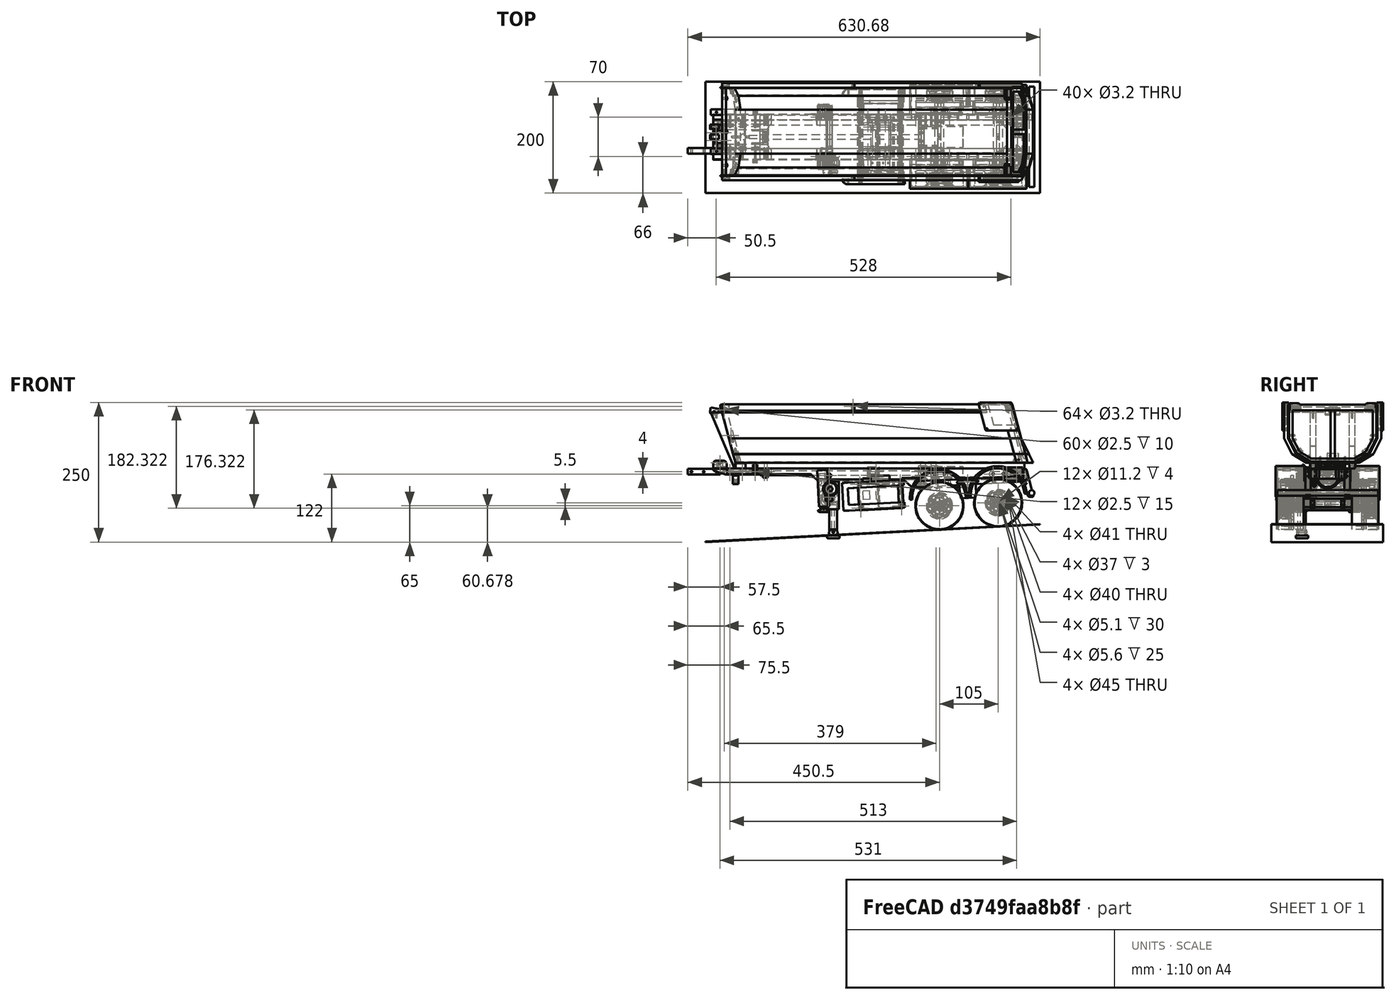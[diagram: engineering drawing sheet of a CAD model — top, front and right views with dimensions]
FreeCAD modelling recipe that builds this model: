
FCSTD DOCUMENT  (FreeCAD 0.19R)
Label: trailer-frame
License: CC-BY 3.0
LicenseURL: http://creativecommons.org/licenses/by/3.0/
objects: Part::Cylinder×595, Part::MultiFuse×465, Part::Box×378, Part::Cut×363, Part::Fillet×122, Part::Chamfer×58, Part::Mirroring×20, Part::Feature×19, Part::Extrusion×10, App::DocumentObjectGroup×8, Part::RegularPolygon×4, Part::Cone×4, Part::Compound×2, Mesh::Feature×1
note: 2040 computed .brp shape members not serialized (recipe doc carries the construction recipe); baked Part::Feature solids carry a one-line shape summary decoded from their .brp

FEATURE [Part::Box] Box
  AttacherType = Attacher::AttachEngine3D
  Height = 20
  Length = 600
  Placement = pos=(0,0,0) rot=(0,1,0;0.05236rad)
  Width = 10
FEATURE [Part::Box] Box001
  AttacherType = Attacher::AttachEngine3D
  Height = 20
  Length = 600
  Placement = pos=(0,52,0) rot=(0,1,0;0.05236rad)
  Width = 10
FEATURE [Part::MultiFuse] Fusion
  Refine = true
  Shapes = -> [Box001,Box]
FEATURE [Part::Fillet] Fillet
  Base = -> Fusion
  Edges = 4 edges r=3: [Edge8,Edge10,Edge17,Edge19]
FEATURE [Part::Box] Box002
  AttacherType = Attacher::AttachEngine3D
  Height = 17
  Length = 200
  Placement = pos=(399,0,-35) rot=(0,0,1;0rad)
  Width = 10
FEATURE [Part::Box] Box003
  AttacherType = Attacher::AttachEngine3D
  Height = 27
  Length = 14
  Placement = pos=(400,0,-35) rot=(0,-1,0;0.785398rad)
  Width = 10
FEATURE [Part::MultiFuse] Fusion001
  Refine = true
  Shapes = -> [Box002,Box003]
FEATURE [Part::MultiFuse] Fusion002
  Refine = true
  Shapes = -> [Box001,Box]
FEATURE [Part::Fillet] Fillet001
  Base = -> Fusion002
  Edges = 4 edges r=3: [Edge8,Edge10,Edge17,Edge19]
FEATURE [Part::Box] Box004
  AttacherType = Attacher::AttachEngine3D
  Height = 27
  Length = 14
  Placement = pos=(400,0,-35) rot=(0,-1,0;0.785398rad)
  Width = 10
FEATURE [Part::Box] Box005
  AttacherType = Attacher::AttachEngine3D
  Height = 17
  Length = 200
  Placement = pos=(399,0,-35) rot=(0,0,1;0rad)
  Width = 10
FEATURE [Part::MultiFuse] Fusion003
  Placement = pos=(0,52,0) rot=(0,0,1;0rad)
  Refine = true
  Shapes = -> [Box005,Box004]
FEATURE [Part::Box] Box006
  AttacherType = Attacher::AttachEngine3D
  Height = 10
  Length = 150
  Placement = pos=(0,0,0) rot=(0,1,0;0.05236rad)
  Width = 62
FEATURE [Part::Box] Box007
  AttacherType = Attacher::AttachEngine3D
  Height = 10
  Length = 20
  Placement = pos=(143.2,0,-4.8) rot=(0,1,0;0.785398rad)
  Width = 62
FEATURE [Part::MultiFuse] Fusion005
  Refine = true
  Shapes = -> [Box007,Box006]
FEATURE [Part::Cut] Cut001
  Base = -> Fillet001
  Placement = pos=(0,0,0) rot=(0,-1,0;0.05236rad)
  Refine = true
  Tool = -> Fusion005
FEATURE [Part::Box] Box008
  AttacherType = Attacher::AttachEngine3D
  Height = 10
  Length = 60
  Placement = pos=(0,1,9) rot=(0,0,1;0rad)
  Width = 60
FEATURE [Part::Cylinder] Cylinder
  Angle = 360
  AttacherType = Attacher::AttachEngine3D
  Height = 19
  Placement = pos=(30,31,6) rot=(0,0,1;0rad)
  Radius = 5
FEATURE [Part::Cylinder] Cylinder001
  Angle = 360
  AttacherType = Attacher::AttachEngine3D
  Height = 51
  Placement = pos=(10,31,10) rot=(0,1,0;1.5708rad)
  Radius = 1.4
FEATURE [Part::Cylinder] Cylinder002
  Angle = 360
  AttacherType = Attacher::AttachEngine3D
  Height = 41
  Placement = pos=(20,31,10) rot=(0,1,0;1.5708rad)
  Radius = 1.6
FEATURE [Part::Cylinder] Cylinder003
  Angle = 360
  AttacherType = Attacher::AttachEngine3D
  Height = 20
  Placement = pos=(41,31,10) rot=(0,1,0;1.5708rad)
  Radius = 2.6
FEATURE [Mesh::Feature] frame_holes  label="frame-holes"
  Placement = pos=(59.5,8,-19) rot=(1,0,0;1.5708rad)
FEATURE [Part::Cylinder] Cylinder004
  Angle = 360
  AttacherType = Attacher::AttachEngine3D
  Height = 15
  Placement = pos=(51,15,14) rot=(1,0,0;1.5708rad)
  Radius = 1.25
FEATURE [Part::Cylinder] Cylinder005
  Angle = 360
  AttacherType = Attacher::AttachEngine3D
  Height = 15
  Placement = pos=(6,15,14) rot=(1,0,0;1.5708rad)
  Radius = 1.25
FEATURE [Part::Cylinder] Cylinder006
  Angle = 360
  AttacherType = Attacher::AttachEngine3D
  Height = 15
  Placement = pos=(28,15,14) rot=(1,0,0;1.5708rad)
  Radius = 1.25
FEATURE [Part::MultiFuse] Fusion007
  Refine = true
  Shapes = -> [Cylinder004,Cylinder005,Cylinder006]
FEATURE [Part::Cylinder] Cylinder007
  Angle = 360
  AttacherType = Attacher::AttachEngine3D
  Height = 15
  Placement = pos=(28,15,14) rot=(1,0,0;1.5708rad)
  Radius = 1.25
FEATURE [Part::Cylinder] Cylinder008
  Angle = 360
  AttacherType = Attacher::AttachEngine3D
  Height = 15
  Placement = pos=(6,15,14) rot=(1,0,0;1.5708rad)
  Radius = 1.25
FEATURE [Part::Cylinder] Cylinder009
  Angle = 360
  AttacherType = Attacher::AttachEngine3D
  Height = 15
  Placement = pos=(51,15,14) rot=(1,0,0;1.5708rad)
  Radius = 1.25
FEATURE [Part::MultiFuse] Fusion008
  Placement = pos=(0,47,0) rot=(0,0,1;0rad)
  Refine = true
  Shapes = -> [Cylinder009,Cylinder008,Cylinder007]
FEATURE [Part::MultiFuse] Fusion009
  Refine = true
  Shapes = -> [Fusion007,Fusion008]
FEATURE [Part::MultiFuse] Fusion010
  Refine = true
  Shapes = -> [Box001,Box]
FEATURE [Part::Fillet] Fillet004
  Base = -> Fusion010
  Edges = 4 edges r=3: [Edge8,Edge10,Edge17,Edge19]
FEATURE [Part::Cut] Cut
  Base = -> Fusion001
  Placement = pos=(0,0,0) rot=(0,-1,0;0.05236rad)
  Refine = true
  Tool = -> Fillet
FEATURE [Part::Cut] Cut006
  Base = -> Fusion003
  Placement = pos=(0,0,0) rot=(0,-1,0;0.05236rad)
  Refine = true
  Tool = -> Fillet004
FEATURE [Part::Box] Box010
  AttacherType = Attacher::AttachEngine3D
  Height = 18
  Length = 600
  Placement = pos=(0,1,1) rot=(0,0,1;0rad)
  Width = 10
FEATURE [Part::Box] Box011
  AttacherType = Attacher::AttachEngine3D
  Height = 18
  Length = 600
  Placement = pos=(0,51,1) rot=(0,0,1;0rad)
  Width = 10
FEATURE [Part::Fillet] Fillet005
  Base = -> Box011
  Edges = 2 edges r=2: [Edge11,Edge12]
FEATURE [Part::Fillet] Fillet006
  Base = -> Box010
  Edges = 2 edges r=2: [Edge9,Edge10]
FEATURE [Part::MultiFuse] Fusion011
  Refine = true
  Shapes = -> [Fillet005,Fillet006]
FEATURE [Part::Cut] Cut007
  Base = -> Cut001
  Refine = true
  Tool = -> Fusion011
FEATURE [Part::Cylinder] Cylinder010
  Angle = 360
  AttacherType = Attacher::AttachEngine3D
  Height = 30
  Placement = pos=(578,6,-35) rot=(0,0,1;0rad)
  Radius = 1.6
FEATURE [Part::Cylinder] Cylinder011
  Angle = 360
  AttacherType = Attacher::AttachEngine3D
  Height = 3
  Placement = pos=(578,6,-35) rot=(0,0,1;0rad)
  Radius = 3.2
FEATURE [Part::MultiFuse] Fusion012
  Placement = pos=(0,0,30) rot=(0,0,1;0rad)
  Refine = true
  Shapes = -> [Cylinder010,Cylinder011]
FEATURE [Part::Cylinder] Cylinder012
  Angle = 360
  AttacherType = Attacher::AttachEngine3D
  Height = 3
  Placement = pos=(578,6,-35) rot=(0,0,1;0rad)
  Radius = 3.2
FEATURE [Part::Cylinder] Cylinder013
  Angle = 360
  AttacherType = Attacher::AttachEngine3D
  Height = 30
  Placement = pos=(578,6,-35) rot=(0,0,1;0rad)
  Radius = 1.6
FEATURE [Part::MultiFuse] Fusion013
  Placement = pos=(-170,0,21.1) rot=(0,0,1;0rad)
  Refine = true
  Shapes = -> [Cylinder013,Cylinder012]
FEATURE [Part::Cylinder] Cylinder014
  Angle = 360
  AttacherType = Attacher::AttachEngine3D
  Height = 3
  Placement = pos=(578,6,-35) rot=(0,0,1;0rad)
  Radius = 3.2
FEATURE [Part::Cylinder] Cylinder015
  Angle = 360
  AttacherType = Attacher::AttachEngine3D
  Height = 30
  Placement = pos=(578,6,-35) rot=(0,0,1;0rad)
  Radius = 1.6
FEATURE [Part::MultiFuse] Fusion014
  Placement = pos=(-110,0,24.3) rot=(0,0,1;0rad)
  Refine = true
  Shapes = -> [Cylinder015,Cylinder014]
FEATURE [Part::Cylinder] Cylinder016
  Angle = 360
  AttacherType = Attacher::AttachEngine3D
  Height = 3
  Placement = pos=(578,6,-35) rot=(0,0,1;0rad)
  Radius = 3.2
FEATURE [Part::Cylinder] Cylinder017
  Angle = 360
  AttacherType = Attacher::AttachEngine3D
  Height = 30
  Placement = pos=(578,6,-35) rot=(0,0,1;0rad)
  Radius = 1.6
FEATURE [Part::MultiFuse] Fusion015
  Placement = pos=(-30,0,28.5) rot=(0,0,1;0rad)
  Refine = true
  Shapes = -> [Cylinder017,Cylinder016]
FEATURE [Part::Cylinder] Cylinder018
  Angle = 360
  AttacherType = Attacher::AttachEngine3D
  Height = 3
  Placement = pos=(578,6,-35) rot=(0,0,1;0rad)
  Radius = 3.2
FEATURE [Part::Cylinder] Cylinder019
  Angle = 360
  AttacherType = Attacher::AttachEngine3D
  Height = 30
  Placement = pos=(578,6,-35) rot=(0,0,1;0rad)
  Radius = 1.6
FEATURE [Part::MultiFuse] Fusion016
  Placement = pos=(0,50,30) rot=(0,0,1;0rad)
  Refine = true
  Shapes = -> [Cylinder019,Cylinder018]
FEATURE [Part::Cylinder] Cylinder020
  Angle = 360
  AttacherType = Attacher::AttachEngine3D
  Height = 3
  Placement = pos=(578,6,-35) rot=(0,0,1;0rad)
  Radius = 3.2
FEATURE [Part::Cylinder] Cylinder021
  Angle = 360
  AttacherType = Attacher::AttachEngine3D
  Height = 30
  Placement = pos=(578,6,-35) rot=(0,0,1;0rad)
  Radius = 1.6
FEATURE [Part::MultiFuse] Fusion017
  Placement = pos=(-170,50,21.1) rot=(0,0,1;0rad)
  Refine = true
  Shapes = -> [Cylinder021,Cylinder020]
FEATURE [Part::Cylinder] Cylinder022
  Angle = 360
  AttacherType = Attacher::AttachEngine3D
  Height = 3
  Placement = pos=(578,6,-35) rot=(0,0,1;0rad)
  Radius = 3.2
FEATURE [Part::Cylinder] Cylinder023
  Angle = 360
  AttacherType = Attacher::AttachEngine3D
  Height = 30
  Placement = pos=(578,6,-35) rot=(0,0,1;0rad)
  Radius = 1.6
FEATURE [Part::MultiFuse] Fusion018
  Placement = pos=(-110,50,24.3) rot=(0,0,1;0rad)
  Refine = true
  Shapes = -> [Cylinder023,Cylinder022]
FEATURE [Part::Cylinder] Cylinder024
  Angle = 360
  AttacherType = Attacher::AttachEngine3D
  Height = 3
  Placement = pos=(578,6,-35) rot=(0,0,1;0rad)
  Radius = 3.2
FEATURE [Part::Cylinder] Cylinder025
  Angle = 360
  AttacherType = Attacher::AttachEngine3D
  Height = 30
  Placement = pos=(578,6,-35) rot=(0,0,1;0rad)
  Radius = 1.6
FEATURE [Part::MultiFuse] Fusion019
  Placement = pos=(-30,50,28.5) rot=(0,0,1;0rad)
  Refine = true
  Shapes = -> [Cylinder025,Cylinder024]
FEATURE [Part::Box] Box012
  AttacherType = Attacher::AttachEngine3D
  Height = 32
  Length = 10
  Placement = pos=(600,0,-3.6) rot=(0,-1,0;0.05236rad)
  Width = 62
FEATURE [Part::Cut] Cut010  label="frame_"
  Base = -> Cut007
  Refine = true
  Tool = -> Box012
FEATURE [Part::Box] Box013
  AttacherType = Attacher::AttachEngine3D
  Height = 17
  Length = 20
  Placement = pos=(580,0,1.5) rot=(0,0,1;0rad)
  Width = 10
FEATURE [Part::Box] Box014
  AttacherType = Attacher::AttachEngine3D
  Height = 32
  Length = 10
  Placement = pos=(600,0,-3.6) rot=(0,-1,0;0.05236rad)
  Width = 62
FEATURE [Part::Cut] Cut011
  Base = -> Box013
  Placement = pos=(0,1,0) rot=(0,0,1;0rad)
  Refine = true
  Tool = -> Box014
FEATURE [Part::Box] Box015
  AttacherType = Attacher::AttachEngine3D
  Height = 32
  Length = 10
  Placement = pos=(600,0,-3.6) rot=(0,-1,0;0.05236rad)
  Width = 62
FEATURE [Part::Box] Box016
  AttacherType = Attacher::AttachEngine3D
  Height = 17
  Length = 20
  Placement = pos=(580,0,1.5) rot=(0,0,1;0rad)
  Width = 10
FEATURE [Part::Cut] Cut012
  Base = -> Box016
  Placement = pos=(0,51,0) rot=(0,0,1;0rad)
  Refine = true
  Tool = -> Box015
FEATURE [Part::Box] Box017
  AttacherType = Attacher::AttachEngine3D
  Height = 17
  Length = 10
  Placement = pos=(580,11,1.5) rot=(0,0,1;0rad)
  Width = 40
FEATURE [Part::MultiFuse] Fusion022
  Refine = true
  Shapes = -> [Cut011,Cut012,Box017]
FEATURE [Part::Chamfer] Chamfer
  Base = -> Fusion022
  Edges = 1 edges r=5: [Edge15]
FEATURE [Part::Chamfer] Chamfer001
  Base = -> Chamfer
  Edges = 1 edges r=5: [Edge23]
FEATURE [Part::Fillet] Fillet007
  Base = -> Chamfer001
  Edges = 2 edges r=3: [Edge8,Edge26]
FEATURE [Part::Fillet] Fillet008
  Base = -> Fillet007
  Edges = 2 edges r=3: [Edge6,Edge27]
FEATURE [Part::Cylinder] Cylinder026
  Angle = 360
  AttacherType = Attacher::AttachEngine3D
  Height = 22
  Placement = pos=(0,0,0) rot=(1,0,0;1.5708rad)
  Radius = 42
FEATURE [Part::Cylinder] Cylinder027
  Angle = 360
  AttacherType = Attacher::AttachEngine3D
  Height = 22
  Placement = pos=(0,-26,0) rot=(1,0,0;1.5708rad)
  Radius = 42
FEATURE [Part::MultiFuse] Fusion023
  Refine = true
  Shapes = -> [Cylinder026,Cylinder027]
FEATURE [Part::Cylinder] Cylinder028
  Angle = 360
  AttacherType = Attacher::AttachEngine3D
  Height = 22
  Placement = pos=(0,-26,0) rot=(1,0,0;1.5708rad)
  Radius = 42
FEATURE [Part::Cylinder] Cylinder029
  Angle = 360
  AttacherType = Attacher::AttachEngine3D
  Height = 22
  Placement = pos=(0,0,0) rot=(1,0,0;1.5708rad)
  Radius = 42
FEATURE [Part::MultiFuse] Fusion024
  Placement = pos=(105,0,0) rot=(0,0,1;0rad)
  Refine = true
  Shapes = -> [Cylinder029,Cylinder028]
FEATURE [Part::MultiFuse] Fusion025  label="wheels_"
  Placement = pos=(450,-12,-47) rot=(0,-1,0;0.05236rad)
  Refine = true
  Shapes = -> [Fusion024,Fusion023]
FEATURE [Part::Cylinder] Cylinder030
  Angle = 360
  AttacherType = Attacher::AttachEngine3D
  Height = 100
  Placement = pos=(400,0,0) rot=(1,0,0;1.5708rad)
  Radius = 1.25
FEATURE [Part::Cylinder] Cylinder031
  Angle = 360
  AttacherType = Attacher::AttachEngine3D
  Height = 100
  Placement = pos=(418,0,0) rot=(1,0,0;1.5708rad)
  Radius = 1.6
FEATURE [Part::Cylinder] Cylinder032
  Angle = 360
  AttacherType = Attacher::AttachEngine3D
  Height = 100
  Placement = pos=(436,0,0) rot=(1,0,0;1.5708rad)
  Radius = 1.25
FEATURE [Part::MultiFuse] Fusion026
  Placement = pos=(83,77,-26) rot=(0,-1,0;0.05236rad)
  Refine = true
  Shapes = -> [Cylinder030,Cylinder031,Cylinder032]
FEATURE [Part::Cylinder] Cylinder033
  Angle = 360
  AttacherType = Attacher::AttachEngine3D
  Height = 100
  Placement = pos=(418,0,0) rot=(1,0,0;1.5708rad)
  Radius = 1.6
FEATURE [Part::Cylinder] Cylinder034
  Angle = 360
  AttacherType = Attacher::AttachEngine3D
  Height = 100
  Placement = pos=(436,0,0) rot=(1,0,0;1.5708rad)
  Radius = 1.25
FEATURE [Part::Cylinder] Cylinder035
  Angle = 360
  AttacherType = Attacher::AttachEngine3D
  Height = 100
  Placement = pos=(400,0,0) rot=(1,0,0;1.5708rad)
  Radius = 1.25
FEATURE [Part::MultiFuse] Fusion027
  Placement = pos=(83,77,-26) rot=(0,-1,0;0.05236rad)
  Refine = true
  Shapes = -> [Cylinder035,Cylinder033,Cylinder034]
FEATURE [Part::Cylinder] Cylinder036
  Angle = 360
  AttacherType = Attacher::AttachEngine3D
  Height = 15
  Placement = pos=(588,16,10) rot=(1,0,0;1.5708rad)
  Radius = 1.25
FEATURE [Part::Cylinder] Cylinder037
  Angle = 360
  AttacherType = Attacher::AttachEngine3D
  Height = 15
  Placement = pos=(588,61,10) rot=(1,0,0;1.5708rad)
  Radius = 1.25
FEATURE [Part::MultiFuse] Fusion028
  Refine = true
  Shapes = -> [Cylinder036,Cylinder037]
FEATURE [Part::Cut] Cut015
  Base = -> Fillet008
  Refine = true
  Tool = -> Fusion028
FEATURE [Part::Cylinder] Cylinder038
  Angle = 360
  AttacherType = Attacher::AttachEngine3D
  Height = 15
  Placement = pos=(585,7,14) rot=(0,1,0;1.5708rad)
  Radius = 1.25
FEATURE [Part::Cylinder] Cylinder039
  Angle = 360
  AttacherType = Attacher::AttachEngine3D
  Height = 15
  Placement = pos=(585,7,6) rot=(0,1,0;1.5708rad)
  Radius = 1.25
FEATURE [Part::MultiFuse] Fusion029
  Refine = true
  Shapes = -> [Cylinder038,Cylinder039]
FEATURE [Part::Cylinder] Cylinder040
  Angle = 360
  AttacherType = Attacher::AttachEngine3D
  Height = 15
  Placement = pos=(585,7,14) rot=(0,1,0;1.5708rad)
  Radius = 1.25
FEATURE [Part::Cylinder] Cylinder041
  Angle = 360
  AttacherType = Attacher::AttachEngine3D
  Height = 15
  Placement = pos=(585,7,6) rot=(0,1,0;1.5708rad)
  Radius = 1.25
FEATURE [Part::MultiFuse] Fusion030
  Placement = pos=(0,48,0) rot=(0,0,1;0rad)
  Refine = true
  Shapes = -> [Cylinder040,Cylinder041]
FEATURE [Part::MultiFuse] Fusion031
  Refine = true
  Shapes = -> [Fusion029,Fusion030]
FEATURE [Part::Cut] Cut016
  Base = -> Cut015
  Refine = true
  Tool = -> Fusion031
FEATURE [Part::Box] Box018
  AttacherType = Attacher::AttachEngine3D
  Height = 5
  Length = 3
  Placement = pos=(580,4,1.5) rot=(0,0,1;0rad)
  Width = 4
FEATURE [Part::Box] Box019
  AttacherType = Attacher::AttachEngine3D
  Height = 5
  Length = 3
  Placement = pos=(580,54,1.5) rot=(0,0,1;0rad)
  Width = 4
FEATURE [Part::MultiFuse] Fusion032
  Refine = true
  Shapes = -> [Box019,Box018]
FEATURE [Part::Cut] Cut017  label="rear-cross-member_"
  Base = -> Cut016
  Refine = true
  Tool = -> Fusion032
FEATURE [Part::Box] Box020
  AttacherType = Attacher::AttachEngine3D
  Height = 10
  Length = 58
  Placement = pos=(0,0,9) rot=(0,0,1;0rad)
  Width = 10
FEATURE [Part::Fillet] Fillet009
  Base = -> Box020
  Edges = 1 edges r=3: [Edge10]
  Placement = pos=(-0.5,1,0) rot=(0,0,1;0rad)
FEATURE [Part::Cylinder] Cylinder042
  Angle = 360
  AttacherType = Attacher::AttachEngine3D
  Height = 10
  Placement = pos=(6,11,14) rot=(1,0,0;1.5708rad)
  Radius = 1.5
FEATURE [Part::Cylinder] Cylinder043
  Angle = 360
  AttacherType = Attacher::AttachEngine3D
  Height = 10
  Placement = pos=(28,11,14) rot=(1,0,0;1.5708rad)
  Radius = 1.5
FEATURE [Part::Cylinder] Cylinder044
  Angle = 360
  AttacherType = Attacher::AttachEngine3D
  Height = 10
  Placement = pos=(51,11,14) rot=(1,0,0;1.5708rad)
  Radius = 1.5
FEATURE [Part::MultiFuse] Fusion033
  Refine = true
  Shapes = -> [Cylinder042,Cylinder043,Cylinder044]
FEATURE [Part::Cut] Cut018  label="frame-holes001"
  Base = -> Fillet009
  Refine = true
  Tool = -> Fusion033
FEATURE [Part::MultiFuse] Fusion034
  Refine = true
  Shapes = -> [Fusion016,Fusion017,Fusion018,Fusion019]
FEATURE [Part::Cut] Cut019
  Base = -> Cut006
  Refine = true
  Tool = -> Fusion034
FEATURE [Part::Cut] Cut020  label="right-wheels-frame"
  Base = -> Cut019
  Placement = pos=(0,10,0) rot=(0,0,1;0rad)
  Refine = true
  Tool = -> Fusion026
FEATURE [Part::MultiFuse] Fusion035
  Refine = true
  Shapes = -> [Fusion012,Fusion013,Fusion014,Fusion015]
FEATURE [Part::Cut] Cut021
  Base = -> Cut
  Refine = true
  Tool = -> Fusion035
FEATURE [Part::Cut] Cut022  label="left-wheels-frame"
  Base = -> Cut021
  Placement = pos=(0,-10,0) rot=(0,0,1;0rad)
  Refine = true
  Tool = -> Fusion027
FEATURE [Part::Box] Box021  label="Cube"
  AttacherType = Attacher::AttachEngine3D
  Height = 10
  Length = 10
  Placement = pos=(80,1,9) rot=(0,0,1;0rad)
  Width = 60
FEATURE [Part::Cylinder] Cylinder045
  Angle = 360
  AttacherType = Attacher::AttachEngine3D
  Height = 4
  Placement = pos=(90,31,10) rot=(0,1,0;1.5708rad)
  Radius = 6.5
FEATURE [Part::Cylinder] Cylinder046
  Angle = 360
  AttacherType = Attacher::AttachEngine3D
  Height = 10
  Placement = pos=(80,31,11.5) rot=(0,1,0;1.5708rad)
  Radius = 8
FEATURE [Part::Cylinder] Cylinder047
  Angle = 360
  AttacherType = Attacher::AttachEngine3D
  Height = 4
  Placement = pos=(89.5,31,10) rot=(0,1,0;1.5708rad)
  Radius = 3.5
FEATURE [Part::MultiFuse] Fusion037
  Placement = pos=(-4,0,2) rot=(0,0,1;0rad)
  Refine = true
  Shapes = -> [Cylinder045,Cylinder047]
FEATURE [Part::MultiFuse] Fusion038
  Refine = true
  Shapes = -> [Box021,Cylinder046]
FEATURE [Part::Cylinder] Cylinder048
  Angle = 360
  AttacherType = Attacher::AttachEngine3D
  Height = 350
  Placement = pos=(48,31,12) rot=(0,1,0;1.5708rad)
  Radius = 4
FEATURE [Part::Cylinder] Cylinder049
  Angle = 360
  AttacherType = Attacher::AttachEngine3D
  Height = 75
  Placement = pos=(336,31,5) rot=(0,1,0;1.5708rad)
  Radius = 18.5
FEATURE [Part::Box] Box022  label="Cube001"
  AttacherType = Attacher::AttachEngine3D
  Height = 17
  Length = 34
  Placement = pos=(326,1,1.5) rot=(0,0,1;0rad)
  Width = 60
FEATURE [Part::Cylinder] Cylinder050
  Angle = 360
  AttacherType = Attacher::AttachEngine3D
  Height = 34
  Placement = pos=(326,31,4.5) rot=(0,1,0;1.5708rad)
  Radius = 20.5
FEATURE [Part::Cylinder] Cylinder051
  Angle = 360
  AttacherType = Attacher::AttachEngine3D
  Height = 10
  Placement = pos=(327,31,12) rot=(0,1,0;1.5708rad)
  Radius = 7
FEATURE [Part::Cylinder] Cylinder052
  Angle = 360
  AttacherType = Attacher::AttachEngine3D
  Height = 75
  Placement = pos=(336,31,5) rot=(0,1,0;1.5708rad)
  Radius = 18.7
FEATURE [Part::MultiFuse] Fusion039
  Placement = pos=(1,0,0) rot=(0,0,1;0rad)
  Refine = true
  Shapes = -> [Box022,Cylinder050]
FEATURE [Part::Cut] Cut024
  Base = -> Fusion039
  Refine = true
  Tool = -> Cylinder051
FEATURE [Part::Cut] Cut025
  Base = -> Cut024
  Refine = true
  Tool = -> Cylinder052
FEATURE [Part::Cylinder] Cylinder053
  Angle = 360
  AttacherType = Attacher::AttachEngine3D
  Height = 10
  Placement = pos=(15.5,0,0) rot=(0,0,1;0rad)
  Radius = 1.6
FEATURE [Part::Cylinder] Cylinder054
  Angle = 360
  AttacherType = Attacher::AttachEngine3D
  Height = 10
  Placement = pos=(-15.5,0,0) rot=(0,0,1;0rad)
  Radius = 1.6
FEATURE [Part::MultiFuse] Fusion041
  Placement = pos=(0,0,0) rot=(0,0,1;1.0472rad)
  Refine = true
  Shapes = -> [Cylinder054,Cylinder053]
FEATURE [Part::Cylinder] Cylinder055
  Angle = 360
  AttacherType = Attacher::AttachEngine3D
  Height = 10
  Placement = pos=(15.5,0,0) rot=(0,0,1;0rad)
  Radius = 1.6
FEATURE [Part::Cylinder] Cylinder056
  Angle = 360
  AttacherType = Attacher::AttachEngine3D
  Height = 10
  Placement = pos=(-15.5,0,0) rot=(0,0,1;0rad)
  Radius = 1.6
FEATURE [Part::MultiFuse] Fusion042
  Placement = pos=(0,0,0) rot=(0,0,1;2.0944rad)
  Refine = true
  Shapes = -> [Cylinder056,Cylinder055]
FEATURE [Part::Cylinder] Cylinder057
  Angle = 360
  AttacherType = Attacher::AttachEngine3D
  Height = 10
  Placement = pos=(-15.5,0,0) rot=(0,0,1;0rad)
  Radius = 1.6
FEATURE [Part::Cylinder] Cylinder058
  Angle = 360
  AttacherType = Attacher::AttachEngine3D
  Height = 10
  Placement = pos=(15.5,0,0) rot=(0,0,1;0rad)
  Radius = 1.6
FEATURE [Part::MultiFuse] Fusion043
  Refine = true
  Shapes = -> [Cylinder057,Cylinder058]
FEATURE [Part::MultiFuse] Fusion044
  Placement = pos=(0,0,0) rot=(0,0,1;0.523599rad)
  Refine = true
  Shapes = -> [Fusion041,Fusion042,Fusion043]
FEATURE [Part::Box] Box023  label="Cube002"
  AttacherType = Attacher::AttachEngine3D
  Height = 10
  Length = 10
  Width = 10
FEATURE [Part::Cut] Cut026  label="holes"
  Base = -> Fusion044
  Placement = pos=(327,31,5) rot=(0,1,0;1.5708rad)
  Refine = true
  Tool = -> Box023
FEATURE [Part::Cut] Cut027
  Base = -> Cut025
  Refine = true
  Tool = -> Cut026
FEATURE [Part::Cylinder] Cylinder059
  Angle = 360
  AttacherType = Attacher::AttachEngine3D
  Height = 10
  Placement = pos=(82.5,11,14) rot=(1,0,0;1.5708rad)
  Radius = 1.25
FEATURE [Part::Cylinder] Cylinder060
  Angle = 360
  AttacherType = Attacher::AttachEngine3D
  Height = 10
  Placement = pos=(87.5,11,14) rot=(1,0,0;1.5708rad)
  Radius = 1.25
FEATURE [Part::Cylinder] Cylinder061
  Angle = 360
  AttacherType = Attacher::AttachEngine3D
  Height = 10
  Placement = pos=(82.5,61,14) rot=(1,0,0;1.5708rad)
  Radius = 1.25
FEATURE [Part::Cylinder] Cylinder062
  Angle = 360
  AttacherType = Attacher::AttachEngine3D
  Height = 10
  Placement = pos=(87.5,61,14) rot=(1,0,0;1.5708rad)
  Radius = 1.25
FEATURE [Part::MultiFuse] Fusion045
  Refine = true
  Shapes = -> [Cylinder059,Cylinder061]
FEATURE [Part::MultiFuse] Fusion046
  Refine = true
  Shapes = -> [Cylinder060,Cylinder062]
FEATURE [Part::Cylinder] Cylinder063
  Angle = 360
  AttacherType = Attacher::AttachEngine3D
  Height = 10
  Placement = pos=(87.5,61,14) rot=(1,0,0;1.5708rad)
  Radius = 1.25
FEATURE [Part::Cylinder] Cylinder064
  Angle = 360
  AttacherType = Attacher::AttachEngine3D
  Height = 10
  Placement = pos=(87.5,11,14) rot=(1,0,0;1.5708rad)
  Radius = 1.25
FEATURE [Part::MultiFuse] Fusion048
  Refine = true
  Shapes = -> [Fusion045,Fusion046]
FEATURE [Part::MultiFuse] Fusion049
  Placement = pos=(242.5,0,0) rot=(0,0,1;0rad)
  Refine = true
  Shapes = -> [Cylinder064,Cylinder063]
FEATURE [Part::Cylinder] Cylinder065
  Angle = 360
  AttacherType = Attacher::AttachEngine3D
  Height = 10
  Placement = pos=(87.5,61,14) rot=(1,0,0;1.5708rad)
  Radius = 1.25
FEATURE [Part::Cylinder] Cylinder066
  Angle = 360
  AttacherType = Attacher::AttachEngine3D
  Height = 10
  Placement = pos=(87.5,11,14) rot=(1,0,0;1.5708rad)
  Radius = 1.25
FEATURE [Part::MultiFuse] Fusion050
  Placement = pos=(251.5,0,0) rot=(0,0,1;0rad)
  Refine = true
  Shapes = -> [Cylinder066,Cylinder065]
FEATURE [Part::Cylinder] Cylinder067
  Angle = 360
  AttacherType = Attacher::AttachEngine3D
  Height = 10
  Placement = pos=(87.5,61,14) rot=(1,0,0;1.5708rad)
  Radius = 1.25
FEATURE [Part::Cylinder] Cylinder068
  Angle = 360
  AttacherType = Attacher::AttachEngine3D
  Height = 10
  Placement = pos=(87.5,11,14) rot=(1,0,0;1.5708rad)
  Radius = 1.25
FEATURE [Part::MultiFuse] Fusion051
  Placement = pos=(261.5,0,0) rot=(0,0,1;0rad)
  Refine = true
  Shapes = -> [Cylinder068,Cylinder067]
FEATURE [Part::Cylinder] Cylinder069
  Angle = 360
  AttacherType = Attacher::AttachEngine3D
  Height = 10
  Placement = pos=(87.5,11,14) rot=(1,0,0;1.5708rad)
  Radius = 1.25
FEATURE [Part::Cylinder] Cylinder070
  Angle = 360
  AttacherType = Attacher::AttachEngine3D
  Height = 10
  Placement = pos=(87.5,61,14) rot=(1,0,0;1.5708rad)
  Radius = 1.25
FEATURE [Part::MultiFuse] Fusion052
  Placement = pos=(270.5,0,0) rot=(0,0,1;0rad)
  Refine = true
  Shapes = -> [Cylinder069,Cylinder070]
FEATURE [Part::MultiFuse] Fusion053
  Refine = true
  Shapes = -> [Fusion049,Fusion050,Fusion051,Fusion052]
FEATURE [Part::MultiFuse] Fusion055
  Placement = pos=(270.5,0,0) rot=(0,0,1;0rad)
  Refine = true
  Shapes = -> [Cylinder069,Cylinder070]
FEATURE [Part::MultiFuse] Fusion056
  Placement = pos=(251.5,0,0) rot=(0,0,1;0rad)
  Refine = true
  Shapes = -> [Cylinder066,Cylinder065]
FEATURE [Part::MultiFuse] Fusion057
  Placement = pos=(261.5,0,0) rot=(0,0,1;0rad)
  Refine = true
  Shapes = -> [Cylinder068,Cylinder067]
FEATURE [Part::MultiFuse] Fusion058
  Placement = pos=(242.5,0,0) rot=(0,0,1;0rad)
  Refine = true
  Shapes = -> [Cylinder064,Cylinder063]
FEATURE [Part::MultiFuse] Fusion054
  Placement = pos=(0,0,-8) rot=(0,0,1;0rad)
  Refine = true
  Shapes = -> [Fusion058,Fusion056,Fusion057,Fusion055]
FEATURE [Part::MultiFuse] Fusion059
  Refine = true
  Shapes = -> [Fusion053,Fusion054]
FEATURE [Part::MultiFuse] Fusion060
  Refine = true
  Shapes = -> [Cylinder060,Cylinder062]
FEATURE [Part::MultiFuse] Fusion062
  Refine = true
  Shapes = -> [Cylinder059,Cylinder061]
FEATURE [Part::MultiFuse] Fusion061
  Placement = pos=(0,-10,0) rot=(0,0,1;0rad)
  Refine = true
  Shapes = -> [Fusion062,Fusion060]
FEATURE [Part::MultiFuse] Fusion064
  Refine = true
  Shapes = -> [Fusion049,Fusion050,Fusion051,Fusion052]
FEATURE [Part::MultiFuse] Fusion065
  Placement = pos=(0,0,-8) rot=(0,0,1;0rad)
  Refine = true
  Shapes = -> [Fusion058,Fusion056,Fusion057,Fusion055]
FEATURE [Part::MultiFuse] Fusion063
  Placement = pos=(0,-10,0) rot=(0,0,1;0rad)
  Refine = true
  Shapes = -> [Fusion064,Fusion065]
FEATURE [Part::Box] Box024  label="Cube003"
  AttacherType = Attacher::AttachEngine3D
  Height = 5
  Length = 10
  Placement = pos=(0,-10,-5) rot=(0,0,1;0rad)
  Width = 15
FEATURE [Part::Box] Box025  label="Cube004"
  AttacherType = Attacher::AttachEngine3D
  Height = 20
  Length = 10
  Placement = pos=(0,-10,0) rot=(0,0,1;0rad)
  Width = 8
FEATURE [Part::Box] Box026  label="Cube005"
  AttacherType = Attacher::AttachEngine3D
  Height = 5
  Length = 10
  Placement = pos=(0,-10,20) rot=(0,0,1;0rad)
  Width = 15
FEATURE [Part::MultiFuse] Fusion066
  Placement = pos=(80,2,0) rot=(0,0,1;0rad)
  Refine = true
  Shapes = -> [Box024,Box025,Box026]
FEATURE [Part::Cut] Cut030
  Base = -> Fusion066
  Placement = pos=(0,-10,0) rot=(1,0,0;1.5708rad)
  Refine = true
  Tool = -> Fusion061
FEATURE [Part::Box] Box027  label="Cube006"
  AttacherType = Attacher::AttachEngine3D
  Height = 5
  Length = 34
  Placement = pos=(0,-10,-5) rot=(0,0,1;0rad)
  Width = 15
FEATURE [Part::Box] Box028  label="Cube007"
  AttacherType = Attacher::AttachEngine3D
  Height = 20
  Length = 34
  Placement = pos=(0,-10,0) rot=(0,0,1;0rad)
  Width = 8
FEATURE [Part::Box] Box029  label="Cube008"
  AttacherType = Attacher::AttachEngine3D
  Height = 5
  Length = 34
  Placement = pos=(0,-10,20) rot=(0,0,1;0rad)
  Width = 15
FEATURE [Part::MultiFuse] Fusion067
  Placement = pos=(327,2,0) rot=(0,0,1;0rad)
  Refine = true
  Shapes = -> [Box027,Box028,Box029]
FEATURE [Part::Cut] Cut031
  Base = -> Fusion067
  Placement = pos=(0,-10,0) rot=(1,0,0;1.5708rad)
  Refine = true
  Tool = -> Fusion063
FEATURE [Part::Cylinder] Cylinder071
  Angle = 360
  AttacherType = Attacher::AttachEngine3D
  Height = 10
  Placement = pos=(80,19,14) rot=(0,1,0;1.5708rad)
  Radius = 1.6
FEATURE [Part::Cylinder] Cylinder072
  Angle = 360
  AttacherType = Attacher::AttachEngine3D
  Height = 10
  Placement = pos=(80,43,14) rot=(0,1,0;1.5708rad)
  Radius = 1.6
FEATURE [Part::MultiFuse] Fusion068
  Refine = true
  Shapes = -> [Cylinder071,Cylinder072]
FEATURE [Part::Box] Box030  label="Cube009"
  AttacherType = Attacher::AttachEngine3D
  Height = 22
  Length = 1
  Placement = pos=(89,15,2) rot=(0,0,1;0rad)
  Width = 32
FEATURE [Part::Cut] Cut036  label="motor-support"
  Base = -> Cut027
  Placement = pos=(86,0,0) rot=(0,0,1;0rad)
  Refine = true
  Tool = -> Fusion059
FEATURE [Part::Box] Box031  label="Cube010"
  AttacherType = Attacher::AttachEngine3D
  Height = 5.5
  Length = 15
  Placement = pos=(75,23,3.5) rot=(0,0,1;0rad)
  Width = 16
FEATURE [Part::Box] Box032  label="Cube011"
  AttacherType = Attacher::AttachEngine3D
  Height = 10
  Length = 5
  Placement = pos=(75,1,9) rot=(0,0,1;0rad)
  Width = 60
FEATURE [Part::MultiFuse] Fusion069
  Refine = true
  Shapes = -> [Box032,Box031,Fusion038]
FEATURE [Part::Cut] Cut037
  Base = -> Fusion069
  Refine = true
  Tool = -> Fusion037
FEATURE [Part::Cut] Cut038
  Base = -> Cut037
  Refine = true
  Tool = -> Fusion048
FEATURE [Part::Cut] Cut039
  Base = -> Cut038
  Refine = true
  Tool = -> Fusion068
FEATURE [Part::Cut] Cut040
  Base = -> Cut039
  Refine = true
  Tool = -> Box030
FEATURE [Part::Fillet] Fillet010
  Base = -> Cut040
  Edges = 2 edges r=2: [Edge33,Edge40]
FEATURE [Part::Chamfer] Chamfer002
  Base = -> Fillet010
  Edges = 2 edges r=5.49: [Edge18,Edge45]
FEATURE [Part::Box] Box033  label="Cube012"
  AttacherType = Attacher::AttachEngine3D
  Height = 10
  Length = 5
  Placement = pos=(90,1,9) rot=(0,0,1;0rad)
  Width = 8
FEATURE [Part::Box] Box034  label="Cube013"
  AttacherType = Attacher::AttachEngine3D
  Height = 10
  Length = 5
  Placement = pos=(90,53,9) rot=(0,0,1;0rad)
  Width = 8
FEATURE [Part::Fillet] Fillet011
  Base = -> Box033
  Edges = 1 edges r=2: [Edge10]
FEATURE [Part::Fillet] Fillet012
  Base = -> Box034
  Edges = 1 edges r=2: [Edge12]
FEATURE [Part::MultiFuse] Fusion070
  Refine = true
  Shapes = -> [Chamfer002,Fillet011,Fillet012]
FEATURE [Part::Fillet] Fillet013
  Base = -> Fusion070
  Edges = 2 edges r=4.99: [Edge2,Edge47]
FEATURE [Part::Box] Box035  label="Cube014"
  AttacherType = Attacher::AttachEngine3D
  Height = 10
  Length = 5
  Placement = pos=(75,1,-1) rot=(0,0,1;0rad)
  Width = 60
FEATURE [Part::Cut] Cut041  label="front-threaded-bar-support"
  Base = -> Fillet013
  Placement = pos=(54,0,0) rot=(0,0,1;0rad)
  Refine = true
  Tool = -> Box035
FEATURE [Part::Box] Box036  label="Cube015"
  AttacherType = Attacher::AttachEngine3D
  Height = 50
  Length = 80
  Placement = pos=(0,-29,0) rot=(0,0,1;0rad)
  Width = 130
FEATURE [Part::Box] Box037  label="Cube016"
  AttacherType = Attacher::AttachEngine3D
  Height = 45
  Length = 75
  Placement = pos=(2.5,-24,2.5) rot=(0,0,1;0rad)
  Width = 120
FEATURE [Part::Cut] Cut042
  Base = -> Box036
  Refine = true
  Tool = -> Box037
FEATURE [Part::Box] Box038  label="Cube017"
  AttacherType = Attacher::AttachEngine3D
  Height = 50
  Length = 80
  Placement = pos=(0,96,0) rot=(0,0,1;0rad)
  Width = 5
FEATURE [Part::Cut] Cut043
  Base = -> Cut042
  Refine = true
  Tool = -> Box038
FEATURE [Part::Box] Box039  label="Cube018"
  AttacherType = Attacher::AttachEngine3D
  Height = 50
  Length = 80
  Placement = pos=(0,96,0) rot=(0,0,1;0rad)
  Width = 5
FEATURE [Part::Cylinder] Cylinder073
  Angle = 360
  AttacherType = Attacher::AttachEngine3D
  Height = 125
  Placement = pos=(3.5,96,3.5) rot=(1,0,0;1.5708rad)
  Radius = 3
FEATURE [Part::Cylinder] Cylinder074
  Angle = 360
  AttacherType = Attacher::AttachEngine3D
  Height = 10
  Placement = pos=(3.5,96,3.5) rot=(1,0,0;1.5708rad)
  Radius = 1.25
FEATURE [Part::Cylinder] Cylinder075
  Angle = 360
  AttacherType = Attacher::AttachEngine3D
  Height = 125
  Placement = pos=(76.5,96,3.5) rot=(1,0,0;1.5708rad)
  Radius = 3
FEATURE [Part::Cylinder] Cylinder076
  Angle = 360
  AttacherType = Attacher::AttachEngine3D
  Height = 10
  Placement = pos=(76.5,96,3.5) rot=(1,0,0;1.5708rad)
  Radius = 1.25
FEATURE [Part::Cylinder] Cylinder077
  Angle = 360
  AttacherType = Attacher::AttachEngine3D
  Height = 125
  Placement = pos=(76.5,96,46.5) rot=(1,0,0;1.5708rad)
  Radius = 3
FEATURE [Part::Cylinder] Cylinder078
  Angle = 360
  AttacherType = Attacher::AttachEngine3D
  Height = 10
  Placement = pos=(76.5,96,46.5) rot=(1,0,0;1.5708rad)
  Radius = 1.25
FEATURE [Part::Cylinder] Cylinder079
  Angle = 360
  AttacherType = Attacher::AttachEngine3D
  Height = 125
  Placement = pos=(3.5,96,46.5) rot=(1,0,0;1.5708rad)
  Radius = 3
FEATURE [Part::Cylinder] Cylinder080
  Angle = 360
  AttacherType = Attacher::AttachEngine3D
  Height = 10
  Placement = pos=(3.5,96,46.5) rot=(1,0,0;1.5708rad)
  Radius = 1.25
FEATURE [Part::MultiFuse] Fusion071
  Refine = true
  Shapes = -> [Cylinder073,Cylinder075,Cylinder077,Cylinder079,Cut043]
FEATURE [Part::MultiFuse] Fusion072
  Refine = true
  Shapes = -> [Cylinder074,Cylinder078,Cylinder076,Cylinder080]
FEATURE [Part::Cylinder] Cylinder081
  Angle = 360
  AttacherType = Attacher::AttachEngine3D
  Height = 10
  Placement = pos=(76.5,96,3.5) rot=(1,0,0;1.5708rad)
  Radius = 1.6
FEATURE [Part::Cylinder] Cylinder082
  Angle = 360
  AttacherType = Attacher::AttachEngine3D
  Height = 10
  Placement = pos=(3.5,96,46.5) rot=(1,0,0;1.5708rad)
  Radius = 1.6
FEATURE [Part::Cylinder] Cylinder083
  Angle = 360
  AttacherType = Attacher::AttachEngine3D
  Height = 10
  Placement = pos=(76.5,96,46.5) rot=(1,0,0;1.5708rad)
  Radius = 1.6
FEATURE [Part::Cylinder] Cylinder084
  Angle = 360
  AttacherType = Attacher::AttachEngine3D
  Height = 10
  Placement = pos=(3.5,96,3.5) rot=(1,0,0;1.5708rad)
  Radius = 1.6
FEATURE [Part::MultiFuse] Fusion073
  Placement = pos=(0,5,0) rot=(0,0,1;0rad)
  Refine = true
  Shapes = -> [Cylinder084,Cylinder083,Cylinder081,Cylinder082]
FEATURE [Part::Cut] Cut044
  Base = -> Fusion071
  Refine = true
  Tool = -> Fusion072
FEATURE [Part::Box] Box040  label="battery"
  AttacherType = Attacher::AttachEngine3D
  Height = 35
  Length = 35
  Placement = pos=(342,-28,-50) rot=(0,-1,0;0.05236rad)
  Width = 109
FEATURE [Part::Box] Box041  label="Cube020"
  AttacherType = Attacher::AttachEngine3D
  Height = 50
  Length = 2.5
  Placement = pos=(35,-29,0) rot=(0,0,1;0rad)
  Width = 100
FEATURE [Part::Box] Box042  label="Cube021"
  AttacherType = Attacher::AttachEngine3D
  Height = 11
  Length = 2.5
  Placement = pos=(63,-29,39) rot=(0,0,1;0rad)
  Width = 100
FEATURE [Part::Box] Box043  label="Cube022"
  AttacherType = Attacher::AttachEngine3D
  Height = 2.5
  Length = 6.5
  Placement = pos=(73.5,-29,25) rot=(0,0,1;0rad)
  Width = 100
FEATURE [Part::MultiFuse] Fusion074
  Refine = true
  Shapes = -> [Cut044,Box041,Box042,Box043]
FEATURE [Part::Cylinder] Cylinder085
  Angle = 360
  AttacherType = Attacher::AttachEngine3D
  Height = 10
  Placement = pos=(72,12,41) rot=(0,1,0;1.5708rad)
  Radius = 3
FEATURE [Part::Cut] Cut045
  Base = -> Fusion074
  Refine = true
  Tool = -> Cylinder085
FEATURE [Part::Cylinder] Cylinder086
  Angle = 360
  AttacherType = Attacher::AttachEngine3D
  Height = 10
  Placement = pos=(0,0,11) rot=(0,1,0;1.5708rad)
  Radius = 1.6
FEATURE [Part::Cylinder] Cylinder087
  Angle = 360
  AttacherType = Attacher::AttachEngine3D
  Height = 10
  Placement = pos=(0,0,37) rot=(0,1,0;1.5708rad)
  Radius = 1.6
FEATURE [Part::Cylinder] Cylinder088
  Angle = 360
  AttacherType = Attacher::AttachEngine3D
  Height = 10
  Placement = pos=(0,62,11) rot=(0,1,0;1.5708rad)
  Radius = 1.6
FEATURE [Part::Cylinder] Cylinder089
  Angle = 360
  AttacherType = Attacher::AttachEngine3D
  Height = 10
  Placement = pos=(0,62,37) rot=(0,1,0;1.5708rad)
  Radius = 1.6
FEATURE [Part::MultiFuse] Fusion075
  Refine = true
  Shapes = -> [Cylinder086,Cylinder088,Cylinder089,Cylinder087]
FEATURE [Part::Cut] Cut046
  Base = -> Cut045
  Refine = true
  Tool = -> Fusion075
FEATURE [Part::Cylinder] Cylinder094
  Angle = 360
  AttacherType = Attacher::AttachEngine3D
  Height = 3
  Placement = pos=(3.5,96,3.5) rot=(1,0,0;1.5708rad)
  Radius = 4
FEATURE [Part::Cylinder] Cylinder095
  Angle = 360
  AttacherType = Attacher::AttachEngine3D
  Height = 3
  Placement = pos=(76.5,96,46.5) rot=(1,0,0;1.5708rad)
  Radius = 4
FEATURE [Part::Cylinder] Cylinder096
  Angle = 360
  AttacherType = Attacher::AttachEngine3D
  Height = 3
  Placement = pos=(76.5,96,3.5) rot=(1,0,0;1.5708rad)
  Radius = 4
FEATURE [Part::Cylinder] Cylinder097
  Angle = 360
  AttacherType = Attacher::AttachEngine3D
  Height = 3
  Placement = pos=(3.5,96,46.5) rot=(1,0,0;1.5708rad)
  Radius = 4
FEATURE [Part::MultiFuse] Fusion082
  Placement = pos=(0,5,0) rot=(0,0,1;0rad)
  Refine = true
  Shapes = -> [Cylinder094,Cylinder095,Cylinder096,Cylinder097]
FEATURE [Part::Box] Box044  label="Cube023"
  AttacherType = Attacher::AttachEngine3D
  Height = 10
  Length = 58
  Placement = pos=(308.5,-3,-14.5) rot=(0,-1,0;0.05236rad)
  Width = 68
FEATURE [Part::Box] Box045  label="Cube024"
  AttacherType = Attacher::AttachEngine3D
  Height = 22
  Length = 50
  Placement = pos=(312.5,-3,-5) rot=(0,0,1;0rad)
  Width = 68
FEATURE [Part::Cut] Cut051
  Base = -> Box045
  Refine = true
  Tool = -> Box044
FEATURE [Part::Box] Box046  label="Cube025"
  AttacherType = Attacher::AttachEngine3D
  Height = 20
  Length = 50
  Placement = pos=(312.5,0,0) rot=(0,0,1;0rad)
  Width = 62
FEATURE [Part::Fillet] Fillet018
  Base = -> Box046
  Edges = 2 edges r=2: [Edge9,Edge11]
FEATURE [Part::Cut] Cut052
  Base = -> Cut051
  Refine = true
  Tool = -> Fillet018
FEATURE [Part::Box] Box047  label="Cube026"
  AttacherType = Attacher::AttachEngine3D
  Height = 20
  Length = 15
  Placement = pos=(312.5,10,-5) rot=(0,0,1;0rad)
  Width = 42
FEATURE [Part::Cut] Cut053
  Base = -> Cut052
  Refine = true
  Tool = -> Box047
FEATURE [Part::Fillet] Fillet019
  Base = -> Cut053
  Edges = 2 edges r=5: [Edge23,Edge34]
FEATURE [Part::Fillet] Fillet020
  Base = -> Fillet019
  Edges = 2 edges r=2: [Edge43,Edge44]
FEATURE [Part::Fillet] Fillet021
  Base = -> Fillet020
  Edges = 2 edges r=5: [Edge6,Edge49]
FEATURE [Part::Cylinder] Cylinder098
  Angle = 360
  AttacherType = Attacher::AttachEngine3D
  Height = 15
  Placement = pos=(330.5,13.5,-15) rot=(0,0,1;0rad)
  Radius = 1.6
FEATURE [Part::Cylinder] Cylinder099
  Angle = 360
  AttacherType = Attacher::AttachEngine3D
  Height = 15
  Placement = pos=(359.5,13.5,-15) rot=(0,0,1;0rad)
  Radius = 1.6
FEATURE [Part::MultiFuse] Fusion083
  Refine = true
  Shapes = -> [Cylinder098,Cylinder099]
FEATURE [Part::Cylinder] Cylinder100
  Angle = 360
  AttacherType = Attacher::AttachEngine3D
  Height = 15
  Placement = pos=(330.5,13.5,-15) rot=(0,0,1;0rad)
  Radius = 1.6
FEATURE [Part::Cylinder] Cylinder101
  Angle = 360
  AttacherType = Attacher::AttachEngine3D
  Height = 15
  Placement = pos=(359.5,13.5,-15) rot=(0,0,1;0rad)
  Radius = 1.6
FEATURE [Part::MultiFuse] Fusion084
  Placement = pos=(0,35,0) rot=(0,0,1;0rad)
  Refine = true
  Shapes = -> [Cylinder100,Cylinder101]
FEATURE [Part::MultiFuse] Fusion085
  Refine = true
  Shapes = -> [Fusion084,Fusion083]
FEATURE [Part::MultiFuse] Fusion086
  Refine = true
  Shapes = -> [Cylinder098,Cylinder099]
FEATURE [Part::MultiFuse] Fusion088
  Placement = pos=(0,35,0) rot=(0,0,1;0rad)
  Refine = true
  Shapes = -> [Cylinder100,Cylinder101]
FEATURE [Part::MultiFuse] Fusion087
  Refine = true
  Shapes = -> [Fusion088,Fusion086]
FEATURE [Part::Cut] Cut054
  Base = -> Fillet021
  Refine = true
  Tool = -> Fusion085
FEATURE [Part::Cylinder] Cylinder102
  Angle = 360
  AttacherType = Attacher::AttachEngine3D
  Height = 10
  Placement = pos=(320,7,10) rot=(1,0,0;1.5708rad)
  Radius = 1.6
FEATURE [Part::Cylinder] Cylinder103
  Angle = 360
  AttacherType = Attacher::AttachEngine3D
  Height = 10
  Placement = pos=(355,7,10) rot=(1,0,0;1.5708rad)
  Radius = 1.6
FEATURE [Part::MultiFuse] Fusion089
  Refine = true
  Shapes = -> [Cylinder102,Cylinder103]
FEATURE [Part::Cylinder] Cylinder104
  Angle = 360
  AttacherType = Attacher::AttachEngine3D
  Height = 10
  Placement = pos=(355,7,10) rot=(1,0,0;1.5708rad)
  Radius = 1.6
FEATURE [Part::Cylinder] Cylinder105
  Angle = 360
  AttacherType = Attacher::AttachEngine3D
  Height = 10
  Placement = pos=(320,7,10) rot=(1,0,0;1.5708rad)
  Radius = 1.6
FEATURE [Part::MultiFuse] Fusion090
  Placement = pos=(0,58,0) rot=(0,0,1;0rad)
  Refine = true
  Shapes = -> [Cylinder105,Cylinder104]
FEATURE [Part::MultiFuse] Fusion091
  Refine = true
  Shapes = -> [Fusion090,Fusion089]
FEATURE [Part::Cut] Cut055
  Base = -> Cut054
  Refine = true
  Tool = -> Fusion091
FEATURE [Part::Fillet] Fillet022  label="battery-box-holder_"
  Base = -> Cut055
  Edges = 4 edges r=3: [Edge7,Edge49,Edge56,Edge66]
FEATURE [Part::Cylinder] Cylinder106
  Angle = 360
  AttacherType = Attacher::AttachEngine3D
  Height = 2
  Placement = pos=(330.5,13.5,-12) rot=(0,0,1;0rad)
  Radius = 3.1
FEATURE [Part::Cylinder] Cylinder107
  Angle = 360
  AttacherType = Attacher::AttachEngine3D
  Height = 2
  Placement = pos=(359.5,13.5,-11) rot=(0,0,1;0rad)
  Radius = 3.1
FEATURE [Part::Cylinder] Cylinder108
  Angle = 360
  AttacherType = Attacher::AttachEngine3D
  Height = 2
  Placement = pos=(359.5,48.5,-11) rot=(0,0,1;0rad)
  Radius = 3.1
FEATURE [Part::Cylinder] Cylinder109
  Angle = 360
  AttacherType = Attacher::AttachEngine3D
  Height = 2
  Placement = pos=(330.5,48.5,-12) rot=(0,0,1;0rad)
  Radius = 3.1
FEATURE [Part::MultiFuse] Fusion092
  Placement = pos=(0,0,6) rot=(0,0,1;0rad)
  Refine = true
  Shapes = -> [Cylinder109,Cylinder106]
FEATURE [Part::MultiFuse] Fusion093
  Placement = pos=(0,0,6.5) rot=(0,0,1;0rad)
  Refine = true
  Shapes = -> [Cylinder108,Cylinder107]
FEATURE [Part::MultiFuse] Fusion094
  Refine = true
  Shapes = -> [Fusion093,Fusion092]
FEATURE [Part::Box] Box048  label="Cube027"
  AttacherType = Attacher::AttachEngine3D
  Height = 17
  Length = 16
  Placement = pos=(323.5,7.5,1.5) rot=(0,0,1;0rad)
  Width = 8.5
FEATURE [Part::Box] Box049  label="Cube028"
  AttacherType = Attacher::AttachEngine3D
  Height = 20
  Length = 20
  Placement = pos=(320,18.5,1.5) rot=(0,0,1;0rad)
  Width = 6
FEATURE [Part::Cylinder] Cylinder110
  Angle = 360
  AttacherType = Attacher::AttachEngine3D
  Height = 10
  Placement = pos=(320,26,0) rot=(1,0,0;1.5708rad)
  Radius = 1.6
FEATURE [Part::Cylinder] Cylinder111
  Angle = 360
  AttacherType = Attacher::AttachEngine3D
  Height = 10
  Placement = pos=(320,26,10) rot=(1,0,0;1.5708rad)
  Radius = 1.6
FEATURE [Part::MultiFuse] Fusion096
  Placement = pos=(15,-1.5,6) rot=(0,0,1;0rad)
  Refine = true
  Shapes = -> [Cylinder111,Cylinder110]
FEATURE [Part::Cut] Cut057  label="limit-switch-1"
  Base = -> Box049
  Placement = pos=(1.5,-18.5,-1.5) rot=(0,0,1;0rad)
  Refine = true
  Tool = -> Fusion096
FEATURE [Part::MultiFuse] Fusion097
  Placement = pos=(15,-1.5,6) rot=(0,0,1;0rad)
  Refine = true
  Shapes = -> [Cylinder111,Cylinder110]
FEATURE [Part::Box] Box050  label="Cube029"
  AttacherType = Attacher::AttachEngine3D
  Height = 20
  Length = 20
  Placement = pos=(320,18.5,1.5) rot=(0,0,1;0rad)
  Width = 6
FEATURE [Part::Cut] Cut058  label="limit-switch-2"
  Base = -> Box050
  Placement = pos=(320,37.5,343) rot=(0,1,0;1.5708rad)
  Refine = true
  Tool = -> Fusion097
FEATURE [Part::Cylinder] Cylinder112
  Angle = 360
  AttacherType = Attacher::AttachEngine3D
  Height = 10
  Placement = pos=(320,26,10) rot=(1,0,0;1.5708rad)
  Radius = 1.25
FEATURE [Part::Cylinder] Cylinder113
  Angle = 360
  AttacherType = Attacher::AttachEngine3D
  Height = 10
  Placement = pos=(320,26,0) rot=(1,0,0;1.5708rad)
  Radius = 1.25
FEATURE [Part::MultiFuse] Fusion098
  Placement = pos=(16.5,-9.5,4.5) rot=(0,0,1;0rad)
  Refine = true
  Shapes = -> [Cylinder112,Cylinder113]
FEATURE [Part::Cut] Cut059
  Base = -> Box048
  Refine = true
  Tool = -> Fusion098
FEATURE [Part::Box] Box051  label="Cube030"
  AttacherType = Attacher::AttachEngine3D
  Height = 17
  Length = 16
  Placement = pos=(323.5,46,1.5) rot=(0,0,1;0rad)
  Width = 8.5
FEATURE [Part::Box] Box052  label="Cube031"
  AttacherType = Attacher::AttachEngine3D
  Height = 10
  Length = 1.2
  Placement = pos=(325.4,46,2.5) rot=(0,0,1;0rad)
  Width = 5
FEATURE [Part::Box] Box053  label="Cube032"
  AttacherType = Attacher::AttachEngine3D
  Height = 10
  Length = 1.2
  Placement = pos=(335.4,46,2.5) rot=(0,0,1;0rad)
  Width = 5
FEATURE [Part::MultiFuse] Fusion099
  Refine = true
  Shapes = -> [Box052,Box053]
FEATURE [Part::Cut] Cut060
  Base = -> Box051
  Refine = true
  Tool = -> Fusion099
FEATURE [Part::Fillet] Fillet024
  Base = -> Cut059
  Edges = 2 edges r=2: [Edge5,Edge7]
FEATURE [Part::Fillet] Fillet025
  Base = -> Cut060
  Edges = 2 edges r=2: [Edge16,Edge18]
FEATURE [Part::Box] Box054  label="Cube033"
  AttacherType = Attacher::AttachEngine3D
  Height = 1.2
  Length = 12
  Placement = pos=(325.5,50.5,9.4) rot=(0,0,1;0rad)
  Width = 4
FEATURE [Part::Cut] Cut061  label="limit-switch-holder-2"
  Base = -> Fillet025
  Placement = pos=(0,16,0) rot=(0,0,1;0rad)
  Refine = true
  Tool = -> Box054
FEATURE [Part::Box] Box055  label="Cube034"
  AttacherType = Attacher::AttachEngine3D
  Height = 1.2
  Length = 12
  Placement = pos=(325.5,7.5,9.4) rot=(0,0,1;0rad)
  Width = 4
FEATURE [Part::Cut] Cut062  label="limit-switch-holder-1"
  Base = -> Fillet024
  Placement = pos=(0,-16,0) rot=(0,0,1;0rad)
  Refine = true
  Tool = -> Box055
FEATURE [Part::Box] Box056  label="Cube035"
  AttacherType = Attacher::AttachEngine3D
  Height = 10
  Length = 110
  Width = 10
FEATURE [Part::Box] Box057  label="Cube036"
  AttacherType = Attacher::AttachEngine3D
  Height = 10
  Length = 110
  Placement = pos=(0,0,-40) rot=(0,0,1;0rad)
  Width = 10
FEATURE [Part::Box] Box058  label="Cube037"
  AttacherType = Attacher::AttachEngine3D
  Height = 50
  Length = 8
  Placement = pos=(100,2,-40) rot=(0,0,1;0rad)
  Width = 8
FEATURE [Part::Box] Box059  label="Cube038"
  AttacherType = Attacher::AttachEngine3D
  Height = 50
  Length = 10
  Placement = pos=(0,0,-40) rot=(0,0,1;0rad)
  Width = 10
FEATURE [Part::MultiFuse] Fusion100
  Refine = true
  Shapes = -> [Box056,Box058,Box057,Box059]
FEATURE [Part::Fillet] Fillet026  label="lateral-protection-2_"
  Base = -> Fusion100
  Edges = 1 edges r=9.99: [Edge30]
  Placement = pos=(276,-49,-16) rot=(0,-1,0;0.05236rad)
FEATURE [Part::MultiFuse] Fusion101
  Refine = true
  Shapes = -> [Box056,Box058,Box057,Box059]
FEATURE [Part::Fillet] Fillet027
  Base = -> Fusion101
  Edges = 1 edges r=9.99: [Edge30]
  Placement = pos=(276,-50,-16) rot=(0,-1,0;0.05236rad)
FEATURE [Part::Mirroring] Part__Mirroring  label="Fillet027 (Mirror #1)"
  Base = (0,0,0)
  Normal = (0,0,1)
  Placement = pos=(0,71,0) rot=(0,0,1;0rad)
  Source = -> Fillet027
FEATURE [Part::Fillet] Fillet028
  Base = -> Box039
  Edges = 4 edges r=3: [Edge2,Edge4,Edge6,Edge8]
FEATURE [Part::Fillet] Fillet029
  Base = -> Fillet028
  Edges = 4 edges r=3: [Edge4,Edge16,Edge18,Edge20]
FEATURE [Part::MultiFuse] Fusion102
  Refine = true
  Shapes = -> [Fillet029,Fusion082]
FEATURE [Part::Cylinder] Cylinder114
  Angle = 360
  AttacherType = Attacher::AttachEngine3D
  Height = 25
  Placement = pos=(3.5,96,46.5) rot=(1,0,0;1.5708rad)
  Radius = 1.6
FEATURE [Part::Cylinder] Cylinder115
  Angle = 360
  AttacherType = Attacher::AttachEngine3D
  Height = 25
  Placement = pos=(76.5,96,3.5) rot=(1,0,0;1.5708rad)
  Radius = 1.6
FEATURE [Part::Cylinder] Cylinder116
  Angle = 360
  AttacherType = Attacher::AttachEngine3D
  Height = 25
  Placement = pos=(3.5,96,3.5) rot=(1,0,0;1.5708rad)
  Radius = 1.6
FEATURE [Part::Cylinder] Cylinder117
  Angle = 360
  AttacherType = Attacher::AttachEngine3D
  Height = 25
  Placement = pos=(76.5,96,46.5) rot=(1,0,0;1.5708rad)
  Radius = 1.6
FEATURE [Part::MultiFuse] Fusion103
  Placement = pos=(306,25,-55) rot=(0,-1,0;0.05236rad)
  Refine = true
  Shapes = -> [Cylinder116,Cylinder117,Cylinder115,Cylinder114]
FEATURE [Part::Cylinder] Cylinder118
  Angle = 360
  AttacherType = Attacher::AttachEngine3D
  Height = 10
  Placement = pos=(76.5,96,3.5) rot=(1,0,0;1.5708rad)
  Radius = 4
FEATURE [Part::Cylinder] Cylinder119
  Angle = 360
  AttacherType = Attacher::AttachEngine3D
  Height = 10
  Placement = pos=(76.5,96,46.5) rot=(1,0,0;1.5708rad)
  Radius = 4
FEATURE [Part::Cylinder] Cylinder120
  Angle = 360
  AttacherType = Attacher::AttachEngine3D
  Height = 10
  Placement = pos=(3.5,96,46.5) rot=(1,0,0;1.5708rad)
  Radius = 4
FEATURE [Part::Cylinder] Cylinder121
  Angle = 360
  AttacherType = Attacher::AttachEngine3D
  Height = 10
  Placement = pos=(3.5,96,3.5) rot=(1,0,0;1.5708rad)
  Radius = 4
FEATURE [Part::MultiFuse] Fusion104
  Placement = pos=(306,15,-55) rot=(0,-1,0;0.05236rad)
  Refine = true
  Shapes = -> [Cylinder121,Cylinder119,Cylinder118,Cylinder120]
FEATURE [Part::Cylinder] Cylinder122
  Angle = 360
  AttacherType = Attacher::AttachEngine3D
  Height = 25
  Placement = pos=(76.5,96,3.5) rot=(1,0,0;1.5708rad)
  Radius = 1.6
FEATURE [Part::Cylinder] Cylinder123
  Angle = 360
  AttacherType = Attacher::AttachEngine3D
  Height = 25
  Placement = pos=(76.5,96,46.5) rot=(1,0,0;1.5708rad)
  Radius = 1.6
FEATURE [Part::Cylinder] Cylinder124
  Angle = 360
  AttacherType = Attacher::AttachEngine3D
  Height = 25
  Placement = pos=(3.5,96,46.5) rot=(1,0,0;1.5708rad)
  Radius = 1.6
FEATURE [Part::Cylinder] Cylinder125
  Angle = 360
  AttacherType = Attacher::AttachEngine3D
  Height = 25
  Placement = pos=(3.5,96,3.5) rot=(1,0,0;1.5708rad)
  Radius = 1.6
FEATURE [Part::MultiFuse] Fusion105
  Placement = pos=(306,25,-55) rot=(0,-1,0;0.05236rad)
  Refine = true
  Shapes = -> [Cylinder125,Cylinder123,Cylinder122,Cylinder124]
FEATURE [Part::Cut] Cut064  label="lateral-protection-spacers-1"
  Base = -> Fusion104
  Placement = pos=(0,-5,0) rot=(0,0,1;0rad)
  Refine = true
  Tool = -> Fusion105
FEATURE [Part::Cylinder] Cylinder126
  Angle = 360
  AttacherType = Attacher::AttachEngine3D
  Height = 25
  Placement = pos=(76.5,96,3.5) rot=(1,0,0;1.5708rad)
  Radius = 1.6
FEATURE [Part::Cylinder] Cylinder127
  Angle = 360
  AttacherType = Attacher::AttachEngine3D
  Height = 25
  Placement = pos=(76.5,96,46.5) rot=(1,0,0;1.5708rad)
  Radius = 1.6
FEATURE [Part::Cylinder] Cylinder128
  Angle = 360
  AttacherType = Attacher::AttachEngine3D
  Height = 25
  Placement = pos=(3.5,96,46.5) rot=(1,0,0;1.5708rad)
  Radius = 1.6
FEATURE [Part::Cylinder] Cylinder129
  Angle = 360
  AttacherType = Attacher::AttachEngine3D
  Height = 25
  Placement = pos=(3.5,96,3.5) rot=(1,0,0;1.5708rad)
  Radius = 1.6
FEATURE [Part::MultiFuse] Fusion106
  Placement = pos=(306,-120,-55) rot=(0,-1,0;0.05236rad)
  Refine = true
  Shapes = -> [Cylinder129,Cylinder127,Cylinder126,Cylinder128]
FEATURE [Part::Cut] Cut065  label="lateral-protection-1"
  Base = -> Part__Mirroring
  Placement = pos=(0,-5,0) rot=(0,0,1;0rad)
  Refine = true
  Tool = -> Fusion103
FEATURE [Part::Cut] Cut067  label="lateral-protection-2"
  Base = -> Fillet026
  Placement = pos=(0,-5,0) rot=(0,0,1;0rad)
  Refine = true
  Tool = -> Fusion106
FEATURE [Part::Fillet] Fillet030
  Base = -> Cut046
  Edges = 4 edges r=3: [Edge1,Edge4,Edge10,Edge30]
FEATURE [Part::Fillet] Fillet031
  Base = -> Fillet030
  Edges = 4 edges r=3: [Edge1,Edge9,Edge12,Edge15]
  Placement = pos=(306,0,-55) rot=(0,-1,0;0.05236rad)
FEATURE [Part::MultiFuse] Fusion109
  Refine = true
  Shapes = -> [Fusion094,Fillet031]
FEATURE [Part::Cut] Cut068
  Base = -> Fusion109
  Refine = true
  Tool = -> Fusion087
FEATURE [Part::MultiFuse] Fusion110
  Placement = pos=(306,15,-55) rot=(0,-1,0;0.05236rad)
  Refine = true
  Shapes = -> [Cylinder121,Cylinder119,Cylinder118,Cylinder120]
FEATURE [Part::MultiFuse] Fusion111
  Placement = pos=(306,25,-55) rot=(0,-1,0;0.05236rad)
  Refine = true
  Shapes = -> [Cylinder125,Cylinder123,Cylinder122,Cylinder124]
FEATURE [Part::Cut] Cut069  label="lateral-protection-spacers-2"
  Base = -> Fusion110
  Placement = pos=(0,-145,0) rot=(0,0,1;0rad)
  Refine = true
  Tool = -> Fusion111
FEATURE [Part::Cylinder] Cylinder130
  Angle = 360
  AttacherType = Attacher::AttachEngine3D
  Height = 3
  Placement = pos=(3.5,96,3.5) rot=(1,0,0;1.5708rad)
  Radius = 4
FEATURE [Part::Cylinder] Cylinder131
  Angle = 360
  AttacherType = Attacher::AttachEngine3D
  Height = 3
  Placement = pos=(76.5,96,3.5) rot=(1,0,0;1.5708rad)
  Radius = 4
FEATURE [Part::Cylinder] Cylinder132
  Angle = 360
  AttacherType = Attacher::AttachEngine3D
  Height = 3
  Placement = pos=(3.5,96,46.5) rot=(1,0,0;1.5708rad)
  Radius = 4
FEATURE [Part::Cylinder] Cylinder133
  Angle = 360
  AttacherType = Attacher::AttachEngine3D
  Height = 3
  Placement = pos=(76.5,96,46.5) rot=(1,0,0;1.5708rad)
  Radius = 4
FEATURE [Part::MultiFuse] Fusion112
  Placement = pos=(306,-122,-55) rot=(0,-1,0;0.05236rad)
  Refine = true
  Shapes = -> [Cylinder130,Cylinder132,Cylinder133,Cylinder131]
FEATURE [Part::MultiFuse] Fusion113
  Refine = true
  Shapes = -> [Cut068,Fusion112]
FEATURE [Part::Cylinder] Cylinder134
  Angle = 360
  AttacherType = Attacher::AttachEngine3D
  Height = 10
  Placement = pos=(3.5,96,3.5) rot=(1,0,0;1.5708rad)
  Radius = 1.25
FEATURE [Part::Cylinder] Cylinder135
  Angle = 360
  AttacherType = Attacher::AttachEngine3D
  Height = 10
  Placement = pos=(3.5,96,46.5) rot=(1,0,0;1.5708rad)
  Radius = 1.25
FEATURE [Part::Cylinder] Cylinder136
  Angle = 360
  AttacherType = Attacher::AttachEngine3D
  Height = 10
  Placement = pos=(76.5,96,46.5) rot=(1,0,0;1.5708rad)
  Radius = 1.25
FEATURE [Part::Cylinder] Cylinder137
  Angle = 360
  AttacherType = Attacher::AttachEngine3D
  Height = 10
  Placement = pos=(76.5,96,3.5) rot=(1,0,0;1.5708rad)
  Radius = 1.25
FEATURE [Part::MultiFuse] Fusion114
  Placement = pos=(306,-115,-55) rot=(0,-1,0;0.05236rad)
  Refine = true
  Shapes = -> [Cylinder134,Cylinder135,Cylinder136,Cylinder137]
FEATURE [Part::Cut] Cut070  label="battery-box_"
  Base = -> Fusion113
  Refine = true
  Tool = -> Fusion114
FEATURE [Part::Box] Box062  label="Cube041"
  AttacherType = Attacher::AttachEngine3D
  Height = 6
  Length = 41
  Placement = pos=(332,7,-12.1) rot=(0,-1,0;0.05236rad)
  Width = 10
FEATURE [Part::Cut] Cut072  label="battery-box"
  Base = -> Cut070
  Placement = pos=(0,-5,0) rot=(0,0,1;0rad)
  Refine = true
  Tool = -> Box062
FEATURE [Part::Cut] Cut063  label="battery-holder-cap"
  Base = -> Fusion102
  Placement = pos=(306,-5,-55) rot=(0,-1,0;0.05236rad)
  Refine = true
  Tool = -> Fusion073
FEATURE [Part::Box] Box063  label="Cube042"
  AttacherType = Attacher::AttachEngine3D
  Height = 29
  Length = 62
  Placement = pos=(309,-10,-9) rot=(0,0,1;0rad)
  Width = 10
FEATURE [Part::Box] Box064  label="Cube043"
  AttacherType = Attacher::AttachEngine3D
  Height = 29
  Length = 62
  Placement = pos=(309,62,-9) rot=(0,0,1;0rad)
  Width = 10
FEATURE [Part::MultiFuse] Fusion115
  Refine = true
  Shapes = -> [Box064,Box063]
FEATURE [Part::Cut] Cut073
  Base = -> Fillet022
  Refine = true
  Tool = -> Fusion115
FEATURE [Part::Cylinder] Cylinder138
  Angle = 360
  AttacherType = Attacher::AttachEngine3D
  Height = 10
  Placement = pos=(320,6,-6) rot=(0,0,1;0rad)
  Radius = 1.6
FEATURE [Part::Cylinder] Cylinder139
  Angle = 360
  AttacherType = Attacher::AttachEngine3D
  Height = 10
  Placement = pos=(320,56,-6) rot=(0,0,1;0rad)
  Radius = 1.6
FEATURE [Part::MultiFuse] Fusion116
  Placement = pos=(2,0,0) rot=(0,0,1;0rad)
  Refine = true
  Shapes = -> [Cylinder139,Cylinder138]
FEATURE [Part::Cylinder] Cylinder140
  Angle = 360
  AttacherType = Attacher::AttachEngine3D
  Height = 10
  Placement = pos=(320,6,-6) rot=(0,0,1;0rad)
  Radius = 1.6
FEATURE [Part::Cylinder] Cylinder141
  Angle = 360
  AttacherType = Attacher::AttachEngine3D
  Height = 10
  Placement = pos=(320,56,-6) rot=(0,0,1;0rad)
  Radius = 1.6
FEATURE [Part::MultiFuse] Fusion117
  Placement = pos=(33,0,0) rot=(0,0,1;0rad)
  Refine = true
  Shapes = -> [Cylinder141,Cylinder140]
FEATURE [Part::MultiFuse] Fusion118
  Refine = true
  Shapes = -> [Fusion117,Fusion116]
FEATURE [Part::Cut] Cut074  label="battery-box-holder"
  Base = -> Cut073
  Refine = true
  Tool = -> Fusion118
FEATURE [Part::Cylinder] Cylinder143
  Angle = 180
  AttacherType = Attacher::AttachEngine3D
  Height = 53
  Placement = pos=(450,-9,-42) rot=(1,0,0;1.5708rad)
  Radius = 52
FEATURE [Part::Cylinder] Cylinder144
  Angle = 180
  AttacherType = Attacher::AttachEngine3D
  Height = 53
  Placement = pos=(450,-9,-42) rot=(1,0,0;1.5708rad)
  Radius = 49
FEATURE [Part::Cut] Cut075
  Base = -> Cylinder143
  Placement = pos=(0,0,10) rot=(0,0,1;0rad)
  Refine = true
  Tool = -> Cylinder144
FEATURE [Part::Cylinder] Cylinder145
  Angle = 180
  AttacherType = Attacher::AttachEngine3D
  Height = 2
  Placement = pos=(450,-12,-42) rot=(1,0,0;1.5708rad)
  Radius = 52
FEATURE [Part::Cylinder] Cylinder146
  Angle = 180
  AttacherType = Attacher::AttachEngine3D
  Height = 2
  Placement = pos=(450,-12,-42) rot=(1,0,0;1.5708rad)
  Radius = 48
FEATURE [Part::Cut] Cut076
  Base = -> Cylinder145
  Placement = pos=(0,-48,10) rot=(0,0,1;0rad)
  Refine = true
  Tool = -> Cylinder146
FEATURE [Part::MultiFuse] Fusion119
  Placement = pos=(105,0,0) rot=(0,0,1;0rad)
  Refine = true
  Shapes = -> [Cut076,Cut075]
FEATURE [Part::Cut] Cut077
  Base = -> Cylinder143
  Placement = pos=(0,0,10) rot=(0,0,1;0rad)
  Refine = true
  Tool = -> Cylinder144
FEATURE [Part::Cut] Cut078
  Base = -> Cylinder145
  Placement = pos=(0,-48,10) rot=(0,0,1;0rad)
  Refine = true
  Tool = -> Cylinder146
FEATURE [Part::MultiFuse] Fusion120
  Refine = true
  Shapes = -> [Cut078,Cut077]
FEATURE [Part::MultiFuse] Fusion121
  Placement = pos=(-2,0,-27) rot=(0,-1,0;0.05236rad)
  Refine = true
  Shapes = -> [Fusion119,Fusion120]
FEATURE [Part::Box] Box065  label="Cube044"
  AttacherType = Attacher::AttachEngine3D
  Height = 10
  Length = 7
  Placement = pos=(498,-39,-32.8) rot=(0,-1,0;0.05236rad)
  Width = 30
FEATURE [Part::MultiFuse] Fusion122
  Placement = pos=(0,3,0) rot=(0,0,1;0rad)
  Refine = true
  Shapes = -> [Fusion121,Box065]
FEATURE [Part::Cylinder] Cylinder147
  Angle = 180
  AttacherType = Attacher::AttachEngine3D
  Height = 3
  Placement = pos=(448.581,-6,-35.3913) rot=(0.999315,-0.026168,0.026168;1.57148rad)
  Radius = 52
FEATURE [Part::Box] Box066  label="Cube045"
  AttacherType = Attacher::AttachEngine3D
  Height = 35
  Length = 128
  Placement = pos=(382,-9,-40.8) rot=(0,-1,0;0.05236rad)
  Width = 3
FEATURE [Part::Cut] Cut079
  Base = -> Cylinder147
  Placement = pos=(0.48,0,-0.5) rot=(0,0,1;0rad)
  Refine = true
  Tool = -> Box066
FEATURE [Part::Box] Box067  label="Cube046"
  AttacherType = Attacher::AttachEngine3D
  Height = 35
  Length = 128
  Placement = pos=(382,-9,-40.8) rot=(0,-1,0;0.05236rad)
  Width = 3
FEATURE [Part::Cylinder] Cylinder148
  Angle = 180
  AttacherType = Attacher::AttachEngine3D
  Height = 3
  Placement = pos=(448.581,-6,-35.3913) rot=(0.999315,-0.026168,0.026168;1.57148rad)
  Radius = 52
FEATURE [Part::Cut] Cut080
  Base = -> Cylinder148
  Placement = pos=(105.48,0,5) rot=(0,0,1;0rad)
  Refine = true
  Tool = -> Box067
FEATURE [Part::Box] Box068  label="Cube047"
  AttacherType = Attacher::AttachEngine3D
  Height = 32
  Length = 59
  Placement = pos=(473,-20,-36) rot=(0,-1,0;0.05236rad)
  Width = 20
FEATURE [Part::MultiFuse] Fusion123
  Refine = true
  Shapes = -> [Fusion122,Cut079,Cut080]
FEATURE [Part::Cut] Cut081
  Base = -> Fusion123
  Refine = true
  Tool = -> Box068
FEATURE [Part::Box] Box069  label="fender-left-support"
  AttacherType = Attacher::AttachEngine3D
  Height = 32
  Length = 29
  Placement = pos=(487,-22.8,-33.5) rot=(0,-1,0;0.05236rad)
  Width = 13.8
FEATURE [Part::Cylinder] Cylinder152
  Angle = 360
  AttacherType = Attacher::AttachEngine3D
  Height = 9
  Placement = pos=(555,-5,10) rot=(1,0,0;1.5708rad)
  Radius = 1.6
FEATURE [Part::Cylinder] Cylinder153
  Angle = 360
  AttacherType = Attacher::AttachEngine3D
  Height = 9
  Placement = pos=(450,-5,10) rot=(1,0,0;1.5708rad)
  Radius = 1.6
FEATURE [Part::Fillet] Fillet033
  Base = -> Cut081
  Edges = 2 edges r=0.99: [Edge16,Edge68]
  Placement = pos=(0,-3,2) rot=(0,0,1;0rad)
FEATURE [Part::MultiFuse] Fusion125
  Placement = pos=(-9,5,0) rot=(0,0,1;0rad)
  Refine = true
  Shapes = -> [Cylinder153,Cylinder152]
FEATURE [Part::Box] Box070  label="fender-right-support"
  AttacherType = Attacher::AttachEngine3D
  Height = 32
  Length = 29
  Placement = pos=(487,71,-33.5) rot=(0,-1,0;0.05236rad)
  Width = 13.8
FEATURE [Part::MultiFuse] Fusion128
  Refine = true
  Shapes = -> [Cylinder026,Cylinder027]
FEATURE [Part::MultiFuse] Fusion130
  Placement = pos=(105,0,0) rot=(0,0,1;0rad)
  Refine = true
  Shapes = -> [Cylinder029,Cylinder028]
FEATURE [Part::MultiFuse] Fusion129  label="wheels001"
  Placement = pos=(450,122,-47) rot=(0,-1,0;0.05236rad)
  Refine = true
  Shapes = -> [Fusion130,Fusion128]
FEATURE [Part::Box] Box071
  AttacherType = Attacher::AttachEngine3D
  Height = 10
  Length = 30
  Placement = pos=(435,-9,5) rot=(0,0,1;0rad)
  Width = 9
FEATURE [Part::MultiFuse] Fusion131  label="wheels"
  Refine = true
  Shapes = -> [Fusion025,Fusion129]
FEATURE [Part::Fillet] Fillet034
  Base = -> Box071
  Edges = 4 edges r=3: [Edge2,Edge4,Edge6,Edge8]
FEATURE [Part::Cylinder] Cylinder154
  Angle = 360
  AttacherType = Attacher::AttachEngine3D
  Height = 9
  Placement = pos=(555,-5,10) rot=(1,0,0;1.5708rad)
  Radius = 1.6
FEATURE [Part::Cylinder] Cylinder155
  Angle = 360
  AttacherType = Attacher::AttachEngine3D
  Height = 9
  Placement = pos=(450,-5,10) rot=(1,0,0;1.5708rad)
  Radius = 1.6
FEATURE [Part::MultiFuse] Fusion132
  Placement = pos=(9,5,0) rot=(0,0,1;0rad)
  Refine = true
  Shapes = -> [Cylinder155,Cylinder154]
FEATURE [Part::Cylinder] Cylinder156
  Angle = 360
  AttacherType = Attacher::AttachEngine3D
  Height = 9
  Placement = pos=(555,-5,10) rot=(1,0,0;1.5708rad)
  Radius = 1.6
FEATURE [Part::Cylinder] Cylinder157
  Angle = 360
  AttacherType = Attacher::AttachEngine3D
  Height = 9
  Placement = pos=(450,-5,10) rot=(1,0,0;1.5708rad)
  Radius = 1.6
FEATURE [Part::MultiFuse] Fusion133
  Placement = pos=(-9,0,0) rot=(0,0,1;0rad)
  Refine = true
  Shapes = -> [Cylinder157,Cylinder156]
FEATURE [Part::Cylinder] Cylinder158
  Angle = 360
  AttacherType = Attacher::AttachEngine3D
  Height = 9
  Placement = pos=(555,-5,10) rot=(1,0,0;1.5708rad)
  Radius = 1.6
FEATURE [Part::Cylinder] Cylinder159
  Angle = 360
  AttacherType = Attacher::AttachEngine3D
  Height = 9
  Placement = pos=(450,-5,10) rot=(1,0,0;1.5708rad)
  Radius = 1.6
FEATURE [Part::MultiFuse] Fusion134
  Placement = pos=(9,0,0) rot=(0,0,1;0rad)
  Refine = true
  Shapes = -> [Cylinder159,Cylinder158]
FEATURE [Part::MultiFuse] Fusion135
  Refine = true
  Shapes = -> [Fusion132,Fusion125]
FEATURE [Part::MultiFuse] Fusion136
  Refine = true
  Shapes = -> [Fusion133,Fusion134]
FEATURE [Part::MultiFuse] Fusion138
  Placement = pos=(-9,5,0) rot=(0,0,1;0rad)
  Refine = true
  Shapes = -> [Cylinder153,Cylinder152]
FEATURE [Part::MultiFuse] Fusion139
  Placement = pos=(9,5,0) rot=(0,0,1;0rad)
  Refine = true
  Shapes = -> [Cylinder155,Cylinder154]
FEATURE [Part::MultiFuse] Fusion137
  Refine = true
  Shapes = -> [Fusion139,Fusion138]
FEATURE [Part::Box] Box072
  AttacherType = Attacher::AttachEngine3D
  Height = 10
  Length = 30
  Placement = pos=(435,-9,5) rot=(0,0,1;0rad)
  Width = 9
FEATURE [Part::Fillet] Fillet035
  Base = -> Box072
  Edges = 4 edges r=3: [Edge2,Edge4,Edge6,Edge8]
  Placement = pos=(105,0,0) rot=(0,0,1;0rad)
FEATURE [Part::Cut] Cut082  label="fender-spacer-left-02"
  Base = -> Fillet035
  Placement = pos=(0,-10,0) rot=(0,0,1;0rad)
  Refine = true
  Tool = -> Fusion137
FEATURE [Part::Cut] Cut083  label="fender-spacer-left-01"
  Base = -> Fillet034
  Placement = pos=(0,-10,0) rot=(0,0,1;0rad)
  Refine = true
  Tool = -> Fusion135
FEATURE [Part::Cut] Cut084  label="fender-lh"
  Base = -> Fillet033
  Refine = true
  Tool = -> Fusion136
FEATURE [Part::MultiFuse] Fusion140
  Refine = true
  Shapes = -> [Fusion133,Fusion134]
FEATURE [Part::Fillet] Fillet036
  Base = -> Cut081
  Edges = 2 edges r=0.99: [Edge16,Edge68]
  Placement = pos=(0,-3,2) rot=(0,0,1;0rad)
FEATURE [Part::Cut] Cut085  label="fender-lh001"
  Base = -> Fillet036
  Refine = true
  Tool = -> Fusion140
FEATURE [Part::Mirroring] Part__Mirroring001  label="fender-rh"
  Base = (0,0,0)
  Normal = (0,0,1)
  Placement = pos=(0,62,0) rot=(0,0,1;0rad)
  Source = -> Cut085
FEATURE [Part::MultiFuse] Fusion141
  Refine = true
  Shapes = -> [Fusion139,Fusion138]
FEATURE [Part::MultiFuse] Fusion142
  Refine = true
  Shapes = -> [Fusion132,Fusion125]
FEATURE [Part::Fillet] Fillet037
  Base = -> Box072
  Edges = 4 edges r=3: [Edge2,Edge4,Edge6,Edge8]
  Placement = pos=(105,0,0) rot=(0,0,1;0rad)
FEATURE [Part::Cut] Cut087  label="fender-spacer-right-04"
  Base = -> Fillet037
  Placement = pos=(0,81,0) rot=(0,0,1;0rad)
  Refine = true
  Tool = -> Fusion141
FEATURE [Part::Fillet] Fillet038
  Base = -> Box071
  Edges = 4 edges r=3: [Edge2,Edge4,Edge6,Edge8]
FEATURE [Part::Cut] Cut086  label="fender-spacer-right-03"
  Base = -> Fillet038
  Placement = pos=(0,81,0) rot=(0,0,1;0rad)
  Refine = true
  Tool = -> Fusion142
FEATURE [Part::Box] Box073
  AttacherType = Attacher::AttachEngine3D
  Height = 25
  Length = 10
  Placement = pos=(590,1,-2) rot=(0,-1,0;0.05236rad)
  Width = 10
FEATURE [Part::Box] Box074
  AttacherType = Attacher::AttachEngine3D
  Height = 10
  Length = 21
  Placement = pos=(591,1,15.5) rot=(0,0,1;0rad)
  Width = 10
FEATURE [Part::Box] Box075
  AttacherType = Attacher::AttachEngine3D
  Height = 54
  Length = 10
  Placement = pos=(609,1,-33) rot=(0,-1,0;0.261799rad)
  Width = 10
FEATURE [Part::Box] Box076
  AttacherType = Attacher::AttachEngine3D
  Height = 10
  Length = 21
  Placement = pos=(591,1,8.5) rot=(0,0,1;0rad)
  Width = 10
FEATURE [Part::Fillet] Fillet039
  Base = -> Box076
  Edges = 1 edges r=3: [Edge10]
FEATURE [Part::Cut] Cut088
  Base = -> Box074
  Refine = true
  Tool = -> Fillet039
FEATURE [Part::MultiFuse] Fusion143
  Refine = true
  Shapes = -> [Box073,Cut088]
FEATURE [Part::Cut] Cut089
  Base = -> Box075
  Refine = true
  Tool = -> Fusion143
FEATURE [Part::Cylinder] Cylinder160
  Angle = 360
  AttacherType = Attacher::AttachEngine3D
  Height = 180
  Placement = pos=(615,121,-24) rot=(1,0,0;1.5708rad)
  Radius = 5
FEATURE [Part::Box] Box077
  AttacherType = Attacher::AttachEngine3D
  Height = 10
  Length = 20
  Placement = pos=(603,1,-41) rot=(0,0,1;0rad)
  Width = 10
FEATURE [Part::Cut] Cut090
  Base = -> Cut089
  Refine = true
  Tool = -> Box077
FEATURE [Part::Fillet] Fillet040
  Base = -> Cut090
  Edges = 1 edges r=2: [Edge3]
FEATURE [Part::Fillet] Fillet041
  Base = -> Fillet040
  Edges = 1 edges r=5: [Edge24]
FEATURE [Part::Cylinder] Cylinder161  label="bumper-METAL"
  Angle = 360
  AttacherType = Attacher::AttachEngine3D
  Height = 180
  Placement = pos=(615,121,-24) rot=(1,0,0;1.5708rad)
  Radius = 5
FEATURE [Part::Cut] Cut091
  Base = -> Fillet041
  Refine = true
  Tool = -> Cylinder160
FEATURE [Part::Cylinder] Cylinder162
  Angle = 360
  AttacherType = Attacher::AttachEngine3D
  Height = 10
  Placement = pos=(599,7,14) rot=(0,1,0;1.5708rad)
  Radius = 1.6
FEATURE [Part::Cylinder] Cylinder163
  Angle = 360
  AttacherType = Attacher::AttachEngine3D
  Height = 10
  Placement = pos=(599,7,6) rot=(0,1,0;1.5708rad)
  Radius = 1.6
FEATURE [Part::Cylinder] Cylinder164
  Angle = 360
  AttacherType = Attacher::AttachEngine3D
  Height = 4
  Placement = pos=(604,7,14) rot=(0,1,0;1.5708rad)
  Radius = 3.1
FEATURE [Part::Cylinder] Cylinder165
  Angle = 360
  AttacherType = Attacher::AttachEngine3D
  Height = 4
  Placement = pos=(606,7,6) rot=(0,1,0;1.5708rad)
  Radius = 3.1
FEATURE [Part::MultiFuse] Fusion144
  Refine = true
  Shapes = -> [Cylinder162,Cylinder165,Cylinder163,Cylinder164]
FEATURE [Part::Cut] Cut092
  Base = -> Cut091
  Refine = true
  Tool = -> Fusion144
FEATURE [Part::Cylinder] Cylinder166
  Angle = 360
  AttacherType = Attacher::AttachEngine3D
  Height = 10
  Placement = pos=(604.475,6,-27.2709) rot=(0,1,0;1.309rad)
  Radius = 1.1
FEATURE [Part::Cut] Cut093
  Base = -> Cut092
  Refine = true
  Tool = -> Cylinder166
FEATURE [Part::Cylinder] Cylinder167
  Angle = 360
  AttacherType = Attacher::AttachEngine3D
  Height = 6
  Placement = pos=(605,11,-7) rot=(1,0,0;1.5708rad)
  Radius = 0.9
FEATURE [Part::Cylinder] Cylinder168
  Angle = 360
  AttacherType = Attacher::AttachEngine3D
  Height = 6
  Placement = pos=(605,11,0) rot=(1,0,0;1.5708rad)
  Radius = 0.9
FEATURE [Part::MultiFuse] Fusion145
  Placement = pos=(0,-4,0) rot=(0,0,1;0rad)
  Refine = true
  Shapes = -> [Cylinder168,Cylinder167]
FEATURE [Part::Cut] Cut094  label="left-bumper-holder"
  Base = -> Cut093
  Placement = pos=(0,-10,0) rot=(0,0,1;0rad)
  Refine = true
  Tool = -> Fusion145
FEATURE [Part::MultiFuse] Fusion146
  Placement = pos=(0,-4,0) rot=(0,0,1;0rad)
  Refine = true
  Shapes = -> [Cylinder168,Cylinder167]
FEATURE [Part::Cut] Cut096
  Base = -> Cut092
  Refine = true
  Tool = -> Cylinder166
FEATURE [Part::Cut] Cut095  label="left-bumper-holder001"
  Base = -> Cut096
  Refine = true
  Tool = -> Fusion146
FEATURE [Part::Mirroring] Part__Mirroring002  label="right-bumper-holder"
  Base = (0,0,0)
  Normal = (0,0,1)
  Placement = pos=(0,72,0) rot=(0,0,1;0rad)
  Source = -> Cut095
FEATURE [Part::Box] Box078  label="Cube048"
  AttacherType = Attacher::AttachEngine3D
  Height = 20
  Length = 70
  Placement = pos=(530,0,0) rot=(0,0,1;0rad)
  Width = 62
FEATURE [Part::Cut] Cut097  label="frame"
  Base = -> Cut010
  Placement = pos=(70,0,0) rot=(0,0,1;0rad)
  Refine = true
  Tool = -> Box078
FEATURE [Part::MultiFuse] Fusion147  label="motor-threaded-bar-METAL"
  Placement = pos=(81,0,0) rot=(0,0,1;0rad)
  Refine = true
  Shapes = -> [Cylinder048,Cylinder049]
FEATURE [Part::Box] Box079  label="Cube049"
  AttacherType = Attacher::AttachEngine3D
  Height = 11
  Length = 25
  Placement = pos=(-24,0,9) rot=(0,0,1;0rad)
  Width = 62
FEATURE [Part::Box] Box083  label="Cube051"
  AttacherType = Attacher::AttachEngine3D
  Height = 1.5
  Length = 25
  Placement = pos=(-24,10,19) rot=(0,0,1;0rad)
  Width = 42
FEATURE [Part::Box] Box084  label="Cube052"
  AttacherType = Attacher::AttachEngine3D
  Height = 10
  Length = 30
  Placement = pos=(-29,0,7) rot=(0,1,0;0.296706rad)
  Width = 62
FEATURE [Part::MultiFuse] Fusion149
  Placement = pos=(-1,0,4) rot=(0,0,1;0rad)
  Refine = true
  Shapes = -> [Cylinder001,Cylinder002,Cylinder003]
FEATURE [Part::Fillet] Fillet044
  Base = -> Box008
  Edges = 2 edges r=3: [Edge10,Edge12]
FEATURE [Part::Cut] Cut098
  Base = -> Box079
  Refine = true
  Tool = -> Box083
FEATURE [Part::Fillet] Fillet045
  Base = -> Cut098
  Edges = 2 edges r=3: [Edge11,Edge18]
FEATURE [Part::MultiFuse] Fusion150
  Refine = true
  Shapes = -> [Fillet044,Fillet045]
FEATURE [Part::Cut] Cut099
  Base = -> Fusion150
  Refine = true
  Tool = -> Box084
FEATURE [Part::Cut] Cut100
  Base = -> Cut099
  Refine = true
  Tool = -> Cylinder
FEATURE [Part::Cut] Cut101
  Base = -> Cut100
  Refine = true
  Tool = -> Fusion009
FEATURE [Part::Cut] Cut102
  Base = -> Cut101
  Refine = true
  Tool = -> Fusion149
FEATURE [Part::Fillet] Fillet046
  Base = -> Cut102
  Edges = 2 edges r=3: [Edge19,Edge56]
  Placement = pos=(69,0,0) rot=(0,0,1;0rad)
FEATURE [Part::Box] Box086  label="Cube054"
  AttacherType = Attacher::AttachEngine3D
  Height = 8
  Length = 8
  Placement = pos=(45,44.5,19) rot=(0,0,1;0rad)
  Width = 5
FEATURE [Part::Box] Box087  label="Cube055"
  AttacherType = Attacher::AttachEngine3D
  Height = 15
  Length = 24
  Placement = pos=(45,42,19) rot=(0,0,1;0rad)
  Width = 10
FEATURE [Part::Cut] Cut103
  Base = -> Box087
  Refine = true
  Tool = -> Box086
FEATURE [Part::Box] Box088  label="Cube056"
  AttacherType = Attacher::AttachEngine3D
  Height = 11
  Length = 1.8
  Placement = pos=(53,43.5,19) rot=(0,0,1;0rad)
  Width = 7
FEATURE [Part::Cut] Cut104
  Base = -> Cut103
  Refine = true
  Tool = -> Box088
FEATURE [Part::Box] Box089  label="Cube057"
  AttacherType = Attacher::AttachEngine3D
  Height = 8
  Length = 4
  Placement = pos=(54,44.5,19) rot=(0,0,1;0rad)
  Width = 5
FEATURE [Part::Cut] Cut105
  Base = -> Cut104
  Refine = true
  Tool = -> Box089
FEATURE [Part::Cylinder] Cylinder169
  Angle = 360
  AttacherType = Attacher::AttachEngine3D
  Height = 10
  Placement = pos=(57,52,30) rot=(1,0,0;1.5708rad)
  Radius = 1.6
FEATURE [Part::Box] Box090  label="Cube058"
  AttacherType = Attacher::AttachEngine3D
  Height = 5
  Length = 19
  Placement = pos=(54,44.5,19) rot=(0,0,1;0rad)
  Width = 5
FEATURE [Part::Cut] Cut106
  Base = -> Cut105
  Refine = true
  Tool = -> Box090
FEATURE [Part::Cut] Cut107
  Base = -> Cut106
  Refine = true
  Tool = -> Cylinder169
FEATURE [Part::Fillet] Fillet047
  Base = -> Cut107
  Edges = 2 edges r=6: [Edge1,Edge10]
  Placement = pos=(0,-32,0) rot=(0,0,1;0rad)
FEATURE [Part::Cut] Cut108
  Base = -> Cut106
  Refine = true
  Tool = -> Cylinder169
FEATURE [Part::Fillet] Fillet048
  Base = -> Cut108
  Edges = 2 edges r=6: [Edge1,Edge10]
FEATURE [Part::Box] Box091  label="Cube059"
  AttacherType = Attacher::AttachEngine3D
  Height = 3
  Length = 24
  Placement = pos=(45,20,19) rot=(0,0,1;0rad)
  Width = 22
FEATURE [Part::MultiFuse] Fusion151
  Refine = true
  Shapes = -> [Fillet047,Fillet048,Box091]
FEATURE [Part::Cylinder] Cylinder170
  Angle = 360
  AttacherType = Attacher::AttachEngine3D
  Height = 10
  Placement = pos=(50,38,12) rot=(0,0,1;0rad)
  Radius = 1.6
FEATURE [Part::Cylinder] Cylinder171
  Angle = 360
  AttacherType = Attacher::AttachEngine3D
  Height = 10
  Placement = pos=(50,24,12) rot=(0,0,1;0rad)
  Radius = 1.6
FEATURE [Part::Cylinder] Cylinder172
  Angle = 360
  AttacherType = Attacher::AttachEngine3D
  Height = 10
  Placement = pos=(64,38,12) rot=(0,0,1;0rad)
  Radius = 1.6
FEATURE [Part::Cylinder] Cylinder173
  Angle = 360
  AttacherType = Attacher::AttachEngine3D
  Height = 10
  Placement = pos=(64,24,12) rot=(0,0,1;0rad)
  Radius = 1.6
FEATURE [Part::MultiFuse] Fusion152
  Refine = true
  Shapes = -> [Cylinder170,Cylinder171,Cylinder173,Cylinder172]
FEATURE [Part::Cylinder] Cylinder174
  Angle = 360
  AttacherType = Attacher::AttachEngine3D
  Height = 4
  Placement = pos=(50,24,15) rot=(0,0,1;0rad)
  Radius = 1.2
FEATURE [Part::Cylinder] Cylinder175
  Angle = 360
  AttacherType = Attacher::AttachEngine3D
  Height = 4
  Placement = pos=(50,38,15) rot=(0,0,1;0rad)
  Radius = 1.2
FEATURE [Part::Cylinder] Cylinder176
  Angle = 360
  AttacherType = Attacher::AttachEngine3D
  Height = 8
  Placement = pos=(64,24,11) rot=(0,0,1;0rad)
  Radius = 1.2
FEATURE [Part::Cylinder] Cylinder177
  Angle = 360
  AttacherType = Attacher::AttachEngine3D
  Height = 8
  Placement = pos=(64,38,11) rot=(0,0,1;0rad)
  Radius = 1.2
FEATURE [Part::MultiFuse] Fusion153
  Refine = true
  Shapes = -> [Cylinder175,Cylinder174,Cylinder176,Cylinder177]
FEATURE [Part::Cut] Cut109  label="fifth-wheel-plate_"
  Base = -> Fillet046
  Refine = true
  Tool = -> Fusion153
FEATURE [Part::Cut] Cut110  label="fake-cylinder-holder"
  Base = -> Fusion151
  Refine = true
  Tool = -> Fusion152
FEATURE [Part::Cylinder] Cylinder178
  Angle = 360
  AttacherType = Attacher::AttachEngine3D
  Height = 62
  Placement = pos=(67,15,19) rot=(0,1,0;1.5708rad)
  Radius = 3
FEATURE [Part::Cylinder] Cylinder179
  Angle = 360
  AttacherType = Attacher::AttachEngine3D
  Height = 62
  Placement = pos=(67,47,19) rot=(0,1,0;1.5708rad)
  Radius = 3
FEATURE [Part::MultiFuse] Fusion154
  Refine = true
  Shapes = -> [Cylinder179,Cylinder178]
FEATURE [Part::Cut] Cut111  label="fifth-wheel-plate"
  Base = -> Cut109
  Refine = true
  Tool = -> Fusion154
FEATURE [Part::Box] Box092  label="Cube060"
  AttacherType = Attacher::AttachEngine3D
  Height = 15
  Length = 135
  Placement = pos=(435,0,5) rot=(0,0,1;0rad)
  Width = 10
FEATURE [Part::Box] Box093  label="Cube061"
  AttacherType = Attacher::AttachEngine3D
  Height = 15
  Length = 135
  Placement = pos=(435,-4,5) rot=(0,0,1;0rad)
  Width = 10
FEATURE [Part::Fillet] Fillet049
  Base = -> Box092
  Edges = 1 edges r=3: [Edge10]
FEATURE [Part::Cut] Cut112
  Base = -> Box093
  Refine = true
  Tool = -> Fillet049
FEATURE [Part::Cylinder] Cylinder180
  Angle = 360
  AttacherType = Attacher::AttachEngine3D
  Height = 10
  Placement = pos=(441,0,10) rot=(1,0,0;1.5708rad)
  Radius = 1.25
FEATURE [Part::Cylinder] Cylinder181
  Angle = 360
  AttacherType = Attacher::AttachEngine3D
  Height = 10
  Placement = pos=(459,0,10) rot=(1,0,0;1.5708rad)
  Radius = 1.25
FEATURE [Part::Cylinder] Cylinder182
  Angle = 360
  AttacherType = Attacher::AttachEngine3D
  Height = 10
  Placement = pos=(546,0,10) rot=(1,0,0;1.5708rad)
  Radius = 1.25
FEATURE [Part::Cylinder] Cylinder183
  Angle = 360
  AttacherType = Attacher::AttachEngine3D
  Height = 10
  Placement = pos=(564,0,10) rot=(1,0,0;1.5708rad)
  Radius = 1.25
FEATURE [Part::MultiFuse] Fusion155
  Refine = true
  Shapes = -> [Cylinder180,Cylinder183,Cylinder182,Cylinder181]
FEATURE [Part::Cut] Cut113  label="fenders-holes"
  Base = -> Cut112
  Refine = true
  Tool = -> Fusion155
FEATURE [Part::Box] Box094  label="Cube062"
  AttacherType = Attacher::AttachEngine3D
  Height = 50
  Length = 20
  Placement = pos=(250,-25,-50) rot=(0,0,1;0rad)
  Width = 20
FEATURE [Part::Box] Box095  label="Cube063"
  AttacherType = Attacher::AttachEngine3D
  Height = 50
  Length = 14
  Placement = pos=(253,-22,-50) rot=(0,0,1;0rad)
  Width = 14
FEATURE [Part::Box] Box096  label="floor"
  AttacherType = Attacher::AttachEngine3D
  Height = 1
  Length = 600
  Placement = pos=(31,-70,-112) rot=(0,-1,0;0.05236rad)
  Width = 200
FEATURE [Part::Box] Box097  label="Cube064"
  AttacherType = Attacher::AttachEngine3D
  Height = 60
  Length = 14
  Placement = pos=(253,-22,-66) rot=(0,0,1;0rad)
  Width = 14
FEATURE [Part::Cut] Cut114
  Base = -> Box094
  Placement = pos=(0,0,-3) rot=(0,0,1;0rad)
  Refine = true
  Tool = -> Box095
FEATURE [Part::Fillet] Fillet050
  Base = -> Box097
  Edges = 2 edges r=5: [Edge4,Edge8]
FEATURE [Part::Box] Box098  label="Cube065"
  AttacherType = Attacher::AttachEngine3D
  Height = 5
  Length = 22
  Placement = pos=(249,-26,-74) rot=(0,0,1;0rad)
  Width = 22
FEATURE [Part::Box] Box099  label="Cube066"
  AttacherType = Attacher::AttachEngine3D
  Height = 10
  Length = 22
  Placement = pos=(249,-26,-66) rot=(0,0,1;0rad)
  Width = 5.2
FEATURE [Part::Box] Box100  label="Cube067"
  AttacherType = Attacher::AttachEngine3D
  Height = 10
  Length = 22
  Placement = pos=(249,-9.2,-66) rot=(0,0,1;0rad)
  Width = 5.2
FEATURE [Part::MultiFuse] Fusion156
  Refine = true
  Shapes = -> [Box100,Box099]
FEATURE [Part::Cut] Cut115
  Base = -> Fillet050
  Refine = true
  Tool = -> Fusion156
FEATURE [Part::Box] Box101  label="Cube068"
  AttacherType = Attacher::AttachEngine3D
  Height = 10
  Length = 16
  Placement = pos=(252,-9,-69) rot=(0,0,1;0rad)
  Width = 3
FEATURE [Part::Box] Box102  label="Cube069"
  AttacherType = Attacher::AttachEngine3D
  Height = 10
  Length = 16
  Placement = pos=(252,-26,-69) rot=(0,0,1;0rad)
  Width = 3
FEATURE [Part::Fillet] Fillet051
  Base = -> Box101
  Edges = 2 edges r=6: [Edge2,Edge6]
FEATURE [Part::Fillet] Fillet052
  Base = -> Box102
  Edges = 2 edges r=6: [Edge2,Edge6]
  Placement = pos=(0,2,0) rot=(0,0,1;0rad)
FEATURE [Part::Cylinder] Cylinder184
  Angle = 360
  AttacherType = Attacher::AttachEngine3D
  Height = 30
  Placement = pos=(260,0,-61) rot=(1,0,0;1.5708rad)
  Radius = 1.5
FEATURE [Part::MultiFuse] Fusion157
  Refine = true
  Shapes = -> [Fillet051,Fillet052,Box098]
FEATURE [Part::Fillet] Fillet053
  Base = -> Fusion157
  Edges = 4 edges r=2: [Edge10,Edge12,Edge14,Edge16]
FEATURE [Part::Fillet] Fillet054
  Base = -> Fillet053
  Edges = 4 edges r=1: [Edge39,Edge40,Edge42,Edge44]
  Placement = pos=(0,0,2) rot=(0,0,1;0rad)
FEATURE [Part::Cut] Cut116
  Base = -> Fillet054
  Placement = pos=(0,0,10) rot=(0,0,1;0rad)
  Refine = true
  Tool = -> Cylinder184
FEATURE [Part::Cylinder] Cylinder185
  Angle = 360
  AttacherType = Attacher::AttachEngine3D
  Height = 30
  Placement = pos=(260,0,-61) rot=(1,0,0;1.5708rad)
  Radius = 1.7
FEATURE [Part::Cut] Cut117
  Base = -> Cut115
  Refine = true
  Tool = -> Cylinder185
FEATURE [Part::Cylinder] Cylinder186
  Angle = 360
  AttacherType = Attacher::AttachEngine3D
  Height = 50
  Placement = pos=(260,-15,-56) rot=(0,0,1;0rad)
  Radius = 2.6
FEATURE [Part::Cut] Cut118
  Base = -> Cut117
  Refine = true
  Tool = -> Cylinder186
FEATURE [Part::Box] Box103  label="Cube070"
  AttacherType = Attacher::AttachEngine3D
  Height = 4
  Length = 14
  Placement = pos=(253,-19,-12) rot=(0,0,1;0rad)
  Width = 8
FEATURE [Part::Cut] Cut119
  Base = -> Cut118
  Placement = pos=(0,0,10) rot=(0,0,1;0rad)
  Refine = true
  Tool = -> Box103
FEATURE [Part::MultiFuse] Fusion158
  Placement = pos=(0,0,-43) rot=(0,0,1;0rad)
  Refine = true
  Shapes = -> [Cut116,Cut119]
FEATURE [Part::Cylinder] Cylinder187
  Angle = 360
  AttacherType = Attacher::AttachEngine3D
  Height = 20
  Placement = pos=(586,31,1.5) rot=(0,0,1;0rad)
  Radius = 1.25
FEATURE [Part::Cut] Cut120  label="rear-cross-member_001"
  Base = -> Cut017
  Refine = true
  Tool = -> Cylinder187
FEATURE [Part::Cylinder] Cylinder188
  Angle = 360
  AttacherType = Attacher::AttachEngine3D
  Height = 8
  Placement = pos=(584,7,10.5) rot=(0,0,1;0rad)
  Radius = 2
FEATURE [Part::Cylinder] Cylinder189
  Angle = 360
  AttacherType = Attacher::AttachEngine3D
  Height = 8
  Placement = pos=(584,55,10.5) rot=(0,0,1;0rad)
  Radius = 2
FEATURE [Part::MultiFuse] Fusion159
  Placement = pos=(0.5,0,0) rot=(0,0,1;0rad)
  Refine = true
  Shapes = -> [Cylinder189,Cylinder188]
FEATURE [Part::Cut] Cut121  label="rear-cross-member"
  Base = -> Cut120
  Refine = true
  Tool = -> Fusion159
FEATURE [Part::Box] Box104  label="Cube169"
  AttacherType = Attacher::AttachEngine3D
  Height = 65
  Length = 18
  Placement = pos=(352,-6,-65) rot=(0,0,1;0rad)
  Width = 16
FEATURE [Part::Box] Box105  label="Cube173"
  AttacherType = Attacher::AttachEngine3D
  Height = 60
  Length = 12.5
  Placement = pos=(353.75,-4.25,-65) rot=(0,0,1;0rad)
  Width = 12.5
FEATURE [Part::Cut] Cut125
  Base = -> Box104
  Refine = true
  Tool = -> Box105
FEATURE [Part::Box] Box106  label="Cube174"
  AttacherType = Attacher::AttachEngine3D
  Height = 12.5
  Length = 12
  Placement = pos=(363.75,-10,-55.25) rot=(0,0,1;0rad)
  Width = 20
FEATURE [Part::Cut] Cut124
  Base = -> Cut125
  Refine = true
  Tool = -> Box106
FEATURE [Part::Cylinder] Cylinder194  label="Cylinder483"
  Angle = 360
  AttacherType = Attacher::AttachEngine3D
  Height = 10
  Placement = pos=(323,0,-59) rot=(0,1,0;1.5708rad)
  Radius = 1.25
FEATURE [Part::Cylinder] Cylinder195  label="Cylinder482"
  Angle = 360
  AttacherType = Attacher::AttachEngine3D
  Height = 10
  Placement = pos=(323,0,-39) rot=(0,1,0;1.5708rad)
  Radius = 1.25
FEATURE [Part::MultiFuse] Fusion167
  Placement = pos=(40,2,0) rot=(0,0,1;0rad)
  Refine = true
  Shapes = -> [Cylinder194,Cylinder195]
FEATURE [Part::Box] Box115  label="Cube196"
  AttacherType = Attacher::AttachEngine3D
  Height = 65
  Length = 18
  Placement = pos=(352,-6,-65) rot=(0,0,1;0rad)
  Width = 16
FEATURE [Part::Box] Box116  label="Cube197"
  AttacherType = Attacher::AttachEngine3D
  Height = 60
  Length = 12.5
  Placement = pos=(353.75,-4.25,-65) rot=(0,0,1;0rad)
  Width = 12.5
FEATURE [Part::Cut] Cut135
  Base = -> Box115
  Refine = true
  Tool = -> Box116
FEATURE [Part::Box] Box117  label="Cube198"
  AttacherType = Attacher::AttachEngine3D
  Height = 12.5
  Length = 12
  Placement = pos=(363.75,-10,-55.25) rot=(0,0,1;0rad)
  Width = 20
FEATURE [Part::Cut] Cut134
  Base = -> Cut135
  Refine = true
  Tool = -> Box117
FEATURE [Part::Cylinder] Cylinder204  label="Cylinder491"
  Angle = 360
  AttacherType = Attacher::AttachEngine3D
  Height = 10
  Placement = pos=(323,0,-59) rot=(0,1,0;1.5708rad)
  Radius = 1.25
FEATURE [Part::Cylinder] Cylinder205  label="Cylinder492"
  Angle = 360
  AttacherType = Attacher::AttachEngine3D
  Height = 10
  Placement = pos=(323,0,-39) rot=(0,1,0;1.5708rad)
  Radius = 1.25
FEATURE [Part::MultiFuse] Fusion175
  Placement = pos=(40,2,0) rot=(0,0,1;0rad)
  Refine = true
  Shapes = -> [Cylinder204,Cylinder205]
FEATURE [Part::Box] Box126  label="Cube222"
  AttacherType = Attacher::AttachEngine3D
  Height = 12
  Length = 12
  Placement = pos=(324,-6,-55) rot=(0,0,1;0rad)
  Width = 16
FEATURE [Part::Box] Box127  label="Cube223"
  AttacherType = Attacher::AttachEngine3D
  Height = 26
  Length = 2
  Placement = pos=(330,-6,-62) rot=(0,0,1;0rad)
  Width = 16
FEATURE [Part::Box] Box128  label="Cube224"
  AttacherType = Attacher::AttachEngine3D
  Height = 14
  Length = 4
  Placement = pos=(332,-6,-56) rot=(0,0,1;0rad)
  Width = 16
FEATURE [Part::MultiFuse] Fusion179
  Refine = true
  Shapes = -> [Box126,Box127,Box128]
FEATURE [Part::Box] Box129  label="Cube221"
  AttacherType = Attacher::AttachEngine3D
  Height = 12
  Length = 10
  Placement = pos=(324,-4.25,-55) rot=(0,0,1;0rad)
  Width = 12.5
FEATURE [Part::Cut] Cut146
  Base = -> Fusion179
  Refine = true
  Tool = -> Box129
FEATURE [Part::Box] Box130  label="Cube228"
  AttacherType = Attacher::AttachEngine3D
  Height = 12
  Length = 12
  Placement = pos=(324,-6,-55) rot=(0,0,1;0rad)
  Width = 16
FEATURE [Part::Box] Box131  label="Cube225"
  AttacherType = Attacher::AttachEngine3D
  Height = 26
  Length = 2
  Placement = pos=(330,-6,-62) rot=(0,0,1;0rad)
  Width = 16
FEATURE [Part::Box] Box132  label="Cube226"
  AttacherType = Attacher::AttachEngine3D
  Height = 14
  Length = 4
  Placement = pos=(332,-6,-56) rot=(0,0,1;0rad)
  Width = 16
FEATURE [Part::MultiFuse] Fusion180
  Refine = true
  Shapes = -> [Box130,Box131,Box132]
FEATURE [Part::Box] Box133  label="Cube227"
  AttacherType = Attacher::AttachEngine3D
  Height = 12
  Length = 10
  Placement = pos=(324,-4.25,-55) rot=(0,0,1;0rad)
  Width = 12.5
FEATURE [Part::Cut] Cut147
  Base = -> Fusion180
  Placement = pos=(0,76,0) rot=(0,0,1;0rad)
  Refine = true
  Tool = -> Box133
FEATURE [Part::Box] Box134  label="Cube233"
  AttacherType = Attacher::AttachEngine3D
  Height = 6
  Length = 8
  Placement = pos=(328,6.25,-52) rot=(0,0,1;0rad)
  Width = 2
FEATURE [Part::Box] Box135  label="Cube234"
  AttacherType = Attacher::AttachEngine3D
  Height = 6
  Length = 8
  Placement = pos=(328,-4.5,-52) rot=(0,0,1;0rad)
  Width = 2
FEATURE [Part::MultiFuse] Fusion181
  Refine = true
  Shapes = -> [Box134,Box135]
FEATURE [Part::Fillet] Fillet057
  Base = -> Fusion181
  Edges = 4 edges r=2.5: [Edge2,Edge4,Edge14,Edge16]
  Placement = pos=(-1.5,0,0) rot=(0,0,1;0rad)
FEATURE [Part::Box] Box136  label="Cube236"
  AttacherType = Attacher::AttachEngine3D
  Height = 6
  Length = 8
  Placement = pos=(328,6.25,-52) rot=(0,0,1;0rad)
  Width = 2
FEATURE [Part::Box] Box137  label="Cube235"
  AttacherType = Attacher::AttachEngine3D
  Height = 6
  Length = 8
  Placement = pos=(328,-4.5,-52) rot=(0,0,1;0rad)
  Width = 2
FEATURE [Part::MultiFuse] Fusion182
  Refine = true
  Shapes = -> [Box136,Box137]
FEATURE [Part::Fillet] Fillet058
  Base = -> Fusion182
  Edges = 4 edges r=2.5: [Edge2,Edge4,Edge14,Edge16]
  Placement = pos=(-1.5,76.25,0) rot=(0,0,1;0rad)
FEATURE [Part::MultiFuse] Fusion178
  Refine = true
  Shapes = -> [Cut146,Cut147,Fillet057,Fillet058]
FEATURE [Part::Cylinder] Cylinder206  label="Cylinder498"
  Angle = 360
  AttacherType = Attacher::AttachEngine3D
  Height = 92
  Placement = pos=(329.25,86,-49) rot=(1,0,0;1.5708rad)
  Radius = 1.6
FEATURE [Part::Cut] Cut145
  Base = -> Fusion178
  Refine = true
  Tool = -> Cylinder206
FEATURE [Part::Cylinder] Cylinder207  label="Cylinder501"
  Angle = 360
  AttacherType = Attacher::AttachEngine3D
  Height = 10
  Placement = pos=(323,0,-59) rot=(0,1,0;1.5708rad)
  Radius = 1.6
FEATURE [Part::Cylinder] Cylinder208  label="Cylinder500"
  Angle = 360
  AttacherType = Attacher::AttachEngine3D
  Height = 10
  Placement = pos=(323,0,-39) rot=(0,1,0;1.5708rad)
  Radius = 1.6
FEATURE [Part::MultiFuse] Fusion184
  Placement = pos=(3,2,0) rot=(0,0,1;0rad)
  Refine = true
  Shapes = -> [Cylinder207,Cylinder208]
FEATURE [Part::Cylinder] Cylinder209  label="Cylinder502"
  Angle = 360
  AttacherType = Attacher::AttachEngine3D
  Height = 10
  Placement = pos=(323,0,-59) rot=(0,1,0;1.5708rad)
  Radius = 1.6
FEATURE [Part::Cylinder] Cylinder210  label="Cylinder503"
  Angle = 360
  AttacherType = Attacher::AttachEngine3D
  Height = 10
  Placement = pos=(323,0,-39) rot=(0,1,0;1.5708rad)
  Radius = 1.6
FEATURE [Part::MultiFuse] Fusion185
  Placement = pos=(3,78,0) rot=(0,0,1;0rad)
  Refine = true
  Shapes = -> [Cylinder209,Cylinder210]
FEATURE [Part::MultiFuse] Fusion183
  Refine = true
  Shapes = -> [Fusion184,Fusion185]
FEATURE [Part::Cut] Cut144
  Base = -> Cut145
  Refine = true
  Tool = -> Fusion183
FEATURE [Part::Box] Box138  label="Cube237"
  AttacherType = Attacher::AttachEngine3D
  Height = 10
  Length = 10
  Placement = pos=(326,10,-54) rot=(0,0,1;0rad)
  Width = 60
FEATURE [Part::Cylinder] Cylinder211  label="Cylinder499"
  Angle = 360
  AttacherType = Attacher::AttachEngine3D
  Height = 92
  Placement = pos=(329.25,86,-49) rot=(1,0,0;1.5708rad)
  Radius = 2
FEATURE [Part::Cut] Cut148
  Base = -> Box138
  Refine = true
  Tool = -> Cylinder211
FEATURE [Part::MultiFuse] Fusion177
  Refine = true
  Shapes = -> [Cut144,Cut148]
FEATURE [Part::Box] Box139  label="Cube238"
  AttacherType = Attacher::AttachEngine3D
  Height = 10
  Length = 10
  Placement = pos=(326,10,-54) rot=(0,0,1;0rad)
  Width = 10
FEATURE [Part::Cut] Cut143
  Base = -> Fusion177
  Refine = true
  Tool = -> Box139
FEATURE [Part::Cylinder] Cylinder212  label="Cylinder508"
  Angle = 360
  AttacherType = Attacher::AttachEngine3D
  Height = 30
  Placement = pos=(333.25,10,-34.25) rot=(1,0,0;1.5708rad)
  Radius = 2.75
FEATURE [Part::Box] Box140  label="Cube247"
  AttacherType = Attacher::AttachEngine3D
  Height = 10
  Length = 6
  Placement = pos=(330,-6,-37) rot=(0,0,1;0rad)
  Width = 16
FEATURE [Part::Box] Box141  label="Cube244"
  AttacherType = Attacher::AttachEngine3D
  Height = 26
  Length = 20
  Placement = pos=(316,10,-62) rot=(0,0,1;0rad)
  Width = 10
FEATURE [Part::Cylinder] Cylinder213  label="Cylinder507"
  Angle = 360
  AttacherType = Attacher::AttachEngine3D
  Height = 6
  Placement = pos=(329.25,18,-49) rot=(1,0,0;1.5708rad)
  Radius = 12.5
FEATURE [Part::Cut] Cut152
  Base = -> Box141
  Refine = true
  Tool = -> Cylinder213
FEATURE [Part::Box] Box142  label="Cube245"
  AttacherType = Attacher::AttachEngine3D
  Height = 9
  Length = 10
  Placement = pos=(326,10,-36) rot=(0,0,1;0rad)
  Width = 10
FEATURE [Part::MultiFuse] Fusion187
  Refine = true
  Shapes = -> [Cut152,Box142]
FEATURE [Part::Box] Box143  label="Cube246"
  AttacherType = Attacher::AttachEngine3D
  Height = 11
  Length = 10
  Placement = pos=(328,12,-40) rot=(0,0,1;0rad)
  Width = 6
FEATURE [Part::Cut] Cut151
  Base = -> Fusion187
  Refine = true
  Tool = -> Box143
FEATURE [Part::MultiFuse] Fusion186
  Refine = true
  Shapes = -> [Cylinder212,Box140,Cut151]
FEATURE [Part::Cylinder] Cylinder214  label="Cylinder510"
  Angle = 360
  AttacherType = Attacher::AttachEngine3D
  Height = 4
  Placement = pos=(332,2,-39) rot=(0,1,0;1.5708rad)
  Radius = 3
FEATURE [Part::Cut] Cut150
  Base = -> Fusion186
  Refine = true
  Tool = -> Cylinder214
FEATURE [Part::Cylinder] Cylinder215  label="Cylinder509"
  Angle = 360
  AttacherType = Attacher::AttachEngine3D
  Height = 47
  Placement = pos=(333.25,20,-34.25) rot=(1,0,0;1.5708rad)
  Radius = 1.55
FEATURE [Part::Cut] Cut149
  Base = -> Cut150
  Refine = true
  Tool = -> Cylinder215
FEATURE [Part::MultiFuse] Fusion176
  Refine = true
  Shapes = -> [Cut143,Cut149]
FEATURE [Part::Cylinder] Cylinder216  label="Cylinder511"
  Angle = 360
  AttacherType = Attacher::AttachEngine3D
  Height = 5
  Placement = pos=(331,8,-54) rot=(0,1,0;1.5708rad)
  Radius = 0.8
FEATURE [Part::Cylinder] Cylinder217  label="Cylinder512"
  Angle = 360
  AttacherType = Attacher::AttachEngine3D
  Height = 5
  Placement = pos=(331,23,-46) rot=(0,1,0;1.5708rad)
  Radius = 0.8
FEATURE [Part::Cylinder] Cylinder218  label="Cylinder513"
  Angle = 360
  AttacherType = Attacher::AttachEngine3D
  Height = 5
  Placement = pos=(331,8,-29) rot=(0,1,0;1.5708rad)
  Radius = 0.8
FEATURE [Part::MultiFuse] Fusion188
  Refine = true
  Shapes = -> [Cylinder216,Cylinder217,Cylinder218]
FEATURE [Part::Cut] Cut142
  Base = -> Fusion176
  Refine = true
  Tool = -> Fusion188
FEATURE [Part::Fillet] Fillet056
  Base = -> Cut142
  Edges = 3 edges r=3: [Edge70,Edge83,Edge169]
FEATURE [Part::Fillet] Fillet055  label="supports-reductor-frame"
  Base = -> Fillet056
  Edges = 6 edges r=4: [Edge5,Edge52,Edge134,Edge139,Edge148,Edge151]
  Placement = pos=(-80,-9,0) rot=(0,-1,0;0.05236rad)
FEATURE [Part::Box] Box144  label="Cube195"
  AttacherType = Attacher::AttachEngine3D
  Height = 8.5
  Length = 16
  Placement = pos=(311,8.5,-74) rot=(0,0,1;0rad)
  Width = 3.5
FEATURE [Part::Chamfer] Chamfer003
  Base = -> Box144
  Edges = 2 edges r=6.5: [Edge2,Edge6]
  Placement = pos=(1,-16.5,0) rot=(0,0,1;0rad)
FEATURE [Part::Box] Box145  label="Cube178"
  AttacherType = Attacher::AttachEngine3D
  Height = 3
  Length = 20
  Placement = pos=(310,-8,-74) rot=(0,0,1;0rad)
  Width = 20
FEATURE [Part::Cylinder] Cylinder219  label="Cylinder484"
  Angle = 360
  AttacherType = Attacher::AttachEngine3D
  Height = 13
  Placement = pos=(320,-4.5,-68) rot=(-1,0,0;1.5708rad)
  Radius = 4.65
FEATURE [Part::Cut] Cut154
  Base = -> Box145
  Refine = true
  Tool = -> Cylinder219
FEATURE [Part::Chamfer] Chamfer004
  Base = -> Cut154
  Edges = 2 edges r=2: [Edge9,Edge11]
FEATURE [Part::Box] Box146  label="Cube180"
  AttacherType = Attacher::AttachEngine3D
  Height = 8.5
  Length = 16
  Placement = pos=(311,8.5,-74) rot=(0,0,1;0rad)
  Width = 3.5
FEATURE [Part::Chamfer] Chamfer005
  Base = -> Box146
  Edges = 2 edges r=6.5: [Edge2,Edge6]
  Placement = pos=(1,0,0) rot=(0,0,1;0rad)
FEATURE [Part::MultiFuse] Fusion189
  Refine = true
  Shapes = -> [Chamfer003,Chamfer004,Chamfer005]
FEATURE [Part::Fillet] Fillet061
  Base = -> Fusion189
  Edges = 4 edges r=3: [Edge2,Edge3,Edge26,Edge40]
FEATURE [Part::Fillet] Fillet060
  Base = -> Fillet061
  Edges = 2 edges r=2.49: [Edge43,Edge44]
FEATURE [Part::Fillet] Fillet059
  Base = -> Fillet060
  Edges = 2 edges r=0.5: [Edge14,Edge32]
FEATURE [Part::Cylinder] Cylinder220  label="Cylinder479"
  Angle = 360
  AttacherType = Attacher::AttachEngine3D
  Height = 22
  Placement = pos=(320,13,-68) rot=(1,0,0;1.5708rad)
  Radius = 1.25
FEATURE [Part::Cut] Cut153  label="supports-left-foot"
  Base = -> Fillet059
  Placement = pos=(-77.3,-19,16) rot=(0,0,1;0rad)
  Refine = true
  Tool = -> Cylinder220
FEATURE [Part::Box] Box147  label="Cube216"
  AttacherType = Attacher::AttachEngine3D
  Height = 8.5
  Length = 16
  Placement = pos=(311,8.5,-74) rot=(0,0,1;0rad)
  Width = 3.5
FEATURE [Part::Chamfer] Chamfer006
  Base = -> Box147
  Edges = 2 edges r=6.5: [Edge2,Edge6]
  Placement = pos=(1,-16.5,0) rot=(0,0,1;0rad)
FEATURE [Part::Box] Box148  label="Cube217"
  AttacherType = Attacher::AttachEngine3D
  Height = 3
  Length = 20
  Placement = pos=(310,-8,-74) rot=(0,0,1;0rad)
  Width = 20
FEATURE [Part::Cylinder] Cylinder221  label="Cylinder493"
  Angle = 360
  AttacherType = Attacher::AttachEngine3D
  Height = 13
  Placement = pos=(320,-4.5,-68) rot=(-1,0,0;1.5708rad)
  Radius = 4.65
FEATURE [Part::Cut] Cut156
  Base = -> Box148
  Refine = true
  Tool = -> Cylinder221
FEATURE [Part::Chamfer] Chamfer007
  Base = -> Cut156
  Edges = 2 edges r=2: [Edge9,Edge11]
FEATURE [Part::Box] Box149  label="Cube218"
  AttacherType = Attacher::AttachEngine3D
  Height = 8.5
  Length = 16
  Placement = pos=(311,8.5,-74) rot=(0,0,1;0rad)
  Width = 3.5
FEATURE [Part::Chamfer] Chamfer008
  Base = -> Box149
  Edges = 2 edges r=6.5: [Edge2,Edge6]
  Placement = pos=(1,0,0) rot=(0,0,1;0rad)
FEATURE [Part::MultiFuse] Fusion190
  Refine = true
  Shapes = -> [Chamfer006,Chamfer007,Chamfer008]
FEATURE [Part::Fillet] Fillet064
  Base = -> Fusion190
  Edges = 4 edges r=3: [Edge2,Edge3,Edge26,Edge40]
FEATURE [Part::Fillet] Fillet063
  Base = -> Fillet064
  Edges = 2 edges r=2.49: [Edge43,Edge44]
FEATURE [Part::Fillet] Fillet062
  Base = -> Fillet063
  Edges = 2 edges r=0.5: [Edge14,Edge32]
FEATURE [Part::Cylinder] Cylinder222  label="Cylinder494"
  Angle = 360
  AttacherType = Attacher::AttachEngine3D
  Height = 22
  Placement = pos=(320,13,-68) rot=(1,0,0;1.5708rad)
  Radius = 1.25
FEATURE [Part::Cut] Cut155  label="supports-right-foot"
  Base = -> Fillet062
  Placement = pos=(-77.3,77,16) rot=(0,0,1;0rad)
  Refine = true
  Tool = -> Cylinder222
FEATURE [Part::Feature] difference
  Placement = pos=(369.25,6,-49) rot=(1,0,0;1.5708rad)
  shape: bbox 8.776 x 12 x 8.776 mm, 388 faces (baked)
FEATURE [Part::Cylinder] Cylinder223  label="Cylinder477"
  Angle = 360
  AttacherType = Attacher::AttachEngine3D
  Height = 12
  Placement = pos=(369.25,-6,-49) rot=(-1,0,0;1.5708rad)
  Radius = 1.65
FEATURE [Part::Cut] Cut158
  Base = -> difference
  Placement = pos=(-40,2,0) rot=(0,0,1;0rad)
  Refine = true
  Tool = -> Cylinder223
FEATURE [Part::Cylinder] Cylinder224  label="Cylinder495"
  Angle = 360
  AttacherType = Attacher::AttachEngine3D
  Height = 12
  Placement = pos=(329.25,8,-49) rot=(1,0,0;1.5708rad)
  Radius = 1.65
FEATURE [Part::Box] Box150  label="Cube219"
  AttacherType = Attacher::AttachEngine3D
  Height = 10
  Length = 10
  Placement = pos=(320.25,-4,-55) rot=(0,0,1;0rad)
  Width = 12
FEATURE [Part::Cut] Cut159
  Base = -> Cylinder224
  Refine = true
  Tool = -> Box150
FEATURE [Part::MultiFuse] Fusion191  label="supports-left-pinion_"
  Refine = true
  Shapes = -> [Cut158,Cut159]
FEATURE [Part::Box] Box151  label="Cube230"
  AttacherType = Attacher::AttachEngine3D
  Height = 10
  Length = 10
  Placement = pos=(324,6,-54) rot=(0,0,1;0rad)
  Width = 2
FEATURE [Part::Box] Box152  label="Cube229"
  AttacherType = Attacher::AttachEngine3D
  Height = 10
  Length = 10
  Placement = pos=(324,-4,-54) rot=(0,0,1;0rad)
  Width = 2
FEATURE [Part::MultiFuse] Fusion192
  Refine = true
  Shapes = -> [Box151,Box152]
FEATURE [Part::Cut] Cut157  label="supports-left-pinion"
  Base = -> Fusion191
  Placement = pos=(-80,-19,17) rot=(0,0,1;0rad)
  Refine = true
  Tool = -> Fusion192
FEATURE [Part::Feature] difference001
  Placement = pos=(369.25,6,-49) rot=(1,0,0;1.5708rad)
  shape: bbox 8.776 x 12 x 8.776 mm, 388 faces (baked)
FEATURE [Part::Cylinder] Cylinder225  label="Cylinder496"
  Angle = 360
  AttacherType = Attacher::AttachEngine3D
  Height = 12
  Placement = pos=(369.25,-6,-49) rot=(-1,0,0;1.5708rad)
  Radius = 1.65
FEATURE [Part::Cut] Cut161
  Base = -> difference001
  Placement = pos=(-40,2,0) rot=(0,0,1;0rad)
  Refine = true
  Tool = -> Cylinder225
FEATURE [Part::Cylinder] Cylinder226  label="Cylinder497"
  Angle = 360
  AttacherType = Attacher::AttachEngine3D
  Height = 12
  Placement = pos=(329.25,8,-49) rot=(1,0,0;1.5708rad)
  Radius = 1.65
FEATURE [Part::Box] Box153  label="Cube220"
  AttacherType = Attacher::AttachEngine3D
  Height = 10
  Length = 10
  Placement = pos=(320.25,-4,-55) rot=(0,0,1;0rad)
  Width = 12
FEATURE [Part::Cut] Cut162
  Base = -> Cylinder226
  Refine = true
  Tool = -> Box153
FEATURE [Part::MultiFuse] Fusion193  label="supports-right-pinion_"
  Placement = pos=(0,76,0) rot=(0,0,1;0rad)
  Refine = true
  Shapes = -> [Cut161,Cut162]
FEATURE [Part::Box] Box154  label="Cube232"
  AttacherType = Attacher::AttachEngine3D
  Height = 10
  Length = 10
  Placement = pos=(324,6,-54) rot=(0,0,1;0rad)
  Width = 2
FEATURE [Part::Box] Box155  label="Cube231"
  AttacherType = Attacher::AttachEngine3D
  Height = 10
  Length = 10
  Placement = pos=(324,-4,-54) rot=(0,0,1;0rad)
  Width = 2
FEATURE [Part::MultiFuse] Fusion194
  Placement = pos=(0,76,0) rot=(0,0,1;0rad)
  Refine = true
  Shapes = -> [Box154,Box155]
FEATURE [Part::Cut] Cut160  label="supports-right-pinion"
  Base = -> Fusion193
  Placement = pos=(-80,1,17) rot=(0,0,1;0rad)
  Refine = true
  Tool = -> Fusion194
FEATURE [Part::Feature] difference002
  Placement = pos=(369.25,6,-49) rot=(1,0,0;1.5708rad)
  shape: bbox 8.776 x 12 x 8.776 mm, 388 faces (baked)
FEATURE [Part::Cylinder] Cylinder227  label="Cylinder504"
  Angle = 360
  AttacherType = Attacher::AttachEngine3D
  Height = 12
  Placement = pos=(369.25,-6,-49) rot=(-1,0,0;1.5708rad)
  Radius = 1.65
FEATURE [Part::Cut] Cut165
  Base = -> difference002
  Placement = pos=(-40,2,0) rot=(0,0,1;0rad)
  Refine = true
  Tool = -> Cylinder227
FEATURE [Part::Cylinder] Cylinder228  label="Cylinder505"
  Angle = 360
  AttacherType = Attacher::AttachEngine3D
  Height = 12
  Placement = pos=(329.25,8,-49) rot=(1,0,0;1.5708rad)
  Radius = 1.65
FEATURE [Part::Box] Box156  label="Cube239"
  AttacherType = Attacher::AttachEngine3D
  Height = 10
  Length = 10
  Placement = pos=(320.25,-4,-55) rot=(0,0,1;0rad)
  Width = 12
FEATURE [Part::Cut] Cut166
  Base = -> Cylinder228
  Refine = true
  Tool = -> Box156
FEATURE [Part::MultiFuse] Fusion195  label="supports-left-pinion_001"
  Refine = true
  Shapes = -> [Cut165,Cut166]
FEATURE [Part::Box] Box157  label="Cube241"
  AttacherType = Attacher::AttachEngine3D
  Height = 10
  Length = 10
  Placement = pos=(324,6,-54) rot=(0,0,1;0rad)
  Width = 2
FEATURE [Part::Box] Box158  label="Cube240"
  AttacherType = Attacher::AttachEngine3D
  Height = 10
  Length = 10
  Placement = pos=(324,-4,-54) rot=(0,0,1;0rad)
  Width = 2
FEATURE [Part::MultiFuse] Fusion196
  Refine = true
  Shapes = -> [Box157,Box158]
FEATURE [Part::Cut] Cut164  label="supports-reductor-pinion_"
  Base = -> Fusion195
  Placement = pos=(0,14.25,0) rot=(0,0,1;0rad)
  Refine = true
  Tool = -> Fusion196
FEATURE [Part::Box] Box159  label="Cube242"
  AttacherType = Attacher::AttachEngine3D
  Height = 10
  Length = 10
  Placement = pos=(324,17.25,-54) rot=(0,0,1;0rad)
  Width = 15
FEATURE [Part::Cut] Cut163  label="supports-reductor-pinion"
  Base = -> Cut164
  Placement = pos=(-74.6,-18.75,32.1) rot=(0,0,1;0rad)
  Refine = true
  Tool = -> Box159
FEATURE [Part::Feature] difference003  label="supports-reductor-gear_"
  Placement = pos=(329.25,17.25,-49) rot=(1,0,0;1.5708rad)
  shape: bbox 23.99 x 5 x 23.99 mm, 1060 faces (baked)
FEATURE [Part::Cylinder] Cylinder229  label="Cylinder514"
  Angle = 360
  AttacherType = Attacher::AttachEngine3D
  Height = 5
  Placement = pos=(329.25,17.25,-49) rot=(1,0,0;1.5708rad)
  Radius = 1.65
FEATURE [Part::Cut] Cut167
  Base = -> difference003
  Refine = true
  Tool = -> Cylinder229
FEATURE [Part::Cylinder] Cylinder230  label="Cylinder506"
  Angle = 360
  AttacherType = Attacher::AttachEngine3D
  Height = 5
  Placement = pos=(329.25,8,-49) rot=(1,0,0;1.5708rad)
  Radius = 1.65
FEATURE [Part::Box] Box160  label="Cube243"
  AttacherType = Attacher::AttachEngine3D
  Height = 10
  Length = 10
  Placement = pos=(320.25,-4,-55) rot=(0,0,1;0rad)
  Width = 12
FEATURE [Part::Cut] Cut168
  Base = -> Cylinder230
  Placement = pos=(0,9.25,0) rot=(0,0,1;0rad)
  Refine = true
  Tool = -> Box160
FEATURE [Part::MultiFuse] Fusion197  label="supports-reductor-gear"
  Placement = pos=(-78,-19,17.2) rot=(0,0,1;0rad)
  Refine = true
  Shapes = -> [Cut167,Cut168]
FEATURE [Part::Cylinder] Cylinder231  label="Cylinder521"
  Angle = 360
  AttacherType = Attacher::AttachEngine3D
  Height = 3
  Placement = pos=(333.25,-23,-34.25) rot=(1,0,0;1.5708rad)
  Radius = 4
FEATURE [Part::Cylinder] Cylinder232  label="Cylinder520"
  Angle = 360
  AttacherType = Attacher::AttachEngine3D
  Height = 2
  Placement = pos=(333.25,-23,-34.25) rot=(1,0,0;1.5708rad)
  Radius = 1.65
FEATURE [Part::Cut] Cut169
  Base = -> Cylinder231
  Refine = true
  Tool = -> Cylinder232
FEATURE [Part::Fillet] Fillet065
  Base = -> Cut169
  Edges = 1 edges r=1: [Edge1]
FEATURE [Part::Cylinder] Cylinder233  label="Cylinder518"
  Angle = 360
  AttacherType = Attacher::AttachEngine3D
  Height = 5
  Placement = pos=(329.25,8,-49) rot=(1,0,0;1.5708rad)
  Radius = 1.65
FEATURE [Part::Box] Box161  label="Cube257"
  AttacherType = Attacher::AttachEngine3D
  Height = 10
  Length = 10
  Placement = pos=(320.25,-4,-55) rot=(0,0,1;0rad)
  Width = 12
FEATURE [Part::Cut] Cut171
  Base = -> Cylinder233
  Placement = pos=(4,-28,14.75) rot=(0,0,1;0rad)
  Refine = true
  Tool = -> Box161
FEATURE [Part::Cylinder] Cylinder234  label="Cylinder516"
  Angle = 360
  AttacherType = Attacher::AttachEngine3D
  Height = 5
  Placement = pos=(333.25,-20,-34.25) rot=(1,0,0;1.5708rad)
  Radius = 13
FEATURE [Part::Cylinder] Cylinder235  label="Cylinder517"
  Angle = 360
  AttacherType = Attacher::AttachEngine3D
  Height = 5
  Placement = pos=(333.25,-20,-34.25) rot=(1,0,0;1.5708rad)
  Radius = 1.65
FEATURE [Part::Cut] Cut172
  Base = -> Cylinder234
  Refine = true
  Tool = -> Cylinder235
FEATURE [Part::MultiFuse] Fusion199
  Refine = true
  Shapes = -> [Cut171,Cut172]
FEATURE [Part::Cylinder] Cylinder236  label="Cylinder519"
  Angle = 360
  AttacherType = Attacher::AttachEngine3D
  Height = 2
  Placement = pos=(333.25,-23,-34.25) rot=(1,0,0;1.5708rad)
  Radius = 11
FEATURE [Part::Cut] Cut170
  Base = -> Fusion199
  Refine = true
  Tool = -> Cylinder236
FEATURE [Part::Fillet] Fillet067
  Base = -> Cut170
  Edges = 2 edges r=0.99: [Edge1,Edge4]
FEATURE [Part::Fillet] Fillet066
  Base = -> Fillet067
  Edges = 1 edges r=1: [Edge3]
FEATURE [Part::MultiFuse] Fusion198  label="supports-wheel"
  Placement = pos=(-78.7,-9,17.5) rot=(0,0,1;0rad)
  Refine = true
  Shapes = -> [Fillet065,Fillet066]
FEATURE [Part::Box] Box162  label="Cube170"
  AttacherType = Attacher::AttachEngine3D
  Height = 70
  Length = 12
  Placement = pos=(354,-6,-73) rot=(0,0,1;0rad)
  Width = 12
FEATURE [Part::Box] Box163  label="Cube172"
  AttacherType = Attacher::AttachEngine3D
  Height = 49
  Length = 5
  Placement = pos=(361.75,-6,-52) rot=(0,0,1;0rad)
  Width = 12
FEATURE [Part::Cut] Cut178
  Base = -> Box162
  Refine = true
  Tool = -> Box163
FEATURE [Part::Feature] union
  Placement = pos=(362.75,0,-29) rot=(0,0,1;0rad)
  shape: bbox 4.337 x 12 x 50 mm, 106 faces (baked)
FEATURE [Part::MultiFuse] Fusion201
  Refine = true
  Shapes = -> [Cut178,union]
FEATURE [Part::Box] Box164  label="Cube182"
  AttacherType = Attacher::AttachEngine3D
  Height = 10
  Length = 17
  Placement = pos=(353,-6,-4) rot=(0,0,1;0rad)
  Width = 12
FEATURE [Part::Cut] Cut177
  Base = -> Fusion201
  Refine = true
  Tool = -> Box164
FEATURE [Part::Box] Box165  label="Cube183"
  AttacherType = Attacher::AttachEngine3D
  Height = 4
  Length = 2.99
  Placement = pos=(361.5,-6,-52) rot=(0,0,1;0rad)
  Width = 12
FEATURE [Part::MultiFuse] Fusion200
  Refine = true
  Shapes = -> [Cut177,Box165]
FEATURE [Part::Box] Box166  label="Cube176"
  AttacherType = Attacher::AttachEngine3D
  Height = 10
  Length = 10
  Placement = pos=(344,-6,-73) rot=(0,1,0;0.785398rad)
  Width = 12
FEATURE [Part::Mirroring] Part__Mirroring006  label="Cube176 (Mirror #11)"
  Base = (0,0,0)
  Normal = (0,0,1)
  Placement = pos=(720,0,0) rot=(0,0,1;0rad)
  Source = -> Box166
FEATURE [Part::Box] Box167  label="Cube175"
  AttacherType = Attacher::AttachEngine3D
  Height = 10
  Length = 10
  Placement = pos=(344,-6,-73) rot=(0,1,0;0.785398rad)
  Width = 12
FEATURE [Part::MultiFuse] Fusion202
  Refine = true
  Shapes = -> [Part__Mirroring006,Box167]
FEATURE [Part::Cut] Cut176
  Base = -> Fusion200
  Refine = true
  Tool = -> Fusion202
FEATURE [Part::Cylinder] Cylinder237  label="Cylinder478"
  Angle = 360
  AttacherType = Attacher::AttachEngine3D
  Height = 12
  Placement = pos=(360,-6,-69) rot=(-1,0,0;1.5708rad)
  Radius = 1.65
FEATURE [Part::Cut] Cut175
  Base = -> Cut176
  Placement = pos=(-40,2,0) rot=(0,0,1;0rad)
  Refine = true
  Tool = -> Cylinder237
FEATURE [Part::Box] Box168  label="Cube192"
  AttacherType = Attacher::AttachEngine3D
  Height = 4.5
  Length = 13
  Placement = pos=(314,-4,-6) rot=(0,0,1;0rad)
  Width = 12
FEATURE [Part::Cut] Cut174
  Base = -> Cut175
  Refine = true
  Tool = -> Box168
FEATURE [Part::Chamfer] Chamfer010
  Base = -> Cut174
  Edges = 1 edges r=1.2: [Edge192]
FEATURE [Part::Chamfer] Chamfer009
  Base = -> Chamfer010
  Edges = 1 edges r=1.49: [Edge99]
FEATURE [Part::Box] Box169  label="Cube194"
  AttacherType = Attacher::AttachEngine3D
  Height = 70
  Length = 12
  Placement = pos=(326,-4,-73) rot=(0,0,1;0rad)
  Width = 12
FEATURE [Part::Box] Box170  label="Cube193"
  AttacherType = Attacher::AttachEngine3D
  Height = 70
  Length = 12
  Placement = pos=(315,-4,-73) rot=(0,0,1;0rad)
  Width = 12
FEATURE [Part::Fillet] Fillet068
  Base = -> Box170
  Edges = 2 edges r=1: [Edge5,Edge7]
FEATURE [Part::Cut] Cut179
  Base = -> Box169
  Placement = pos=(-1,0,0) rot=(0,0,1;0rad)
  Refine = true
  Tool = -> Fillet068
FEATURE [Part::Cut] Cut173  label="supports-left-leg"
  Base = -> Chamfer009
  Placement = pos=(-80.5,-19,0.3) rot=(0,-1,0;0.05236rad)
  Refine = true
  Tool = -> Cut179
FEATURE [Part::Box] Box171  label="Cube258"
  AttacherType = Attacher::AttachEngine3D
  Height = 70
  Length = 12
  Placement = pos=(354,-6,-73) rot=(0,0,1;0rad)
  Width = 12
FEATURE [Part::Box] Box172  label="Cube259"
  AttacherType = Attacher::AttachEngine3D
  Height = 49
  Length = 5
  Placement = pos=(361.75,-6,-52) rot=(0,0,1;0rad)
  Width = 12
FEATURE [Part::Cut] Cut185
  Base = -> Box171
  Refine = true
  Tool = -> Box172
FEATURE [Part::Feature] union001
  Placement = pos=(362.75,0,-29) rot=(0,0,1;0rad)
  shape: bbox 4.337 x 12 x 50 mm, 106 faces (baked)
FEATURE [Part::MultiFuse] Fusion204
  Refine = true
  Shapes = -> [Cut185,union001]
FEATURE [Part::Box] Box173  label="Cube260"
  AttacherType = Attacher::AttachEngine3D
  Height = 10
  Length = 17
  Placement = pos=(353,-6,-4) rot=(0,0,1;0rad)
  Width = 12
FEATURE [Part::Cut] Cut184
  Base = -> Fusion204
  Refine = true
  Tool = -> Box173
FEATURE [Part::Box] Box174  label="Cube261"
  AttacherType = Attacher::AttachEngine3D
  Height = 4
  Length = 2.99
  Placement = pos=(361.5,-6,-52) rot=(0,0,1;0rad)
  Width = 12
FEATURE [Part::MultiFuse] Fusion203
  Refine = true
  Shapes = -> [Cut184,Box174]
FEATURE [Part::Box] Box175  label="Cube262"
  AttacherType = Attacher::AttachEngine3D
  Height = 10
  Length = 10
  Placement = pos=(344,-6,-73) rot=(0,1,0;0.785398rad)
  Width = 12
FEATURE [Part::Mirroring] Part__Mirroring007  label="Cube176 (Mirror #11)001"
  Base = (0,0,0)
  Normal = (0,0,1)
  Placement = pos=(720,0,0) rot=(0,0,1;0rad)
  Source = -> Box175
FEATURE [Part::Box] Box176  label="Cube263"
  AttacherType = Attacher::AttachEngine3D
  Height = 10
  Length = 10
  Placement = pos=(344,-6,-73) rot=(0,1,0;0.785398rad)
  Width = 12
FEATURE [Part::MultiFuse] Fusion205
  Refine = true
  Shapes = -> [Part__Mirroring007,Box176]
FEATURE [Part::Cut] Cut183
  Base = -> Fusion203
  Refine = true
  Tool = -> Fusion205
FEATURE [Part::Cylinder] Cylinder238  label="Cylinder522"
  Angle = 360
  AttacherType = Attacher::AttachEngine3D
  Height = 12
  Placement = pos=(360,-6,-69) rot=(-1,0,0;1.5708rad)
  Radius = 1.65
FEATURE [Part::Cut] Cut182
  Base = -> Cut183
  Placement = pos=(-40,2,0) rot=(0,0,1;0rad)
  Refine = true
  Tool = -> Cylinder238
FEATURE [Part::Box] Box177  label="Cube264"
  AttacherType = Attacher::AttachEngine3D
  Height = 4.5
  Length = 13
  Placement = pos=(314,-4,-6) rot=(0,0,1;0rad)
  Width = 12
FEATURE [Part::Cut] Cut181
  Base = -> Cut182
  Refine = true
  Tool = -> Box177
FEATURE [Part::Chamfer] Chamfer012
  Base = -> Cut181
  Edges = 1 edges r=1.2: [Edge192]
FEATURE [Part::Chamfer] Chamfer011
  Base = -> Chamfer012
  Edges = 1 edges r=1.49: [Edge99]
FEATURE [Part::Box] Box178  label="Cube265"
  AttacherType = Attacher::AttachEngine3D
  Height = 70
  Length = 12
  Placement = pos=(326,-4,-73) rot=(0,0,1;0rad)
  Width = 12
FEATURE [Part::Box] Box179  label="Cube266"
  AttacherType = Attacher::AttachEngine3D
  Height = 70
  Length = 12
  Placement = pos=(315,-4,-73) rot=(0,0,1;0rad)
  Width = 12
FEATURE [Part::Fillet] Fillet069
  Base = -> Box179
  Edges = 2 edges r=1: [Edge5,Edge7]
FEATURE [Part::Cut] Cut186
  Base = -> Box178
  Placement = pos=(-1,0,0) rot=(0,0,1;0rad)
  Refine = true
  Tool = -> Fillet069
FEATURE [Part::Cut] Cut180  label="supports-right-leg"
  Base = -> Chamfer011
  Placement = pos=(-79.5,77,6) rot=(0,-1,0;0.034907rad)
  Refine = true
  Tool = -> Cut186
FEATURE [Part::Cut] Cut187
  Base = -> Cut124
  Placement = pos=(-120,-9,10) rot=(0,0,1;0rad)
  Refine = true
  Tool = -> Fusion167
FEATURE [Part::Cut] Cut188
  Base = -> Cut134
  Placement = pos=(-120,67,10) rot=(0,0,1;0rad)
  Refine = true
  Tool = -> Fusion175
FEATURE [Part::Chamfer] Chamfer013
  Base = -> Cut188
  Edges = 2 edges r=1.1: [Edge29,Edge35]
  Placement = pos=(0,0,-13) rot=(0,-1,0;0.05236rad)
FEATURE [Part::Chamfer] Chamfer014
  Base = -> Cut187
  Edges = 2 edges r=1.1: [Edge29,Edge35]
  Placement = pos=(0,0,-13) rot=(0,-1,0;0.05236rad)
FEATURE [Part::Box] Box180  label="Cube267"
  AttacherType = Attacher::AttachEngine3D
  Height = 18
  Length = 20
  Placement = pos=(231,0,-7) rot=(0,0,1;0rad)
  Width = 10
FEATURE [Part::Box] Box181  label="Cube268"
  AttacherType = Attacher::AttachEngine3D
  Height = 18
  Length = 20
  Placement = pos=(231,52,-7) rot=(0,0,1;0rad)
  Width = 10
FEATURE [Part::Cut] Cut189
  Base = -> Chamfer013
  Placement = pos=(0,0,7) rot=(0,0,1;0rad)
  Refine = true
  Tool = -> Box181
FEATURE [Part::Cut] Cut190
  Base = -> Chamfer014
  Placement = pos=(0,0,7) rot=(0,0,1;0rad)
  Refine = true
  Tool = -> Box180
FEATURE [Part::Box] Box182  label="Cube269"
  AttacherType = Attacher::AttachEngine3D
  Height = 11
  Length = 18
  Placement = pos=(232.21,0,-11) rot=(0,-1,0;0.05236rad)
  Width = 10
FEATURE [Part::Box] Box185  label="Cube272"
  AttacherType = Attacher::AttachEngine3D
  Height = 11
  Length = 50
  Placement = pos=(231,0,0) rot=(0,0,1;0rad)
  Width = 10
FEATURE [Part::Cut] Cut191
  Base = -> Box182
  Refine = true
  Tool = -> Box185
FEATURE [Part::Chamfer] Chamfer015
  Base = -> Cut191
  Edges = 1 edges r=9: [Edge13]
FEATURE [Part::Cylinder] Cylinder239  label="Cylinder523"
  Angle = 360
  AttacherType = Attacher::AttachEngine3D
  Height = 10
  Placement = pos=(236,6,-9) rot=(0,0,1;0rad)
  Radius = 1.6
FEATURE [Part::Cylinder] Cylinder240  label="Cylinder524"
  Angle = 360
  AttacherType = Attacher::AttachEngine3D
  Height = 10
  Placement = pos=(246,6,-9) rot=(0,0,1;0rad)
  Radius = 1.6
FEATURE [Part::Cylinder] Cylinder241  label="Cylinder525"
  Angle = 360
  AttacherType = Attacher::AttachEngine3D
  Height = 10
  Placement = pos=(236,6,-12) rot=(0,0,1;0rad)
  Radius = 3.1
FEATURE [Part::Cylinder] Cylinder242  label="Cylinder526"
  Angle = 360
  AttacherType = Attacher::AttachEngine3D
  Height = 10
  Placement = pos=(246,6,-12) rot=(0,0,1;0rad)
  Radius = 3.1
FEATURE [Part::MultiFuse] Fusion206
  Placement = pos=(0,0,-1) rot=(0,0,1;0rad)
  Refine = true
  Shapes = -> [Cylinder239,Cylinder240,Cylinder242,Cylinder241]
FEATURE [Part::Cut] Cut192
  Base = -> Chamfer015
  Refine = true
  Tool = -> Fusion206
FEATURE [Part::Box] Box186  label="Cube273"
  AttacherType = Attacher::AttachEngine3D
  Height = 7
  Length = 7.5
  Placement = pos=(249,-3,3) rot=(0,0,1;0rad)
  Width = 3
FEATURE [Part::Cylinder] Cylinder243  label="Cylinder527"
  Angle = 360
  AttacherType = Attacher::AttachEngine3D
  Height = 10
  Placement = pos=(253,7,6.5) rot=(1,0,0;1.5708rad)
  Radius = 1.6
FEATURE [Part::Cut] Cut193
  Base = -> Box186
  Refine = true
  Tool = -> Cylinder243
FEATURE [Part::Fillet] Fillet070
  Base = -> Cut193
  Edges = 2 edges r=3: [Edge10,Edge14]
  Placement = pos=(-0.5,0,0.5) rot=(0,0,1;0rad)
FEATURE [Part::Cylinder] Cylinder244  label="Cylinder528"
  Angle = 360
  AttacherType = Attacher::AttachEngine3D
  Height = 10
  Placement = pos=(246,6,-9) rot=(0,0,1;0rad)
  Radius = 1.6
FEATURE [Part::Box] Box187  label="Cube274"
  AttacherType = Attacher::AttachEngine3D
  Height = 11
  Length = 18
  Placement = pos=(232.21,0,-11) rot=(0,-1,0;0.05236rad)
  Width = 10
FEATURE [Part::Box] Box188  label="Cube275"
  AttacherType = Attacher::AttachEngine3D
  Height = 11
  Length = 50
  Placement = pos=(231,0,0) rot=(0,0,1;0rad)
  Width = 10
FEATURE [Part::Cut] Cut194
  Base = -> Box187
  Refine = true
  Tool = -> Box188
FEATURE [Part::Chamfer] Chamfer016
  Base = -> Cut194
  Edges = 1 edges r=9: [Edge13]
FEATURE [Part::Cylinder] Cylinder245  label="Cylinder529"
  Angle = 360
  AttacherType = Attacher::AttachEngine3D
  Height = 10
  Placement = pos=(246,6,-12) rot=(0,0,1;0rad)
  Radius = 3.1
FEATURE [Part::Box] Box189  label="Cube276"
  AttacherType = Attacher::AttachEngine3D
  Height = 7
  Length = 7.5
  Placement = pos=(249,-3,3) rot=(0,0,1;0rad)
  Width = 3
FEATURE [Part::Cylinder] Cylinder246  label="Cylinder530"
  Angle = 360
  AttacherType = Attacher::AttachEngine3D
  Height = 10
  Placement = pos=(253,7,6.5) rot=(1,0,0;1.5708rad)
  Radius = 1.6
FEATURE [Part::Cut] Cut196
  Base = -> Box189
  Refine = true
  Tool = -> Cylinder246
FEATURE [Part::Fillet] Fillet071
  Base = -> Cut196
  Edges = 2 edges r=3: [Edge10,Edge14]
  Placement = pos=(-0.5,0,0.5) rot=(0,0,1;0rad)
FEATURE [Part::Cylinder] Cylinder247  label="Cylinder531"
  Angle = 360
  AttacherType = Attacher::AttachEngine3D
  Height = 10
  Placement = pos=(236,6,-12) rot=(0,0,1;0rad)
  Radius = 3.1
FEATURE [Part::Cylinder] Cylinder248  label="Cylinder532"
  Angle = 360
  AttacherType = Attacher::AttachEngine3D
  Height = 10
  Placement = pos=(236,6,-9) rot=(0,0,1;0rad)
  Radius = 1.6
FEATURE [Part::MultiFuse] Fusion209
  Placement = pos=(0,0,-1) rot=(0,0,1;0rad)
  Refine = true
  Shapes = -> [Cylinder248,Cylinder244,Cylinder245,Cylinder247]
FEATURE [Part::Cut] Cut195
  Base = -> Chamfer016
  Placement = pos=(0.371,0,0) rot=(0,0,1;0rad)
  Refine = true
  Tool = -> Fusion209
FEATURE [Part::Box] Box190  label="Cube277"
  AttacherType = Attacher::AttachEngine3D
  Height = 12.5
  Length = 38
  Placement = pos=(223,-16,15.7) rot=(0,-1,0;0.05236rad)
  Width = 20
FEATURE [Part::Box] Box191  label="Cube278"
  AttacherType = Attacher::AttachEngine3D
  Height = 12.5
  Length = 38
  Placement = pos=(223,58,15.7) rot=(0,-1,0;0.05236rad)
  Width = 20
FEATURE [Part::MultiFuse] Fusion213
  Refine = true
  Shapes = -> [Cut195,Cut190,Fillet071]
FEATURE [Part::Cut] Cut197  label="supports-left-frame"
  Base = -> Fusion213
  Placement = pos=(0,-10,0) rot=(0,0,1;0rad)
  Refine = true
  Tool = -> Box190
FEATURE [Part::Mirroring] Part__Mirroring008  label="Fillet070 (Mirror #6)"
  Base = (0,0,0)
  Normal = (0,0,1)
  Placement = pos=(0,62,0) rot=(0,0,1;0rad)
  Source = -> Fillet070
FEATURE [Part::Mirroring] Part__Mirroring009  label="Cut192 (Mirror #7)"
  Base = (0,0,0)
  Normal = (0,0,1)
  Placement = pos=(0.371,62,0) rot=(0,0,1;0rad)
  Source = -> Cut192
FEATURE [Part::MultiFuse] Fusion214
  Refine = true
  Shapes = -> [Cut189,Part__Mirroring008,Part__Mirroring009]
FEATURE [Part::Cut] Cut198  label="supports-right-frame"
  Base = -> Fusion214
  Placement = pos=(0,10,0) rot=(0,0,1;0rad)
  Refine = true
  Tool = -> Box191
FEATURE [Part::Box] Box192
  AttacherType = Attacher::AttachEngine3D
  Height = 20
  Length = 600
  Placement = pos=(0,-10,0) rot=(0,0,1;0rad)
  Width = 10
FEATURE [Part::Box] Box193
  AttacherType = Attacher::AttachEngine3D
  Height = 20
  Length = 600
  Placement = pos=(0,62,0) rot=(0,0,1;0rad)
  Width = 10
FEATURE [Part::MultiFuse] Fusion216
  Refine = true
  Shapes = -> [Box193,Box192]
FEATURE [Part::Box] Box194
  AttacherType = Attacher::AttachEngine3D
  Height = 10
  Length = 150
  Placement = pos=(0,-10,0) rot=(0,0,1;0rad)
  Width = 82
FEATURE [Part::Box] Box195
  AttacherType = Attacher::AttachEngine3D
  Height = 20
  Length = 20
  Placement = pos=(137,-10,-10) rot=(0,0,1;0rad)
  Width = 82
FEATURE [Part::Box] Box196
  AttacherType = Attacher::AttachEngine3D
  Height = 18
  Length = 600
  Placement = pos=(0,1,1) rot=(0,0,1;0rad)
  Width = 10
FEATURE [Part::Box] Box197
  AttacherType = Attacher::AttachEngine3D
  Height = 18
  Length = 600
  Placement = pos=(0,51,1) rot=(0,0,1;0rad)
  Width = 10
FEATURE [Part::Fillet] Fillet073
  Base = -> Box197
  Edges = 2 edges r=2: [Edge11,Edge12]
  Placement = pos=(0,10,0) rot=(0,0,1;0rad)
FEATURE [Part::Fillet] Fillet074
  Base = -> Box196
  Edges = 2 edges r=2: [Edge9,Edge10]
  Placement = pos=(0,-10,0) rot=(0,0,1;0rad)
FEATURE [Part::Fillet] Fillet075
  Base = -> Fusion216
  Edges = 4 edges r=3: [Edge11,Edge12,Edge21,Edge22]
FEATURE [Part::MultiFuse] Fusion218
  Refine = true
  Shapes = -> [Fillet073,Fillet074]
FEATURE [Part::Cut] Cut199
  Base = -> Fillet075
  Refine = true
  Tool = -> Fusion218
FEATURE [Part::Chamfer] Chamfer017
  Base = -> Box195
  Edges = 1 edges r=19: [Edge6]
  Placement = pos=(12,0,0) rot=(0,0,1;0rad)
FEATURE [Part::MultiFuse] Fusion219
  Placement = pos=(70,0,0) rot=(0,0,1;0rad)
  Refine = true
  Shapes = -> [Chamfer017,Box194]
FEATURE [Part::Box] Box211  label="Cube292"
  AttacherType = Attacher::AttachEngine3D
  Height = 20
  Length = 70
  Placement = pos=(0,-10,0) rot=(0,0,1;0rad)
  Width = 82
FEATURE [Part::MultiFuse] Fusion245
  Refine = true
  Shapes = -> [Box211,Fusion219]
FEATURE [Part::Cut] Cut221  label="frame-wide-METAL"
  Base = -> Cut199
  Refine = true
  Tool = -> Fusion245
FEATURE [Part::Box] Box212
  AttacherType = Attacher::AttachEngine3D
  Height = 10
  Length = 60
  Placement = pos=(0,-9,9) rot=(0,0,1;0rad)
  Width = 80
FEATURE [Part::Cylinder] Cylinder271
  Angle = 360
  AttacherType = Attacher::AttachEngine3D
  Height = 19
  Placement = pos=(30,31,6) rot=(0,0,1;0rad)
  Radius = 5
FEATURE [Part::Cylinder] Cylinder272
  Angle = 360
  AttacherType = Attacher::AttachEngine3D
  Height = 41
  Placement = pos=(20,31,10) rot=(0,1,0;1.5708rad)
  Radius = 1.6
FEATURE [Part::Cylinder] Cylinder273
  Angle = 360
  AttacherType = Attacher::AttachEngine3D
  Height = 51
  Placement = pos=(10,31,10) rot=(0,1,0;1.5708rad)
  Radius = 1.4
FEATURE [Part::Cylinder] Cylinder274
  Angle = 360
  AttacherType = Attacher::AttachEngine3D
  Height = 20
  Placement = pos=(41,31,10) rot=(0,1,0;1.5708rad)
  Radius = 2.6
FEATURE [Part::Cylinder] Cylinder277
  Angle = 360
  AttacherType = Attacher::AttachEngine3D
  Height = 15
  Placement = pos=(28,15,14) rot=(1,0,0;1.5708rad)
  Radius = 1.25
FEATURE [Part::Cylinder] Cylinder278
  Angle = 360
  AttacherType = Attacher::AttachEngine3D
  Height = 15
  Placement = pos=(6,15,14) rot=(1,0,0;1.5708rad)
  Radius = 1.25
FEATURE [Part::Cylinder] Cylinder279
  Angle = 360
  AttacherType = Attacher::AttachEngine3D
  Height = 15
  Placement = pos=(51,15,14) rot=(1,0,0;1.5708rad)
  Radius = 1.25
FEATURE [Part::MultiFuse] Fusion246
  Placement = pos=(0,56,0) rot=(0,0,1;0rad)
  Refine = true
  Shapes = -> [Cylinder279,Cylinder278,Cylinder277]
FEATURE [Part::Box] Box213  label="Cube293"
  AttacherType = Attacher::AttachEngine3D
  Height = 11
  Length = 25
  Placement = pos=(-24,-10,9) rot=(0,0,1;0rad)
  Width = 82
FEATURE [Part::Box] Box214  label="Cube294"
  AttacherType = Attacher::AttachEngine3D
  Height = 1.5
  Length = 25
  Placement = pos=(-24,0,19) rot=(0,0,1;0rad)
  Width = 62
FEATURE [Part::Box] Box215  label="Cube295"
  AttacherType = Attacher::AttachEngine3D
  Height = 10
  Length = 30
  Placement = pos=(-29,-10,7) rot=(0,1,0;0.296706rad)
  Width = 82
FEATURE [Part::MultiFuse] Fusion249
  Placement = pos=(-1,0,4) rot=(0,0,1;0rad)
  Refine = true
  Shapes = -> [Cylinder273,Cylinder272,Cylinder274]
FEATURE [Part::Fillet] Fillet084
  Base = -> Box212
  Edges = 2 edges r=3: [Edge10,Edge12]
FEATURE [Part::Cut] Cut222
  Base = -> Box213
  Refine = true
  Tool = -> Box214
FEATURE [Part::Fillet] Fillet085
  Base = -> Cut222
  Edges = 2 edges r=3: [Edge11,Edge18]
FEATURE [Part::Cylinder] Cylinder280
  Angle = 360
  AttacherType = Attacher::AttachEngine3D
  Height = 4
  Placement = pos=(50,24,15) rot=(0,0,1;0rad)
  Radius = 1.2
FEATURE [Part::Cylinder] Cylinder281
  Angle = 360
  AttacherType = Attacher::AttachEngine3D
  Height = 4
  Placement = pos=(50,38,15) rot=(0,0,1;0rad)
  Radius = 1.2
FEATURE [Part::Cylinder] Cylinder282
  Angle = 360
  AttacherType = Attacher::AttachEngine3D
  Height = 8
  Placement = pos=(64,24,11) rot=(0,0,1;0rad)
  Radius = 1.2
FEATURE [Part::Cylinder] Cylinder283
  Angle = 360
  AttacherType = Attacher::AttachEngine3D
  Height = 8
  Placement = pos=(64,38,11) rot=(0,0,1;0rad)
  Radius = 1.2
FEATURE [Part::Cylinder] Cylinder284
  Angle = 360
  AttacherType = Attacher::AttachEngine3D
  Height = 62
  Placement = pos=(67,5,19) rot=(0,1,0;1.5708rad)
  Radius = 3
FEATURE [Part::Cylinder] Cylinder285
  Angle = 360
  AttacherType = Attacher::AttachEngine3D
  Height = 62
  Placement = pos=(67,57,19) rot=(0,1,0;1.5708rad)
  Radius = 3
FEATURE [Part::MultiFuse] Fusion252
  Refine = true
  Shapes = -> [Cylinder285,Cylinder284]
FEATURE [Part::MultiFuse] Fusion253
  Refine = true
  Shapes = -> [Fillet084,Fillet085]
FEATURE [Part::Cut] Cut223
  Base = -> Fusion253
  Refine = true
  Tool = -> Box215
FEATURE [Part::Cylinder] Cylinder286
  Angle = 360
  AttacherType = Attacher::AttachEngine3D
  Height = 15
  Placement = pos=(6,15,14) rot=(1,0,0;1.5708rad)
  Radius = 1.25
FEATURE [Part::Cylinder] Cylinder287
  Angle = 360
  AttacherType = Attacher::AttachEngine3D
  Height = 15
  Placement = pos=(28,15,14) rot=(1,0,0;1.5708rad)
  Radius = 1.25
FEATURE [Part::Cylinder] Cylinder288
  Angle = 360
  AttacherType = Attacher::AttachEngine3D
  Height = 15
  Placement = pos=(51,15,14) rot=(1,0,0;1.5708rad)
  Radius = 1.25
FEATURE [Part::MultiFuse] Fusion254
  Placement = pos=(0,-9,0) rot=(0,0,1;0rad)
  Refine = true
  Shapes = -> [Cylinder288,Cylinder286,Cylinder287]
FEATURE [Part::MultiFuse] Fusion255
  Refine = true
  Shapes = -> [Cylinder271,Fusion246,Fusion249,Fusion254]
FEATURE [Part::Cut] Cut224
  Base = -> Cut223
  Placement = pos=(69,0,0) rot=(0,0,1;0rad)
  Refine = true
  Tool = -> Fusion255
FEATURE [Part::Fillet] Fillet086
  Base = -> Cut224
  Edges = 2 edges r=3: [Edge19,Edge56]
FEATURE [Part::Box] Box216  label="Cube296"
  AttacherType = Attacher::AttachEngine3D
  Height = 10
  Length = 10
  Placement = pos=(80,-9,9) rot=(0,0,1;0rad)
  Width = 80
FEATURE [Part::Cylinder] Cylinder289
  Angle = 360
  AttacherType = Attacher::AttachEngine3D
  Height = 4
  Placement = pos=(90,31,10) rot=(0,1,0;1.5708rad)
  Radius = 6.5
FEATURE [Part::Cylinder] Cylinder290
  Angle = 360
  AttacherType = Attacher::AttachEngine3D
  Height = 10
  Placement = pos=(80,31,11.5) rot=(0,1,0;1.5708rad)
  Radius = 8
FEATURE [Part::Cylinder] Cylinder291
  Angle = 360
  AttacherType = Attacher::AttachEngine3D
  Height = 4
  Placement = pos=(89.5,31,10) rot=(0,1,0;1.5708rad)
  Radius = 3.5
FEATURE [Part::MultiFuse] Fusion257
  Placement = pos=(-4,0,2) rot=(0,0,1;0rad)
  Refine = true
  Shapes = -> [Cylinder289,Cylinder291]
FEATURE [Part::MultiFuse] Fusion258
  Refine = true
  Shapes = -> [Box216,Cylinder290]
FEATURE [Part::Cylinder] Cylinder292
  Angle = 360
  AttacherType = Attacher::AttachEngine3D
  Height = 10
  Placement = pos=(82.5,1,14) rot=(1,0,0;1.5708rad)
  Radius = 1.25
FEATURE [Part::Cylinder] Cylinder293
  Angle = 360
  AttacherType = Attacher::AttachEngine3D
  Height = 10
  Placement = pos=(87.5,1,14) rot=(1,0,0;1.5708rad)
  Radius = 1.25
FEATURE [Part::Cylinder] Cylinder294
  Angle = 360
  AttacherType = Attacher::AttachEngine3D
  Height = 10
  Placement = pos=(82.5,71,14) rot=(1,0,0;1.5708rad)
  Radius = 1.25
FEATURE [Part::Cylinder] Cylinder295
  Angle = 360
  AttacherType = Attacher::AttachEngine3D
  Height = 10
  Placement = pos=(87.5,71,14) rot=(1,0,0;1.5708rad)
  Radius = 1.25
FEATURE [Part::MultiFuse] Fusion259
  Refine = true
  Shapes = -> [Cylinder292,Cylinder294]
FEATURE [Part::MultiFuse] Fusion260
  Refine = true
  Shapes = -> [Cylinder293,Cylinder295]
FEATURE [Part::MultiFuse] Fusion261
  Refine = true
  Shapes = -> [Fusion259,Fusion260]
FEATURE [Part::Cylinder] Cylinder296
  Angle = 360
  AttacherType = Attacher::AttachEngine3D
  Height = 16
  Placement = pos=(80,19,14) rot=(0,1,0;1.5708rad)
  Radius = 1.6
FEATURE [Part::Cylinder] Cylinder297
  Angle = 360
  AttacherType = Attacher::AttachEngine3D
  Height = 16
  Placement = pos=(80,43,14) rot=(0,1,0;1.5708rad)
  Radius = 1.6
FEATURE [Part::MultiFuse] Fusion262
  Placement = pos=(-6,0,0) rot=(0,0,1;0rad)
  Refine = true
  Shapes = -> [Cylinder296,Cylinder297]
FEATURE [Part::Box] Box217  label="Cube297"
  AttacherType = Attacher::AttachEngine3D
  Height = 22
  Length = 1
  Placement = pos=(89,15,2) rot=(0,0,1;0rad)
  Width = 32
FEATURE [Part::Box] Box218  label="Cube298"
  AttacherType = Attacher::AttachEngine3D
  Height = 5.5
  Length = 15
  Placement = pos=(75,23,3.5) rot=(0,0,1;0rad)
  Width = 16
FEATURE [Part::Box] Box219  label="Cube299"
  AttacherType = Attacher::AttachEngine3D
  Height = 10
  Length = 5
  Placement = pos=(75,-9,9) rot=(0,0,1;0rad)
  Width = 80
FEATURE [Part::MultiFuse] Fusion263
  Refine = true
  Shapes = -> [Box219,Box218,Fusion258]
FEATURE [Part::Cut] Cut226
  Base = -> Fusion263
  Refine = true
  Tool = -> Fusion257
FEATURE [Part::Cut] Cut227
  Base = -> Cut226
  Refine = true
  Tool = -> Fusion261
FEATURE [Part::Cut] Cut228
  Base = -> Cut227
  Refine = true
  Tool = -> Fusion262
FEATURE [Part::Cut] Cut229
  Base = -> Cut228
  Refine = true
  Tool = -> Box217
FEATURE [Part::Box] Box220  label="Cube300"
  AttacherType = Attacher::AttachEngine3D
  Height = 10
  Length = 5
  Placement = pos=(90,1,9) rot=(0,0,1;0rad)
  Width = 8
FEATURE [Part::Box] Box221  label="Cube301"
  AttacherType = Attacher::AttachEngine3D
  Height = 10
  Length = 5
  Placement = pos=(90,53,9) rot=(0,0,1;0rad)
  Width = 8
FEATURE [Part::Fillet] Fillet088
  Base = -> Box220
  Edges = 1 edges r=2: [Edge10]
  Placement = pos=(0,-10,0) rot=(0,0,1;0rad)
FEATURE [Part::Fillet] Fillet089
  Base = -> Box221
  Edges = 1 edges r=2: [Edge12]
  Placement = pos=(0,10,0) rot=(0,0,1;0rad)
FEATURE [Part::Box] Box222  label="Cube302"
  AttacherType = Attacher::AttachEngine3D
  Height = 10
  Length = 5
  Placement = pos=(75,1,-1) rot=(0,0,1;0rad)
  Width = 60
FEATURE [Part::Cut] Cut230
  Base = -> Cut229
  Refine = true
  Tool = -> Box222
FEATURE [Part::Fillet] Fillet090
  Base = -> Cut230
  Edges = 2 edges r=2: [Edge23,Edge25]
FEATURE [Part::MultiFuse] Fusion264
  Placement = pos=(54,0,0) rot=(0,0,1;0rad)
  Refine = true
  Shapes = -> [Fillet088,Fillet089,Fillet090]
FEATURE [Part::Box] Box226  label="Cube306"
  AttacherType = Attacher::AttachEngine3D
  Height = 50
  Length = 80
  Placement = pos=(0,-29,0) rot=(0,0,1;0rad)
  Width = 130
FEATURE [Part::Box] Box227  label="Cube307"
  AttacherType = Attacher::AttachEngine3D
  Height = 45
  Length = 75
  Placement = pos=(2.5,-24,2.5) rot=(0,0,1;0rad)
  Width = 120
FEATURE [Part::Cut] Cut232
  Base = -> Box226
  Refine = true
  Tool = -> Box227
FEATURE [Part::Box] Box229  label="Cube309"
  AttacherType = Attacher::AttachEngine3D
  Height = 30
  Length = 3.5
  Placement = pos=(337.5,6,-35.5) rot=(0,-1,0;0.05236rad)
  Width = 60
FEATURE [Part::Box] Box231  label="Cube311"
  AttacherType = Attacher::AttachEngine3D
  Height = 6.5
  Length = 6.5
  Placement = pos=(377.5,-31,-26) rot=(0,-1,0;0.05236rad)
  Width = 100
FEATURE [Part::Cylinder] Cylinder310
  Angle = 360
  AttacherType = Attacher::AttachEngine3D
  Height = 10
  Placement = pos=(0,0,11) rot=(0,1,0;1.5708rad)
  Radius = 1.75
FEATURE [Part::Cylinder] Cylinder311
  Angle = 360
  AttacherType = Attacher::AttachEngine3D
  Height = 10
  Placement = pos=(0,0,37) rot=(0,1,0;1.5708rad)
  Radius = 1.75
FEATURE [Part::Cylinder] Cylinder312
  Angle = 360
  AttacherType = Attacher::AttachEngine3D
  Height = 10
  Placement = pos=(0,62,11) rot=(0,1,0;1.5708rad)
  Radius = 1.75
FEATURE [Part::Cylinder] Cylinder313
  Angle = 360
  AttacherType = Attacher::AttachEngine3D
  Height = 10
  Placement = pos=(0,62,37) rot=(0,1,0;1.5708rad)
  Radius = 1.75
FEATURE [Part::MultiFuse] Fusion272
  Placement = pos=(300,-1,-55) rot=(0,0,1;0rad)
  Refine = true
  Shapes = -> [Cylinder310,Cylinder312,Cylinder313,Cylinder311]
FEATURE [Part::Cylinder] Cylinder314
  Angle = 360
  AttacherType = Attacher::AttachEngine3D
  Height = 15
  Placement = pos=(330.5,13.5,-15) rot=(0,0,1;0rad)
  Radius = 1.6
FEATURE [Part::Cylinder] Cylinder315
  Angle = 360
  AttacherType = Attacher::AttachEngine3D
  Height = 15
  Placement = pos=(361.5,13.5,-15) rot=(0,0,1;0rad)
  Radius = 1.6
FEATURE [Part::Cylinder] Cylinder316
  Angle = 360
  AttacherType = Attacher::AttachEngine3D
  Height = 15
  Placement = pos=(330.5,13.5,-15) rot=(0,0,1;0rad)
  Radius = 1.6
FEATURE [Part::Cylinder] Cylinder317
  Angle = 360
  AttacherType = Attacher::AttachEngine3D
  Height = 15
  Placement = pos=(361.5,13.5,-15) rot=(0,0,1;0rad)
  Radius = 1.6
FEATURE [Part::MultiFuse] Fusion273
  Placement = pos=(-8.5,-17.5,0) rot=(0,0,1;0rad)
  Refine = true
  Shapes = -> [Cylinder314,Cylinder315]
FEATURE [Part::MultiFuse] Fusion275
  Placement = pos=(-8.5,52.5,0) rot=(0,0,1;0rad)
  Refine = true
  Shapes = -> [Cylinder316,Cylinder317]
FEATURE [Part::Cylinder] Cylinder318
  Angle = 360
  AttacherType = Attacher::AttachEngine3D
  Height = 4
  Placement = pos=(322,-4,-12) rot=(0,0,1;0rad)
  Radius = 4
FEATURE [Part::Cylinder] Cylinder319
  Angle = 360
  AttacherType = Attacher::AttachEngine3D
  Height = 4
  Placement = pos=(353,-4,-11) rot=(0,0,1;0rad)
  Radius = 4
FEATURE [Part::Cylinder] Cylinder320
  Angle = 360
  AttacherType = Attacher::AttachEngine3D
  Height = 4
  Placement = pos=(353,66,-11) rot=(0,0,1;0rad)
  Radius = 4
FEATURE [Part::Cylinder] Cylinder321
  Angle = 360
  AttacherType = Attacher::AttachEngine3D
  Height = 4
  Placement = pos=(322,66,-12) rot=(0,0,1;0rad)
  Radius = 4
FEATURE [Part::MultiFuse] Fusion276
  Placement = pos=(0,0,6) rot=(0,0,1;0rad)
  Refine = true
  Shapes = -> [Cylinder321,Cylinder318]
FEATURE [Part::MultiFuse] Fusion277
  Placement = pos=(0,0,6.5) rot=(0,0,1;0rad)
  Refine = true
  Shapes = -> [Cylinder320,Cylinder319]
FEATURE [Part::MultiFuse] Fusion278
  Placement = pos=(0,0,-2.5) rot=(0,0,1;0rad)
  Refine = true
  Shapes = -> [Fusion277,Fusion276]
FEATURE [Part::Cylinder] Cylinder322
  Angle = 360
  AttacherType = Attacher::AttachEngine3D
  Height = 3
  Placement = pos=(3.5,96,3.5) rot=(1,0,0;1.5708rad)
  Radius = 4
FEATURE [Part::Cylinder] Cylinder323
  Angle = 360
  AttacherType = Attacher::AttachEngine3D
  Height = 3
  Placement = pos=(76.5,96,3.5) rot=(1,0,0;1.5708rad)
  Radius = 4
FEATURE [Part::Cylinder] Cylinder324
  Angle = 360
  AttacherType = Attacher::AttachEngine3D
  Height = 3
  Placement = pos=(3.5,96,46.5) rot=(1,0,0;1.5708rad)
  Radius = 4
FEATURE [Part::Cylinder] Cylinder325
  Angle = 360
  AttacherType = Attacher::AttachEngine3D
  Height = 3
  Placement = pos=(76.5,96,46.5) rot=(1,0,0;1.5708rad)
  Radius = 4
FEATURE [Part::MultiFuse] Fusion280
  Placement = pos=(306,-127,-55) rot=(0,-1,0;0.05236rad)
  Refine = true
  Shapes = -> [Cylinder322,Cylinder324,Cylinder325,Cylinder323]
FEATURE [Part::Cylinder] Cylinder326
  Angle = 360
  AttacherType = Attacher::AttachEngine3D
  Height = 10
  Placement = pos=(3.5,96,3.5) rot=(1,0,0;1.5708rad)
  Radius = 1.25
FEATURE [Part::Cylinder] Cylinder327
  Angle = 360
  AttacherType = Attacher::AttachEngine3D
  Height = 10
  Placement = pos=(3.5,96,46.5) rot=(1,0,0;1.5708rad)
  Radius = 1.25
FEATURE [Part::Cylinder] Cylinder328
  Angle = 360
  AttacherType = Attacher::AttachEngine3D
  Height = 10
  Placement = pos=(76.5,96,46.5) rot=(1,0,0;1.5708rad)
  Radius = 1.25
FEATURE [Part::Cylinder] Cylinder329
  Angle = 360
  AttacherType = Attacher::AttachEngine3D
  Height = 10
  Placement = pos=(76.5,96,3.5) rot=(1,0,0;1.5708rad)
  Radius = 1.25
FEATURE [Part::MultiFuse] Fusion282
  Placement = pos=(306,-120,-55) rot=(0,-1,0;0.05236rad)
  Refine = true
  Shapes = -> [Cylinder326,Cylinder327,Cylinder328,Cylinder329]
FEATURE [Part::Box] Box233  label="Cube313"
  AttacherType = Attacher::AttachEngine3D
  Height = 17
  Length = 34
  Placement = pos=(326,1,1.5) rot=(0,0,1;0rad)
  Width = 60
FEATURE [Part::Cylinder] Cylinder330
  Angle = 360
  AttacherType = Attacher::AttachEngine3D
  Height = 34
  Placement = pos=(326,31,4.5) rot=(0,1,0;1.5708rad)
  Radius = 20.5
FEATURE [Part::Cylinder] Cylinder331
  Angle = 360
  AttacherType = Attacher::AttachEngine3D
  Height = 10
  Placement = pos=(327,31,12) rot=(0,1,0;1.5708rad)
  Radius = 7
FEATURE [Part::Cylinder] Cylinder332
  Angle = 360
  AttacherType = Attacher::AttachEngine3D
  Height = 75
  Placement = pos=(336,31,5) rot=(0,1,0;1.5708rad)
  Radius = 18.7
FEATURE [Part::MultiFuse] Fusion283
  Placement = pos=(1,0,0) rot=(0,0,1;0rad)
  Refine = true
  Shapes = -> [Box233,Cylinder330]
FEATURE [Part::Cut] Cut240
  Base = -> Fusion283
  Refine = true
  Tool = -> Cylinder331
FEATURE [Part::Cut] Cut241
  Base = -> Cut240
  Refine = true
  Tool = -> Cylinder332
FEATURE [Part::Cylinder] Cylinder333
  Angle = 360
  AttacherType = Attacher::AttachEngine3D
  Height = 10
  Placement = pos=(15.5,0,0) rot=(0,0,1;0rad)
  Radius = 1.6
FEATURE [Part::Cylinder] Cylinder334
  Angle = 360
  AttacherType = Attacher::AttachEngine3D
  Height = 10
  Placement = pos=(-15.5,0,0) rot=(0,0,1;0rad)
  Radius = 1.6
FEATURE [Part::MultiFuse] Fusion284
  Placement = pos=(0,0,0) rot=(0,0,1;1.0472rad)
  Refine = true
  Shapes = -> [Cylinder334,Cylinder333]
FEATURE [Part::Cylinder] Cylinder335
  Angle = 360
  AttacherType = Attacher::AttachEngine3D
  Height = 10
  Placement = pos=(15.5,0,0) rot=(0,0,1;0rad)
  Radius = 1.6
FEATURE [Part::Cylinder] Cylinder336
  Angle = 360
  AttacherType = Attacher::AttachEngine3D
  Height = 10
  Placement = pos=(-15.5,0,0) rot=(0,0,1;0rad)
  Radius = 1.6
FEATURE [Part::MultiFuse] Fusion285
  Placement = pos=(0,0,0) rot=(0,0,1;2.0944rad)
  Refine = true
  Shapes = -> [Cylinder336,Cylinder335]
FEATURE [Part::Cylinder] Cylinder337
  Angle = 360
  AttacherType = Attacher::AttachEngine3D
  Height = 10
  Placement = pos=(-15.5,0,0) rot=(0,0,1;0rad)
  Radius = 1.6
FEATURE [Part::Cylinder] Cylinder338
  Angle = 360
  AttacherType = Attacher::AttachEngine3D
  Height = 10
  Placement = pos=(15.5,0,0) rot=(0,0,1;0rad)
  Radius = 1.6
FEATURE [Part::MultiFuse] Fusion286
  Refine = true
  Shapes = -> [Cylinder337,Cylinder338]
FEATURE [Part::MultiFuse] Fusion287
  Placement = pos=(0,0,0) rot=(0,0,1;0.523599rad)
  Refine = true
  Shapes = -> [Fusion284,Fusion285,Fusion286]
FEATURE [Part::Box] Box234  label="Cube314"
  AttacherType = Attacher::AttachEngine3D
  Height = 10
  Length = 10
  Width = 10
FEATURE [Part::Cut] Cut242  label="holes002"
  Base = -> Fusion287
  Placement = pos=(327,31,5) rot=(0,1,0;1.5708rad)
  Refine = true
  Tool = -> Box234
FEATURE [Part::Cut] Cut243
  Base = -> Cut241
  Refine = true
  Tool = -> Cut242
FEATURE [Part::Cylinder] Cylinder339
  Angle = 360
  AttacherType = Attacher::AttachEngine3D
  Height = 10
  Placement = pos=(87.5,61,14) rot=(1,0,0;1.5708rad)
  Radius = 1.25
FEATURE [Part::Cylinder] Cylinder340
  Angle = 360
  AttacherType = Attacher::AttachEngine3D
  Height = 10
  Placement = pos=(87.5,11,14) rot=(1,0,0;1.5708rad)
  Radius = 1.25
FEATURE [Part::MultiFuse] Fusion288
  Placement = pos=(242.5,0,0) rot=(0,0,1;0rad)
  Refine = true
  Shapes = -> [Cylinder340,Cylinder339]
FEATURE [Part::Cylinder] Cylinder341
  Angle = 360
  AttacherType = Attacher::AttachEngine3D
  Height = 10
  Placement = pos=(87.5,61,14) rot=(1,0,0;1.5708rad)
  Radius = 1.25
FEATURE [Part::Cylinder] Cylinder342
  Angle = 360
  AttacherType = Attacher::AttachEngine3D
  Height = 10
  Placement = pos=(87.5,11,14) rot=(1,0,0;1.5708rad)
  Radius = 1.25
FEATURE [Part::MultiFuse] Fusion289
  Placement = pos=(251.5,0,0) rot=(0,0,1;0rad)
  Refine = true
  Shapes = -> [Cylinder342,Cylinder341]
FEATURE [Part::Cylinder] Cylinder343
  Angle = 360
  AttacherType = Attacher::AttachEngine3D
  Height = 10
  Placement = pos=(87.5,61,14) rot=(1,0,0;1.5708rad)
  Radius = 1.25
FEATURE [Part::Cylinder] Cylinder344
  Angle = 360
  AttacherType = Attacher::AttachEngine3D
  Height = 10
  Placement = pos=(87.5,11,14) rot=(1,0,0;1.5708rad)
  Radius = 1.25
FEATURE [Part::MultiFuse] Fusion290
  Placement = pos=(261.5,0,0) rot=(0,0,1;0rad)
  Refine = true
  Shapes = -> [Cylinder344,Cylinder343]
FEATURE [Part::Cylinder] Cylinder345
  Angle = 360
  AttacherType = Attacher::AttachEngine3D
  Height = 10
  Placement = pos=(87.5,11,14) rot=(1,0,0;1.5708rad)
  Radius = 1.25
FEATURE [Part::Cylinder] Cylinder346
  Angle = 360
  AttacherType = Attacher::AttachEngine3D
  Height = 10
  Placement = pos=(87.5,61,14) rot=(1,0,0;1.5708rad)
  Radius = 1.25
FEATURE [Part::MultiFuse] Fusion291
  Placement = pos=(270.5,0,0) rot=(0,0,1;0rad)
  Refine = true
  Shapes = -> [Cylinder345,Cylinder346]
FEATURE [Part::MultiFuse] Fusion292
  Refine = true
  Shapes = -> [Fusion288,Fusion289,Fusion290,Fusion291]
FEATURE [Part::MultiFuse] Fusion294
  Placement = pos=(270.5,0,0) rot=(0,0,1;0rad)
  Refine = true
  Shapes = -> [Cylinder345,Cylinder346]
FEATURE [Part::MultiFuse] Fusion295
  Placement = pos=(251.5,0,0) rot=(0,0,1;0rad)
  Refine = true
  Shapes = -> [Cylinder342,Cylinder341]
FEATURE [Part::MultiFuse] Fusion296
  Placement = pos=(261.5,0,0) rot=(0,0,1;0rad)
  Refine = true
  Shapes = -> [Cylinder344,Cylinder343]
FEATURE [Part::MultiFuse] Fusion297
  Placement = pos=(242.5,0,0) rot=(0,0,1;0rad)
  Refine = true
  Shapes = -> [Cylinder340,Cylinder339]
FEATURE [Part::MultiFuse] Fusion293
  Placement = pos=(0,0,-8) rot=(0,0,1;0rad)
  Refine = true
  Shapes = -> [Fusion297,Fusion295,Fusion296,Fusion294]
FEATURE [Part::MultiFuse] Fusion298
  Refine = true
  Shapes = -> [Fusion292,Fusion293]
FEATURE [Part::Cut] Cut244  label="motor-support001"
  Base = -> Cut243
  Placement = pos=(86,0,0) rot=(0,0,1;0rad)
  Refine = true
  Tool = -> Fusion298
FEATURE [App::DocumentObjectGroup] Group002  label="Narrow Frame"
  Group = -> [Cut084,Part__Mirroring001,Fusion131,Cut111,Cut041,Fusion158,Cut114,Cut063,Cut036,Cut097,Cut110,Fillet055,Cut074,Cut244,Cut072,Cut121,Box070,Box069]
FEATURE [Part::Box] Box235  label="Cube315"
  AttacherType = Attacher::AttachEngine3D
  Height = 3
  Length = 24
  Placement = pos=(45,10,19) rot=(0,0,1;0rad)
  Width = 42
FEATURE [Part::Cylinder] Cylinder347
  Angle = 360
  AttacherType = Attacher::AttachEngine3D
  Height = 10
  Placement = pos=(50,38,12) rot=(0,0,1;0rad)
  Radius = 1.6
FEATURE [Part::Cylinder] Cylinder349
  Angle = 360
  AttacherType = Attacher::AttachEngine3D
  Height = 10
  Placement = pos=(50,24,12) rot=(0,0,1;0rad)
  Radius = 1.6
FEATURE [Part::Cylinder] Cylinder350
  Angle = 360
  AttacherType = Attacher::AttachEngine3D
  Height = 10
  Placement = pos=(64,38,12) rot=(0,0,1;0rad)
  Radius = 1.6
FEATURE [Part::Cylinder] Cylinder351
  Angle = 360
  AttacherType = Attacher::AttachEngine3D
  Height = 10
  Placement = pos=(64,24,12) rot=(0,0,1;0rad)
  Radius = 1.6
FEATURE [Part::MultiFuse] Fusion300
  Refine = true
  Shapes = -> [Cylinder347,Cylinder349,Cylinder351,Cylinder350]
FEATURE [Part::Box] Box236  label="Cube316"
  AttacherType = Attacher::AttachEngine3D
  Height = 8
  Length = 8
  Placement = pos=(45,44.5,19) rot=(0,0,1;0rad)
  Width = 5
FEATURE [Part::Box] Box237  label="Cube317"
  AttacherType = Attacher::AttachEngine3D
  Height = 15
  Length = 24
  Placement = pos=(45,42,19) rot=(0,0,1;0rad)
  Width = 10
FEATURE [Part::Cut] Cut245
  Base = -> Box237
  Refine = true
  Tool = -> Box236
FEATURE [Part::Box] Box238  label="Cube318"
  AttacherType = Attacher::AttachEngine3D
  Height = 11
  Length = 1.8
  Placement = pos=(53,43.5,19) rot=(0,0,1;0rad)
  Width = 7
FEATURE [Part::Cut] Cut246
  Base = -> Cut245
  Refine = true
  Tool = -> Box238
FEATURE [Part::Box] Box239  label="Cube319"
  AttacherType = Attacher::AttachEngine3D
  Height = 8
  Length = 4
  Placement = pos=(54,44.5,19) rot=(0,0,1;0rad)
  Width = 5
FEATURE [Part::Cut] Cut247
  Base = -> Cut246
  Refine = true
  Tool = -> Box239
FEATURE [Part::Cylinder] Cylinder352
  Angle = 360
  AttacherType = Attacher::AttachEngine3D
  Height = 10
  Placement = pos=(57,52,30) rot=(1,0,0;1.5708rad)
  Radius = 1.6
FEATURE [Part::Box] Box240  label="Cube320"
  AttacherType = Attacher::AttachEngine3D
  Height = 5
  Length = 19
  Placement = pos=(54,44.5,19) rot=(0,0,1;0rad)
  Width = 5
FEATURE [Part::Cut] Cut248
  Base = -> Cut247
  Refine = true
  Tool = -> Box240
FEATURE [Part::Cut] Cut249
  Base = -> Cut248
  Refine = true
  Tool = -> Cylinder352
FEATURE [Part::Fillet] Fillet094
  Base = -> Cut249
  Edges = 2 edges r=6: [Edge1,Edge10]
  Placement = pos=(0,-42,0) rot=(0,0,1;0rad)
FEATURE [Part::Box] Box241  label="Cube321"
  AttacherType = Attacher::AttachEngine3D
  Height = 5
  Length = 19
  Placement = pos=(54,44.5,19) rot=(0,0,1;0rad)
  Width = 5
FEATURE [Part::Box] Box242  label="Cube322"
  AttacherType = Attacher::AttachEngine3D
  Height = 8
  Length = 4
  Placement = pos=(54,44.5,19) rot=(0,0,1;0rad)
  Width = 5
FEATURE [Part::Cylinder] Cylinder353
  Angle = 360
  AttacherType = Attacher::AttachEngine3D
  Height = 10
  Placement = pos=(57,52,30) rot=(1,0,0;1.5708rad)
  Radius = 1.6
FEATURE [Part::Box] Box243  label="Cube323"
  AttacherType = Attacher::AttachEngine3D
  Height = 11
  Length = 1.8
  Placement = pos=(53,43.5,19) rot=(0,0,1;0rad)
  Width = 7
FEATURE [Part::Box] Box244  label="Cube324"
  AttacherType = Attacher::AttachEngine3D
  Height = 8
  Length = 8
  Placement = pos=(45,44.5,19) rot=(0,0,1;0rad)
  Width = 5
FEATURE [Part::Box] Box245  label="Cube325"
  AttacherType = Attacher::AttachEngine3D
  Height = 15
  Length = 24
  Placement = pos=(45,42,19) rot=(0,0,1;0rad)
  Width = 10
FEATURE [Part::Cut] Cut250
  Base = -> Box245
  Refine = true
  Tool = -> Box244
FEATURE [Part::Cut] Cut254
  Base = -> Cut250
  Refine = true
  Tool = -> Box243
FEATURE [Part::Cut] Cut253
  Base = -> Cut254
  Refine = true
  Tool = -> Box242
FEATURE [Part::Cut] Cut251
  Base = -> Cut253
  Refine = true
  Tool = -> Box241
FEATURE [Part::Cut] Cut252
  Base = -> Cut251
  Refine = true
  Tool = -> Cylinder353
FEATURE [Part::Fillet] Fillet095
  Base = -> Cut252
  Edges = 2 edges r=6: [Edge1,Edge10]
  Placement = pos=(0,10,0) rot=(0,0,1;0rad)
FEATURE [Part::Box] Box246  label="Cube326"
  AttacherType = Attacher::AttachEngine3D
  Height = 12
  Length = 10
  Placement = pos=(52,42,22) rot=(0,0,1;0rad)
  Width = 10
FEATURE [Part::Cylinder] Cylinder354
  Angle = 360
  AttacherType = Attacher::AttachEngine3D
  Height = 10
  Placement = pos=(57,52,30) rot=(1,0,0;1.5708rad)
  Radius = 1.6
FEATURE [Part::Cut] Cut255
  Base = -> Box246
  Refine = true
  Tool = -> Cylinder354
FEATURE [Part::Box] Box247  label="Cube327"
  AttacherType = Attacher::AttachEngine3D
  Height = 12
  Length = 10
  Placement = pos=(52,42,22) rot=(0,0,1;0rad)
  Width = 10
FEATURE [Part::Cylinder] Cylinder355
  Angle = 360
  AttacherType = Attacher::AttachEngine3D
  Height = 10
  Placement = pos=(57,52,30) rot=(1,0,0;1.5708rad)
  Radius = 1.6
FEATURE [Part::Cut] Cut256
  Base = -> Box247
  Placement = pos=(0,-32,0) rot=(0,0,1;0rad)
  Refine = true
  Tool = -> Cylinder355
FEATURE [Part::MultiFuse] Fusion301
  Refine = true
  Shapes = -> [Box235,Fillet095,Fillet094,Cut256,Cut255]
FEATURE [Part::Cut] Cut257
  Base = -> Fusion301
  Refine = true
  Tool = -> Fusion300
FEATURE [Part::Cylinder] Cylinder356
  Angle = 360
  AttacherType = Attacher::AttachEngine3D
  Height = 17
  Placement = pos=(129,5,19) rot=(0,1,0;1.5708rad)
  Radius = 3
FEATURE [Part::Cylinder] Cylinder357
  Angle = 360
  AttacherType = Attacher::AttachEngine3D
  Height = 17
  Placement = pos=(129,57,19) rot=(0,1,0;1.5708rad)
  Radius = 3
FEATURE [Part::MultiFuse] Fusion302
  Refine = true
  Shapes = -> [Cylinder356,Cylinder357]
FEATURE [Part::Box] Box248  label="Cube328"
  AttacherType = Attacher::AttachEngine3D
  Height = 12
  Length = 12
  Placement = pos=(324,-6,-55) rot=(0,0,1;0rad)
  Width = 16
FEATURE [Part::Box] Box249  label="Cube329"
  AttacherType = Attacher::AttachEngine3D
  Height = 26
  Length = 2
  Placement = pos=(330,-6,-62) rot=(0,0,1;0rad)
  Width = 16
FEATURE [Part::Box] Box250  label="Cube330"
  AttacherType = Attacher::AttachEngine3D
  Height = 14
  Length = 4
  Placement = pos=(332,-6,-56) rot=(0,0,1;0rad)
  Width = 16
FEATURE [Part::MultiFuse] Fusion306
  Refine = true
  Shapes = -> [Box248,Box249,Box250]
FEATURE [Part::Box] Box251  label="Cube331"
  AttacherType = Attacher::AttachEngine3D
  Height = 12
  Length = 10
  Placement = pos=(324,-4.25,-55) rot=(0,0,1;0rad)
  Width = 12.5
FEATURE [Part::Cut] Cut263
  Base = -> Fusion306
  Placement = pos=(0,-10,0) rot=(0,0,1;0rad)
  Refine = true
  Tool = -> Box251
FEATURE [Part::Box] Box252  label="Cube332"
  AttacherType = Attacher::AttachEngine3D
  Height = 12
  Length = 12
  Placement = pos=(324,-6,-55) rot=(0,0,1;0rad)
  Width = 16
FEATURE [Part::Box] Box253  label="Cube333"
  AttacherType = Attacher::AttachEngine3D
  Height = 26
  Length = 2
  Placement = pos=(330,-6,-62) rot=(0,0,1;0rad)
  Width = 16
FEATURE [Part::Box] Box254  label="Cube334"
  AttacherType = Attacher::AttachEngine3D
  Height = 14
  Length = 4
  Placement = pos=(332,-6,-56) rot=(0,0,1;0rad)
  Width = 16
FEATURE [Part::MultiFuse] Fusion307
  Refine = true
  Shapes = -> [Box252,Box253,Box254]
FEATURE [Part::Box] Box255  label="Cube335"
  AttacherType = Attacher::AttachEngine3D
  Height = 12
  Length = 10
  Placement = pos=(324,-4.25,-55) rot=(0,0,1;0rad)
  Width = 12.5
FEATURE [Part::Cut] Cut264
  Base = -> Fusion307
  Placement = pos=(0,86,0) rot=(0,0,1;0rad)
  Refine = true
  Tool = -> Box255
FEATURE [Part::Box] Box256  label="Cube336"
  AttacherType = Attacher::AttachEngine3D
  Height = 6
  Length = 8
  Placement = pos=(328,6.25,-52) rot=(0,0,1;0rad)
  Width = 2
FEATURE [Part::Box] Box257  label="Cube337"
  AttacherType = Attacher::AttachEngine3D
  Height = 6
  Length = 8
  Placement = pos=(328,-4.5,-52) rot=(0,0,1;0rad)
  Width = 2
FEATURE [Part::MultiFuse] Fusion308
  Refine = true
  Shapes = -> [Box256,Box257]
FEATURE [Part::Fillet] Fillet099
  Base = -> Fusion308
  Edges = 4 edges r=2.5: [Edge2,Edge4,Edge14,Edge16]
  Placement = pos=(-1.5,-10,0) rot=(0,0,1;0rad)
FEATURE [Part::Box] Box258  label="Cube338"
  AttacherType = Attacher::AttachEngine3D
  Height = 6
  Length = 8
  Placement = pos=(328,6.25,-52) rot=(0,0,1;0rad)
  Width = 2
FEATURE [Part::Box] Box259  label="Cube339"
  AttacherType = Attacher::AttachEngine3D
  Height = 6
  Length = 8
  Placement = pos=(328,-4.5,-52) rot=(0,0,1;0rad)
  Width = 2
FEATURE [Part::MultiFuse] Fusion309
  Refine = true
  Shapes = -> [Box258,Box259]
FEATURE [Part::Fillet] Fillet100
  Base = -> Fusion309
  Edges = 4 edges r=2.5: [Edge2,Edge4,Edge14,Edge16]
  Placement = pos=(-1.5,86.25,0) rot=(0,0,1;0rad)
FEATURE [Part::Cylinder] Cylinder358  label="Cylinder534"
  Angle = 360
  AttacherType = Attacher::AttachEngine3D
  Height = 112
  Placement = pos=(329.25,96,-49) rot=(1,0,0;1.5708rad)
  Radius = 1.6
FEATURE [Part::Cylinder] Cylinder359  label="Cylinder535"
  Angle = 360
  AttacherType = Attacher::AttachEngine3D
  Height = 10
  Placement = pos=(323,0,-59) rot=(0,1,0;1.5708rad)
  Radius = 1.6
FEATURE [Part::Cylinder] Cylinder360  label="Cylinder536"
  Angle = 360
  AttacherType = Attacher::AttachEngine3D
  Height = 10
  Placement = pos=(323,0,-39) rot=(0,1,0;1.5708rad)
  Radius = 1.6
FEATURE [Part::MultiFuse] Fusion311
  Placement = pos=(3,-8,0) rot=(0,0,1;0rad)
  Refine = true
  Shapes = -> [Cylinder359,Cylinder360]
FEATURE [Part::Cylinder] Cylinder361  label="Cylinder537"
  Angle = 360
  AttacherType = Attacher::AttachEngine3D
  Height = 10
  Placement = pos=(323,0,-59) rot=(0,1,0;1.5708rad)
  Radius = 1.6
FEATURE [Part::Cylinder] Cylinder362  label="Cylinder538"
  Angle = 360
  AttacherType = Attacher::AttachEngine3D
  Height = 10
  Placement = pos=(323,0,-39) rot=(0,1,0;1.5708rad)
  Radius = 1.6
FEATURE [Part::MultiFuse] Fusion312
  Placement = pos=(3,88,0) rot=(0,0,1;0rad)
  Refine = true
  Shapes = -> [Cylinder361,Cylinder362]
FEATURE [Part::Box] Box260  label="Cube340"
  AttacherType = Attacher::AttachEngine3D
  Height = 10
  Length = 10
  Placement = pos=(326,10,-54) rot=(0,0,1;0rad)
  Width = 70
FEATURE [Part::Cylinder] Cylinder363  label="Cylinder539"
  Angle = 360
  AttacherType = Attacher::AttachEngine3D
  Height = 102
  Placement = pos=(329.25,86,-49) rot=(1,0,0;1.5708rad)
  Radius = 2
FEATURE [Part::Cut] Cut265
  Base = -> Box260
  Refine = true
  Tool = -> Cylinder363
FEATURE [Part::Cylinder] Cylinder364  label="Cylinder540"
  Angle = 360
  AttacherType = Attacher::AttachEngine3D
  Height = 20
  Placement = pos=(333.25,10,-34.25) rot=(1,0,0;1.5708rad)
  Radius = 2.75
FEATURE [Part::Box] Box262  label="Cube342"
  AttacherType = Attacher::AttachEngine3D
  Height = 10
  Length = 6
  Placement = pos=(330,-6,-37) rot=(0,0,1;0rad)
  Width = 16
FEATURE [Part::Box] Box263  label="Cube343"
  AttacherType = Attacher::AttachEngine3D
  Height = 26
  Length = 20
  Placement = pos=(316,10,-62) rot=(0,0,1;0rad)
  Width = 10
FEATURE [Part::Cylinder] Cylinder365  label="Cylinder541"
  Angle = 360
  AttacherType = Attacher::AttachEngine3D
  Height = 6
  Placement = pos=(329.25,18,-49) rot=(1,0,0;1.5708rad)
  Radius = 12.5
FEATURE [Part::Cut] Cut269
  Base = -> Box263
  Refine = true
  Tool = -> Cylinder365
FEATURE [Part::Box] Box264  label="Cube344"
  AttacherType = Attacher::AttachEngine3D
  Height = 9
  Length = 10
  Placement = pos=(326,10,-36) rot=(0,0,1;0rad)
  Width = 10
FEATURE [Part::MultiFuse] Fusion314
  Refine = true
  Shapes = -> [Cut269,Box264]
FEATURE [Part::Box] Box265  label="Cube345"
  AttacherType = Attacher::AttachEngine3D
  Height = 11
  Length = 10
  Placement = pos=(328,12,-40) rot=(0,0,1;0rad)
  Width = 6
FEATURE [Part::Cut] Cut268
  Base = -> Fusion314
  Refine = true
  Tool = -> Box265
FEATURE [Part::MultiFuse] Fusion313
  Refine = true
  Shapes = -> [Cylinder364,Box262,Cut268]
FEATURE [Part::Cylinder] Cylinder366  label="Cylinder542"
  Angle = 360
  AttacherType = Attacher::AttachEngine3D
  Height = 4
  Placement = pos=(332,2,-39) rot=(0,1,0;1.5708rad)
  Radius = 3
FEATURE [Part::Cut] Cut267
  Base = -> Fusion313
  Refine = true
  Tool = -> Cylinder366
FEATURE [Part::Cylinder] Cylinder367  label="Cylinder543"
  Angle = 360
  AttacherType = Attacher::AttachEngine3D
  Height = 47
  Placement = pos=(333.25,20,-34.25) rot=(1,0,0;1.5708rad)
  Radius = 1.55
FEATURE [Part::Cut] Cut266
  Base = -> Cut267
  Placement = pos=(0,-10,0) rot=(0,0,1;0rad)
  Refine = true
  Tool = -> Cylinder367
FEATURE [Part::Cylinder] Cylinder368  label="Cylinder544"
  Angle = 360
  AttacherType = Attacher::AttachEngine3D
  Height = 5
  Placement = pos=(331,8,-54) rot=(0,1,0;1.5708rad)
  Radius = 0.8
FEATURE [Part::Cylinder] Cylinder369  label="Cylinder545"
  Angle = 360
  AttacherType = Attacher::AttachEngine3D
  Height = 5
  Placement = pos=(331,23,-46) rot=(0,1,0;1.5708rad)
  Radius = 0.8
FEATURE [Part::Cylinder] Cylinder370  label="Cylinder546"
  Angle = 360
  AttacherType = Attacher::AttachEngine3D
  Height = 5
  Placement = pos=(331,8,-29) rot=(0,1,0;1.5708rad)
  Radius = 0.8
FEATURE [Part::MultiFuse] Fusion315
  Placement = pos=(0,-10,0) rot=(0,0,1;0rad)
  Refine = true
  Shapes = -> [Cylinder368,Cylinder369,Cylinder370]
FEATURE [Part::MultiFuse] Fusion316
  Refine = true
  Shapes = -> [Fusion311,Fusion312]
FEATURE [Part::MultiFuse] Fusion317
  Refine = true
  Shapes = -> [Cut263,Fillet100,Cut264,Fillet099]
FEATURE [Part::Cut] Cut270
  Base = -> Fusion317
  Refine = true
  Tool = -> Cylinder358
FEATURE [Part::Cylinder] Cylinder371  label="Cylinder547"
  Angle = 360
  AttacherType = Attacher::AttachEngine3D
  Height = 102
  Placement = pos=(329.25,91,-49) rot=(1,0,0;1.5708rad)
  Radius = 2
FEATURE [Part::MultiFuse] Fusion318
  Refine = true
  Shapes = -> [Cut266,Cut265]
FEATURE [Part::Cut] Cut271
  Base = -> Fusion318
  Refine = true
  Tool = -> Cylinder371
FEATURE [Part::MultiFuse] Fusion319
  Refine = true
  Shapes = -> [Cut270,Cut271]
FEATURE [Part::Cut] Cut272
  Base = -> Fusion319
  Refine = true
  Tool = -> Fusion316
FEATURE [Part::Cut] Cut273
  Base = -> Cut272
  Placement = pos=(-80,-9,0) rot=(0,-1,0;0.05236rad)
  Refine = true
  Tool = -> Fusion315
FEATURE [Part::Chamfer] Chamfer025
  Base = -> Cut273
  Edges = 1 edges r=1: [Edge84]
FEATURE [Part::Fillet] Fillet101
  Base = -> Chamfer025
  Edges = 6 edges r=4: [Edge7,Edge57,Edge113,Edge118,Edge128,Edge131]
FEATURE [Part::Fillet] Fillet102  label="support-reductor-box-wide"
  Base = -> Fillet101
  Edges = 3 edges r=3: [Edge5,Edge121,Edge145]
FEATURE [App::DocumentObjectGroup] Group001  label="Supports"
  Group = -> [Cut153,Cut155,Cut157,Cut160,Cut163,Fusion197,Fusion198,Cut173,Cut180,Cut197,Cut198,Fillet102]
FEATURE [Part::Box] Box266  label="Cube346"
  AttacherType = Attacher::AttachEngine3D
  Height = 17
  Length = 34
  Placement = pos=(326,-9,1.5) rot=(0,0,1;0rad)
  Width = 80
FEATURE [Part::Cylinder] Cylinder372
  Angle = 360
  AttacherType = Attacher::AttachEngine3D
  Height = 34
  Placement = pos=(326,31,4.5) rot=(0,1,0;1.5708rad)
  Radius = 20.5
FEATURE [Part::Cylinder] Cylinder373
  Angle = 360
  AttacherType = Attacher::AttachEngine3D
  Height = 10
  Placement = pos=(327,31,12) rot=(0,1,0;1.5708rad)
  Radius = 7
FEATURE [Part::Cylinder] Cylinder374
  Angle = 360
  AttacherType = Attacher::AttachEngine3D
  Height = 75
  Placement = pos=(336,31,5) rot=(0,1,0;1.5708rad)
  Radius = 18.7
FEATURE [Part::Cylinder] Cylinder375
  Angle = 360
  AttacherType = Attacher::AttachEngine3D
  Height = 10
  Placement = pos=(15.5,0,0) rot=(0,0,1;0rad)
  Radius = 1.6
FEATURE [Part::Cylinder] Cylinder376
  Angle = 360
  AttacherType = Attacher::AttachEngine3D
  Height = 10
  Placement = pos=(-15.5,0,0) rot=(0,0,1;0rad)
  Radius = 1.6
FEATURE [Part::MultiFuse] Fusion321
  Placement = pos=(0,0,0) rot=(0,0,1;1.0472rad)
  Refine = true
  Shapes = -> [Cylinder376,Cylinder375]
FEATURE [Part::Cylinder] Cylinder377
  Angle = 360
  AttacherType = Attacher::AttachEngine3D
  Height = 10
  Placement = pos=(15.5,0,0) rot=(0,0,1;0rad)
  Radius = 1.6
FEATURE [Part::Cylinder] Cylinder378
  Angle = 360
  AttacherType = Attacher::AttachEngine3D
  Height = 10
  Placement = pos=(-15.5,0,0) rot=(0,0,1;0rad)
  Radius = 1.6
FEATURE [Part::MultiFuse] Fusion322
  Placement = pos=(0,0,0) rot=(0,0,1;2.0944rad)
  Refine = true
  Shapes = -> [Cylinder378,Cylinder377]
FEATURE [Part::Cylinder] Cylinder379
  Angle = 360
  AttacherType = Attacher::AttachEngine3D
  Height = 10
  Placement = pos=(-15.5,0,0) rot=(0,0,1;0rad)
  Radius = 1.6
FEATURE [Part::Cylinder] Cylinder380
  Angle = 360
  AttacherType = Attacher::AttachEngine3D
  Height = 10
  Placement = pos=(15.5,0,0) rot=(0,0,1;0rad)
  Radius = 1.6
FEATURE [Part::MultiFuse] Fusion323
  Refine = true
  Shapes = -> [Cylinder379,Cylinder380]
FEATURE [Part::MultiFuse] Fusion324
  Placement = pos=(0,0,0) rot=(0,0,1;0.523599rad)
  Refine = true
  Shapes = -> [Fusion321,Fusion322,Fusion323]
FEATURE [Part::Box] Box267  label="Cube347"
  AttacherType = Attacher::AttachEngine3D
  Height = 10
  Length = 10
  Width = 10
FEATURE [Part::Cut] Cut276  label="holes003"
  Base = -> Fusion324
  Placement = pos=(327,31,5) rot=(0,1,0;1.5708rad)
  Refine = true
  Tool = -> Box267
FEATURE [Part::Cylinder] Cylinder381
  Angle = 360
  AttacherType = Attacher::AttachEngine3D
  Height = 10
  Placement = pos=(87.5,71,14) rot=(1,0,0;1.5708rad)
  Radius = 1.25
FEATURE [Part::Cylinder] Cylinder382
  Angle = 360
  AttacherType = Attacher::AttachEngine3D
  Height = 10
  Placement = pos=(87.5,1,14) rot=(1,0,0;1.5708rad)
  Radius = 1.25
FEATURE [Part::MultiFuse] Fusion325
  Placement = pos=(242.5,0,0) rot=(0,0,1;0rad)
  Refine = true
  Shapes = -> [Cylinder382,Cylinder381]
FEATURE [Part::Cylinder] Cylinder383
  Angle = 360
  AttacherType = Attacher::AttachEngine3D
  Height = 10
  Placement = pos=(87.5,71,14) rot=(1,0,0;1.5708rad)
  Radius = 1.25
FEATURE [Part::Cylinder] Cylinder384
  Angle = 360
  AttacherType = Attacher::AttachEngine3D
  Height = 10
  Placement = pos=(87.5,1,14) rot=(1,0,0;1.5708rad)
  Radius = 1.25
FEATURE [Part::MultiFuse] Fusion326
  Placement = pos=(251.5,0,0) rot=(0,0,1;0rad)
  Refine = true
  Shapes = -> [Cylinder384,Cylinder383]
FEATURE [Part::Cylinder] Cylinder385
  Angle = 360
  AttacherType = Attacher::AttachEngine3D
  Height = 10
  Placement = pos=(87.5,71,14) rot=(1,0,0;1.5708rad)
  Radius = 1.25
FEATURE [Part::Cylinder] Cylinder386
  Angle = 360
  AttacherType = Attacher::AttachEngine3D
  Height = 10
  Placement = pos=(87.5,1,14) rot=(1,0,0;1.5708rad)
  Radius = 1.25
FEATURE [Part::MultiFuse] Fusion327
  Placement = pos=(261.5,0,0) rot=(0,0,1;0rad)
  Refine = true
  Shapes = -> [Cylinder386,Cylinder385]
FEATURE [Part::Cylinder] Cylinder387
  Angle = 360
  AttacherType = Attacher::AttachEngine3D
  Height = 10
  Placement = pos=(87.5,1,14) rot=(1,0,0;1.5708rad)
  Radius = 1.25
FEATURE [Part::Cylinder] Cylinder388
  Angle = 360
  AttacherType = Attacher::AttachEngine3D
  Height = 10
  Placement = pos=(87.5,71,14) rot=(1,0,0;1.5708rad)
  Radius = 1.25
FEATURE [Part::MultiFuse] Fusion328
  Placement = pos=(270.5,0,0) rot=(0,0,1;0rad)
  Refine = true
  Shapes = -> [Cylinder387,Cylinder388]
FEATURE [Part::MultiFuse] Fusion329
  Refine = true
  Shapes = -> [Fusion325,Fusion326,Fusion327,Fusion328]
FEATURE [Part::MultiFuse] Fusion331
  Placement = pos=(270.5,0,0) rot=(0,0,1;0rad)
  Refine = true
  Shapes = -> [Cylinder387,Cylinder388]
FEATURE [Part::MultiFuse] Fusion332
  Placement = pos=(251.5,0,0) rot=(0,0,1;0rad)
  Refine = true
  Shapes = -> [Cylinder384,Cylinder383]
FEATURE [Part::MultiFuse] Fusion333
  Placement = pos=(261.5,0,0) rot=(0,0,1;0rad)
  Refine = true
  Shapes = -> [Cylinder386,Cylinder385]
FEATURE [Part::MultiFuse] Fusion334
  Placement = pos=(242.5,0,0) rot=(0,0,1;0rad)
  Refine = true
  Shapes = -> [Cylinder382,Cylinder381]
FEATURE [Part::MultiFuse] Fusion330
  Placement = pos=(0,0,-8) rot=(0,0,1;0rad)
  Refine = true
  Shapes = -> [Fusion334,Fusion332,Fusion333,Fusion331]
FEATURE [Part::MultiFuse] Fusion335
  Refine = true
  Shapes = -> [Fusion329,Fusion330]
FEATURE [Part::MultiFuse] Fusion336
  Refine = true
  Shapes = -> [Box266,Cylinder372]
FEATURE [Part::Chamfer] Chamfer026
  Base = -> Fusion336
  Edges = 2 edges r=8: [Edge4,Edge13]
FEATURE [Part::Fillet] Fillet103
  Base = -> Chamfer026
  Edges = 4 edges r=2: [Edge3,Edge18,Edge31,Edge32]
  Placement = pos=(1,0,0) rot=(0,0,1;0rad)
FEATURE [Part::Cut] Cut277
  Base = -> Fillet103
  Refine = true
  Tool = -> Cylinder373
FEATURE [Part::Cut] Cut278
  Base = -> Cut277
  Refine = true
  Tool = -> Cylinder374
FEATURE [Part::Cut] Cut279
  Base = -> Cut278
  Refine = true
  Tool = -> Cut276
FEATURE [Part::Cut] Cut280  label="motor-support-wide"
  Base = -> Cut279
  Placement = pos=(86,0,0) rot=(0,0,1;0rad)
  Refine = true
  Tool = -> Fusion335
FEATURE [Part::Box] Box268  label="Cube348"
  AttacherType = Attacher::AttachEngine3D
  Height = 10
  Length = 58
  Placement = pos=(308.5,-10,-14.5) rot=(0,-1,0;0.05236rad)
  Width = 82
FEATURE [Part::Box] Box269  label="Cube349"
  AttacherType = Attacher::AttachEngine3D
  Height = 22
  Length = 50
  Placement = pos=(312.5,-10,-5) rot=(0,0,1;0rad)
  Width = 82
FEATURE [Part::Box] Box270  label="Cube350"
  AttacherType = Attacher::AttachEngine3D
  Height = 20
  Length = 50
  Placement = pos=(312.5,0,0) rot=(0,0,1;0rad)
  Width = 82
FEATURE [Part::Fillet] Fillet104
  Base = -> Box270
  Edges = 2 edges r=2: [Edge9,Edge11]
  Placement = pos=(0,-10,0) rot=(0,0,1;0rad)
FEATURE [Part::Box] Box271  label="Cube351"
  AttacherType = Attacher::AttachEngine3D
  Height = 20
  Length = 15
  Placement = pos=(312.5,10,-5) rot=(0,0,1;0rad)
  Width = 42
FEATURE [Part::Cylinder] Cylinder397
  Angle = 360
  AttacherType = Attacher::AttachEngine3D
  Height = 10
  Placement = pos=(320,-4,-6) rot=(0,0,1;0rad)
  Radius = 1.6
FEATURE [Part::Cylinder] Cylinder398
  Angle = 360
  AttacherType = Attacher::AttachEngine3D
  Height = 10
  Placement = pos=(320,66,-6) rot=(0,0,1;0rad)
  Radius = 1.6
FEATURE [Part::MultiFuse] Fusion344
  Placement = pos=(2,0,0) rot=(0,0,1;0rad)
  Refine = true
  Shapes = -> [Cylinder398,Cylinder397]
FEATURE [Part::Cylinder] Cylinder399
  Angle = 360
  AttacherType = Attacher::AttachEngine3D
  Height = 10
  Placement = pos=(320,-4,-6) rot=(0,0,1;0rad)
  Radius = 1.6
FEATURE [Part::Cylinder] Cylinder400
  Angle = 360
  AttacherType = Attacher::AttachEngine3D
  Height = 10
  Placement = pos=(320,66,-6) rot=(0,0,1;0rad)
  Radius = 1.6
FEATURE [Part::MultiFuse] Fusion345
  Placement = pos=(33,0,0) rot=(0,0,1;0rad)
  Refine = true
  Shapes = -> [Cylinder400,Cylinder399]
FEATURE [Part::MultiFuse] Fusion346
  Refine = true
  Shapes = -> [Fusion345,Fusion344]
FEATURE [Part::Cut] Cut281
  Base = -> Box269
  Refine = true
  Tool = -> Box268
FEATURE [Part::Cut] Cut282
  Base = -> Cut281
  Refine = true
  Tool = -> Fillet104
FEATURE [Part::Cut] Cut283
  Base = -> Cut282
  Refine = true
  Tool = -> Box271
FEATURE [Part::Cut] Cut284
  Base = -> Cut283
  Refine = true
  Tool = -> Fusion346
FEATURE [Part::Fillet] Fillet105  label="battery-box-holder-wide"
  Base = -> Cut284
  Edges = 4 edges r=5: [Edge4,Edge21,Edge34,Edge37]
FEATURE [Part::MultiFuse] Fusion347
  Refine = true
  Shapes = -> [Fusion275,Fusion273]
FEATURE [Part::RegularPolygon] RegularPolygon005  label="Regular polygon005"
  AttacherType = Attacher::AttachEngine3D
  Circumradius = 3.3
  Placement = pos=(13,0,0) rot=(0,1,0;1.5708rad)
  Polygon = 6
FEATURE [Part::Extrusion] Extrude020
  Base = -> RegularPolygon005
  Dir = (1,0,0)
  DirMode = 0
  FaceMakerClass = Part::FaceMakerExtrusion
  LengthFwd = 0
  LengthRev = 0
  Placement = pos=(322,-4,13.5) rot=(0,1,0;1.5708rad)
  Solid = true
  Symmetric = false
FEATURE [Part::RegularPolygon] RegularPolygon006  label="Regular polygon006"
  AttacherType = Attacher::AttachEngine3D
  Circumradius = 3.3
  Placement = pos=(13,0,0) rot=(0,1,0;1.5708rad)
  Polygon = 6
FEATURE [Part::Extrusion] Extrude021
  Base = -> RegularPolygon006
  Dir = (1,0,0)
  DirMode = 0
  FaceMakerClass = Part::FaceMakerExtrusion
  LengthFwd = 0
  LengthRev = 0
  Placement = pos=(353,-4,15) rot=(0,1,0;1.5708rad)
  Solid = true
  Symmetric = false
FEATURE [Part::RegularPolygon] RegularPolygon007  label="Regular polygon007"
  AttacherType = Attacher::AttachEngine3D
  Circumradius = 3.3
  Placement = pos=(13,0,0) rot=(0,1,0;1.5708rad)
  Polygon = 6
FEATURE [Part::Extrusion] Extrude022
  Base = -> RegularPolygon007
  Dir = (1,0,0)
  DirMode = 0
  FaceMakerClass = Part::FaceMakerExtrusion
  LengthFwd = 0
  LengthRev = 0
  Placement = pos=(353,66,15) rot=(0,1,0;1.5708rad)
  Solid = true
  Symmetric = false
FEATURE [Part::RegularPolygon] RegularPolygon008  label="Regular polygon008"
  AttacherType = Attacher::AttachEngine3D
  Circumradius = 3.3
  Placement = pos=(13,0,0) rot=(0,1,0;1.5708rad)
  Polygon = 6
FEATURE [Part::Extrusion] Extrude023
  Base = -> RegularPolygon008
  Dir = (1,0,0)
  DirMode = 0
  FaceMakerClass = Part::FaceMakerExtrusion
  LengthFwd = 0
  LengthRev = 0
  Placement = pos=(322,66,13.5) rot=(0,1,0;1.5708rad)
  Solid = true
  Symmetric = false
FEATURE [Part::MultiFuse] Fusion348
  Placement = pos=(0,0,-6) rot=(0,0,1;0rad)
  Refine = true
  Shapes = -> [Extrude020,Extrude021,Extrude022,Extrude023]
FEATURE [Part::MultiFuse] Fusion349
  Refine = true
  Shapes = -> [Fusion348,Fusion347]
FEATURE [Part::Cylinder] Cylinder401
  Angle = 360
  AttacherType = Attacher::AttachEngine3D
  Height = 10
  Placement = pos=(3.5,96,3.5) rot=(1,0,0;1.5708rad)
  Radius = 1.25
FEATURE [Part::Cylinder] Cylinder402
  Angle = 360
  AttacherType = Attacher::AttachEngine3D
  Height = 10
  Placement = pos=(3.5,96,46.5) rot=(1,0,0;1.5708rad)
  Radius = 1.25
FEATURE [Part::Cylinder] Cylinder403
  Angle = 360
  AttacherType = Attacher::AttachEngine3D
  Height = 10
  Placement = pos=(76.5,96,46.5) rot=(1,0,0;1.5708rad)
  Radius = 1.25
FEATURE [Part::Cylinder] Cylinder404
  Angle = 360
  AttacherType = Attacher::AttachEngine3D
  Height = 10
  Placement = pos=(76.5,96,3.5) rot=(1,0,0;1.5708rad)
  Radius = 1.25
FEATURE [Part::MultiFuse] Fusion353
  Placement = pos=(306,0,-55) rot=(0,-1,0;0.05236rad)
  Refine = true
  Shapes = -> [Cylinder401,Cylinder402,Cylinder403,Cylinder404]
FEATURE [Part::MultiFuse] Fusion355
  Refine = true
  Shapes = -> [Fusion353,Fusion282]
FEATURE [Part::Box] Box275  label="Cube355"
  AttacherType = Attacher::AttachEngine3D
  Height = 48
  Length = 75
  Placement = pos=(2.5,-14,-0.5) rot=(0,0,1;0rad)
  Width = 100
FEATURE [Part::Box] Box276  label="Cube356"
  AttacherType = Attacher::AttachEngine3D
  Height = 8
  Length = 67.5
  Placement = pos=(6.25,-24,-0.5) rot=(0,0,1;0rad)
  Width = 120
FEATURE [Part::MultiFuse] Fusion356
  Refine = true
  Shapes = -> [Box275,Box276]
FEATURE [Part::Fillet] Fillet106
  Base = -> Cut232
  Edges = 11 edges r=3: [Edge1,Edge2,Edge3,Edge4,Edge5,Edge6,Edge7,Edge9,Edge10,Edge11,Edge12]
FEATURE [Part::Cylinder] Cylinder409
  Angle = 360
  AttacherType = Attacher::AttachEngine3D
  Height = 3
  Placement = pos=(3.5,96,3.5) rot=(1,0,0;1.5708rad)
  Radius = 4
FEATURE [Part::Cylinder] Cylinder410
  Angle = 360
  AttacherType = Attacher::AttachEngine3D
  Height = 3
  Placement = pos=(76.5,96,3.5) rot=(1,0,0;1.5708rad)
  Radius = 4
FEATURE [Part::Cylinder] Cylinder411
  Angle = 360
  AttacherType = Attacher::AttachEngine3D
  Height = 3
  Placement = pos=(3.5,96,46.5) rot=(1,0,0;1.5708rad)
  Radius = 4
FEATURE [Part::Cylinder] Cylinder412
  Angle = 360
  AttacherType = Attacher::AttachEngine3D
  Height = 3
  Placement = pos=(76.5,96,46.5) rot=(1,0,0;1.5708rad)
  Radius = 4
FEATURE [Part::MultiFuse] Fusion358
  Placement = pos=(306,0,-55) rot=(0,-1,0;0.05236rad)
  Refine = true
  Shapes = -> [Cylinder409,Cylinder411,Cylinder412,Cylinder410]
FEATURE [Part::MultiFuse] Fusion359
  Refine = true
  Shapes = -> [Fusion358,Fusion280]
FEATURE [Part::Cut] Cut285
  Base = -> Fillet106
  Refine = true
  Tool = -> Fusion356
FEATURE [Part::Box] Box277  label="Cube357"
  AttacherType = Attacher::AttachEngine3D
  Height = 15
  Length = 6
  Placement = pos=(2.5,-24,0) rot=(0,0,1;0rad)
  Width = 10
FEATURE [Part::Box] Box278  label="Cube358"
  AttacherType = Attacher::AttachEngine3D
  Height = 12.5
  Length = 6
  Placement = pos=(2.5,-14,2.5) rot=(0,0,1;0rad)
  Width = 10
FEATURE [Part::MultiFuse] Fusion360
  Refine = true
  Shapes = -> [Box277,Box278]
FEATURE [Part::Box] Box279  label="Cube359"
  AttacherType = Attacher::AttachEngine3D
  Height = 12.5
  Length = 6
  Placement = pos=(2.5,-14,2.5) rot=(0,0,1;0rad)
  Width = 10
FEATURE [Part::Box] Box280  label="Cube360"
  AttacherType = Attacher::AttachEngine3D
  Height = 15
  Length = 6
  Placement = pos=(2.5,-24,0) rot=(0,0,1;0rad)
  Width = 10
FEATURE [Part::MultiFuse] Fusion361
  Placement = pos=(69,0,0) rot=(0,0,1;0rad)
  Refine = true
  Shapes = -> [Box280,Box279]
FEATURE [Part::Box] Box281  label="Cube361"
  AttacherType = Attacher::AttachEngine3D
  Height = 15
  Length = 6
  Placement = pos=(2.5,86,0) rot=(0,0,1;0rad)
  Width = 10
FEATURE [Part::Box] Box282  label="Cube362"
  AttacherType = Attacher::AttachEngine3D
  Height = 12.5
  Length = 6
  Placement = pos=(2.5,76,2.5) rot=(0,0,1;0rad)
  Width = 10
FEATURE [Part::MultiFuse] Fusion362
  Refine = true
  Shapes = -> [Box281,Box282]
FEATURE [Part::Box] Box283  label="Cube363"
  AttacherType = Attacher::AttachEngine3D
  Height = 15
  Length = 6
  Placement = pos=(2.5,86,0) rot=(0,0,1;0rad)
  Width = 10
FEATURE [Part::Box] Box284  label="Cube364"
  AttacherType = Attacher::AttachEngine3D
  Height = 12.5
  Length = 6
  Placement = pos=(2.5,76,2.5) rot=(0,0,1;0rad)
  Width = 10
FEATURE [Part::MultiFuse] Fusion363
  Placement = pos=(69,0,0) rot=(0,0,1;0rad)
  Refine = true
  Shapes = -> [Box283,Box284]
FEATURE [Part::MultiFuse] Fusion364
  Refine = true
  Shapes = -> [Fusion360,Fusion361,Fusion363,Fusion362]
FEATURE [Part::Chamfer] Chamfer027
  Base = -> Fusion364
  Edges = 4 edges r=5.99: [Edge17,Edge36,Edge53,Edge72]
FEATURE [Part::Cylinder] Cylinder413  label="Cylinder548"
  Angle = 360
  AttacherType = Attacher::AttachEngine3D
  Height = 10
  Placement = pos=(4.5,-24,45.5) rot=(-1,0,0;1.5708rad)
  Radius = 3
FEATURE [Part::Cylinder] Cylinder414  label="Cylinder549"
  Angle = 360
  AttacherType = Attacher::AttachEngine3D
  Height = 10
  Placement = pos=(75.5,-24,45.5) rot=(-1,0,0;1.5708rad)
  Radius = 3
FEATURE [Part::MultiFuse] Fusion365
  Refine = true
  Shapes = -> [Cylinder413,Cylinder414]
FEATURE [Part::Cylinder] Cylinder415  label="Cylinder550"
  Angle = 360
  AttacherType = Attacher::AttachEngine3D
  Height = 10
  Placement = pos=(75.5,-24,45.5) rot=(-1,0,0;1.5708rad)
  Radius = 3
FEATURE [Part::Cylinder] Cylinder416  label="Cylinder551"
  Angle = 360
  AttacherType = Attacher::AttachEngine3D
  Height = 10
  Placement = pos=(4.5,-24,45.5) rot=(-1,0,0;1.5708rad)
  Radius = 3
FEATURE [Part::MultiFuse] Fusion366
  Placement = pos=(0,110,0) rot=(0,0,1;0rad)
  Refine = true
  Shapes = -> [Cylinder416,Cylinder415]
FEATURE [Part::MultiFuse] Fusion367
  Refine = true
  Shapes = -> [Fusion366,Fusion365]
FEATURE [Part::MultiFuse] Fusion368
  Placement = pos=(306,-5,-55) rot=(0,-1,0;0.05236rad)
  Refine = true
  Shapes = -> [Cut285,Chamfer027,Fusion367]
FEATURE [Part::MultiFuse] Fusion369
  Refine = true
  Shapes = -> [Fusion368,Fusion278]
FEATURE [Part::Cut] Cut286
  Base = -> Fusion369
  Refine = true
  Tool = -> Fusion349
FEATURE [Part::MultiFuse] Fusion370
  Refine = true
  Shapes = -> [Cut286,Fusion359]
FEATURE [Part::Cut] Cut287
  Base = -> Fusion370
  Refine = true
  Tool = -> Fusion272
FEATURE [Part::Cut] Cut288
  Base = -> Cut287
  Refine = true
  Tool = -> Fusion355
FEATURE [Part::Box] Box285  label="Cube365"
  AttacherType = Attacher::AttachEngine3D
  Height = 15.5
  Length = 12
  Placement = pos=(314,86,-36) rot=(0,-1,0;0.05236rad)
  Width = 10
FEATURE [Part::Cut] Cut289
  Base = -> Cut288
  Refine = true
  Tool = -> Box285
FEATURE [Part::Box] Box288  label="Cube368"
  AttacherType = Attacher::AttachEngine3D
  Height = 2.5
  Length = 74.5
  Placement = pos=(2.75,-13.75,-0.5) rot=(0,0,1;0rad)
  Width = 99.5
FEATURE [Part::Box] Box289  label="Cube369"
  AttacherType = Attacher::AttachEngine3D
  Height = 2.5
  Length = 62.5
  Placement = pos=(8.75,-23.75,-0.5) rot=(0,0,1;0rad)
  Width = 119.5
FEATURE [Part::MultiFuse] Fusion371
  Refine = true
  Shapes = -> [Box288,Box289]
FEATURE [Part::Chamfer] Chamfer028
  Base = -> Fusion371
  Edges = 12 edges r=0.5: [Edge2,Edge7,Edge10,Edge11,Edge14,Edge19,Edge22,Edge23,Edge26,Edge31,Edge33,Edge36]
  Placement = pos=(306,-5,-54.5) rot=(0,-1,0;0.05236rad)
FEATURE [Part::Cylinder] Cylinder417  label="Cylinder552"
  Angle = 360
  AttacherType = Attacher::AttachEngine3D
  Height = 15
  Placement = pos=(311.5,-14,-56) rot=(0,-1,0;0.05236rad)
  Radius = 1.25
FEATURE [Part::Cylinder] Cylinder418  label="Cylinder553"
  Angle = 360
  AttacherType = Attacher::AttachEngine3D
  Height = 15
  Placement = pos=(380.5,-14,-52) rot=(0,-1,0;0.05236rad)
  Radius = 1.25
FEATURE [Part::MultiFuse] Fusion372
  Refine = true
  Shapes = -> [Cylinder417,Cylinder418]
FEATURE [Part::Cylinder] Cylinder419  label="Cylinder554"
  Angle = 360
  AttacherType = Attacher::AttachEngine3D
  Height = 15
  Placement = pos=(380.5,-14,-52) rot=(0,-1,0;0.05236rad)
  Radius = 1.25
FEATURE [Part::Cylinder] Cylinder420  label="Cylinder555"
  Angle = 360
  AttacherType = Attacher::AttachEngine3D
  Height = 15
  Placement = pos=(311.5,-14,-56) rot=(0,-1,0;0.05236rad)
  Radius = 1.25
FEATURE [Part::MultiFuse] Fusion373
  Placement = pos=(0,90,0) rot=(0,0,1;0rad)
  Refine = true
  Shapes = -> [Cylinder420,Cylinder419]
FEATURE [Part::MultiFuse] Fusion374
  Refine = true
  Shapes = -> [Fusion373,Fusion372]
FEATURE [Part::Cylinder] Cylinder421  label="Cylinder556"
  Angle = 360
  AttacherType = Attacher::AttachEngine3D
  Height = 2
  Placement = pos=(311.5,-14,-56) rot=(0,-1,0;0.05236rad)
  Radius = 3
FEATURE [Part::Cylinder] Cylinder422  label="Cylinder557"
  Angle = 360
  AttacherType = Attacher::AttachEngine3D
  Height = 2
  Placement = pos=(380.5,-14,-52) rot=(0,-1,0;0.05236rad)
  Radius = 3
FEATURE [Part::Cylinder] Cylinder423  label="Cylinder558"
  Angle = 360
  AttacherType = Attacher::AttachEngine3D
  Height = 2
  Placement = pos=(311.5,-14,-56) rot=(0,-1,0;0.05236rad)
  Radius = 3
FEATURE [Part::MultiFuse] Fusion376
  Refine = true
  Shapes = -> [Cylinder423,Cylinder422]
FEATURE [Part::Cylinder] Cylinder424  label="Cylinder559"
  Angle = 360
  AttacherType = Attacher::AttachEngine3D
  Height = 2
  Placement = pos=(380.5,-14,-52) rot=(0,-1,0;0.05236rad)
  Radius = 3
FEATURE [Part::MultiFuse] Fusion377
  Placement = pos=(0,90,0) rot=(0,0,1;0rad)
  Refine = true
  Shapes = -> [Cylinder421,Cylinder424]
FEATURE [Part::MultiFuse] Fusion375
  Refine = true
  Shapes = -> [Fusion377,Fusion376]
FEATURE [Part::Cylinder] Cylinder425  label="Cylinder560"
  Angle = 360
  AttacherType = Attacher::AttachEngine3D
  Height = 15
  Placement = pos=(380.5,-14,-52) rot=(0,-1,0;0.05236rad)
  Radius = 1.6
FEATURE [Part::Cylinder] Cylinder426  label="Cylinder561"
  Angle = 360
  AttacherType = Attacher::AttachEngine3D
  Height = 15
  Placement = pos=(380.5,-14,-52) rot=(0,-1,0;0.05236rad)
  Radius = 1.6
FEATURE [Part::Cylinder] Cylinder427  label="Cylinder562"
  Angle = 360
  AttacherType = Attacher::AttachEngine3D
  Height = 15
  Placement = pos=(311.5,-14,-56) rot=(0,-1,0;0.05236rad)
  Radius = 1.6
FEATURE [Part::MultiFuse] Fusion378
  Placement = pos=(0,90,0) rot=(0,0,1;0rad)
  Refine = true
  Shapes = -> [Cylinder427,Cylinder426]
FEATURE [Part::Cylinder] Cylinder428  label="Cylinder563"
  Angle = 360
  AttacherType = Attacher::AttachEngine3D
  Height = 15
  Placement = pos=(311.5,-14,-56) rot=(0,-1,0;0.05236rad)
  Radius = 1.6
FEATURE [Part::MultiFuse] Fusion380
  Refine = true
  Shapes = -> [Cylinder428,Cylinder425]
FEATURE [Part::MultiFuse] Fusion379
  Refine = true
  Shapes = -> [Fusion378,Fusion380]
FEATURE [Part::MultiFuse] Fusion381
  Refine = true
  Shapes = -> [Fusion375,Fusion379]
FEATURE [Part::Cylinder] Cylinder429  label="Cylinder564"
  Angle = 360
  AttacherType = Attacher::AttachEngine3D
  Height = 2
  Placement = pos=(380.5,-14,-52) rot=(0,-1,0;0.05236rad)
  Radius = 3
FEATURE [Part::Cylinder] Cylinder430  label="Cylinder565"
  Angle = 360
  AttacherType = Attacher::AttachEngine3D
  Height = 15
  Placement = pos=(380.5,-14,-52) rot=(0,-1,0;0.05236rad)
  Radius = 1.25
FEATURE [Part::Cylinder] Cylinder431  label="Cylinder566"
  Angle = 360
  AttacherType = Attacher::AttachEngine3D
  Height = 2
  Placement = pos=(380.5,-14,-52) rot=(0,-1,0;0.05236rad)
  Radius = 3
FEATURE [Part::Cylinder] Cylinder432  label="Cylinder567"
  Angle = 360
  AttacherType = Attacher::AttachEngine3D
  Height = 15
  Placement = pos=(311.5,-14,-56) rot=(0,-1,0;0.05236rad)
  Radius = 1.25
FEATURE [Part::MultiFuse] Fusion383
  Placement = pos=(0,90,0) rot=(0,0,1;0rad)
  Refine = true
  Shapes = -> [Cylinder432,Cylinder430]
FEATURE [Part::Cylinder] Cylinder433  label="Cylinder568"
  Angle = 360
  AttacherType = Attacher::AttachEngine3D
  Height = 15
  Placement = pos=(311.5,-14,-56) rot=(0,-1,0;0.05236rad)
  Radius = 1.25
FEATURE [Part::Cylinder] Cylinder434  label="Cylinder569"
  Angle = 360
  AttacherType = Attacher::AttachEngine3D
  Height = 15
  Placement = pos=(380.5,-14,-52) rot=(0,-1,0;0.05236rad)
  Radius = 1.25
FEATURE [Part::MultiFuse] Fusion382
  Refine = true
  Shapes = -> [Cylinder433,Cylinder434]
FEATURE [Part::MultiFuse] Fusion385
  Refine = true
  Shapes = -> [Fusion383,Fusion382]
FEATURE [Part::Cylinder] Cylinder435  label="Cylinder570"
  Angle = 360
  AttacherType = Attacher::AttachEngine3D
  Height = 2
  Placement = pos=(311.5,-14,-56) rot=(0,-1,0;0.05236rad)
  Radius = 3
FEATURE [Part::MultiFuse] Fusion384
  Placement = pos=(0,90,0) rot=(0,0,1;0rad)
  Refine = true
  Shapes = -> [Cylinder435,Cylinder431]
FEATURE [Part::Cylinder] Cylinder436  label="Cylinder571"
  Angle = 360
  AttacherType = Attacher::AttachEngine3D
  Height = 2
  Placement = pos=(311.5,-14,-56) rot=(0,-1,0;0.05236rad)
  Radius = 3
FEATURE [Part::MultiFuse] Fusion387
  Refine = true
  Shapes = -> [Cylinder436,Cylinder429]
FEATURE [Part::MultiFuse] Fusion386
  Refine = true
  Shapes = -> [Fusion384,Fusion387]
FEATURE [Part::MultiFuse] Fusion388
  Refine = true
  Shapes = -> [Fusion386,Fusion385]
FEATURE [Part::MultiFuse] Fusion389
  Refine = true
  Shapes = -> [Fusion388,Fusion374]
FEATURE [Part::Cut] Cut290
  Base = -> Cut289
  Refine = true
  Tool = -> Fusion389
FEATURE [Part::Cut] Cut291  label="battery-box-wide-closure"
  Base = -> Chamfer028
  Refine = true
  Tool = -> Fusion381
FEATURE [Part::Chamfer] Chamfer029
  Base = -> Box231
  Edges = 1 edges: [Edge2 r1=5 r2=4.75]
FEATURE [Part::Box] Box290  label="Cube370"
  AttacherType = Attacher::AttachEngine3D
  Height = 9
  Length = 45
  Placement = pos=(337,59,-14) rot=(0,-1,0;0.05236rad)
  Width = 2.5
FEATURE [Part::Box] Box291  label="Cube371"
  AttacherType = Attacher::AttachEngine3D
  Height = 9
  Length = 45
  Placement = pos=(338,10,-14) rot=(0,-1,0;0.05236rad)
  Width = 2.5
FEATURE [Part::MultiFuse] Fusion390
  Refine = true
  Shapes = -> [Box229,Box290,Box291,Chamfer029]
FEATURE [Part::MultiFuse] Fusion391
  Refine = true
  Shapes = -> [Cut290,Fusion390]
FEATURE [Part::Cylinder] Cylinder437  label="Cylinder572"
  Angle = 360
  AttacherType = Attacher::AttachEngine3D
  Height = 10
  Placement = pos=(374,6,-8.5) rot=(0,1,0;1.51844rad)
  Radius = 3.5
FEATURE [Part::Cylinder] Cylinder438  label="Cylinder573"
  Angle = 360
  AttacherType = Attacher::AttachEngine3D
  Height = 10
  Placement = pos=(374,-4,-8.5) rot=(0,1,0;1.51844rad)
  Radius = 3.5
FEATURE [Part::MultiFuse] Fusion392
  Refine = true
  Shapes = -> [Cylinder438,Cylinder437]
FEATURE [Part::Box] Box292
  AttacherType = Attacher::AttachEngine3D
  Height = 17
  Length = 35
  Placement = pos=(565,-9,1.5) rot=(0,0,1;0rad)
  Width = 20
FEATURE [Part::Box] Box293
  AttacherType = Attacher::AttachEngine3D
  Height = 32
  Length = 10
  Placement = pos=(600,-10,-3.6) rot=(0,-1,0;0.05236rad)
  Width = 82
FEATURE [Part::Box] Box295
  AttacherType = Attacher::AttachEngine3D
  Height = 17
  Length = 35
  Placement = pos=(565,51,1.5) rot=(0,0,1;0rad)
  Width = 20
FEATURE [Part::Box] Box296
  AttacherType = Attacher::AttachEngine3D
  Height = 18.5
  Length = 20
  Placement = pos=(570,11,1.5) rot=(0,0,1;0rad)
  Width = 40
FEATURE [Part::Cylinder] Cylinder439
  Angle = 360
  AttacherType = Attacher::AttachEngine3D
  Height = 15
  Placement = pos=(588,6,10) rot=(1,0,0;1.5708rad)
  Radius = 1.25
FEATURE [Part::Cylinder] Cylinder440
  Angle = 360
  AttacherType = Attacher::AttachEngine3D
  Height = 15
  Placement = pos=(588,71,10) rot=(1,0,0;1.5708rad)
  Radius = 1.25
FEATURE [Part::MultiFuse] Fusion394
  Refine = true
  Shapes = -> [Cylinder439,Cylinder440]
FEATURE [Part::Cylinder] Cylinder441
  Angle = 360
  AttacherType = Attacher::AttachEngine3D
  Height = 15
  Placement = pos=(585,7,14) rot=(0,1,0;1.5708rad)
  Radius = 1.25
FEATURE [Part::Cylinder] Cylinder442
  Angle = 360
  AttacherType = Attacher::AttachEngine3D
  Height = 15
  Placement = pos=(585,7,6) rot=(0,1,0;1.5708rad)
  Radius = 1.25
FEATURE [Part::MultiFuse] Fusion395
  Placement = pos=(0,-10,0) rot=(0,0,1;0rad)
  Refine = true
  Shapes = -> [Cylinder441,Cylinder442]
FEATURE [Part::Cylinder] Cylinder443
  Angle = 360
  AttacherType = Attacher::AttachEngine3D
  Height = 15
  Placement = pos=(585,7,14) rot=(0,1,0;1.5708rad)
  Radius = 1.25
FEATURE [Part::Cylinder] Cylinder444
  Angle = 360
  AttacherType = Attacher::AttachEngine3D
  Height = 15
  Placement = pos=(585,7,6) rot=(0,1,0;1.5708rad)
  Radius = 1.25
FEATURE [Part::MultiFuse] Fusion396
  Placement = pos=(0,58,0) rot=(0,0,1;0rad)
  Refine = true
  Shapes = -> [Cylinder443,Cylinder444]
FEATURE [Part::MultiFuse] Fusion397
  Refine = true
  Shapes = -> [Fusion395,Fusion396]
FEATURE [Part::Box] Box297
  AttacherType = Attacher::AttachEngine3D
  Height = 5
  Length = 4
  Placement = pos=(579,-6,1.5) rot=(0,0,1;0rad)
  Width = 4
FEATURE [Part::Box] Box298
  AttacherType = Attacher::AttachEngine3D
  Height = 5
  Length = 4
  Placement = pos=(579,64,1.5) rot=(0,0,1;0rad)
  Width = 4
FEATURE [Part::MultiFuse] Fusion398
  Refine = true
  Shapes = -> [Box298,Box297]
FEATURE [Part::Cylinder] Cylinder445
  Angle = 360
  AttacherType = Attacher::AttachEngine3D
  Height = 20
  Placement = pos=(586,31,1.5) rot=(0,0,1;0rad)
  Radius = 1.25
FEATURE [Part::Cylinder] Cylinder446
  Angle = 360
  AttacherType = Attacher::AttachEngine3D
  Height = 18.5
  Placement = pos=(584,7,10.5) rot=(0,0,1;0rad)
  Radius = 1.8
FEATURE [Part::Cylinder] Cylinder447
  Angle = 360
  AttacherType = Attacher::AttachEngine3D
  Height = 18.5
  Placement = pos=(584,55,10.5) rot=(0,0,1;0rad)
  Radius = 1.8
FEATURE [Part::MultiFuse] Fusion399
  Placement = pos=(0.5,0,-9) rot=(0,0,1;0rad)
  Refine = true
  Shapes = -> [Cylinder447,Cylinder446]
FEATURE [Part::Cylinder] Cylinder448
  Angle = 360
  AttacherType = Attacher::AttachEngine3D
  Height = 15
  Placement = pos=(588,6,10) rot=(1,0,0;1.5708rad)
  Radius = 1.25
FEATURE [Part::Cylinder] Cylinder449
  Angle = 360
  AttacherType = Attacher::AttachEngine3D
  Height = 15
  Placement = pos=(588,71,10) rot=(1,0,0;1.5708rad)
  Radius = 1.25
FEATURE [Part::MultiFuse] Fusion401
  Placement = pos=(-18,0,0) rot=(0,0,1;0rad)
  Refine = true
  Shapes = -> [Cylinder448,Cylinder449]
FEATURE [Part::Box] Box299
  AttacherType = Attacher::AttachEngine3D
  Height = 1.5
  Length = 35
  Placement = pos=(565,51,18.5) rot=(0,0,1;0rad)
  Width = 10
FEATURE [Part::Box] Box300
  AttacherType = Attacher::AttachEngine3D
  Height = 1.5
  Length = 35
  Placement = pos=(565,1,18.5) rot=(0,0,1;0rad)
  Width = 10
FEATURE [Part::MultiFuse] Fusion402
  Refine = true
  Shapes = -> [Box299,Box300,Box295,Box292,Box296]
FEATURE [Part::Cut] Cut293
  Base = -> Fusion402
  Refine = true
  Tool = -> Box293
FEATURE [Part::Cylinder] Cylinder450
  Angle = 360
  AttacherType = Attacher::AttachEngine3D
  Height = 18.5
  Placement = pos=(584,7,10.5) rot=(0,0,1;0rad)
  Radius = 1.8
FEATURE [Part::Cylinder] Cylinder451
  Angle = 360
  AttacherType = Attacher::AttachEngine3D
  Height = 18.5
  Placement = pos=(584,55,10.5) rot=(0,0,1;0rad)
  Radius = 1.8
FEATURE [Part::MultiFuse] Fusion403
  Placement = pos=(-9.5,0,-9) rot=(0,0,1;0rad)
  Refine = true
  Shapes = -> [Cylinder451,Cylinder450]
FEATURE [Part::MultiFuse] Fusion404
  Refine = true
  Shapes = -> [Fusion394,Fusion401]
FEATURE [Part::Cut] Cut294
  Base = -> Cut293
  Refine = true
  Tool = -> Fusion404
FEATURE [Part::MultiFuse] Fusion405
  Refine = true
  Shapes = -> [Fusion399,Fusion403]
FEATURE [Part::Cut] Cut295
  Base = -> Cut294
  Refine = true
  Tool = -> Fusion405
FEATURE [Part::Fillet] Fillet107
  Base = -> Cut295
  Edges = 4 edges r=3: [Edge1,Edge4,Edge16,Edge52]
FEATURE [Part::Chamfer] Chamfer030
  Base = -> Fillet107
  Edges = 4 edges r=4.99: [Edge43,Edge56,Edge57,Edge58]
FEATURE [Part::Cut] Cut296
  Base = -> Chamfer030
  Refine = true
  Tool = -> Fusion397
FEATURE [Part::Cut] Cut297
  Base = -> Cut296
  Refine = true
  Tool = -> Fusion398
FEATURE [Part::Cut] Cut298  label="rear-cross-member-wide"
  Base = -> Cut297
  Refine = true
  Tool = -> Cylinder445
FEATURE [Part::Box] Box301  label="Cube372"
  AttacherType = Attacher::AttachEngine3D
  Height = 1
  Length = 25
  Placement = pos=(45,-10,19) rot=(0,0,1;0rad)
  Width = 82
FEATURE [Part::Cut] Cut299
  Base = -> Fillet086
  Refine = true
  Tool = -> Box301
FEATURE [Part::Cylinder] Cylinder452
  Angle = 360
  AttacherType = Attacher::AttachEngine3D
  Height = 4
  Placement = pos=(125,50,15) rot=(0,0,1;0rad)
  Radius = 1.2
FEATURE [Part::Cylinder] Cylinder453
  Angle = 360
  AttacherType = Attacher::AttachEngine3D
  Height = 4
  Placement = pos=(125,12,15) rot=(0,0,1;0rad)
  Radius = 1.2
FEATURE [Part::MultiFuse] Fusion406
  Refine = true
  Shapes = -> [Cylinder452,Cylinder280,Cylinder281,Cylinder282,Cylinder283,Cylinder453]
FEATURE [Part::Box] Box302  label="Cube373"
  AttacherType = Attacher::AttachEngine3D
  Height = 3
  Length = 25
  Placement = pos=(45,-10,17) rot=(0,0,1;0rad)
  Width = 82
FEATURE [Part::Box] Box303  label="Cube374"
  AttacherType = Attacher::AttachEngine3D
  Height = 2
  Length = 25
  Placement = pos=(45,-10,17) rot=(0,0,1;0rad)
  Width = 82
FEATURE [Part::Fillet] Fillet108
  Base = -> Box302
  Edges = 2 edges r=2.99: [Edge10,Edge12]
FEATURE [Part::Cut] Cut301
  Base = -> Fillet108
  Refine = true
  Tool = -> Box303
FEATURE [Part::Box] Box304  label="Cube375"
  AttacherType = Attacher::AttachEngine3D
  Height = 1
  Length = 25
  Placement = pos=(45,0,19) rot=(0,0,1;0rad)
  Width = 62
FEATURE [Part::Cut] Cut302
  Base = -> Cut301
  Refine = true
  Tool = -> Box304
FEATURE [Part::Fillet] Fillet109
  Base = -> Cut257
  Edges = 4 edges r=6: [Edge106,Edge119,Edge142,Edge144]
FEATURE [Part::Box] Box305  label="Cube376"
  AttacherType = Attacher::AttachEngine3D
  Height = 1
  Length = 75
  Placement = pos=(69,0,19) rot=(0,0,1;0rad)
  Width = 62
FEATURE [Part::Box] Box306  label="Cube377"
  AttacherType = Attacher::AttachEngine3D
  Height = 1
  Length = 4
  Placement = pos=(69,2,19) rot=(0,0,1;0rad)
  Width = 6
FEATURE [Part::Box] Box307  label="Cube378"
  AttacherType = Attacher::AttachEngine3D
  Height = 1
  Length = 4
  Placement = pos=(69,54,19) rot=(0,0,1;0rad)
  Width = 6
FEATURE [Part::Box] Box308  label="Cube379"
  AttacherType = Attacher::AttachEngine3D
  Height = 1
  Length = 10.5
  Placement = pos=(133.5,28,19) rot=(0,0,1;0rad)
  Width = 6
FEATURE [Part::MultiFuse] Fusion408
  Refine = true
  Shapes = -> [Box306,Box307,Box308]
FEATURE [Part::Cylinder] Cylinder454
  Angle = 360
  AttacherType = Attacher::AttachEngine3D
  Height = 4
  Placement = pos=(125,12,15) rot=(0,0,1;0rad)
  Radius = 1.2
FEATURE [Part::Cylinder] Cylinder455
  Angle = 360
  AttacherType = Attacher::AttachEngine3D
  Height = 4
  Placement = pos=(125,50,15) rot=(0,0,1;0rad)
  Radius = 1.2
FEATURE [Part::MultiFuse] Fusion409
  Placement = pos=(0,0,1) rot=(0,0,1;0rad)
  Refine = true
  Shapes = -> [Cylinder454,Cylinder455]
FEATURE [Part::MultiFuse] Fusion410
  Refine = true
  Shapes = -> [Fusion408,Fusion409]
FEATURE [Part::Cut] Cut303
  Base = -> Box305
  Refine = true
  Tool = -> Fusion410
FEATURE [Part::MultiFuse] Fusion411
  Refine = true
  Shapes = -> [Cut302,Cut303]
FEATURE [Part::MultiFuse] Fusion412  label="fake-cylinder-holder-wide"
  Refine = true
  Shapes = -> [Fillet109,Fusion411]
FEATURE [Part::Cylinder] Cylinder456
  Angle = 360
  AttacherType = Attacher::AttachEngine3D
  Height = 15
  Placement = pos=(80,19,14) rot=(0,1,0;1.5708rad)
  Radius = 1.25
FEATURE [Part::Cylinder] Cylinder457
  Angle = 360
  AttacherType = Attacher::AttachEngine3D
  Height = 15
  Placement = pos=(80,43,14) rot=(0,1,0;1.5708rad)
  Radius = 1.25
FEATURE [Part::MultiFuse] Fusion413
  Placement = pos=(34,0,0) rot=(0,0,1;0rad)
  Refine = true
  Shapes = -> [Cylinder456,Cylinder457]
FEATURE [Part::MultiFuse] Fusion414
  Refine = true
  Shapes = -> [Fusion413,Fusion252,Fusion406]
FEATURE [Part::Cut] Cut304  label="fifth-wheel-plate-wide"
  Base = -> Cut299
  Refine = true
  Tool = -> Fusion414
FEATURE [Part::Cut] Cut305
  Base = -> Fusion264
  Refine = true
  Tool = -> Fusion302
FEATURE [Part::Chamfer] Chamfer031
  Base = -> Cut305
  Edges = 2 edges r=5.49: [Edge26,Edge28]
FEATURE [Part::Chamfer] Chamfer032
  Base = -> Chamfer031
  Edges = 1 edges r=3: [Edge37]
FEATURE [Part::Fillet] Fillet110  label="front-threaded-bar-support-wide"
  Base = -> Chamfer032
  Edges = 2 edges r=4.99: [Edge50,Edge82]
FEATURE [Part::Box] Box309  label="Cube380"
  AttacherType = Attacher::AttachEngine3D
  Height = 10
  Length = 129
  Placement = pos=(286,-34,-6) rot=(0,-1,0;0.05236rad)
  Width = 130
FEATURE [Part::Cut] Cut306
  Base = -> Fusion391
  Refine = true
  Tool = -> Box309
FEATURE [Part::Cut] Cut307  label="battery-box-wide"
  Base = -> Cut306
  Refine = true
  Tool = -> Fusion392
FEATURE [Part::Box] Box310  label="Cube381"
  AttacherType = Attacher::AttachEngine3D
  Height = 24
  Length = 34
  Placement = pos=(565,-11,-2) rot=(0,0,1;0rad)
  Width = 12
FEATURE [Part::Box] Box311  label="Cube382"
  AttacherType = Attacher::AttachEngine3D
  Height = 20
  Length = 34
  Placement = pos=(565,-9,0) rot=(0,0,1;0rad)
  Width = 12
FEATURE [Part::Fillet] Fillet111
  Base = -> Box311
  Edges = 2 edges r=3: [Edge9,Edge10]
FEATURE [Part::Cut] Cut308
  Base = -> Box310
  Refine = true
  Tool = -> Fillet111
FEATURE [Part::Cylinder] Cylinder458
  Angle = 360
  AttacherType = Attacher::AttachEngine3D
  Height = 15
  Placement = pos=(588,6,10) rot=(1,0,0;1.5708rad)
  Radius = 1.6
FEATURE [Part::Cylinder] Cylinder459
  Angle = 360
  AttacherType = Attacher::AttachEngine3D
  Height = 15
  Placement = pos=(570,6,10) rot=(1,0,0;1.5708rad)
  Radius = 1.6
FEATURE [Part::MultiFuse] Fusion415
  Placement = pos=(0,-4,0) rot=(0,0,1;0rad)
  Refine = true
  Shapes = -> [Cylinder459,Cylinder458]
FEATURE [Part::Cut] Cut309  label="rear-cross-member-wide-HOLES"
  Base = -> Cut308
  Refine = true
  Tool = -> Fusion415
FEATURE [Part::Cylinder] Cylinder460  label="Cylinder574"
  Angle = 360
  AttacherType = Attacher::AttachEngine3D
  Height = 10
  Placement = pos=(120,-21,13) rot=(-1,0,0;1.5708rad)
  Radius = 1.6
FEATURE [Part::Box] Box312  label="Cube383"
  AttacherType = Attacher::AttachEngine3D
  Height = 17
  Length = 8
  Placement = pos=(116,-16,10) rot=(0,0,1;0rad)
  Width = 7.5
FEATURE [Part::Chamfer] Chamfer033
  Base = -> Box312
  Edges = 1 edges r=3: [Edge9]
FEATURE [Part::Chamfer] Chamfer034
  Base = -> Chamfer033
  Edges = 1 edges: [Edge8 r1=7 r2=2]
FEATURE [Part::Box] Box313  label="Cube384"
  AttacherType = Attacher::AttachEngine3D
  Height = 12
  Length = 10
  Placement = pos=(116,-10,8) rot=(0,0,1;0rad)
  Width = 3
FEATURE [Part::Fillet] Fillet112
  Base = -> Box313
  Edges = 1 edges r=2.99: [Edge10]
FEATURE [Part::Cut] Cut310
  Base = -> Chamfer034
  Refine = true
  Tool = -> Fillet112
FEATURE [Part::Box] Box314  label="Cube385"
  AttacherType = Attacher::AttachEngine3D
  Height = 12
  Length = 10
  Placement = pos=(116,-10,20) rot=(0,0,1;0rad)
  Width = 3
FEATURE [Part::Cut] Cut311
  Base = -> Cut310
  Refine = true
  Tool = -> Box314
FEATURE [Part::Chamfer] Chamfer035
  Base = -> Cut311
  Edges = 1 edges: [Edge14 r1=2 r2=3]
FEATURE [Part::Box] Box316  label="Cube387"
  AttacherType = Attacher::AttachEngine3D
  Height = 17
  Length = 8
  Placement = pos=(116,-16,10) rot=(0,0,1;0rad)
  Width = 7.5
FEATURE [Part::Chamfer] Chamfer036
  Base = -> Box316
  Edges = 1 edges r=3: [Edge9]
FEATURE [Part::Chamfer] Chamfer037
  Base = -> Chamfer036
  Edges = 1 edges: [Edge8 r1=7 r2=2]
FEATURE [Part::Box] Box317  label="Cube388"
  AttacherType = Attacher::AttachEngine3D
  Height = 17
  Length = 6
  Placement = pos=(117,-20,10) rot=(0,0,1;0rad)
  Width = 7.5
FEATURE [Part::Cut] Cut312
  Base = -> Box317
  Placement = pos=(0,1,0) rot=(0,0,1;0rad)
  Refine = true
  Tool = -> Chamfer037
FEATURE [Part::Cut] Cut313
  Base = -> Chamfer035
  Refine = true
  Tool = -> Cut312
FEATURE [Part::Cylinder] Cylinder461  label="Cylinder575"
  Angle = 360
  AttacherType = Attacher::AttachEngine3D
  Height = 3
  Placement = pos=(120,-15,13) rot=(-1,0,0;1.5708rad)
  Radius = 3
FEATURE [Part::MultiFuse] Fusion416
  Refine = true
  Shapes = -> [Cut313,Cylinder461]
FEATURE [Part::Cut] Cut314  label="kipper-holder-left"
  Base = -> Fusion416
  Refine = true
  Tool = -> Cylinder460
FEATURE [Part::Cylinder] Cylinder462  label="Cylinder576"
  Angle = 360
  AttacherType = Attacher::AttachEngine3D
  Height = 10
  Placement = pos=(120,-21,13) rot=(-1,0,0;1.5708rad)
  Radius = 1.6
FEATURE [Part::Box] Box318  label="Cube389"
  AttacherType = Attacher::AttachEngine3D
  Height = 17
  Length = 8
  Placement = pos=(116,-16,10) rot=(0,0,1;0rad)
  Width = 7.5
FEATURE [Part::Chamfer] Chamfer038
  Base = -> Box318
  Edges = 1 edges r=3: [Edge9]
FEATURE [Part::Chamfer] Chamfer039
  Base = -> Chamfer038
  Edges = 1 edges: [Edge8 r1=7 r2=2]
FEATURE [Part::Box] Box319  label="Cube390"
  AttacherType = Attacher::AttachEngine3D
  Height = 12
  Length = 10
  Placement = pos=(116,-10,8) rot=(0,0,1;0rad)
  Width = 3
FEATURE [Part::Fillet] Fillet113
  Base = -> Box319
  Edges = 1 edges r=2.99: [Edge10]
FEATURE [Part::Cut] Cut315
  Base = -> Chamfer039
  Refine = true
  Tool = -> Fillet113
FEATURE [Part::Box] Box320  label="Cube391"
  AttacherType = Attacher::AttachEngine3D
  Height = 12
  Length = 10
  Placement = pos=(116,-10,20) rot=(0,0,1;0rad)
  Width = 3
FEATURE [Part::Cut] Cut316
  Base = -> Cut315
  Refine = true
  Tool = -> Box320
FEATURE [Part::Chamfer] Chamfer040
  Base = -> Cut316
  Edges = 1 edges: [Edge14 r1=2 r2=3]
FEATURE [Part::Box] Box321  label="Cube392"
  AttacherType = Attacher::AttachEngine3D
  Height = 17
  Length = 8
  Placement = pos=(116,-16,10) rot=(0,0,1;0rad)
  Width = 7.5
FEATURE [Part::Chamfer] Chamfer041
  Base = -> Box321
  Edges = 1 edges r=3: [Edge9]
FEATURE [Part::Chamfer] Chamfer042
  Base = -> Chamfer041
  Edges = 1 edges: [Edge8 r1=7 r2=2]
FEATURE [Part::Box] Box322  label="Cube393"
  AttacherType = Attacher::AttachEngine3D
  Height = 17
  Length = 6
  Placement = pos=(117,-20,10) rot=(0,0,1;0rad)
  Width = 7.5
FEATURE [Part::Cut] Cut317
  Base = -> Box322
  Placement = pos=(0,1,0) rot=(0,0,1;0rad)
  Refine = true
  Tool = -> Chamfer042
FEATURE [Part::Cut] Cut318
  Base = -> Chamfer040
  Refine = true
  Tool = -> Cut317
FEATURE [Part::Cylinder] Cylinder463  label="Cylinder577"
  Angle = 360
  AttacherType = Attacher::AttachEngine3D
  Height = 3
  Placement = pos=(120,-15,13) rot=(-1,0,0;1.5708rad)
  Radius = 3
FEATURE [Part::MultiFuse] Fusion417
  Refine = true
  Shapes = -> [Cut318,Cylinder463]
FEATURE [Part::Cut] Cut319  label="kipper-holder-right"
  Base = -> Fusion417
  Placement = pos=(240,62,0) rot=(0,0,1;3.14159rad)
  Refine = true
  Tool = -> Cylinder462
FEATURE [Part::Box] Box323  label="Cube394"
  AttacherType = Attacher::AttachEngine3D
  Height = 10
  Length = 10
  Placement = pos=(429.5,-12.5,5) rot=(0,0,1;0rad)
  Width = 2.5
FEATURE [Part::Box] Box324  label="Cube395"
  AttacherType = Attacher::AttachEngine3D
  Height = 10
  Length = 10
  Placement = pos=(429.5,72,5) rot=(0,0,1;0rad)
  Width = 2.5
FEATURE [Part::Cylinder] Cylinder464  label="Cylinder578"
  Angle = 360
  AttacherType = Attacher::AttachEngine3D
  Height = 2.5
  Placement = pos=(569.5,72,10) rot=(-1,0,0;1.5708rad)
  Radius = 3.5
FEATURE [Part::Cylinder] Cylinder465  label="Cylinder579"
  Angle = 360
  AttacherType = Attacher::AttachEngine3D
  Height = 2.5
  Placement = pos=(569.5,-10,10) rot=(1,0,0;1.5708rad)
  Radius = 3.5
FEATURE [Part::Cut] Cut320  label="fender-spacer-rear-right"
  Base = -> Cut087
  Refine = true
  Tool = -> Cylinder464
FEATURE [Part::Cut] Cut321  label="fender-spacer-rear-left"
  Base = -> Cut082
  Refine = true
  Tool = -> Cylinder465
FEATURE [Part::Cut] Cut322  label="fender-spacer-front-left"
  Base = -> Cut083
  Refine = true
  Tool = -> Box323
FEATURE [Part::Cut] Cut323  label="fender-spacer-front-right"
  Base = -> Cut086
  Refine = true
  Tool = -> Box324
FEATURE [Part::Cylinder] Cylinder467
  Angle = 360
  AttacherType = Attacher::AttachEngine3D
  Height = 9
  Placement = pos=(546,-17,10) rot=(1,0,0;1.5708rad)
  Radius = 1.6
FEATURE [Part::Cylinder] Cylinder468
  Angle = 360
  AttacherType = Attacher::AttachEngine3D
  Height = 9
  Placement = pos=(459,-17,10) rot=(1,0,0;1.5708rad)
  Radius = 1.6
FEATURE [Part::Cylinder] Cylinder469
  Angle = 360
  AttacherType = Attacher::AttachEngine3D
  Height = 9
  Placement = pos=(564,-17,10) rot=(1,0,0;1.5708rad)
  Radius = 1.6
FEATURE [Part::Cylinder] Cylinder470
  Angle = 360
  AttacherType = Attacher::AttachEngine3D
  Height = 9
  Placement = pos=(441,-17,10) rot=(1,0,0;1.5708rad)
  Radius = 1.6
FEATURE [Part::Box] Box331  label="Cube402"
  AttacherType = Attacher::AttachEngine3D
  Height = 32
  Length = 59
  Placement = pos=(473,-33,-34) rot=(0,-1,0;0.05236rad)
  Width = 20
FEATURE [Part::MultiFuse] Fusion427
  Refine = true
  Shapes = -> [Cylinder468,Cylinder470]
FEATURE [Part::MultiFuse] Fusion428
  Refine = true
  Shapes = -> [Cylinder469,Cylinder467]
FEATURE [Part::Cylinder] Cylinder472
  Angle = 180
  AttacherType = Attacher::AttachEngine3D
  Height = 43
  Placement = pos=(554,-19,-28) rot=(1,0,0;1.5708rad)
  Radius = 52
FEATURE [Part::Cylinder] Cylinder473
  Angle = 180
  AttacherType = Attacher::AttachEngine3D
  Height = 42
  Placement = pos=(554,-19,-28) rot=(1,0,0;1.5708rad)
  Radius = 50
FEATURE [Part::Cylinder] Cylinder474
  Angle = 180
  AttacherType = Attacher::AttachEngine3D
  Height = 2
  Placement = pos=(554,-60,-28) rot=(1,0,0;1.5708rad)
  Radius = 48
FEATURE [Part::MultiFuse] Fusion429
  Refine = true
  Shapes = -> [Cylinder473,Cylinder474]
FEATURE [Part::Cut] Cut332
  Base = -> Cylinder472
  Placement = pos=(-0.706169,-4e-15,-29.0325) rot=(0,-1,0;0.05236rad)
  Refine = true
  Tool = -> Fusion429
FEATURE [Part::Box] Box332  label="Cube403"
  AttacherType = Attacher::AttachEngine3D
  Height = 35
  Length = 128
  Placement = pos=(382,-9,-40.8) rot=(0,-1,0;0.05236rad)
  Width = 3
FEATURE [Part::Cylinder] Cylinder475
  Angle = 180
  AttacherType = Attacher::AttachEngine3D
  Height = 3
  Placement = pos=(448.581,-6,-35.3913) rot=(0.999315,-0.026168,0.026168;1.57148rad)
  Radius = 52
FEATURE [Part::Cut] Cut333
  Base = -> Cylinder475
  Placement = pos=(105.48,-13,6.5) rot=(0,0,1;0rad)
  Refine = true
  Tool = -> Box332
FEATURE [Part::MultiFuse] Fusion430
  Refine = true
  Shapes = -> [Cut332,Cut333]
FEATURE [Part::Cylinder] Cylinder476
  Angle = 180
  AttacherType = Attacher::AttachEngine3D
  Height = 42
  Placement = pos=(554,-19,-28) rot=(1,0,0;1.5708rad)
  Radius = 50
FEATURE [Part::Cylinder] Cylinder477  label="Cylinder580"
  Angle = 180
  AttacherType = Attacher::AttachEngine3D
  Height = 3
  Placement = pos=(448.581,-6,-35.3913) rot=(0.999315,-0.026168,0.026168;1.57148rad)
  Radius = 52
FEATURE [Part::Box] Box333  label="Cube404"
  AttacherType = Attacher::AttachEngine3D
  Height = 35
  Length = 128
  Placement = pos=(382,-9,-40.8) rot=(0,-1,0;0.05236rad)
  Width = 3
FEATURE [Part::Cylinder] Cylinder478  label="Cylinder581"
  Angle = 180
  AttacherType = Attacher::AttachEngine3D
  Height = 43
  Placement = pos=(554,-19,-28) rot=(1,0,0;1.5708rad)
  Radius = 52
FEATURE [Part::Cylinder] Cylinder479  label="Cylinder582"
  Angle = 180
  AttacherType = Attacher::AttachEngine3D
  Height = 2
  Placement = pos=(554,-60,-28) rot=(1,0,0;1.5708rad)
  Radius = 48
FEATURE [Part::MultiFuse] Fusion432
  Refine = true
  Shapes = -> [Cylinder476,Cylinder479]
FEATURE [Part::Cut] Cut334
  Base = -> Cylinder478
  Placement = pos=(-0.706169,-4e-15,-29.0325) rot=(0,-1,0;0.05236rad)
  Refine = true
  Tool = -> Fusion432
FEATURE [Part::Cut] Cut335
  Base = -> Cylinder477
  Placement = pos=(105.48,-13,6.5) rot=(0,0,1;0rad)
  Refine = true
  Tool = -> Box333
FEATURE [Part::MultiFuse] Fusion431
  Placement = pos=(-105,0,-5.5) rot=(0,0,1;0rad)
  Refine = true
  Shapes = -> [Cut334,Cut335]
FEATURE [Part::Cut] Cut336
  Base = -> Fusion430
  Refine = true
  Tool = -> Fusion428
FEATURE [Part::Cut] Cut337
  Base = -> Fusion431
  Refine = true
  Tool = -> Fusion427
FEATURE [Part::Box] Box334  label="Cube405"
  AttacherType = Attacher::AttachEngine3D
  Height = 32
  Length = 59
  Placement = pos=(473,-33,-34) rot=(0,-1,0;0.05236rad)
  Width = 20
FEATURE [Part::Cut] Cut338
  Base = -> Cut336
  Refine = true
  Tool = -> Box331
FEATURE [Part::Cut] Cut339
  Base = -> Cut337
  Refine = true
  Tool = -> Box334
FEATURE [Part::Fillet] Fillet118
  Base = -> Cut338
  Edges = 1 edges r=2: [Edge6]
FEATURE [Part::Fillet] Fillet119
  Base = -> Fillet118
  Edges = 1 edges r=1: [Edge6]
FEATURE [Part::Fillet] Fillet120
  Base = -> Cut339
  Edges = 1 edges r=2: [Edge6]
FEATURE [Part::Fillet] Fillet121
  Base = -> Fillet120
  Edges = 1 edges r=1: [Edge3]
FEATURE [Part::Chamfer] Chamfer045
  Base = -> Fillet121
  Edges = 1 edges r=1.99: [Edge36]
FEATURE [Part::Chamfer] Chamfer046
  Base = -> Fillet119
  Edges = 1 edges r=1.99: [Edge36]
FEATURE [Part::Chamfer] Chamfer047  label="fender-rear-left"
  Base = -> Chamfer046
  Edges = 2 edges r=1.99: [Edge6,Edge30]
FEATURE [Part::Chamfer] Chamfer048  label="fender-front-left"
  Base = -> Chamfer045
  Edges = 2 edges r=1.99: [Edge6,Edge31]
FEATURE [Part::Cylinder] Cylinder480
  Angle = 360
  AttacherType = Attacher::AttachEngine3D
  Height = 9
  Placement = pos=(546,-17,10) rot=(1,0,0;1.5708rad)
  Radius = 1.6
FEATURE [Part::Cylinder] Cylinder481
  Angle = 360
  AttacherType = Attacher::AttachEngine3D
  Height = 9
  Placement = pos=(459,-17,10) rot=(1,0,0;1.5708rad)
  Radius = 1.6
FEATURE [Part::Cylinder] Cylinder482  label="Cylinder583"
  Angle = 360
  AttacherType = Attacher::AttachEngine3D
  Height = 9
  Placement = pos=(564,-17,10) rot=(1,0,0;1.5708rad)
  Radius = 1.6
FEATURE [Part::Cylinder] Cylinder483  label="Cylinder584"
  Angle = 360
  AttacherType = Attacher::AttachEngine3D
  Height = 9
  Placement = pos=(441,-17,10) rot=(1,0,0;1.5708rad)
  Radius = 1.6
FEATURE [Part::Box] Box335  label="Cube406"
  AttacherType = Attacher::AttachEngine3D
  Height = 32
  Length = 59
  Placement = pos=(473,-33,-34) rot=(0,-1,0;0.05236rad)
  Width = 20
FEATURE [Part::MultiFuse] Fusion433
  Refine = true
  Shapes = -> [Cylinder481,Cylinder483]
FEATURE [Part::MultiFuse] Fusion434
  Refine = true
  Shapes = -> [Cylinder482,Cylinder480]
FEATURE [Part::Cylinder] Cylinder484  label="Cylinder585"
  Angle = 180
  AttacherType = Attacher::AttachEngine3D
  Height = 43
  Placement = pos=(554,-19,-28) rot=(1,0,0;1.5708rad)
  Radius = 52
FEATURE [Part::Cylinder] Cylinder485
  Angle = 180
  AttacherType = Attacher::AttachEngine3D
  Height = 42
  Placement = pos=(554,-19,-28) rot=(1,0,0;1.5708rad)
  Radius = 50
FEATURE [Part::Cylinder] Cylinder486
  Angle = 180
  AttacherType = Attacher::AttachEngine3D
  Height = 2
  Placement = pos=(554,-60,-28) rot=(1,0,0;1.5708rad)
  Radius = 48
FEATURE [Part::MultiFuse] Fusion435
  Refine = true
  Shapes = -> [Cylinder485,Cylinder486]
FEATURE [Part::Cut] Cut340
  Base = -> Cylinder484
  Placement = pos=(-0.706169,-4e-15,-29.0325) rot=(0,-1,0;0.05236rad)
  Refine = true
  Tool = -> Fusion435
FEATURE [Part::Box] Box336  label="Cube407"
  AttacherType = Attacher::AttachEngine3D
  Height = 35
  Length = 128
  Placement = pos=(382,-9,-40.8) rot=(0,-1,0;0.05236rad)
  Width = 3
FEATURE [Part::Cylinder] Cylinder487
  Angle = 180
  AttacherType = Attacher::AttachEngine3D
  Height = 3
  Placement = pos=(448.581,-6,-35.3913) rot=(0.999315,-0.026168,0.026168;1.57148rad)
  Radius = 52
FEATURE [Part::Cut] Cut341
  Base = -> Cylinder487
  Placement = pos=(105.48,-13,6.5) rot=(0,0,1;0rad)
  Refine = true
  Tool = -> Box336
FEATURE [Part::MultiFuse] Fusion436
  Refine = true
  Shapes = -> [Cut340,Cut341]
FEATURE [Part::Cylinder] Cylinder488
  Angle = 180
  AttacherType = Attacher::AttachEngine3D
  Height = 42
  Placement = pos=(554,-19,-28) rot=(1,0,0;1.5708rad)
  Radius = 50
FEATURE [Part::Cylinder] Cylinder489  label="Cylinder586"
  Angle = 180
  AttacherType = Attacher::AttachEngine3D
  Height = 3
  Placement = pos=(448.581,-6,-35.3913) rot=(0.999315,-0.026168,0.026168;1.57148rad)
  Radius = 52
FEATURE [Part::Box] Box337  label="Cube408"
  AttacherType = Attacher::AttachEngine3D
  Height = 35
  Length = 128
  Placement = pos=(382,-9,-40.8) rot=(0,-1,0;0.05236rad)
  Width = 3
FEATURE [Part::Cylinder] Cylinder490  label="Cylinder587"
  Angle = 180
  AttacherType = Attacher::AttachEngine3D
  Height = 43
  Placement = pos=(554,-19,-28) rot=(1,0,0;1.5708rad)
  Radius = 52
FEATURE [Part::Cylinder] Cylinder491  label="Cylinder588"
  Angle = 180
  AttacherType = Attacher::AttachEngine3D
  Height = 2
  Placement = pos=(554,-60,-28) rot=(1,0,0;1.5708rad)
  Radius = 48
FEATURE [Part::MultiFuse] Fusion438
  Refine = true
  Shapes = -> [Cylinder488,Cylinder491]
FEATURE [Part::Cut] Cut342
  Base = -> Cylinder490
  Placement = pos=(-0.706169,-4e-15,-29.0325) rot=(0,-1,0;0.05236rad)
  Refine = true
  Tool = -> Fusion438
FEATURE [Part::Cut] Cut343
  Base = -> Cylinder489
  Placement = pos=(105.48,-13,6.5) rot=(0,0,1;0rad)
  Refine = true
  Tool = -> Box337
FEATURE [Part::MultiFuse] Fusion437
  Placement = pos=(-105,0,-5.5) rot=(0,0,1;0rad)
  Refine = true
  Shapes = -> [Cut342,Cut343]
FEATURE [Part::Cut] Cut344
  Base = -> Fusion436
  Refine = true
  Tool = -> Fusion434
FEATURE [Part::Cut] Cut345
  Base = -> Fusion437
  Refine = true
  Tool = -> Fusion433
FEATURE [Part::Box] Box338  label="Cube409"
  AttacherType = Attacher::AttachEngine3D
  Height = 32
  Length = 59
  Placement = pos=(473,-33,-34) rot=(0,-1,0;0.05236rad)
  Width = 20
FEATURE [Part::Cut] Cut346
  Base = -> Cut344
  Refine = true
  Tool = -> Box335
FEATURE [Part::Cut] Cut347
  Base = -> Cut345
  Refine = true
  Tool = -> Box338
FEATURE [Part::Fillet] Fillet122
  Base = -> Cut346
  Edges = 1 edges r=2: [Edge6]
FEATURE [Part::Fillet] Fillet123
  Base = -> Fillet122
  Edges = 1 edges r=1: [Edge6]
FEATURE [Part::Fillet] Fillet124
  Base = -> Cut347
  Edges = 1 edges r=2: [Edge6]
FEATURE [Part::Fillet] Fillet125
  Base = -> Fillet124
  Edges = 1 edges r=1: [Edge3]
FEATURE [Part::Chamfer] Chamfer049
  Base = -> Fillet125
  Edges = 1 edges r=1.99: [Edge36]
FEATURE [Part::Chamfer] Chamfer050
  Base = -> Fillet123
  Edges = 1 edges r=1.99: [Edge36]
FEATURE [Part::Chamfer] Chamfer051  label="fender-rear-left_"
  Base = -> Chamfer050
  Edges = 2 edges r=1.99: [Edge6,Edge30]
FEATURE [Part::Chamfer] Chamfer052  label="fender-front-left_"
  Base = -> Chamfer049
  Edges = 2 edges r=1.99: [Edge6,Edge31]
FEATURE [Part::Mirroring] Part__Mirroring010  label="fender-rear-right"
  Base = (0,0,0)
  Normal = (0,1,0)
  Placement = pos=(0,62,0) rot=(0,0,1;0rad)
  Source = -> Chamfer051
FEATURE [Part::Mirroring] Part__Mirroring011  label="fender-front-right"
  Base = (0,0,0)
  Normal = (0,1,0)
  Placement = pos=(0,62,0) rot=(0,0,1;0rad)
  Source = -> Chamfer052
FEATURE [App::DocumentObjectGroup] Group003  label="Tools"
  Group = -> [Cut309,Cut031,Cut030,Cut018,frame_holes,Cut113]
FEATURE [App::DocumentObjectGroup] Group004  label="Fenders"
  Group = -> [Cut320,Cut321,Cut322,Cut323,Chamfer047,Chamfer048,Part__Mirroring010,Part__Mirroring011]
FEATURE [App::DocumentObjectGroup] Group005  label="Battery Box"
  Group = -> [Fillet105,Cut291,Cut064,Cut065,Cut067,Cut069,Cut307,Box040]
FEATURE [App::DocumentObjectGroup] Group006  label="Frame"
  Group = -> [Cut221,Cut280,Cut298,Fusion412,Cut304,Fillet110,Cut314,Cut319,Fusion147,Part__Mirroring002,Cut094,Cylinder161,Cut062,Cut061,Cut058,Cut057,Cut022,Cut020]
FEATURE [Part::Cylinder] Cylinder090
  Angle = 360
  AttacherType = Attacher::AttachEngine3D
  Height = 8
  Placement = pos=(12,0,16) rot=(0,1,0;1.01229rad)
  Radius = 2.5
FEATURE [Part::Cylinder] Cylinder492  label="Cylinder589"
  Angle = 360
  AttacherType = Attacher::AttachEngine3D
  Height = 26
  Radius = 10
FEATURE [Part::Cylinder] Cylinder493  label="Cylinder590"
  Angle = 360
  AttacherType = Attacher::AttachEngine3D
  Height = 10
  Placement = pos=(-12.5,0,13) rot=(0,0,1;0rad)
  Radius = 1.1
FEATURE [Part::Cylinder] Cylinder494  label="Cylinder591"
  Angle = 360
  AttacherType = Attacher::AttachEngine3D
  Height = 19
  Radius = 22.1
FEATURE [Part::Cylinder] Cylinder495  label="Cylinder592"
  Angle = 360
  AttacherType = Attacher::AttachEngine3D
  Height = 22
  Radius = 18.5
FEATURE [Part::Cylinder] Cylinder496  label="Cylinder593"
  Angle = 360
  AttacherType = Attacher::AttachEngine3D
  Height = 10
  Placement = pos=(12.5,0,13) rot=(0,0,1;0rad)
  Radius = 1.1
FEATURE [Part::Cylinder] Cylinder497  label="Cylinder594"
  Angle = 360
  AttacherType = Attacher::AttachEngine3D
  Height = 12
  Placement = pos=(0,0,0.5) rot=(0,0,1;0rad)
  Radius = 23.5
FEATURE [Part::Cylinder] Cylinder498  label="Cylinder595"
  Angle = 360
  AttacherType = Attacher::AttachEngine3D
  Height = 19
  Radius = 23.5
FEATURE [Part::Cylinder] Cylinder499  label="Cylinder596"
  Angle = 360
  AttacherType = Attacher::AttachEngine3D
  Height = 7
  Radius = 20
FEATURE [Part::Cylinder] Cylinder500  label="Cylinder597"
  Angle = 360
  AttacherType = Attacher::AttachEngine3D
  Height = 8
  Placement = pos=(12,0,16) rot=(0,1,0;1.01229rad)
  Radius = 2.5
FEATURE [Part::Cylinder] Cylinder501  label="Cylinder598"
  Angle = 360
  AttacherType = Attacher::AttachEngine3D
  Height = 8
  Placement = pos=(12,0,16) rot=(0,1,0;1.01229rad)
  Radius = 2.5
FEATURE [Part::Cylinder] Cylinder093
  Angle = 360
  AttacherType = Attacher::AttachEngine3D
  Height = 10
  Placement = pos=(-12.5,0,13) rot=(0,0,1;0rad)
  Radius = 1.1
FEATURE [Part::Cylinder] Cylinder502  label="Cylinder599"
  Angle = 360
  AttacherType = Attacher::AttachEngine3D
  Height = 8
  Placement = pos=(12,0,16) rot=(0,1,0;1.01229rad)
  Radius = 2.5
FEATURE [Part::Mirroring] Part__Mirroring005  label="Cylinder107 (Mirror #1)009"
  Base = (0,0,0)
  Normal = (1,0,0)
  Source = -> Cylinder502
FEATURE [Part::MultiFuse] Fusion443
  Refine = true
  Shapes = -> [Cylinder501,Part__Mirroring005]
FEATURE [Part::Cylinder] Cylinder503  label="Cylinder600"
  Angle = 360
  AttacherType = Attacher::AttachEngine3D
  Height = 8
  Placement = pos=(12,0,16) rot=(0,1,0;1.01229rad)
  Radius = 2.5
FEATURE [Part::Cone] Cone002
  Angle = 360
  AttacherType = Attacher::AttachEngine3D
  Height = 7
  Placement = pos=(0,0,15) rot=(0,0,1;0rad)
  Radius1 = 21
  Radius2 = 15
FEATURE [Part::Cylinder] Cylinder504  label="Cylinder601"
  Angle = 360
  AttacherType = Attacher::AttachEngine3D
  Height = 8
  Placement = pos=(12,0,16) rot=(0,1,0;1.01229rad)
  Radius = 2.5
FEATURE [Part::Mirroring] Part__Mirroring012  label="Cylinder107 (Mirror #1)010"
  Base = (0,0,0)
  Normal = (1,0,0)
  Source = -> Cylinder500
FEATURE [Part::Cylinder] Cylinder091
  Angle = 360
  AttacherType = Attacher::AttachEngine3D
  Height = 8
  Placement = pos=(12,0,16) rot=(0,1,0;1.01229rad)
  Radius = 2.5
FEATURE [Part::Cylinder] Cylinder092
  Angle = 360
  AttacherType = Attacher::AttachEngine3D
  Height = 10
  Placement = pos=(12.5,0,13) rot=(0,0,1;0rad)
  Radius = 1.1
FEATURE [Part::Mirroring] Part__Mirroring013  label="Cylinder107 (Mirror #1)013"
  Base = (0,0,0)
  Normal = (1,0,0)
  Source = -> Cylinder091
FEATURE [Part::MultiFuse] Fusion446
  Placement = pos=(0,0,0) rot=(0,0,1;2.51327rad)
  Refine = true
  Shapes = -> [Cylinder090,Part__Mirroring013]
FEATURE [Part::Cylinder] Cylinder505  label="Cylinder602"
  Angle = 360
  AttacherType = Attacher::AttachEngine3D
  Height = 10
  Placement = pos=(-12.5,0,13) rot=(0,0,1;0rad)
  Radius = 1.1
FEATURE [Part::Cylinder] Cylinder506  label="Cylinder603"
  Angle = 360
  AttacherType = Attacher::AttachEngine3D
  Height = 8
  Placement = pos=(12,0,16) rot=(0,1,0;1.01229rad)
  Radius = 2.5
FEATURE [Part::Cut] Cut350
  Base = -> Cylinder498
  Placement = pos=(0,0,1.5) rot=(0,0,1;0rad)
  Refine = true
  Tool = -> Cylinder494
FEATURE [Part::Cylinder] Cylinder507  label="Cylinder604"
  Angle = 360
  AttacherType = Attacher::AttachEngine3D
  Height = 10
  Placement = pos=(12.5,0,13) rot=(0,0,1;0rad)
  Radius = 1.1
FEATURE [Part::MultiFuse] Fusion447
  Placement = pos=(0,0,0) rot=(0,0,1;2.19911rad)
  Refine = true
  Shapes = -> [Cylinder507,Cylinder505]
FEATURE [Part::Cylinder] Cylinder508  label="Cylinder605"
  Angle = 360
  AttacherType = Attacher::AttachEngine3D
  Height = 8
  Placement = pos=(12,0,16) rot=(0,1,0;1.01229rad)
  Radius = 2.5
FEATURE [Part::Mirroring] Part__Mirroring014  label="Cylinder107 (Mirror #1)012"
  Base = (0,0,0)
  Normal = (1,0,0)
  Source = -> Cylinder508
FEATURE [Part::MultiFuse] Fusion442
  Placement = pos=(0,0,0) rot=(0,0,1;1.88496rad)
  Refine = true
  Shapes = -> [Cylinder506,Part__Mirroring014]
FEATURE [Part::Mirroring] Part__Mirroring015  label="Cylinder107 (Mirror #1)011"
  Base = (0,0,0)
  Normal = (1,0,0)
  Source = -> Cylinder504
FEATURE [Part::MultiFuse] Fusion439
  Placement = pos=(0,0,0) rot=(0,0,1;1.25664rad)
  Refine = true
  Shapes = -> [Cylinder503,Part__Mirroring015]
FEATURE [Part::Cylinder] Cylinder509  label="Cylinder606"
  Angle = 360
  AttacherType = Attacher::AttachEngine3D
  Height = 8
  Placement = pos=(12,0,16) rot=(0,1,0;1.01229rad)
  Radius = 2.5
FEATURE [Part::MultiFuse] Fusion445
  Placement = pos=(0,0,0) rot=(0,0,1;0.628319rad)
  Refine = true
  Shapes = -> [Cylinder509,Part__Mirroring012]
FEATURE [Part::MultiFuse] Fusion020
  Placement = pos=(0,0,-6) rot=(0,0,1;0rad)
  Refine = true
  Shapes = -> [Fusion443,Fusion445,Fusion439,Fusion442,Fusion446]
FEATURE [Part::MultiFuse] Fusion021
  Placement = pos=(0,0,0) rot=(0,0,1;0.314159rad)
  Refine = true
  Shapes = -> [Cylinder092,Cylinder093]
FEATURE [Part::Cylinder] Cylinder510  label="Cylinder607"
  Angle = 360
  AttacherType = Attacher::AttachEngine3D
  Height = 10
  Placement = pos=(-12.5,0,13) rot=(0,0,1;0rad)
  Radius = 1.1
FEATURE [Part::MultiFuse] Fusion444
  Placement = pos=(0,0,0) rot=(0,0,1;1.5708rad)
  Refine = true
  Shapes = -> [Cylinder496,Cylinder510]
FEATURE [Part::Cylinder] Cylinder511  label="Cylinder608"
  Angle = 360
  AttacherType = Attacher::AttachEngine3D
  Height = 12
  Placement = pos=(0,0,10) rot=(0,0,1;0rad)
  Radius = 20.5
FEATURE [Part::Cylinder] Cylinder512  label="Cylinder609"
  Angle = 360
  AttacherType = Attacher::AttachEngine3D
  Height = 12
  Radius = 22
FEATURE [Part::Cut] Cut349
  Base = -> Cylinder497
  Placement = pos=(0,0,4.5) rot=(0,0,1;0rad)
  Refine = true
  Tool = -> Cylinder512
FEATURE [Part::Cylinder] Cylinder513  label="Cylinder610"
  Angle = 360
  AttacherType = Attacher::AttachEngine3D
  Height = 10
  Placement = pos=(12.5,0,13) rot=(0,0,1;0rad)
  Radius = 1.1
FEATURE [Part::Cylinder] Cylinder514  label="Cylinder611"
  Angle = 360
  AttacherType = Attacher::AttachEngine3D
  Height = 22
  Radius = 23.5
FEATURE [Part::Cut] Cut023
  Base = -> Cylinder514
  Refine = true
  Tool = -> Cut350
FEATURE [Part::MultiFuse] Fusion441
  Refine = true
  Shapes = -> [Cut349,Cut023]
FEATURE [Part::Cut] Cut348
  Base = -> Fusion441
  Refine = true
  Tool = -> Cylinder495
FEATURE [Part::MultiFuse] Fusion448
  Placement = pos=(0,0,0) rot=(0,0,1;0.942478rad)
  Refine = true
  Shapes = -> [Cylinder513,Cylinder493]
FEATURE [Part::Cut] Cut351
  Base = -> Cone002
  Refine = true
  Tool = -> Cylinder492
FEATURE [Part::Cylinder] Cylinder515
  Angle = 360
  AttacherType = Attacher::AttachEngine3D
  Height = 26
  Radius = 10.1
FEATURE [Part::Cut] Cut032
  Base = -> Cut348
  Refine = true
  Tool = -> Cylinder499
FEATURE [Part::Cut] Cut033
  Base = -> Cut032
  Refine = true
  Tool = -> Cylinder511
FEATURE [Part::Chamfer] Chamfer053
  Base = -> Cut033
  Edges = 1 edges r=1.49: [Edge21]
FEATURE [Part::Chamfer] Chamfer054
  Base = -> Chamfer053
  Edges = 1 edges r=2: [Edge3]
FEATURE [Part::Fillet] Fillet126
  Base = -> Chamfer054
  Edges = 2 edges r=1.5: [Edge5,Edge19]
FEATURE [Part::Cylinder] Cylinder516  label="Cylinder612"
  Angle = 360
  AttacherType = Attacher::AttachEngine3D
  Height = 6
  Placement = pos=(0,0,9) rot=(0,0,1;0rad)
  Radius = 15
FEATURE [Part::Cylinder] Cylinder517  label="Cylinder613"
  Angle = 360
  AttacherType = Attacher::AttachEngine3D
  Height = 1.5
  Placement = pos=(0,0,3) rot=(0,0,1;0rad)
  Radius = 7
FEATURE [Part::Cylinder] Cylinder518  label="Cylinder614"
  Angle = 360
  AttacherType = Attacher::AttachEngine3D
  Height = 4
  Placement = pos=(0,0,6.5) rot=(0,0,1;0rad)
  Radius = 5.6
FEATURE [Part::Cylinder] Cylinder519  label="Cylinder615"
  Angle = 360
  AttacherType = Attacher::AttachEngine3D
  Height = 10
  Placement = pos=(12.5,0,13) rot=(0,0,1;0rad)
  Radius = 1.1
FEATURE [Part::Cylinder] Cylinder520  label="Cylinder616"
  Angle = 360
  AttacherType = Attacher::AttachEngine3D
  Height = 10
  Placement = pos=(-12.5,0,13) rot=(0,0,1;0rad)
  Radius = 1.1
FEATURE [Part::MultiFuse] Fusion440
  Placement = pos=(0,0,0) rot=(0,0,1;2.82743rad)
  Refine = true
  Shapes = -> [Cylinder519,Cylinder520]
FEATURE [Part::MultiFuse] Fusion452
  Placement = pos=(0,0,-5) rot=(0,0,1;0rad)
  Refine = true
  Shapes = -> [Fusion021,Fusion448,Fusion440,Fusion447,Fusion444]
FEATURE [Part::Cone] Cone003
  Angle = 360
  AttacherType = Attacher::AttachEngine3D
  Height = 10
  Placement = pos=(0,0,9) rot=(0,0,1;0rad)
  Radius1 = 24
  Radius2 = 15
FEATURE [Part::Cut] Cut028
  Base = -> Cut351
  Placement = pos=(0,0,-5) rot=(0,0,1;0rad)
  Refine = true
  Tool = -> Cone003
FEATURE [Part::Cut] Cut029
  Base = -> Cut028
  Refine = true
  Tool = -> Fusion020
FEATURE [Part::Cut] Cut352
  Base = -> Cut029
  Refine = true
  Tool = -> Fusion452
FEATURE [Part::Cut] Cut353
  Base = -> Cut352
  Refine = true
  Tool = -> Cylinder515
FEATURE [Part::Fillet] Fillet003
  Base = -> Cut353
  Edges = 1 edges r=1.5: [Edge6]
FEATURE [Part::Cylinder] Cylinder521  label="Cylinder617"
  Angle = 360
  AttacherType = Attacher::AttachEngine3D
  Height = 4
  Radius = 5.6
FEATURE [Part::Cylinder] Cylinder522  label="Cylinder618"
  Angle = 360
  AttacherType = Attacher::AttachEngine3D
  Height = 4
  Placement = pos=(0,0,3) rot=(0,0,1;0rad)
  Radius = 3
FEATURE [Part::MultiFuse] Fusion453
  Placement = pos=(0,0,4.5) rot=(0,0,1;0rad)
  Refine = true
  Shapes = -> [Cylinder518,Cylinder522,Cylinder521]
FEATURE [Part::Cylinder] Cylinder523  label="Cylinder619"
  Angle = 360
  AttacherType = Attacher::AttachEngine3D
  Height = 20
  Placement = pos=(12.5,0,13) rot=(0,0,1;0rad)
  Radius = 0.8
FEATURE [Part::Cylinder] Cylinder524  label="Cylinder620"
  Angle = 360
  AttacherType = Attacher::AttachEngine3D
  Height = 20
  Placement = pos=(12.5,0,13) rot=(0,0,1;0rad)
  Radius = 0.8
FEATURE [Part::Cylinder] Cylinder525  label="Cylinder621"
  Angle = 360
  AttacherType = Attacher::AttachEngine3D
  Height = 20
  Placement = pos=(-12.5,0,13) rot=(0,0,1;0rad)
  Radius = 0.8
FEATURE [Part::MultiFuse] Fusion455
  Placement = pos=(0,0,0) rot=(0,0,1;1.5708rad)
  Refine = true
  Shapes = -> [Cylinder524,Cylinder525]
FEATURE [Part::Cylinder] Cylinder526  label="Cylinder622"
  Angle = 360
  AttacherType = Attacher::AttachEngine3D
  Height = 20
  Placement = pos=(12.5,0,13) rot=(0,0,1;0rad)
  Radius = 0.8
FEATURE [Part::Cylinder] Cylinder527  label="Cylinder623"
  Angle = 360
  AttacherType = Attacher::AttachEngine3D
  Height = 20
  Placement = pos=(-12.5,0,13) rot=(0,0,1;0rad)
  Radius = 0.8
FEATURE [Part::MultiFuse] Fusion450
  Placement = pos=(0,0,0) rot=(0,0,1;0.314159rad)
  Refine = true
  Shapes = -> [Cylinder523,Cylinder527]
FEATURE [Part::Cylinder] Cylinder528  label="Cylinder624"
  Angle = 360
  AttacherType = Attacher::AttachEngine3D
  Height = 6
  Placement = pos=(0,0,3) rot=(0,0,1;0rad)
  Radius = 10
FEATURE [Part::Cylinder] Cylinder529  label="Cylinder625"
  Angle = 360
  AttacherType = Attacher::AttachEngine3D
  Height = 20
  Placement = pos=(-12.5,0,13) rot=(0,0,1;0rad)
  Radius = 0.8
FEATURE [Part::MultiFuse] Fusion449
  Placement = pos=(0,0,0) rot=(0,0,1;0.942478rad)
  Refine = true
  Shapes = -> [Cylinder526,Cylinder529]
FEATURE [Part::Cylinder] Cylinder530  label="Cylinder626"
  Angle = 360
  AttacherType = Attacher::AttachEngine3D
  Height = 20
  Placement = pos=(12.5,0,13) rot=(0,0,1;0rad)
  Radius = 0.8
FEATURE [Part::Cylinder] Cylinder531  label="Cylinder627"
  Angle = 360
  AttacherType = Attacher::AttachEngine3D
  Height = 20
  Placement = pos=(-12.5,0,13) rot=(0,0,1;0rad)
  Radius = 0.8
FEATURE [Part::MultiFuse] Fusion451
  Placement = pos=(0,0,0) rot=(0,0,1;2.82743rad)
  Refine = true
  Shapes = -> [Cylinder530,Cylinder531]
FEATURE [Part::Cylinder] Cylinder532  label="Cylinder628"
  Angle = 360
  AttacherType = Attacher::AttachEngine3D
  Height = 20
  Placement = pos=(12.5,0,13) rot=(0,0,1;0rad)
  Radius = 0.8
FEATURE [Part::Cylinder] Cylinder533
  Angle = 360
  AttacherType = Attacher::AttachEngine3D
  Height = 20
  Placement = pos=(-12.5,0,13) rot=(0,0,1;0rad)
  Radius = 0.8
FEATURE [Part::MultiFuse] Fusion454
  Placement = pos=(0,0,0) rot=(0,0,1;2.19911rad)
  Refine = true
  Shapes = -> [Cylinder532,Cylinder533]
FEATURE [Part::MultiFuse] Fusion036
  Placement = pos=(0,0,3) rot=(0,0,1;0rad)
  Refine = true
  Shapes = -> [Fusion450,Fusion449,Fusion451,Fusion454,Fusion455]
FEATURE [Part::MultiFuse] Fusion456
  Refine = true
  Shapes = -> [Cylinder516,Cylinder528]
FEATURE [Part::Cut] Cut354
  Base = -> Fusion456
  Refine = true
  Tool = -> Cylinder517
FEATURE [Part::Cut] Cut034
  Base = -> Cut354
  Placement = pos=(0,0,8) rot=(0,0,1;0rad)
  Refine = true
  Tool = -> Fusion453
FEATURE [Part::Cut] Cut035
  Base = -> Cut034
  Refine = true
  Tool = -> Fusion036
FEATURE [Part::Cylinder] Cylinder534  label="Cylinder629"
  Angle = 360
  AttacherType = Attacher::AttachEngine3D
  Height = 3
  Placement = pos=(0,0,11) rot=(0,0,1;0rad)
  Radius = 10
FEATURE [Part::Cylinder] Cylinder535  label="Cylinder630"
  Angle = 360
  AttacherType = Attacher::AttachEngine3D
  Height = 3
  Placement = pos=(0,0,11) rot=(0,0,1;0rad)
  Radius = 8.5
FEATURE [Part::Cut] Cut355
  Base = -> Cylinder534
  Refine = true
  Tool = -> Cylinder535
FEATURE [Part::Cut] Cut356
  Base = -> Cut035
  Refine = true
  Tool = -> Cut355
FEATURE [Part::Chamfer] Chamfer055  label="hub-wide"
  Base = -> Cut356
  Edges = 1 edges r=1: [Edge1]
FEATURE [Part::Cylinder] Cylinder536  label="Cylinder631"
  Angle = 360
  AttacherType = Attacher::AttachEngine3D
  Height = 3
  Placement = pos=(0,0,11) rot=(0,0,1;0rad)
  Radius = 10
FEATURE [Part::Cylinder] Cylinder537  label="Cylinder632"
  Angle = 360
  AttacherType = Attacher::AttachEngine3D
  Height = 4
  Placement = pos=(0,0,10) rot=(0,0,1;0rad)
  Radius = 8.55
FEATURE [Part::Cone] Cone
  Angle = 360
  AttacherType = Attacher::AttachEngine3D
  Height = 8
  Placement = pos=(0,0,3) rot=(0,0,1;0rad)
  Radius1 = 6
  Radius2 = 10
FEATURE [Part::MultiFuse] Fusion457
  Refine = true
  Shapes = -> [Cone,Cylinder536]
FEATURE [Part::Cylinder] Cylinder538  label="Cylinder633"
  Angle = 360
  AttacherType = Attacher::AttachEngine3D
  Height = 1.6
  Placement = pos=(0,0,10) rot=(0,0,1;0rad)
  Radius = 21
FEATURE [Part::Cylinder] Cylinder539  label="Cylinder634"
  Angle = 360
  AttacherType = Attacher::AttachEngine3D
  Height = 1.6
  Placement = pos=(0,0,10) rot=(0,0,1;0rad)
  Radius = 19.5
FEATURE [Part::Cut] Cut357
  Base = -> Cylinder538
  Refine = true
  Tool = -> Cylinder539
FEATURE [Part::MultiFuse] Fusion458
  Refine = true
  Shapes = -> [Fillet003,Cut357]
FEATURE [Part::Fillet] Fillet127
  Base = -> Fusion458
  Edges = 1 edges r=1: [Edge7]
FEATURE [Part::MultiFuse] Fusion459
  Refine = true
  Shapes = -> [Fillet126,Fillet127]
FEATURE [Part::Fillet] Fillet128  label="rim-wide"
  Base = -> Fusion459
  Edges = 1 edges r=0.5: [Edge215]
FEATURE [Part::Cone] Cone004
  Angle = 360
  AttacherType = Attacher::AttachEngine3D
  Height = 6
  Placement = pos=(0,0,4) rot=(0,0,1;0rad)
  Radius1 = 5
  Radius2 = 8.5
FEATURE [Part::MultiFuse] Fusion460
  Refine = true
  Shapes = -> [Cone004,Cylinder537]
FEATURE [Part::Cut] Cut358
  Base = -> Fusion457
  Refine = true
  Tool = -> Fusion460
FEATURE [Part::Fillet] Fillet129  label="hub-wide-cap"
  Base = -> Cut358
  Edges = 2 edges r=1: [Edge1,Edge3]
FEATURE [Part::Compound] Compound  label="rim-left-front-wide"
  Links = -> [Chamfer055,Fillet128,Fillet129]
  Placement = pos=(450,-56,-47) rot=(1,0,0;-1.5708rad)
FEATURE [Part::Cylinder] Cylinder540  label="Cylinder635"
  Angle = 360
  AttacherType = Attacher::AttachEngine3D
  Height = 15
  Placement = pos=(13.5,49.5,13) rot=(0,0,1;0rad)
  Radius = 1.75
FEATURE [Part::Cylinder] Cylinder541  label="Cylinder636"
  Angle = 360
  AttacherType = Attacher::AttachEngine3D
  Height = 15
  Placement = pos=(13.5,-49.5,13) rot=(0,0,1;0rad)
  Radius = 1.75
FEATURE [Part::MultiFuse] Fusion461
  Refine = true
  Shapes = -> [Cylinder540,Cylinder541]
FEATURE [Part::Cylinder] Cylinder542  label="Cylinder637"
  Angle = 360
  AttacherType = Attacher::AttachEngine3D
  Height = 15
  Placement = pos=(13.5,-49.5,13) rot=(0,0,1;0rad)
  Radius = 1.75
FEATURE [Part::Cylinder] Cylinder543  label="Cylinder638"
  Angle = 360
  AttacherType = Attacher::AttachEngine3D
  Height = 15
  Placement = pos=(13.5,49.5,13) rot=(0,0,1;0rad)
  Radius = 1.75
FEATURE [Part::MultiFuse] Fusion462
  Placement = pos=(-12,0,0) rot=(0,0,1;0rad)
  Refine = true
  Shapes = -> [Cylinder543,Cylinder542]
FEATURE [Part::MultiFuse] Fusion463
  Placement = pos=(-7.5,0,-20.5) rot=(0,0,1;0rad)
  Refine = true
  Shapes = -> [Fusion462,Fusion461]
FEATURE [Part::Cylinder] Cylinder142
  Angle = 360
  AttacherType = Attacher::AttachEngine3D
  Height = 128
  Placement = pos=(0,-64,0) rot=(-1,0,0;1.5708rad)
  Radius = 8
FEATURE [Part::Box] Box339  label="Cube410"
  AttacherType = Attacher::AttachEngine3D
  Height = 15
  Length = 20
  Placement = pos=(-10,-53.5,-7.5) rot=(0,0,1;0rad)
  Width = 8
FEATURE [Part::Fillet] Fillet130
  Base = -> Box339
  Edges = 4 edges r=3: [Edge1,Edge3,Edge5,Edge7]
  Placement = pos=(0,99,0) rot=(0,0,1;0rad)
FEATURE [Part::Box] Box340  label="Cube411"
  AttacherType = Attacher::AttachEngine3D
  Height = 15
  Length = 20
  Placement = pos=(-10,-53.5,-7.5) rot=(0,0,1;0rad)
  Width = 8
FEATURE [Part::Fillet] Fillet131
  Base = -> Box340
  Edges = 4 edges r=3: [Edge1,Edge3,Edge5,Edge7]
FEATURE [Part::Cylinder] Cylinder544  label="Cylinder639"
  Angle = 360
  AttacherType = Attacher::AttachEngine3D
  Height = 128
  Placement = pos=(0,-64,0) rot=(-1,0,0;1.5708rad)
  Radius = 2.55
FEATURE [Part::Cylinder] Cylinder545  label="Cylinder640"
  Angle = 360
  AttacherType = Attacher::AttachEngine3D
  Height = 4
  Placement = pos=(0,-64,0) rot=(-1,0,0;1.5708rad)
  Radius = 5.6
FEATURE [Part::Cylinder] Cylinder546  label="Cylinder641"
  Angle = 360
  AttacherType = Attacher::AttachEngine3D
  Height = 4
  Placement = pos=(0,60,0) rot=(-1,0,0;1.5708rad)
  Radius = 5.6
FEATURE [Part::MultiFuse] Fusion124
  Refine = true
  Shapes = -> [Cylinder546,Cylinder545]
FEATURE [Part::MultiFuse] Fusion464
  Refine = true
  Shapes = -> [Cylinder544,Fusion124]
FEATURE [Part::MultiFuse] Fusion126
  Refine = true
  Shapes = -> [Cylinder142,Fillet131,Fillet130]
FEATURE [Part::Box] Box341  label="Cube412"
  AttacherType = Attacher::AttachEngine3D
  Height = 1
  Length = 20
  Placement = pos=(-10,-64,-8.5) rot=(0,0,1;0rad)
  Width = 128
FEATURE [Part::Box] Box342  label="Cube413"
  AttacherType = Attacher::AttachEngine3D
  Height = 1
  Length = 20
  Placement = pos=(-10,-64,7.5) rot=(0,0,1;0rad)
  Width = 128
FEATURE [Part::MultiFuse] Fusion127
  Refine = true
  Shapes = -> [Box341,Box342]
FEATURE [Part::Cylinder] Cylinder547  label="Cylinder642"
  Angle = 360
  AttacherType = Attacher::AttachEngine3D
  Height = 6
  Placement = pos=(0,0,-7.5) rot=(0,0,1;0rad)
  Radius = 1.5
FEATURE [Part::Cylinder] Cylinder149
  Angle = 360
  AttacherType = Attacher::AttachEngine3D
  Height = 25
  Placement = pos=(0,-30,0) rot=(-1,0,0;1.5708rad)
  Radius = 2.8
FEATURE [Part::Cylinder] Cylinder150
  Angle = 360
  AttacherType = Attacher::AttachEngine3D
  Height = 25
  Placement = pos=(0,5,0) rot=(-1,0,0;1.5708rad)
  Radius = 2.8
FEATURE [Part::MultiFuse] Fusion465
  Refine = true
  Shapes = -> [Cylinder150,Cylinder149]
FEATURE [Part::Box] Box343  label="Cube414"
  AttacherType = Attacher::AttachEngine3D
  Height = 15
  Length = 5.5
  Placement = pos=(2.5,-30,-7.5) rot=(0,0,1;0rad)
  Width = 6
FEATURE [Part::Box] Box344  label="Cube415"
  AttacherType = Attacher::AttachEngine3D
  Height = 15
  Length = 5.5
  Placement = pos=(2.5,24,-7.5) rot=(0,0,1;0rad)
  Width = 6
FEATURE [Part::MultiFuse] Fusion466
  Refine = true
  Shapes = -> [Box344,Box343]
FEATURE [Part::Fillet] Fillet132
  Base = -> Fusion466
  Edges = 8 edges r=2: [Edge9,Edge10,Edge11,Edge12,Edge21,Edge22,Edge23,Edge24]
FEATURE [Part::MultiFuse] Fusion467
  Refine = true
  Shapes = -> [Fusion126,Fillet132]
FEATURE [Part::Cylinder] Cylinder151
  Angle = 360
  AttacherType = Attacher::AttachEngine3D
  Height = 10
  Placement = pos=(0,-27,4.5) rot=(0,1,0;1.5708rad)
  Radius = 1.25
FEATURE [Part::Cylinder] Cylinder548  label="Cylinder643"
  Angle = 360
  AttacherType = Attacher::AttachEngine3D
  Height = 10
  Placement = pos=(0,-27,-4.5) rot=(0,1,0;1.5708rad)
  Radius = 1.25
FEATURE [Part::MultiFuse] Fusion468
  Refine = true
  Shapes = -> [Cylinder548,Cylinder151]
FEATURE [Part::Cylinder] Cylinder549  label="Cylinder644"
  Angle = 360
  AttacherType = Attacher::AttachEngine3D
  Height = 10
  Placement = pos=(0,-27,4.5) rot=(0,1,0;1.5708rad)
  Radius = 1.25
FEATURE [Part::Cylinder] Cylinder550  label="Cylinder645"
  Angle = 360
  AttacherType = Attacher::AttachEngine3D
  Height = 10
  Placement = pos=(0,-27,-4.5) rot=(0,1,0;1.5708rad)
  Radius = 1.25
FEATURE [Part::MultiFuse] Fusion469
  Placement = pos=(0,54,0) rot=(0,0,1;0rad)
  Refine = true
  Shapes = -> [Cylinder550,Cylinder549]
FEATURE [Part::MultiFuse] Fusion470
  Placement = pos=(-2,0,0) rot=(0,0,1;0rad)
  Refine = true
  Shapes = -> [Fusion469,Fusion468]
FEATURE [Part::Cut] Cut359
  Base = -> Fusion467
  Refine = true
  Tool = -> Fusion464
FEATURE [Part::Cut] Cut360
  Base = -> Cut359
  Refine = true
  Tool = -> Fusion470
FEATURE [Part::Cut] Cut047
  Base = -> Cut360
  Refine = true
  Tool = -> Fusion463
FEATURE [Part::Cut] Cut048
  Base = -> Cut047
  Refine = true
  Tool = -> Fusion465
FEATURE [Part::Cut] Cut049
  Base = -> Cut048
  Refine = true
  Tool = -> Fusion127
FEATURE [Part::Cut] Cut050  label="axle-front-wide"
  Base = -> Cut049
  Placement = pos=(450,31,-47) rot=(0,0,1;0rad)
  Refine = true
  Tool = -> Cylinder547
FEATURE [Part::Cylinder] Cylinder551  label="Cylinder646"
  Angle = 360
  AttacherType = Attacher::AttachEngine3D
  Height = 15
  Placement = pos=(13.5,-49.5,13) rot=(0,0,1;0rad)
  Radius = 1.75
FEATURE [Part::Cylinder] Cylinder552  label="Cylinder647"
  Angle = 360
  AttacherType = Attacher::AttachEngine3D
  Height = 15
  Placement = pos=(13.5,49.5,13) rot=(0,0,1;0rad)
  Radius = 1.75
FEATURE [Part::MultiFuse] Fusion471
  Placement = pos=(-12,0,0) rot=(0,0,1;0rad)
  Refine = true
  Shapes = -> [Cylinder552,Cylinder551]
FEATURE [Part::Cylinder] Cylinder553  label="Cylinder648"
  Angle = 360
  AttacherType = Attacher::AttachEngine3D
  Height = 128
  Placement = pos=(0,-64,0) rot=(-1,0,0;1.5708rad)
  Radius = 8
FEATURE [Part::Box] Box345  label="Cube416"
  AttacherType = Attacher::AttachEngine3D
  Height = 15
  Length = 20
  Placement = pos=(-10,-53.5,-7.5) rot=(0,0,1;0rad)
  Width = 8
FEATURE [Part::Fillet] Fillet133
  Base = -> Box345
  Edges = 4 edges r=3: [Edge1,Edge3,Edge5,Edge7]
  Placement = pos=(0,99,0) rot=(0,0,1;0rad)
FEATURE [Part::Box] Box346  label="Cube417"
  AttacherType = Attacher::AttachEngine3D
  Height = 15
  Length = 20
  Placement = pos=(-10,-53.5,-7.5) rot=(0,0,1;0rad)
  Width = 8
FEATURE [Part::Fillet] Fillet134
  Base = -> Box346
  Edges = 4 edges r=3: [Edge1,Edge3,Edge5,Edge7]
FEATURE [Part::Cylinder] Cylinder554  label="Cylinder649"
  Angle = 360
  AttacherType = Attacher::AttachEngine3D
  Height = 128
  Placement = pos=(0,-64,0) rot=(-1,0,0;1.5708rad)
  Radius = 2.55
FEATURE [Part::Cylinder] Cylinder555  label="Cylinder650"
  Angle = 360
  AttacherType = Attacher::AttachEngine3D
  Height = 4
  Placement = pos=(0,-64,0) rot=(-1,0,0;1.5708rad)
  Radius = 5.6
FEATURE [Part::Cylinder] Cylinder556  label="Cylinder651"
  Angle = 360
  AttacherType = Attacher::AttachEngine3D
  Height = 25
  Placement = pos=(0,-30,0) rot=(-1,0,0;1.5708rad)
  Radius = 2.8
FEATURE [Part::Cylinder] Cylinder557  label="Cylinder652"
  Angle = 360
  AttacherType = Attacher::AttachEngine3D
  Height = 25
  Placement = pos=(0,5,0) rot=(-1,0,0;1.5708rad)
  Radius = 2.8
FEATURE [Part::MultiFuse] Fusion473
  Refine = true
  Shapes = -> [Cylinder557,Cylinder556]
FEATURE [Part::Box] Box347  label="Cube418"
  AttacherType = Attacher::AttachEngine3D
  Height = 15
  Length = 5.5
  Placement = pos=(2.5,-30,-7.5) rot=(0,0,1;0rad)
  Width = 6
FEATURE [Part::Box] Box348  label="Cube419"
  AttacherType = Attacher::AttachEngine3D
  Height = 15
  Length = 5.5
  Placement = pos=(2.5,24,-7.5) rot=(0,0,1;0rad)
  Width = 6
FEATURE [Part::MultiFuse] Fusion474
  Refine = true
  Shapes = -> [Box348,Box347]
FEATURE [Part::Fillet] Fillet135
  Base = -> Fusion474
  Edges = 8 edges r=2: [Edge9,Edge10,Edge11,Edge12,Edge21,Edge22,Edge23,Edge24]
FEATURE [Part::Cylinder] Cylinder558  label="Cylinder653"
  Angle = 360
  AttacherType = Attacher::AttachEngine3D
  Height = 10
  Placement = pos=(0,-27,4.5) rot=(0,1,0;1.5708rad)
  Radius = 1.25
FEATURE [Part::Cylinder] Cylinder559  label="Cylinder654"
  Angle = 360
  AttacherType = Attacher::AttachEngine3D
  Height = 10
  Placement = pos=(0,-27,-4.5) rot=(0,1,0;1.5708rad)
  Radius = 1.25
FEATURE [Part::MultiFuse] Fusion476
  Refine = true
  Shapes = -> [Cylinder559,Cylinder558]
FEATURE [Part::Cylinder] Cylinder560  label="Cylinder655"
  Angle = 360
  AttacherType = Attacher::AttachEngine3D
  Height = 10
  Placement = pos=(0,-27,4.5) rot=(0,1,0;1.5708rad)
  Radius = 1.25
FEATURE [Part::Cylinder] Cylinder561  label="Cylinder656"
  Angle = 360
  AttacherType = Attacher::AttachEngine3D
  Height = 10
  Placement = pos=(0,-27,-4.5) rot=(0,1,0;1.5708rad)
  Radius = 1.25
FEATURE [Part::MultiFuse] Fusion477
  Placement = pos=(0,54,0) rot=(0,0,1;0rad)
  Refine = true
  Shapes = -> [Cylinder561,Cylinder560]
FEATURE [Part::MultiFuse] Fusion478
  Placement = pos=(-2,0,0) rot=(0,0,1;0rad)
  Refine = true
  Shapes = -> [Fusion477,Fusion476]
FEATURE [Part::Cylinder] Cylinder562  label="Cylinder657"
  Angle = 360
  AttacherType = Attacher::AttachEngine3D
  Height = 4
  Placement = pos=(0,60,0) rot=(-1,0,0;1.5708rad)
  Radius = 5.6
FEATURE [Part::MultiFuse] Fusion479
  Refine = true
  Shapes = -> [Cylinder562,Cylinder555]
FEATURE [Part::MultiFuse] Fusion480
  Refine = true
  Shapes = -> [Cylinder554,Fusion479]
FEATURE [Part::MultiFuse] Fusion481
  Refine = true
  Shapes = -> [Cylinder553,Fillet134,Fillet133]
FEATURE [Part::MultiFuse] Fusion475
  Refine = true
  Shapes = -> [Fusion481,Fillet135]
FEATURE [Part::Cut] Cut361
  Base = -> Fusion475
  Refine = true
  Tool = -> Fusion480
FEATURE [Part::Cut] Cut362
  Base = -> Cut361
  Refine = true
  Tool = -> Fusion478
FEATURE [Part::Box] Box349  label="Cube420"
  AttacherType = Attacher::AttachEngine3D
  Height = 1
  Length = 20
  Placement = pos=(-10,-64,-8.5) rot=(0,0,1;0rad)
  Width = 128
FEATURE [Part::Box] Box350  label="Cube421"
  AttacherType = Attacher::AttachEngine3D
  Height = 1
  Length = 20
  Placement = pos=(-10,-64,7.5) rot=(0,0,1;0rad)
  Width = 128
FEATURE [Part::MultiFuse] Fusion482
  Refine = true
  Shapes = -> [Box349,Box350]
FEATURE [Part::Cylinder] Cylinder563  label="Cylinder658"
  Angle = 360
  AttacherType = Attacher::AttachEngine3D
  Height = 6
  Placement = pos=(0,0,-7.5) rot=(0,0,1;0rad)
  Radius = 1.5
FEATURE [Part::Cylinder] Cylinder564  label="Cylinder659"
  Angle = 360
  AttacherType = Attacher::AttachEngine3D
  Height = 15
  Placement = pos=(13.5,49.5,13) rot=(0,0,1;0rad)
  Radius = 1.75
FEATURE [Part::Cylinder] Cylinder565  label="Cylinder660"
  Angle = 360
  AttacherType = Attacher::AttachEngine3D
  Height = 15
  Placement = pos=(13.5,-49.5,13) rot=(0,0,1;0rad)
  Radius = 1.75
FEATURE [Part::MultiFuse] Fusion483
  Refine = true
  Shapes = -> [Cylinder564,Cylinder565]
FEATURE [Part::MultiFuse] Fusion472
  Placement = pos=(-7.5,0,-20.5) rot=(0,0,1;0rad)
  Refine = true
  Shapes = -> [Fusion471,Fusion483]
FEATURE [Part::Cut] Cut363
  Base = -> Cut362
  Refine = true
  Tool = -> Fusion472
FEATURE [Part::Cut] Cut364
  Base = -> Cut363
  Refine = true
  Tool = -> Fusion473
FEATURE [Part::Cut] Cut365
  Base = -> Cut364
  Refine = true
  Tool = -> Fusion482
FEATURE [Part::Cut] Cut366  label="axle-rear-wide"
  Base = -> Cut365
  Placement = pos=(555,31,-41.5) rot=(0,0,1;0rad)
  Refine = true
  Tool = -> Cylinder563
FEATURE [Part::Feature] Part__Mirroring016001  label="rim-right-front-wide"
  Placement = pos=(0,62,0) rot=(0,0,1;0rad)
  shape: bbox 51.28 x 23 x 51.28 mm, 141 faces, 3 solids (baked)
FEATURE [Part::Feature] Compound001  label="rim-left-rear-wide"
  Placement = pos=(555,-56,-41.5) rot=(-1,0,0;1.5708rad)
  shape: bbox 51.28 x 23 x 51.28 mm, 141 faces, 3 solids (baked)
FEATURE [Part::Feature] Part__Mirroring016001001  label="rim-right-rear-wide"
  Placement = pos=(105,62,5.5) rot=(0,0,1;0rad)
  shape: bbox 51.28 x 23 x 51.28 mm, 141 faces, 3 solids (baked)
FEATURE [Part::Feature] Fillet010001  label="wheel-left-front-wide"
  Placement = pos=(450,-30,-47) rot=(0,0,1;0rad)
  shape: bbox 93.09 x 28 x 93.09 mm, 10 faces (baked)
FEATURE [Part::Feature] Fillet010002  label="wheel-left-rear-wide"
  Placement = pos=(555,-30,-41.5) rot=(0,0,1;0rad)
  shape: bbox 93.09 x 28 x 93.09 mm, 10 faces (baked)
FEATURE [Part::Feature] Fillet010003  label="wheel-right-rear-wide"
  Placement = pos=(555,120,-41.5) rot=(0,0,1;0rad)
  shape: bbox 93.09 x 28 x 93.09 mm, 10 faces (baked)
FEATURE [Part::Feature] Fillet010004  label="wheel-right-front-wide"
  Placement = pos=(450,120,-47) rot=(0,0,1;0rad)
  shape: bbox 93.09 x 28 x 93.09 mm, 10 faces (baked)
FEATURE [App::DocumentObjectGroup] Group007  label="Axles"
  Group = -> [Part__Mirroring016001,Compound001,Part__Mirroring016001001,Fillet010001,Fillet010002,Fillet010003,Fillet010004,Cut050,Cut366,Compound]
FEATURE [Part::Box] Box351
  AttacherType = Attacher::AttachEngine3D
  Height = 2
  Length = 560
  Placement = pos=(0,106,16) rot=(1,0,0;1.09956rad)
  Width = 31
FEATURE [Part::Box] Box352
  AttacherType = Attacher::AttachEngine3D
  Height = 2
  Length = 560
  Placement = pos=(0,120,44) rot=(1,0,0;1.5708rad)
  Width = 60
FEATURE [Part::Box] Box353
  AttacherType = Attacher::AttachEngine3D
  Height = 2
  Length = 560
  Placement = pos=(0,120,44) rot=(1,0,0;1.5708rad)
  Width = 60
FEATURE [Part::Box] Box354
  AttacherType = Attacher::AttachEngine3D
  Height = 2
  Length = 560
  Placement = pos=(0,106,16) rot=(1,0,0;1.09956rad)
  Width = 31
FEATURE [Part::Box] Box355
  AttacherType = Attacher::AttachEngine3D
  Height = 2
  Length = 560
  Placement = pos=(0,80,0) rot=(1,0,0;0.541051rad)
  Width = 30
FEATURE [Part::Box] Box356  label="Cube422"
  AttacherType = Attacher::AttachEngine3D
  Height = 120
  Length = 25
  Placement = pos=(550,-41,0) rot=(0,-1,0;0.261799rad)
  Width = 162
FEATURE [Part::Feature] Face001
  Placement = pos=(0,0,0) rot=(0,-1,0;0.261799rad)
  shape: bbox 37.01 x 198 x 138.1 mm, 1 faces, 0 solids (baked)
FEATURE [Part::Extrusion] Extrude001
  Base = -> Face001
  Dir = (50,0,0)
  DirMode = 0
  FaceMakerClass = Part::FaceMakerExtrusion
  LengthFwd = 0
  LengthRev = 0
  Placement = pos=(-23,0,0) rot=(0,0,1;0rad)
  Solid = false
  Symmetric = false
FEATURE [Part::Feature] Face002
  Placement = pos=(25,0,6.8) rot=(0,-1,0;0.261799rad)
  shape: bbox 28.9 x 171.6 x 107.8 mm, 1 faces, 0 solids (baked)
FEATURE [Part::Extrusion] Extrude002
  Base = -> Face002
  Dir = (10,0,0)
  DirMode = 0
  FaceMakerClass = Part::FaceMakerExtrusion
  LengthFwd = 0
  LengthRev = 0
  Solid = false
  Symmetric = false
FEATURE [Part::Box] Box357
  AttacherType = Attacher::AttachEngine3D
  Height = 2
  Length = 560
  Width = 80
FEATURE [Part::Box] Box358
  AttacherType = Attacher::AttachEngine3D
  Height = 2
  Length = 560
  Placement = pos=(0,80,0) rot=(1,0,0;0.541051rad)
  Width = 30
FEATURE [Part::Box] Box359
  AttacherType = Attacher::AttachEngine3D
  Height = 10
  Length = 517
  Placement = pos=(26.9,0,-10) rot=(0,0,1;0rad)
  Width = 10
FEATURE [Part::Box] Box009
  AttacherType = Attacher::AttachEngine3D
  Height = 45
  Length = 12
  Placement = pos=(25,0,-10) rot=(0,-1,0;0.401426rad)
  Width = 10
FEATURE [Part::Box] Box360
  AttacherType = Attacher::AttachEngine3D
  Height = 67
  Length = 20
  Placement = pos=(8,0,30) rot=(0,-1,0;0.401426rad)
  Width = 10
FEATURE [Part::MultiFuse] Fusion004
  Refine = true
  Shapes = -> [Box009,Box360]
FEATURE [Part::Box] Box361
  AttacherType = Attacher::AttachEngine3D
  Height = 10
  Length = 517
  Placement = pos=(26.9,70,-10) rot=(0,0,1;0rad)
  Width = 10
FEATURE [Part::Box] Box362
  AttacherType = Attacher::AttachEngine3D
  Height = 67
  Length = 20
  Placement = pos=(8,0,30) rot=(0,-1,0;0.401426rad)
  Width = 10
FEATURE [Part::Box] Box363
  AttacherType = Attacher::AttachEngine3D
  Height = 45
  Length = 12
  Placement = pos=(25,0,-10) rot=(0,-1,0;0.401426rad)
  Width = 10
FEATURE [Part::MultiFuse] Fusion006
  Placement = pos=(0,70,0) rot=(0,0,1;0rad)
  Refine = true
  Shapes = -> [Box363,Box362]
FEATURE [Part::MultiFuse] Fusion484
  Refine = true
  Shapes = -> [Fusion004,Fusion006]
FEATURE [Part::Box] Box364
  AttacherType = Attacher::AttachEngine3D
  Height = 15
  Length = 25
  Placement = pos=(-22.3,-38,90) rot=(0,0,1;0rad)
  Width = 156
FEATURE [Part::MultiFuse] Fusion485
  Refine = true
  Shapes = -> [Extrude002,Fusion484]
FEATURE [Part::Cut] Cut004
  Base = -> Fusion485
  Refine = true
  Tool = -> Box364
FEATURE [Part::Box] Box365
  AttacherType = Attacher::AttachEngine3D
  Height = 10
  Length = 10
  Placement = pos=(25,0,-10) rot=(0,0,1;0rad)
  Width = 10
FEATURE [Part::Box] Box366
  AttacherType = Attacher::AttachEngine3D
  Height = 10
  Length = 10
  Placement = pos=(25,70,-10) rot=(0,0,1;0rad)
  Width = 10
FEATURE [Part::MultiFuse] Fusion486
  Refine = true
  Shapes = -> [Cut004,Box365,Box366]
FEATURE [Part::Box] Box367
  AttacherType = Attacher::AttachEngine3D
  Height = 12.2
  Length = 10
  Placement = pos=(26.2,0,-10) rot=(0,0,1;0rad)
  Width = 10
FEATURE [Part::Box] Box368
  AttacherType = Attacher::AttachEngine3D
  Height = 12.2
  Length = 10
  Placement = pos=(26.2,70,-10) rot=(0,0,1;0rad)
  Width = 10
FEATURE [Part::MultiFuse] Fusion487
  Refine = true
  Shapes = -> [Box368,Box367]
FEATURE [Part::Cut] Cut005
  Base = -> Fusion486
  Refine = true
  Tool = -> Fusion487
FEATURE [Part::Cylinder] Cylinder566  label="Cylinder661"
  Angle = 360
  AttacherType = Attacher::AttachEngine3D
  Height = 10
  Placement = pos=(-7,5,80) rot=(0,0,1;0rad)
  Radius = 1.25
FEATURE [Part::Cylinder] Cylinder567  label="Cylinder662"
  Angle = 360
  AttacherType = Attacher::AttachEngine3D
  Height = 10
  Placement = pos=(-7,75,80) rot=(0,0,1;0rad)
  Radius = 1.25
FEATURE [Part::MultiFuse] Fusion488
  Refine = true
  Shapes = -> [Cylinder566,Cylinder567]
FEATURE [Part::Cylinder] Cylinder568  label="Cylinder663"
  Angle = 360
  AttacherType = Attacher::AttachEngine3D
  Height = 10
  Placement = pos=(2,-20,97) rot=(0,1,0;1.5708rad)
  Radius = 1.6
FEATURE [Part::Cut] Cut367
  Base = -> Cut005
  Refine = true
  Tool = -> Fusion488
FEATURE [Part::Cylinder] Cylinder569  label="Cylinder664"
  Angle = 360
  AttacherType = Attacher::AttachEngine3D
  Height = 10
  Placement = pos=(2,40,97) rot=(0,1,0;1.5708rad)
  Radius = 1.6
FEATURE [Part::Cylinder] Cylinder570  label="Cylinder665"
  Angle = 360
  AttacherType = Attacher::AttachEngine3D
  Height = 10
  Placement = pos=(2,100,97) rot=(0,1,0;1.5708rad)
  Radius = 1.6
FEATURE [Part::Cylinder] Cylinder571  label="Cylinder666"
  Angle = 360
  AttacherType = Attacher::AttachEngine3D
  Height = 3
  Placement = pos=(2,-20,97) rot=(0,1,0;1.5708rad)
  Radius = 3.1
FEATURE [Part::Cylinder] Cylinder572  label="Cylinder667"
  Angle = 360
  AttacherType = Attacher::AttachEngine3D
  Height = 3
  Placement = pos=(2,40,97) rot=(0,1,0;1.5708rad)
  Radius = 3.1
FEATURE [Part::Cylinder] Cylinder573  label="Cylinder668"
  Angle = 360
  AttacherType = Attacher::AttachEngine3D
  Height = 3
  Placement = pos=(2,100,97) rot=(0,1,0;1.5708rad)
  Radius = 3.1
FEATURE [Part::MultiFuse] Fusion489
  Placement = pos=(-1,0,-2) rot=(0,0,1;0rad)
  Refine = true
  Shapes = -> [Cylinder568,Cylinder569,Cylinder570]
FEATURE [Part::MultiFuse] Fusion490
  Placement = pos=(8,0,-2) rot=(0,0,1;0rad)
  Refine = true
  Shapes = -> [Cylinder571,Cylinder573,Cylinder572]
FEATURE [Part::MultiFuse] Fusion491
  Placement = pos=(-0.8,0,0) rot=(0,0,1;0rad)
  Refine = true
  Shapes = -> [Fusion489,Fusion490]
FEATURE [Part::Cut] Cut368
  Base = -> Cut367
  Refine = true
  Tool = -> Fusion491
FEATURE [Part::Cylinder] Cylinder574  label="Cylinder669"
  Angle = 360
  AttacherType = Attacher::AttachEngine3D
  Height = 10
  Placement = pos=(7,118,95) rot=(1,0,0;1.5708rad)
  Radius = 1.25
FEATURE [Part::Cylinder] Cylinder575  label="Cylinder670"
  Angle = 360
  AttacherType = Attacher::AttachEngine3D
  Height = 10
  Placement = pos=(7,-28,95) rot=(1,0,0;1.5708rad)
  Radius = 1.25
FEATURE [Part::Cylinder] Cylinder576  label="Cylinder671"
  Angle = 360
  AttacherType = Attacher::AttachEngine3D
  Height = 10
  Placement = pos=(19,118,49) rot=(1,0,0;1.5708rad)
  Radius = 1.25
FEATURE [Part::Cylinder] Cylinder577  label="Cylinder672"
  Angle = 360
  AttacherType = Attacher::AttachEngine3D
  Height = 10
  Placement = pos=(19,-28,49) rot=(1,0,0;1.5708rad)
  Radius = 1.25
FEATURE [Part::Cylinder] Cylinder578  label="Cylinder673"
  Angle = 360
  AttacherType = Attacher::AttachEngine3D
  Height = 10
  Placement = pos=(26.5,-17,25) rot=(1,0,0;2.02458rad)
  Radius = 1.25
FEATURE [Part::Cylinder] Cylinder579  label="Cylinder674"
  Angle = 360
  AttacherType = Attacher::AttachEngine3D
  Height = 10
  Placement = pos=(22,-26,42) rot=(1,0,0;2.02458rad)
  Radius = 1.25
FEATURE [Part::MultiFuse] Fusion492
  Refine = true
  Shapes = -> [Cylinder579,Cylinder578]
FEATURE [Part::Cylinder] Cylinder580  label="Cylinder675"
  Angle = 360
  AttacherType = Attacher::AttachEngine3D
  Height = 10
  Placement = pos=(22,-26,42) rot=(1,0,0;2.02458rad)
  Radius = 1.25
FEATURE [Part::Cylinder] Cylinder581  label="Cylinder676"
  Angle = 360
  AttacherType = Attacher::AttachEngine3D
  Height = 10
  Placement = pos=(26.5,-17,25) rot=(1,0,0;2.02458rad)
  Radius = 1.25
FEATURE [Part::MultiFuse] Fusion493
  Placement = pos=(48.5,133,62.6) rot=(0,1,0;3.14159rad)
  Refine = true
  Shapes = -> [Cylinder580,Cylinder581]
FEATURE [Part::Cylinder] Cylinder582  label="Cylinder677"
  Angle = 360
  AttacherType = Attacher::AttachEngine3D
  Height = 10
  Placement = pos=(28,-14,22) rot=(1,0,0;2.58309rad)
  Radius = 1.25
FEATURE [Part::Cylinder] Cylinder583  label="Cylinder678"
  Angle = 360
  AttacherType = Attacher::AttachEngine3D
  Height = 10
  Placement = pos=(30.5,0,14) rot=(1,0,0;2.58309rad)
  Radius = 1.25
FEATURE [Part::MultiFuse] Fusion494
  Placement = pos=(0,-1,0) rot=(0,0,1;0rad)
  Refine = true
  Shapes = -> [Cylinder582,Cylinder583]
FEATURE [Part::Cylinder] Cylinder584  label="Cylinder679"
  Angle = 360
  AttacherType = Attacher::AttachEngine3D
  Height = 10
  Placement = pos=(30.5,0,14) rot=(1,0,0;2.58309rad)
  Radius = 1.25
FEATURE [Part::Cylinder] Cylinder585  label="Cylinder680"
  Angle = 360
  AttacherType = Attacher::AttachEngine3D
  Height = 10
  Placement = pos=(28,-14,22) rot=(1,0,0;2.58309rad)
  Radius = 1.25
FEATURE [Part::MultiFuse] Fusion495
  Placement = pos=(58.5,99,27.3) rot=(0,1,0;3.14159rad)
  Refine = true
  Shapes = -> [Cylinder585,Cylinder584]
FEATURE [Part::Cylinder] Cylinder586  label="Cylinder681"
  Angle = 360
  AttacherType = Attacher::AttachEngine3D
  Height = 10
  Placement = pos=(31,18,1) rot=(0,0,1;0rad)
  Radius = 1.25
FEATURE [Part::Cylinder] Cylinder587  label="Cylinder682"
  Angle = 360
  AttacherType = Attacher::AttachEngine3D
  Height = 10
  Placement = pos=(31,62,1) rot=(0,0,1;0rad)
  Radius = 1.25
FEATURE [Part::MultiFuse] Fusion496
  Refine = true
  Shapes = -> [Cylinder574,Fusion495,Cylinder586,Fusion494,Cylinder575,Fusion492,Cylinder576,Cylinder577,Fusion493,Cylinder587]
FEATURE [Part::Cut] Cut008  label="front-end"
  Base = -> Cut368
  Refine = true
  Tool = -> Fusion496
FEATURE [Part::Box] Box369
  AttacherType = Attacher::AttachEngine3D
  Height = 16
  Length = 45
  Placement = pos=(-42.3,-47,90) rot=(0,0,1;0rad)
  Width = 174
FEATURE [Part::Box] Box370
  AttacherType = Attacher::AttachEngine3D
  Height = 10
  Length = 45
  Placement = pos=(-42.3,-37,87) rot=(0,0,1;0rad)
  Width = 37
FEATURE [Part::Box] Box371
  AttacherType = Attacher::AttachEngine3D
  Height = 10
  Length = 45
  Placement = pos=(-42.3,80,87) rot=(0,0,1;0rad)
  Width = 37
FEATURE [Part::Box] Box372
  AttacherType = Attacher::AttachEngine3D
  Height = 10
  Length = 45
  Placement = pos=(-42.3,10,87) rot=(0,0,1;0rad)
  Width = 60
FEATURE [Part::Box] Box373
  AttacherType = Attacher::AttachEngine3D
  Height = 14
  Length = 45
  Placement = pos=(-60.3,-45,83) rot=(0,0,1;0rad)
  Width = 170
FEATURE [Part::Box] Box374
  AttacherType = Attacher::AttachEngine3D
  Height = 11
  Length = 50
  Placement = pos=(-45.3,115,87) rot=(0,1,0;0.15708rad)
  Width = 12
FEATURE [Part::Box] Box375
  AttacherType = Attacher::AttachEngine3D
  Height = 11
  Length = 50
  Placement = pos=(-45.3,-47,87) rot=(0,1,0;0.15708rad)
  Width = 12
FEATURE [Part::Cylinder] Cylinder588  label="Cylinder683"
  Angle = 360
  AttacherType = Attacher::AttachEngine3D
  Height = 20
  Placement = pos=(-7,75,89) rot=(0,0,1;0rad)
  Radius = 1.6
FEATURE [Part::Cylinder] Cylinder589  label="Cylinder684"
  Angle = 360
  AttacherType = Attacher::AttachEngine3D
  Height = 20
  Placement = pos=(-7,5,89) rot=(0,0,1;0rad)
  Radius = 1.6
FEATURE [Part::Cylinder] Cylinder590  label="Cylinder685"
  Angle = 360
  AttacherType = Attacher::AttachEngine3D
  Height = 10
  Placement = pos=(-7,-20,95) rot=(0,1,0;1.5708rad)
  Radius = 1.25
FEATURE [Part::Cylinder] Cylinder591  label="Cylinder686"
  Angle = 360
  AttacherType = Attacher::AttachEngine3D
  Height = 10
  Placement = pos=(-7,40,95) rot=(0,1,0;1.5708rad)
  Radius = 1.25
FEATURE [Part::Cylinder] Cylinder592  label="Cylinder687"
  Angle = 360
  AttacherType = Attacher::AttachEngine3D
  Height = 10
  Placement = pos=(-7,100,95) rot=(0,1,0;1.5708rad)
  Radius = 1.25
FEATURE [Part::Cylinder] Cylinder593  label="Cylinder688"
  Angle = 360
  AttacherType = Attacher::AttachEngine3D
  Height = 3
  Placement = pos=(-7,75,103) rot=(0,0,1;0rad)
  Radius = 3.2
FEATURE [Part::Cylinder] Cylinder594  label="Cylinder689"
  Angle = 360
  AttacherType = Attacher::AttachEngine3D
  Height = 3
  Placement = pos=(-7,5,103) rot=(0,0,1;0rad)
  Radius = 3.2
FEATURE [Part::MultiFuse] Fusion497
  Refine = true
  Shapes = -> [Cylinder588,Cylinder594,Cylinder593,Cylinder589,Cylinder592,Cylinder590,Cylinder591]
FEATURE [Part::Box] Box376
  AttacherType = Attacher::AttachEngine3D
  Height = 6
  Length = 10
  Placement = pos=(0,-38,100) rot=(0,0,1;0rad)
  Width = 156
FEATURE [Part::Cylinder] Cylinder595  label="Cylinder690"
  Angle = 360
  AttacherType = Attacher::AttachEngine3D
  Height = 6
  Placement = pos=(-4.3,-20,95) rot=(0,1,0;1.5708rad)
  Radius = 3
FEATURE [Part::Cylinder] Cylinder596  label="Cylinder691"
  Angle = 360
  AttacherType = Attacher::AttachEngine3D
  Height = 10
  Placement = pos=(-7.3,-20,95) rot=(0,1,0;1.5708rad)
  Radius = 1.25
FEATURE [Part::Cut] Cut369
  Base = -> Cylinder595
  Refine = true
  Tool = -> Cylinder596
FEATURE [Part::Cylinder] Cylinder597  label="Cylinder692"
  Angle = 360
  AttacherType = Attacher::AttachEngine3D
  Height = 10
  Placement = pos=(-7.3,-20,95) rot=(0,1,0;1.5708rad)
  Radius = 1.25
FEATURE [Part::Cylinder] Cylinder598  label="Cylinder693"
  Angle = 360
  AttacherType = Attacher::AttachEngine3D
  Height = 6
  Placement = pos=(-4.3,-20,95) rot=(0,1,0;1.5708rad)
  Radius = 3
FEATURE [Part::Cut] Cut013
  Base = -> Cylinder598
  Placement = pos=(0,60,0) rot=(0,0,1;0rad)
  Refine = true
  Tool = -> Cylinder597
FEATURE [Part::Cylinder] Cylinder599  label="Cylinder694"
  Angle = 360
  AttacherType = Attacher::AttachEngine3D
  Height = 10
  Placement = pos=(-7.3,-20,95) rot=(0,1,0;1.5708rad)
  Radius = 1.25
FEATURE [Part::Cylinder] Cylinder600  label="Cylinder695"
  Angle = 360
  AttacherType = Attacher::AttachEngine3D
  Height = 6
  Placement = pos=(-4.3,-20,95) rot=(0,1,0;1.5708rad)
  Radius = 3
FEATURE [Part::Cut] Cut014
  Base = -> Cylinder600
  Placement = pos=(0,120,0) rot=(0,0,1;0rad)
  Refine = true
  Tool = -> Cylinder599
FEATURE [Part::MultiFuse] Fusion498
  Refine = true
  Shapes = -> [Cut369,Cut014,Cut013]
FEATURE [Part::MultiFuse] Fusion499
  Refine = true
  Shapes = -> [Box352,Box358,Box351]
FEATURE [Part::MultiFuse] Fusion500
  Refine = true
  Shapes = -> [Box353,Box355,Box354]
FEATURE [Part::Mirroring] Part__Mirroring016001002  label="Fusion029 (Mirror #1)"
  Base = (0,0,0)
  Normal = (0,0,1)
  Placement = pos=(0,80,0) rot=(0,0,1;0rad)
  Source = -> Fusion500
FEATURE [Part::MultiFuse] Fusion501
  Refine = true
  Shapes = -> [Box357,Part__Mirroring016001002,Fusion499]
FEATURE [Part::Cut] Cut370
  Base = -> Fusion501
  Refine = true
  Tool = -> Extrude001
FEATURE [Part::Box] Box377  label="Cube423"
  AttacherType = Attacher::AttachEngine3D
  Height = 100
  Length = 40
  Placement = pos=(510,-41,0) rot=(0,0,1;0rad)
  Width = 162
FEATURE [Part::Box] Box378  label="Cube424"
  AttacherType = Attacher::AttachEngine3D
  Height = 120
  Length = 25
  Placement = pos=(560,-41,0) rot=(0,-1,0;0.459022rad)
  Width = 162
FEATURE [Part::Box] Box379  label="Cube425"
  AttacherType = Attacher::AttachEngine3D
  Height = 100
  Length = 40
  Placement = pos=(520,-41,0) rot=(0,0,1;0rad)
  Width = 162
FEATURE [Part::Box] Box380  label="Cube426"
  AttacherType = Attacher::AttachEngine3D
  Height = 75
  Length = 40
  Placement = pos=(537,-41,55) rot=(0,0,1;0rad)
  Width = 162
FEATURE [Part::Box] Box381  label="Cube427"
  AttacherType = Attacher::AttachEngine3D
  Height = 100
  Length = 40
  Placement = pos=(520,-41,0) rot=(0,0,1;0rad)
  Width = 162
FEATURE [Part::Cut] Cut371
  Base = -> Box377
  Refine = true
  Tool = -> Box356
FEATURE [Part::Cut] Cut372
  Base = -> Box379
  Refine = true
  Tool = -> Box378
FEATURE [Part::MultiFuse] Fusion503
  Refine = true
  Shapes = -> [Cut371,Cut372]
FEATURE [Part::Cut] Cut373
  Base = -> Fusion503
  Refine = true
  Tool = -> Box380
FEATURE [Part::Cut] Cut374
  Base = -> Box381
  Refine = true
  Tool = -> Cut373
FEATURE [Part::Feature] Face
  shape: bbox 2e-07 x 176 x 110 mm, 1 faces, 0 solids (baked)
FEATURE [Part::Extrusion] Extrude
  Base = -> Face
  Dir = (60,0,0)
  DirMode = 0
  FaceMakerClass = Part::FaceMakerExtrusion
  LengthFwd = 0
  LengthRev = 0
  Solid = false
  Symmetric = false
FEATURE [Part::Box] Box382  label="Cube428"
  AttacherType = Attacher::AttachEngine3D
  Height = 120
  Length = 37
  Placement = pos=(620,-50,-4) rot=(0,-1,0;0.261799rad)
  Width = 160
FEATURE [Part::Box] Box383  label="Cube429"
  AttacherType = Attacher::AttachEngine3D
  Height = 120
  Length = 37.35
  Placement = pos=(562.94,-50,-10) rot=(0,-1,0;0.261799rad)
  Width = 160
FEATURE [Part::Feature] Face005
  shape: bbox 2e-07 x 176 x 110 mm, 1 faces, 0 solids (baked)
FEATURE [Part::Extrusion] Extrude004
  Base = -> Face005
  Dir = (60,0,0)
  DirMode = 0
  FaceMakerClass = Part::FaceMakerExtrusion
  LengthFwd = 0
  LengthRev = 0
  Placement = pos=(0,-7,0) rot=(0,0,1;0rad)
  Solid = false
  Symmetric = false
FEATURE [Part::Cut] Cut375
  Base = -> Cut370
  Refine = true
  Tool = -> Cut374
FEATURE [Part::MultiFuse] Fusion504  label="kipper-frame-METAL"
  Refine = true
  Shapes = -> [Box361,Box359]
FEATURE [Part::Box] Box384  label="Cube430"
  AttacherType = Attacher::AttachEngine3D
  Height = 120
  Length = 80
  Placement = pos=(538.2,-40,44) rot=(0,-1,0;0.261799rad)
  Width = 160
FEATURE [Part::Cut] Cut376  label="kipper-METAL"
  Base = -> Cut375
  Refine = true
  Tool = -> Box384
FEATURE [Part::Box] Box385  label="Cube431"
  AttacherType = Attacher::AttachEngine3D
  Height = 15
  Length = 475
  Placement = pos=(0,-40,89) rot=(0,0,1;0rad)
  Width = 8
FEATURE [Part::Cut] Cut377
  Base = -> Extrude004
  Placement = pos=(3,0,0) rot=(0,0,1;0rad)
  Refine = true
  Tool = -> Extrude
FEATURE [Part::Cylinder] Cylinder601  label="Cylinder696"
  Angle = 360
  AttacherType = Attacher::AttachEngine3D
  Height = 1
  Placement = pos=(518,-37,100) rot=(1,0,0;1.5708rad)
  Radius = 6
FEATURE [Part::Cylinder] Cylinder602  label="Cylinder697"
  Angle = 360
  AttacherType = Attacher::AttachEngine3D
  Height = 1
  Placement = pos=(518,-37,100) rot=(1,0,0;1.5708rad)
  Radius = 2.5
FEATURE [Part::Cut] Cut378  label="kipper-closure-spacer-METAL"
  Base = -> Cylinder601
  Placement = pos=(-1,0,0) rot=(0,0,1;0rad)
  Refine = true
  Tool = -> Cylinder602
FEATURE [Part::Cylinder] Cylinder603  label="Cylinder698"
  Angle = 360
  AttacherType = Attacher::AttachEngine3D
  Height = 5
  Placement = pos=(516,-39,100) rot=(1,0,0;1.5708rad)
  Radius = 5.6
FEATURE [Part::Box] Box386  label="Cube432"
  AttacherType = Attacher::AttachEngine3D
  Height = 120
  Length = 47
  Placement = pos=(680,-50,-4) rot=(0,-1,0;0.261799rad)
  Width = 160
FEATURE [Part::Box] Box387  label="Cube433"
  AttacherType = Attacher::AttachEngine3D
  Height = 120
  Length = 37.35
  Placement = pos=(582.94,-50,-10) rot=(0,-1,0;0.261799rad)
  Width = 160
FEATURE [Part::MultiFuse] Fusion505
  Refine = true
  Shapes = -> [Box382,Box383]
FEATURE [Part::Box] Box388  label="Cube434"
  AttacherType = Attacher::AttachEngine3D
  Height = 8
  Length = 60
  Placement = pos=(563,-47,100) rot=(0,0,1;0rad)
  Width = 7
FEATURE [Part::MultiFuse] Fusion506
  Refine = true
  Shapes = -> [Cut377,Box388]
FEATURE [Part::Cut] Cut056
  Base = -> Fusion506
  Placement = pos=(-69,0,0) rot=(0,0,1;0rad)
  Refine = true
  Tool = -> Fusion505
FEATURE [Part::Box] Box389  label="Cube435"
  AttacherType = Attacher::AttachEngine3D
  Height = 50
  Length = 100
  Placement = pos=(566,-47,58) rot=(0,0,1;0rad)
  Width = 7
FEATURE [Part::MultiFuse] Fusion507
  Refine = true
  Shapes = -> [Box386,Box387]
FEATURE [Part::Cut] Cut379
  Base = -> Box389
  Placement = pos=(-129,0,0) rot=(0,0,1;0rad)
  Refine = true
  Tool = -> Fusion507
FEATURE [Part::Box] Box390  label="Cube436"
  AttacherType = Attacher::AttachEngine3D
  Height = 4
  Length = 100
  Placement = pos=(433,-40,104) rot=(0,0,1;0rad)
  Width = 1
FEATURE [Part::Box] Box391  label="Cube437"
  AttacherType = Attacher::AttachEngine3D
  Height = 120
  Length = 37.35
  Placement = pos=(453.94,-50,-10) rot=(0,-1,0;0.261799rad)
  Width = 160
FEATURE [Part::Box] Box392  label="Cube438"
  AttacherType = Attacher::AttachEngine3D
  Height = 120
  Length = 37
  Placement = pos=(551,-50,-4) rot=(0,-1,0;0.261799rad)
  Width = 160
FEATURE [Part::MultiFuse] Fusion508
  Refine = true
  Shapes = -> [Box391,Box392]
FEATURE [Part::Cut] Cut380
  Base = -> Box390
  Refine = true
  Tool = -> Fusion508
FEATURE [Part::MultiFuse] Fusion502
  Refine = true
  Shapes = -> [Cut056,Cut379,Cut380]
FEATURE [Part::Box] Box060  label="Cube439"
  AttacherType = Attacher::AttachEngine3D
  Height = 120
  Length = 37.35
  Placement = pos=(470.94,-50,-10) rot=(0,-1,0;0.261799rad)
  Width = 160
FEATURE [Part::Box] Box061  label="Cube440"
  AttacherType = Attacher::AttachEngine3D
  Height = 120
  Length = 37
  Placement = pos=(549,-50,-4) rot=(0,-1,0;0.261799rad)
  Width = 160
FEATURE [Part::Box] Box393  label="Cube441"
  AttacherType = Attacher::AttachEngine3D
  Height = 37
  Length = 64
  Placement = pos=(468,-49,68) rot=(0,0,1;0rad)
  Width = 5
FEATURE [Part::MultiFuse] Fusion509
  Refine = true
  Shapes = -> [Box060,Box061]
FEATURE [Part::Cut] Cut381
  Base = -> Box393
  Refine = true
  Tool = -> Fusion509
FEATURE [Part::Cylinder] Cylinder604  label="Cylinder699"
  Angle = 360
  AttacherType = Attacher::AttachEngine3D
  Height = 9
  Placement = pos=(519.3,-40,106) rot=(1,0,0;1.5708rad)
  Radius = 0.8
FEATURE [Part::Cylinder] Cylinder605  label="Cylinder700"
  Angle = 360
  AttacherType = Attacher::AttachEngine3D
  Height = 9
  Placement = pos=(531,-40,61) rot=(1,0,0;1.5708rad)
  Radius = 0.8
FEATURE [Part::Cylinder] Cylinder606  label="Cylinder701"
  Angle = 360
  AttacherType = Attacher::AttachEngine3D
  Height = 9
  Placement = pos=(519.3,-40,106) rot=(1,0,0;1.5708rad)
  Radius = 0.8
FEATURE [Part::Cylinder] Cylinder607  label="Cylinder702"
  Angle = 360
  AttacherType = Attacher::AttachEngine3D
  Height = 9
  Placement = pos=(531,-40,61) rot=(1,0,0;1.5708rad)
  Radius = 0.8
FEATURE [Part::Box] Box394  label="Cube442"
  AttacherType = Attacher::AttachEngine3D
  Height = 50
  Length = 76
  Placement = pos=(460,-49,58) rot=(0,0,1;0rad)
  Width = 3
FEATURE [Part::Box] Box395  label="Cube443"
  AttacherType = Attacher::AttachEngine3D
  Height = 120
  Length = 37.35
  Placement = pos=(453.94,-50,-10) rot=(0,-1,0;0.261799rad)
  Width = 160
FEATURE [Part::Box] Box396  label="Cube039"
  AttacherType = Attacher::AttachEngine3D
  Height = 120
  Length = 37
  Placement = pos=(551,-50,-4) rot=(0,-1,0;0.261799rad)
  Width = 160
FEATURE [Part::MultiFuse] Fusion510
  Refine = true
  Shapes = -> [Box395,Box396]
FEATURE [Part::Cut] Cut382
  Base = -> Box394
  Placement = pos=(0,-1,0) rot=(0,0,1;0rad)
  Refine = true
  Tool = -> Fusion510
FEATURE [Part::MultiFuse] Fusion511
  Refine = true
  Shapes = -> [Cylinder605,Cylinder604]
FEATURE [Part::MultiFuse] Fusion513
  Placement = pos=(-54,0,0) rot=(0,0,1;0rad)
  Refine = true
  Shapes = -> [Cylinder607,Cylinder606]
FEATURE [Part::MultiFuse] Fusion512
  Placement = pos=(0,-1,0) rot=(0,0,1;0rad)
  Refine = true
  Shapes = -> [Fusion513,Fusion511]
FEATURE [Part::Cut] Cut383
  Base = -> Cut382
  Refine = true
  Tool = -> Fusion512
FEATURE [Part::Fillet] Fillet010005
  Base = -> Cut383
  Edges = 3 edges r=2: [Edge10,Edge11,Edge14]
FEATURE [Part::Chamfer] Chamfer056
  Base = -> Fillet010005
  Edges = 1 edges r=3: [Edge20]
FEATURE [Part::Cylinder] Cylinder608  label="Cylinder703"
  Angle = 360
  AttacherType = Attacher::AttachEngine3D
  Height = 10
  Placement = pos=(471,-39,101) rot=(1,0,0;1.5708rad)
  Radius = 1.25
FEATURE [Part::Cylinder] Cylinder609  label="Cylinder704"
  Angle = 360
  AttacherType = Attacher::AttachEngine3D
  Height = 20
  Placement = pos=(520,-29,61) rot=(1,0,0;1.5708rad)
  Radius = 1.25
FEATURE [Part::Cylinder] Cylinder610  label="Cylinder705"
  Angle = 360
  AttacherType = Attacher::AttachEngine3D
  Height = 20
  Placement = pos=(534,-7.3072,22.5449) rot=(1,0,0;2.63545rad)
  Radius = 1.25
FEATURE [Part::MultiFuse] Fusion514
  Refine = true
  Shapes = -> [Cylinder608,Cylinder609,Cylinder610]
FEATURE [Part::Box] Box397  label="Cube040"
  AttacherType = Attacher::AttachEngine3D
  Height = 10
  Length = 475
  Placement = pos=(0,-53.1,85.5) rot=(-1,0,0;0.471239rad)
  Width = 10
FEATURE [Part::Box] Box398  label="Cube444"
  AttacherType = Attacher::AttachEngine3D
  Height = 15
  Length = 475
  Placement = pos=(0,-47,90) rot=(0,0,1;0rad)
  Width = 8
FEATURE [Part::Cut] Cut066
  Base = -> Box398
  Refine = true
  Tool = -> Box385
FEATURE [Part::Cut] Cut384
  Base = -> Cut066
  Placement = pos=(3,0,0) rot=(0,0,1;0rad)
  Refine = true
  Tool = -> Box397
FEATURE [Part::MultiFuse] Fusion515
  Refine = true
  Shapes = -> [Box060,Box061]
FEATURE [Part::Box] Box399  label="Cube445"
  AttacherType = Attacher::AttachEngine3D
  Height = 37
  Length = 64
  Placement = pos=(468,-49,68) rot=(0,0,1;0rad)
  Width = 5
FEATURE [Part::Cut] Cut385
  Base = -> Box399
  Refine = true
  Tool = -> Fusion515
FEATURE [Part::Cut] Cut386
  Base = -> Fusion502
  Refine = true
  Tool = -> Cut385
FEATURE [Part::Cut] Cut387
  Base = -> Cut386
  Refine = true
  Tool = -> Cylinder603
FEATURE [Part::Cut] Cut071
  Base = -> Cut387
  Refine = true
  Tool = -> Fusion514
FEATURE [Part::Cylinder] Cylinder611  label="Cylinder706"
  Angle = 360
  AttacherType = Attacher::AttachEngine3D
  Height = 9
  Placement = pos=(531,-40,61) rot=(1,0,0;1.5708rad)
  Radius = 0.8
FEATURE [Part::Cylinder] Cylinder612  label="Cylinder707"
  Angle = 360
  AttacherType = Attacher::AttachEngine3D
  Height = 3
  Placement = pos=(519.3,-44,106) rot=(1,0,0;1.5708rad)
  Radius = 2
FEATURE [Part::Cylinder] Cylinder613  label="Cylinder708"
  Angle = 360
  AttacherType = Attacher::AttachEngine3D
  Height = 9
  Placement = pos=(519.3,-40,106) rot=(1,0,0;1.5708rad)
  Radius = 0.8
FEATURE [Part::MultiFuse] Fusion516
  Refine = true
  Shapes = -> [Cylinder612,Cut071]
FEATURE [Part::Cylinder] Cylinder614  label="Cylinder709"
  Angle = 360
  AttacherType = Attacher::AttachEngine3D
  Height = 9
  Placement = pos=(531,-40,61) rot=(1,0,0;1.5708rad)
  Radius = 0.8
FEATURE [Part::Cylinder] Cylinder615  label="Cylinder710"
  Angle = 360
  AttacherType = Attacher::AttachEngine3D
  Height = 9
  Placement = pos=(519.3,-40,106) rot=(1,0,0;1.5708rad)
  Radius = 0.8
FEATURE [Part::MultiFuse] Fusion517
  Refine = true
  Shapes = -> [Cylinder611,Cylinder613]
FEATURE [Part::MultiFuse] Fusion518
  Placement = pos=(-54,0,0) rot=(0,0,1;0rad)
  Refine = true
  Shapes = -> [Cylinder614,Cylinder615]
FEATURE [Part::MultiFuse] Fusion519
  Refine = true
  Shapes = -> [Fusion517,Fusion518]
FEATURE [Part::Cut] Cut388
  Base = -> Fusion516
  Refine = true
  Tool = -> Fusion519
FEATURE [Part::Cut] Cut389  label="right-back-door-mech-cover_"
  Base = -> Chamfer056
  Refine = true
  Tool = -> Cut381
FEATURE [Part::Fillet] Fillet010006
  Base = -> Cut388
  Edges = 2 edges r=2: [Edge32,Edge35]
FEATURE [Part::Chamfer] Chamfer057  label="right-back-door-mech_"
  Base = -> Fillet010006
  Edges = 1 edges r=3: [Edge23]
FEATURE [Part::MultiFuse] Fusion520
  Placement = pos=(0,0,3) rot=(0,0,1;0rad)
  Refine = true
  Shapes = -> [Box374,Box375]
FEATURE [Part::MultiFuse] Fusion521
  Placement = pos=(-16,0,0) rot=(0,1,0;0.15708rad)
  Refine = true
  Shapes = -> [Box370,Box373,Box372,Box371]
FEATURE [Part::Cut] Cut390
  Base = -> Box369
  Refine = true
  Tool = -> Fusion521
FEATURE [Part::Cut] Cut391
  Base = -> Cut390
  Refine = true
  Tool = -> Fusion520
FEATURE [Part::MultiFuse] Fusion522
  Refine = true
  Shapes = -> [Box376,Cut391]
FEATURE [Part::MultiFuse] Fusion523
  Refine = true
  Shapes = -> [Fusion498,Fusion522]
FEATURE [Part::Cut] Cut392
  Base = -> Fusion523
  Refine = true
  Tool = -> Fusion497
FEATURE [Part::Box] Box400  label="Cube446"
  AttacherType = Attacher::AttachEngine3D
  Height = 12
  Length = 15
  Placement = pos=(-14,45,86) rot=(0,0,1;0rad)
  Width = 8
FEATURE [Part::Box] Box401  label="Cube447"
  AttacherType = Attacher::AttachEngine3D
  Height = 12
  Length = 15
  Placement = pos=(-14,27,86) rot=(0,0,1;0rad)
  Width = 8
FEATURE [Part::MultiFuse] Fusion076
  Refine = true
  Shapes = -> [Box401,Box400]
FEATURE [Part::Fillet] Fillet010007
  Base = -> Fusion076
  Edges = 2 edges r=5: [Edge4,Edge16]
FEATURE [Part::Fillet] Fillet010008
  Base = -> Fillet010007
  Edges = 2 edges r=5: [Edge15,Edge30]
FEATURE [Part::Cylinder] Cylinder616  label="Cylinder711"
  Angle = 360
  AttacherType = Attacher::AttachEngine3D
  Height = 30
  Placement = pos=(-6.5,55,90) rot=(1,0,0;1.5708rad)
  Radius = 2.6
FEATURE [Part::Cut] Cut393
  Base = -> Fillet010008
  Placement = pos=(-19,0,0) rot=(0,1,0;0.15708rad)
  Refine = true
  Tool = -> Cylinder616
FEATURE [Part::MultiFuse] Fusion077  label="cab-protection"
  Refine = true
  Shapes = -> [Cut393,Cut392]
FEATURE [Part::Chamfer] Chamfer058
  Base = -> Fillet010005
  Edges = 1 edges r=3: [Edge20]
FEATURE [Part::Cut] Cut394
  Base = -> Box393
  Refine = true
  Tool = -> Fusion509
FEATURE [Part::Cut] Cut395  label="left-back-door-mech-cover"
  Base = -> Chamfer058
  Refine = true
  Tool = -> Cut394
FEATURE [Part::Fillet] Fillet010009
  Base = -> Cut388
  Edges = 2 edges r=2: [Edge32,Edge35]
FEATURE [Part::Chamfer] Chamfer059  label="left-back-door-mech"
  Base = -> Fillet010009
  Edges = 1 edges r=3: [Edge23]
FEATURE [Part::Mirroring] Part__Mirroring016001003  label="right-back-door-mech"
  Base = (0,0,0)
  Normal = (0,0,1)
  Placement = pos=(0,80,0) rot=(0,0,1;0rad)
  Source = -> Chamfer057
FEATURE [Part::Mirroring] Part__Mirroring016001004  label="right-back-door-mech-cover"
  Base = (0,0,0)
  Normal = (0,0,1)
  Placement = pos=(0,80,0) rot=(0,0,1;0rad)
  Source = -> Cut389
FEATURE [Part::Box] Box402  label="Cube448"
  AttacherType = Attacher::AttachEngine3D
  Height = 120
  Length = 37
  Placement = pos=(502.2,-50,-4) rot=(0,-1,0;0.261799rad)
  Width = 160
FEATURE [Part::Cut] Cut396
  Base = -> Cut384
  Refine = true
  Tool = -> Box402
FEATURE [Part::Cut] Cut398
  Base = -> Cut066
  Placement = pos=(3,0,0) rot=(0,0,1;0rad)
  Refine = true
  Tool = -> Box397
FEATURE [Part::Box] Box403  label="Cube449"
  AttacherType = Attacher::AttachEngine3D
  Height = 120
  Length = 37
  Placement = pos=(502.2,-50,-4) rot=(0,-1,0;0.261799rad)
  Width = 160
FEATURE [Part::Cut] Cut397
  Base = -> Cut398
  Refine = true
  Tool = -> Box403
FEATURE [Part::Box] Box404  label="Cube450"
  AttacherType = Attacher::AttachEngine3D
  Height = 15
  Length = 237
  Placement = pos=(3,-47,90) rot=(0,0,1;0rad)
  Width = 8
FEATURE [Part::Box] Box405  label="Cube451"
  AttacherType = Attacher::AttachEngine3D
  Height = 15
  Length = 238
  Placement = pos=(240,-47,90) rot=(0,0,1;0rad)
  Width = 8
FEATURE [Part::Cut] Cut399
  Base = -> Cut396
  Refine = true
  Tool = -> Box404
FEATURE [Part::Cut] Cut400
  Base = -> Cut397
  Refine = true
  Tool = -> Box405
FEATURE [Part::Cylinder] Cylinder617  label="Cylinder712"
  Angle = 360
  AttacherType = Attacher::AttachEngine3D
  Height = 10
  Placement = pos=(7,-33,95) rot=(1,0,0;1.5708rad)
  Radius = 3.25
FEATURE [Part::Cut] Cut401
  Base = -> Cut400
  Refine = true
  Tool = -> Cylinder617
FEATURE [Part::Cylinder] Cylinder618  label="Cylinder713"
  Angle = 360
  AttacherType = Attacher::AttachEngine3D
  Height = 6
  Placement = pos=(471,-40,101) rot=(1,0,0;1.5708rad)
  Radius = 1.25
FEATURE [Part::Box] Box406  label="Cube452"
  AttacherType = Attacher::AttachEngine3D
  Height = 9.4
  Length = 4.8
  Placement = pos=(235.2,-42.8,94.2) rot=(0,0,1;0rad)
  Width = 2.8
FEATURE [Part::Box] Box407  label="Cube050"
  AttacherType = Attacher::AttachEngine3D
  Height = 10.2
  Length = 5.1
  Placement = pos=(234.9,-43.1,93.9) rot=(0,0,1;0rad)
  Width = 3.1
FEATURE [Part::Cylinder] Cylinder619  label="Cylinder714"
  Angle = 360
  AttacherType = Attacher::AttachEngine3D
  Height = 6
  Placement = pos=(15,-40,101) rot=(1,0,0;1.5708rad)
  Radius = 1.25
FEATURE [Part::Cylinder] Cylinder620  label="Cylinder715"
  Angle = 360
  AttacherType = Attacher::AttachEngine3D
  Height = 6
  Placement = pos=(237.5,-40,101) rot=(1,0,0;1.5708rad)
  Radius = 1.6
FEATURE [Part::Cylinder] Cylinder621  label="Cylinder716"
  Angle = 360
  AttacherType = Attacher::AttachEngine3D
  Height = 6
  Placement = pos=(237.5,-40,101) rot=(1,0,0;1.5708rad)
  Radius = 1.25
FEATURE [Part::MultiFuse] Fusion524
  Refine = true
  Shapes = -> [Cut399,Box406]
FEATURE [Part::MultiFuse] Fusion525
  Refine = true
  Shapes = -> [Cylinder618,Cylinder620]
FEATURE [Part::Cut] Cut402  label="right-border-02_"
  Base = -> Fusion524
  Refine = true
  Tool = -> Fusion525
FEATURE [Part::Cut] Cut403
  Base = -> Cut401
  Refine = true
  Tool = -> Box407
FEATURE [Part::MultiFuse] Fusion526
  Refine = true
  Shapes = -> [Cylinder619,Cylinder621]
FEATURE [Part::Cut] Cut404  label="left-border-01__"
  Base = -> Cut403
  Refine = true
  Tool = -> Fusion526
FEATURE [Part::Cylinder] Cylinder622  label="Cylinder717"
  Angle = 360
  AttacherType = Attacher::AttachEngine3D
  Height = 10
  Placement = pos=(10,-33,95) rot=(1,0,0;1.5708rad)
  Radius = 3.25
FEATURE [Part::Box] Box408  label="Cube453"
  AttacherType = Attacher::AttachEngine3D
  Height = 6.5
  Length = 3
  Placement = pos=(7,-43,91.75) rot=(0,0,1;0rad)
  Width = 10
FEATURE [Part::MultiFuse] Fusion527
  Refine = true
  Shapes = -> [Cylinder622,Box408]
FEATURE [Part::Cut] Cut405  label="right-border-01_"
  Base = -> Cut404
  Refine = true
  Tool = -> Fusion527
FEATURE [Part::MultiFuse] Fusion528
  Refine = true
  Shapes = -> [Cut399,Box406]
FEATURE [Part::MultiFuse] Fusion529
  Refine = true
  Shapes = -> [Cylinder618,Cylinder620]
FEATURE [Part::Cut] Cut406  label="left-border-02"
  Base = -> Fusion528
  Refine = true
  Tool = -> Fusion529
FEATURE [Part::MultiFuse] Fusion530
  Refine = true
  Shapes = -> [Cylinder622,Box408]
FEATURE [Part::Cut] Cut407  label="left-border-01__001"
  Base = -> Cut403
  Refine = true
  Tool = -> Fusion526
FEATURE [Part::Cut] Cut408  label="left-border-01"
  Base = -> Cut407
  Refine = true
  Tool = -> Fusion530
FEATURE [Part::Mirroring] Part__Mirroring003  label="right-border-02"
  Base = (0,0,0)
  Normal = (0,0,1)
  Placement = pos=(0,80,0) rot=(0,0,1;0rad)
  Source = -> Cut402
FEATURE [Part::Mirroring] Part__Mirroring004  label="right-border-01"
  Base = (0,0,0)
  Normal = (0,0,1)
  Placement = pos=(0,80,0) rot=(0,0,1;0rad)
  Source = -> Cut405
FEATURE [Part::Box] Box080  label="Cube454"
  AttacherType = Attacher::AttachEngine3D
  Height = 15
  Length = 5
  Placement = pos=(536,30,2) rot=(0,-1,0;0.261799rad)
  Width = 20
FEATURE [Part::Box] Box081  label="Cube053"
  AttacherType = Attacher::AttachEngine3D
  Height = 4
  Length = 16
  Placement = pos=(524,30,2) rot=(0,0,1;0rad)
  Width = 20
FEATURE [Part::Box] Box082  label="Cube455"
  AttacherType = Attacher::AttachEngine3D
  Height = 20
  Length = 3
  Placement = pos=(540,28,2) rot=(0,-1,0;0.261799rad)
  Width = 24
FEATURE [Part::Cylinder] Cylinder623  label="Cylinder718"
  Angle = 360
  AttacherType = Attacher::AttachEngine3D
  Height = 20
  Placement = pos=(529,40,-10) rot=(0,0,1;0rad)
  Radius = 1.9
FEATURE [Part::Cylinder] Cylinder624  label="Cylinder719"
  Angle = 360
  AttacherType = Attacher::AttachEngine3D
  Height = 20
  Placement = pos=(532,35,7.5) rot=(0,1,0;1.309rad)
  Radius = 1.1
FEATURE [Part::Cylinder] Cylinder625  label="Cylinder720"
  Angle = 360
  AttacherType = Attacher::AttachEngine3D
  Height = 20
  Placement = pos=(532,45,7.5) rot=(0,1,0;1.309rad)
  Radius = 1.1
FEATURE [Part::MultiFuse] Fusion531
  Placement = pos=(0,0,4) rot=(0,0,1;0rad)
  Refine = true
  Shapes = -> [Cylinder625,Cylinder624]
FEATURE [Part::MultiFuse] Fusion095
  Refine = true
  Shapes = -> [Box081,Box080]
FEATURE [Part::Cut] Cut409
  Base = -> Fusion095
  Refine = true
  Tool = -> Fusion531
FEATURE [Part::Cut] Cut410
  Base = -> Cut409
  Refine = true
  Tool = -> Box082
FEATURE [Part::Cut] Cut411
  Base = -> Cut410
  Refine = true
  Tool = -> Cylinder623
FEATURE [Part::Fillet] Fillet010010
  Base = -> Cut411
  Edges = 2 edges r=5: [Edge1,Edge3]
FEATURE [Part::Fillet] Fillet010011
  Base = -> Fillet010010
  Edges = 1 edges r=3: [Edge7]
FEATURE [Part::Fillet] Fillet010012
  Base = -> Fillet010011
  Edges = 1 edges r=3: [Edge28]
FEATURE [Part::Fillet] Fillet023  label="rear-door-closure-lock"
  Base = -> Fillet010012
  Edges = 2 edges r=1.5: [Edge22,Edge31]
FEATURE [Part::Box] Box085  label="Cube456"
  AttacherType = Attacher::AttachEngine3D
  Height = 130
  Length = 30
  Placement = pos=(538.1,-38,-7) rot=(0,-1,0;0.261799rad)
  Width = 156
FEATURE [Part::Box] Box409  label="Cube457"
  AttacherType = Attacher::AttachEngine3D
  Height = 130
  Length = 40
  Placement = pos=(573,-38,-9) rot=(0,-1,0;0.261799rad)
  Width = 156
FEATURE [Part::Cylinder] Cylinder626  label="Cylinder721"
  Angle = 360
  AttacherType = Attacher::AttachEngine3D
  Height = 1
  Placement = pos=(518,-37,100) rot=(1,0,0;1.5708rad)
  Radius = 6.5
FEATURE [Part::Feature] Face009
  shape: bbox 2e-07 x 158.7 x 95.08 mm, 1 faces, 0 solids (baked)
FEATURE [Part::Cylinder] Cylinder627  label="Cylinder722"
  Angle = 360
  AttacherType = Attacher::AttachEngine3D
  Height = 1
  Placement = pos=(518,118,100) rot=(1,0,0;1.5708rad)
  Radius = 6.5
FEATURE [Part::Box] Box410  label="Cube458"
  AttacherType = Attacher::AttachEngine3D
  Height = 130
  Length = 40
  Placement = pos=(572,-38,1) rot=(0,-1,0;0.261799rad)
  Width = 156
FEATURE [Part::MultiFuse] Fusion533
  Placement = pos=(-4,0,-2) rot=(0,0,1;0rad)
  Refine = true
  Shapes = -> [Box085,Box410]
FEATURE [Part::Box] Box411  label="Cube459"
  AttacherType = Attacher::AttachEngine3D
  Height = 4
  Length = 50
  Placement = pos=(532,-38,100) rot=(0,0,1;0rad)
  Width = 156
FEATURE [Part::Box] Box412  label="Cube460"
  AttacherType = Attacher::AttachEngine3D
  Height = 95
  Length = 4
  Placement = pos=(545.64,36,3) rot=(0,-1,0;0.261799rad)
  Width = 8
FEATURE [Part::Feature] Face010
  shape: bbox 2e-07 x 171.6 x 107.8 mm, 1 faces, 0 solids (baked)
FEATURE [Part::Extrusion] Extrude011
  Base = -> Face010
  Dir = (50,0,0)
  DirMode = 0
  FaceMakerClass = Part::FaceMakerExtrusion
  LengthFwd = 0
  LengthRev = 0
  Placement = pos=(26,0,0) rot=(0,0,1;0rad)
  Solid = false
  Symmetric = false
FEATURE [Part::MultiFuse] Fusion532
  Refine = true
  Shapes = -> [Box411,Extrude011]
FEATURE [Part::MultiFuse] Fusion535
  Placement = pos=(-2,0,0) rot=(0,0,1;0rad)
  Refine = true
  Shapes = -> [Cylinder626,Cylinder627]
FEATURE [Part::Box] Box413  label="Cube461"
  AttacherType = Attacher::AttachEngine3D
  Height = 130
  Length = 30
  Placement = pos=(533.4,-38,-7) rot=(0,-1,0;0.261799rad)
  Width = 156
FEATURE [Part::MultiFuse] Fusion534
  Refine = true
  Shapes = -> [Box413,Box409]
FEATURE [Part::Cut] Cut412
  Base = -> Fusion532
  Placement = pos=(-20,0,0) rot=(0,0,1;0rad)
  Refine = true
  Tool = -> Fusion534
FEATURE [Part::Cylinder] Cylinder628  label="Cylinder723"
  Angle = 360
  AttacherType = Attacher::AttachEngine3D
  Height = 15
  Placement = pos=(516,117,100) rot=(1,0,0;1.5708rad)
  Radius = 2.5
FEATURE [Part::Extrusion] Extrude012
  Base = -> Face009
  Dir = (50,0,0)
  DirMode = 0
  FaceMakerClass = Part::FaceMakerExtrusion
  LengthFwd = 0
  LengthRev = 0
  Placement = pos=(27,0,0) rot=(0,0,1;0rad)
  Solid = false
  Symmetric = false
FEATURE [Part::Cut] Cut413
  Base = -> Extrude012
  Placement = pos=(-16,0,0) rot=(0,0,1;0rad)
  Refine = true
  Tool = -> Fusion533
FEATURE [Part::Cut] Cut414
  Base = -> Cut412
  Refine = true
  Tool = -> Cut413
FEATURE [Part::MultiFuse] Fusion536
  Placement = pos=(-2,0,0) rot=(0,0,1;0rad)
  Refine = true
  Shapes = -> [Cut414,Box412]
FEATURE [Part::Cut] Cut415
  Base = -> Fusion536
  Refine = true
  Tool = -> Fusion535
FEATURE [Part::Cylinder] Cylinder629  label="Cylinder724"
  Angle = 360
  AttacherType = Attacher::AttachEngine3D
  Height = 9
  Placement = pos=(532,35,7.5) rot=(0,1,0;1.309rad)
  Radius = 0.9
FEATURE [Part::Cylinder] Cylinder630  label="Cylinder725"
  Angle = 360
  AttacherType = Attacher::AttachEngine3D
  Height = 9
  Placement = pos=(532,45,7.5) rot=(0,1,0;1.309rad)
  Radius = 0.9
FEATURE [Part::MultiFuse] Fusion537
  Placement = pos=(0,0,4) rot=(0,0,1;0rad)
  Refine = true
  Shapes = -> [Cylinder630,Cylinder629]
FEATURE [Part::Cylinder] Cylinder631  label="Cylinder726"
  Angle = 360
  AttacherType = Attacher::AttachEngine3D
  Height = 9
  Placement = pos=(509,-34,102.5) rot=(0,1,0;1.309rad)
  Radius = 0.9
FEATURE [Part::Cut] Cut416
  Base = -> Cut415
  Refine = true
  Tool = -> Fusion537
FEATURE [Part::Box] Box414  label="Cube462"
  AttacherType = Attacher::AttachEngine3D
  Height = 8
  Length = 10
  Placement = pos=(511,-37,99) rot=(0,0,1;0rad)
  Width = 20
FEATURE [Part::Box] Box415  label="Cube463"
  AttacherType = Attacher::AttachEngine3D
  Height = 130
  Length = 40
  Placement = pos=(573,-38,-9) rot=(0,-1,0;0.261799rad)
  Width = 156
FEATURE [Part::Box] Box416  label="Cube464"
  AttacherType = Attacher::AttachEngine3D
  Height = 130
  Length = 30
  Placement = pos=(533.4,-38,-7) rot=(0,-1,0;0.261799rad)
  Width = 156
FEATURE [Part::MultiFuse] Fusion107
  Placement = pos=(-22,0,0) rot=(0,0,1;0rad)
  Refine = true
  Shapes = -> [Box416,Box415]
FEATURE [Part::Chamfer] Chamfer060
  Base = -> Box414
  Edges = 1 edges r=4: [Edge12]
FEATURE [Part::Box] Box417  label="Cube465"
  AttacherType = Attacher::AttachEngine3D
  Height = 8
  Length = 10
  Placement = pos=(511,97,99) rot=(0,0,1;0rad)
  Width = 20
FEATURE [Part::Chamfer] Chamfer061
  Base = -> Box417
  Edges = 1 edges r=4: [Edge10]
FEATURE [Part::MultiFuse] Fusion108
  Refine = true
  Shapes = -> [Chamfer060,Chamfer061]
FEATURE [Part::Cut] Cut417
  Base = -> Fusion108
  Refine = true
  Tool = -> Fusion107
FEATURE [Part::MultiFuse] Fusion538
  Refine = true
  Shapes = -> [Cut416,Cut417]
FEATURE [Part::Cylinder] Cylinder632  label="Cylinder727"
  Angle = 360
  AttacherType = Attacher::AttachEngine3D
  Height = 15
  Placement = pos=(516,-22,100) rot=(1,0,0;1.5708rad)
  Radius = 2.5
FEATURE [Part::MultiFuse] Fusion539
  Refine = true
  Shapes = -> [Cylinder632,Cylinder628]
FEATURE [Part::Cut] Cut418
  Base = -> Fusion538
  Refine = true
  Tool = -> Fusion539
FEATURE [Part::Cylinder] Cylinder633  label="Cylinder728"
  Angle = 360
  AttacherType = Attacher::AttachEngine3D
  Height = 9
  Placement = pos=(509,-21,102.5) rot=(0,1,0;1.309rad)
  Radius = 0.9
FEATURE [Part::MultiFuse] Fusion540
  Refine = true
  Shapes = -> [Cylinder633,Cylinder631]
FEATURE [Part::Cylinder] Cylinder634  label="Cylinder729"
  Angle = 360
  AttacherType = Attacher::AttachEngine3D
  Height = 9
  Placement = pos=(509,-34,102.5) rot=(0,1,0;1.309rad)
  Radius = 0.9
FEATURE [Part::Cylinder] Cylinder635  label="Cylinder730"
  Angle = 360
  AttacherType = Attacher::AttachEngine3D
  Height = 9
  Placement = pos=(509,-21,102.5) rot=(0,1,0;1.309rad)
  Radius = 0.9
FEATURE [Part::MultiFuse] Fusion541
  Placement = pos=(2,0,-9) rot=(0,0,1;0rad)
  Refine = true
  Shapes = -> [Cylinder635,Cylinder634]
FEATURE [Part::MultiFuse] Fusion542
  Refine = true
  Shapes = -> [Fusion541,Fusion540]
FEATURE [Part::Cylinder] Cylinder636  label="Cylinder731"
  Angle = 360
  AttacherType = Attacher::AttachEngine3D
  Height = 9
  Placement = pos=(509,-21,102.5) rot=(0,1,0;1.309rad)
  Radius = 0.9
FEATURE [Part::Cylinder] Cylinder637  label="Cylinder732"
  Angle = 360
  AttacherType = Attacher::AttachEngine3D
  Height = 9
  Placement = pos=(509,-34,102.5) rot=(0,1,0;1.309rad)
  Radius = 0.9
FEATURE [Part::Cylinder] Cylinder638  label="Cylinder733"
  Angle = 360
  AttacherType = Attacher::AttachEngine3D
  Height = 9
  Placement = pos=(509,-34,102.5) rot=(0,1,0;1.309rad)
  Radius = 0.9
FEATURE [Part::Cylinder] Cylinder639  label="Cylinder734"
  Angle = 360
  AttacherType = Attacher::AttachEngine3D
  Height = 9
  Placement = pos=(509,-21,102.5) rot=(0,1,0;1.309rad)
  Radius = 0.9
FEATURE [Part::MultiFuse] Fusion543
  Placement = pos=(2,0,-9) rot=(0,0,1;0rad)
  Refine = true
  Shapes = -> [Cylinder636,Cylinder637]
FEATURE [Part::MultiFuse] Fusion544
  Refine = true
  Shapes = -> [Cylinder639,Cylinder638]
FEATURE [Part::MultiFuse] Fusion545
  Placement = pos=(0,135,0) rot=(0,0,1;0rad)
  Refine = true
  Shapes = -> [Fusion543,Fusion544]
FEATURE [Part::MultiFuse] Fusion546
  Refine = true
  Shapes = -> [Fusion545,Fusion542]
FEATURE [Part::Cut] Cut419  label="door-rear"
  Base = -> Cut418
  Refine = true
  Tool = -> Fusion546
FEATURE [Part::Box] Box418  label="Cube466"
  AttacherType = Attacher::AttachEngine3D
  Height = 130
  Length = 40
  Placement = pos=(569,-38,-9) rot=(0,-1,0;0.261799rad)
  Width = 156
FEATURE [Part::Box] Box419  label="Cube071"
  AttacherType = Attacher::AttachEngine3D
  Height = 130
  Length = 30
  Placement = pos=(533.4,-38,-7) rot=(0,-1,0;0.261799rad)
  Width = 156
FEATURE [Part::MultiFuse] Fusion547
  Placement = pos=(-22,0,0) rot=(0,0,1;0rad)
  Refine = true
  Shapes = -> [Box419,Box418]
FEATURE [Part::Box] Box420  label="Cube072"
  AttacherType = Attacher::AttachEngine3D
  Height = 16
  Length = 10
  Placement = pos=(511,-37,98) rot=(0,0,1;0rad)
  Width = 20
FEATURE [Part::Chamfer] Chamfer062
  Base = -> Box420
  Edges = 1 edges r=4: [Edge12]
  Placement = pos=(0,0,-7) rot=(0,0,1;0rad)
FEATURE [Part::Cut] Cut420
  Base = -> Chamfer062
  Placement = pos=(-4,0,0) rot=(0,0,1;0rad)
  Refine = true
  Tool = -> Fusion547
FEATURE [Part::Cylinder] Cylinder640  label="Cylinder735"
  Angle = 360
  AttacherType = Attacher::AttachEngine3D
  Height = 9
  Placement = pos=(509,-21,102.5) rot=(0,1,0;1.309rad)
  Radius = 0.9
FEATURE [Part::Cylinder] Cylinder641  label="Cylinder736"
  Angle = 360
  AttacherType = Attacher::AttachEngine3D
  Height = 9
  Placement = pos=(509,-34,102.5) rot=(0,1,0;1.309rad)
  Radius = 0.9
FEATURE [Part::Cylinder] Cylinder642  label="Cylinder737"
  Angle = 360
  AttacherType = Attacher::AttachEngine3D
  Height = 9
  Placement = pos=(509,-34,102.5) rot=(0,1,0;1.309rad)
  Radius = 0.9
FEATURE [Part::Cylinder] Cylinder643  label="Cylinder738"
  Angle = 360
  AttacherType = Attacher::AttachEngine3D
  Height = 9
  Placement = pos=(509,-21,102.5) rot=(0,1,0;1.309rad)
  Radius = 0.9
FEATURE [Part::MultiFuse] Fusion548
  Placement = pos=(2,0,-9) rot=(0,0,1;0rad)
  Refine = true
  Shapes = -> [Cylinder640,Cylinder641]
FEATURE [Part::MultiFuse] Fusion549
  Refine = true
  Shapes = -> [Cylinder643,Cylinder642]
FEATURE [Part::MultiFuse] Fusion550
  Refine = true
  Shapes = -> [Fusion548,Fusion549]
FEATURE [Part::Cut] Cut421
  Base = -> Cut420
  Refine = true
  Tool = -> Fusion550
FEATURE [Part::Fillet] Fillet010013
  Base = -> Cut421
  Edges = 3 edges r=3: [Edge7,Edge15,Edge23]
FEATURE [Part::Chamfer] Chamfer063
  Base = -> Fillet010013
  Edges = 2 edges r=1: [Edge7,Edge8]
FEATURE [Part::Cylinder] Cylinder644  label="Cylinder739"
  Angle = 360
  AttacherType = Attacher::AttachEngine3D
  Height = 15
  Placement = pos=(516,-22,100) rot=(1,0,0;1.5708rad)
  Radius = 2.4
FEATURE [Part::Cut] Cut422
  Base = -> Chamfer063
  Refine = true
  Tool = -> Cylinder644
FEATURE [Part::Cylinder] Cylinder645  label="Cylinder740"
  Angle = 360
  AttacherType = Attacher::AttachEngine3D
  Height = 1
  Placement = pos=(509,-34,102.5) rot=(0,1,0;1.309rad)
  Radius = 2
FEATURE [Part::Cylinder] Cylinder646  label="Cylinder741"
  Angle = 360
  AttacherType = Attacher::AttachEngine3D
  Height = 1.4
  Placement = pos=(509,-21,102.5) rot=(0,1,0;1.309rad)
  Radius = 2
FEATURE [Part::Cylinder] Cylinder647  label="Cylinder742"
  Angle = 360
  AttacherType = Attacher::AttachEngine3D
  Height = 1
  Placement = pos=(509,-21,102.5) rot=(0,1,0;1.309rad)
  Radius = 2
FEATURE [Part::MultiFuse] Fusion551
  Refine = true
  Shapes = -> [Cylinder647,Cylinder645]
FEATURE [Part::Cylinder] Cylinder648  label="Cylinder743"
  Angle = 360
  AttacherType = Attacher::AttachEngine3D
  Height = 1.4
  Placement = pos=(509,-34,102.5) rot=(0,1,0;1.309rad)
  Radius = 2
FEATURE [Part::MultiFuse] Fusion553
  Placement = pos=(2,0,-9) rot=(0,0,1;0rad)
  Refine = true
  Shapes = -> [Cylinder646,Cylinder648]
FEATURE [Part::MultiFuse] Fusion552
  Refine = true
  Shapes = -> [Fusion553,Fusion551]
FEATURE [Part::Fillet] Fillet010014
  Base = -> Cut422
  Edges = 2 edges r=2: [Edge18,Edge20]
FEATURE [Part::Cut] Cut423  label="door-rear-bar-holder-left"
  Base = -> Fillet010014
  Refine = true
  Tool = -> Fusion552
FEATURE [Part::Cylinder] Cylinder649  label="Cylinder744"
  Angle = 360
  AttacherType = Attacher::AttachEngine3D
  Height = 15
  Placement = pos=(516,-22,100) rot=(1,0,0;1.5708rad)
  Radius = 2.4
FEATURE [Part::Cylinder] Cylinder650  label="Cylinder745"
  Angle = 360
  AttacherType = Attacher::AttachEngine3D
  Height = 1
  Placement = pos=(509,-21,102.5) rot=(0,1,0;1.309rad)
  Radius = 2
FEATURE [Part::Cylinder] Cylinder651  label="Cylinder746"
  Angle = 360
  AttacherType = Attacher::AttachEngine3D
  Height = 1.4
  Placement = pos=(509,-34,102.5) rot=(0,1,0;1.309rad)
  Radius = 2
FEATURE [Part::Cylinder] Cylinder652  label="Cylinder747"
  Angle = 360
  AttacherType = Attacher::AttachEngine3D
  Height = 1.4
  Placement = pos=(509,-21,102.5) rot=(0,1,0;1.309rad)
  Radius = 2
FEATURE [Part::Cylinder] Cylinder653  label="Cylinder748"
  Angle = 360
  AttacherType = Attacher::AttachEngine3D
  Height = 1
  Placement = pos=(509,-34,102.5) rot=(0,1,0;1.309rad)
  Radius = 2
FEATURE [Part::Cylinder] Cylinder654  label="Cylinder749"
  Angle = 360
  AttacherType = Attacher::AttachEngine3D
  Height = 9
  Placement = pos=(509,-34,102.5) rot=(0,1,0;1.309rad)
  Radius = 0.9
FEATURE [Part::Cylinder] Cylinder655  label="Cylinder750"
  Angle = 360
  AttacherType = Attacher::AttachEngine3D
  Height = 9
  Placement = pos=(509,-21,102.5) rot=(0,1,0;1.309rad)
  Radius = 0.9
FEATURE [Part::Box] Box421  label="Cube073"
  AttacherType = Attacher::AttachEngine3D
  Height = 130
  Length = 30
  Placement = pos=(533.4,-38,-7) rot=(0,-1,0;0.261799rad)
  Width = 156
FEATURE [Part::Box] Box422  label="Cube074"
  AttacherType = Attacher::AttachEngine3D
  Height = 16
  Length = 10
  Placement = pos=(511,-37,98) rot=(0,0,1;0rad)
  Width = 20
FEATURE [Part::Chamfer] Chamfer065
  Base = -> Box422
  Edges = 1 edges r=4: [Edge12]
  Placement = pos=(0,0,-7) rot=(0,0,1;0rad)
FEATURE [Part::Box] Box423  label="Cube075"
  AttacherType = Attacher::AttachEngine3D
  Height = 130
  Length = 40
  Placement = pos=(569,-38,-9) rot=(0,-1,0;0.261799rad)
  Width = 156
FEATURE [Part::MultiFuse] Fusion556
  Placement = pos=(-22,0,0) rot=(0,0,1;0rad)
  Refine = true
  Shapes = -> [Box421,Box423]
FEATURE [Part::Cut] Cut424
  Base = -> Chamfer065
  Placement = pos=(-4,0,0) rot=(0,0,1;0rad)
  Refine = true
  Tool = -> Fusion556
FEATURE [Part::Cylinder] Cylinder656  label="Cylinder751"
  Angle = 360
  AttacherType = Attacher::AttachEngine3D
  Height = 9
  Placement = pos=(509,-21,102.5) rot=(0,1,0;1.309rad)
  Radius = 0.9
FEATURE [Part::MultiFuse] Fusion554
  Refine = true
  Shapes = -> [Cylinder656,Cylinder654]
FEATURE [Part::Cylinder] Cylinder657  label="Cylinder752"
  Angle = 360
  AttacherType = Attacher::AttachEngine3D
  Height = 9
  Placement = pos=(509,-34,102.5) rot=(0,1,0;1.309rad)
  Radius = 0.9
FEATURE [Part::MultiFuse] Fusion557
  Placement = pos=(2,0,-9) rot=(0,0,1;0rad)
  Refine = true
  Shapes = -> [Cylinder655,Cylinder657]
FEATURE [Part::MultiFuse] Fusion555
  Refine = true
  Shapes = -> [Fusion557,Fusion554]
FEATURE [Part::Cut] Cut122
  Base = -> Cut424
  Refine = true
  Tool = -> Fusion555
FEATURE [Part::Fillet] Fillet010015
  Base = -> Cut122
  Edges = 3 edges r=3: [Edge7,Edge15,Edge23]
FEATURE [Part::Chamfer] Chamfer064
  Base = -> Fillet010015
  Edges = 2 edges r=1: [Edge7,Edge8]
FEATURE [Part::Cut] Cut123
  Base = -> Chamfer064
  Refine = true
  Tool = -> Cylinder649
FEATURE [Part::Fillet] Fillet010016
  Base = -> Cut123
  Edges = 2 edges r=2: [Edge18,Edge20]
FEATURE [Part::MultiFuse] Fusion559
  Refine = true
  Shapes = -> [Cylinder650,Cylinder653]
FEATURE [Part::MultiFuse] Fusion560
  Placement = pos=(2,0,-9) rot=(0,0,1;0rad)
  Refine = true
  Shapes = -> [Cylinder652,Cylinder651]
FEATURE [Part::MultiFuse] Fusion558
  Refine = true
  Shapes = -> [Fusion560,Fusion559]
FEATURE [Part::Cut] Cut425  label="door-rear-bar-holder-left_"
  Base = -> Fillet010016
  Refine = true
  Tool = -> Fusion558
FEATURE [Part::Mirroring] Part__Mirroring016001005  label="door-rear-bar-holder-right"
  Base = (0,0,0)
  Normal = (0,0,1)
  Placement = pos=(0,80,0) rot=(0,0,1;0rad)
  Source = -> Cut425
FEATURE [Part::Box] Box424  label="Cube076"
  AttacherType = Attacher::AttachEngine3D
  Height = 10
  Length = 18
  Placement = pos=(27,0,-10) rot=(0,0,1;0rad)
  Width = 10
FEATURE [Part::Box] Box425  label="Cube077"
  AttacherType = Attacher::AttachEngine3D
  Height = 10
  Length = 18
  Placement = pos=(27,71,-10) rot=(0,0,1;0rad)
  Width = 10
FEATURE [Part::Box] Box426  label="Cube078"
  AttacherType = Attacher::AttachEngine3D
  Height = 2
  Length = 18
  Placement = pos=(27,0,-2) rot=(0,0,1;0rad)
  Width = 81
FEATURE [Part::MultiFuse] Fusion561
  Refine = true
  Shapes = -> [Box424,Box426,Box425]
FEATURE [Part::Box] Box107  label="Cube079"
  AttacherType = Attacher::AttachEngine3D
  Height = 10
  Length = 3
  Width = 6
FEATURE [Part::Fillet] Fillet010017
  Base = -> Box107
  Edges = 4 edges r=1.49: [Edge1,Edge3,Edge5,Edge7]
  Placement = pos=(31,15.5,-6) rot=(0,0,1;0rad)
FEATURE [Part::Box] Box108  label="Cube080"
  AttacherType = Attacher::AttachEngine3D
  Height = 10
  Length = 3
  Width = 6
FEATURE [Part::Fillet] Fillet010018
  Base = -> Box108
  Edges = 4 edges r=1.49: [Edge1,Edge3,Edge5,Edge7]
  Placement = pos=(31,59.5,-6) rot=(0,0,1;0rad)
FEATURE [Part::MultiFuse] Fusion562
  Refine = true
  Shapes = -> [Fillet010017,Fillet010018]
FEATURE [Part::Cut] Cut426
  Base = -> Fusion561
  Refine = true
  Tool = -> Fusion562
FEATURE [Part::Chamfer] Chamfer066  label="kipper-frame-missing-part"
  Base = -> Cut426
  Edges = 2 edges r=1.99: [Edge10,Edge14]
  Placement = pos=(0,-0.5,0) rot=(0,0,1;0rad)
FEATURE [Part::Compound] Compound002  label="kipper-complete"
  Links = -> [Cut008,Fusion504,Cut376,Cut378,Fusion077,Cut395,Chamfer059,Part__Mirroring016001003,Part__Mirroring016001004,Cut406,Cut408,Part__Mirroring003,Part__Mirroring004,Fillet023,Cut419,Cut423,Part__Mirroring016001005,Chamfer066]
  Placement = pos=(58,0,30) rot=(0,0,1;0rad)
FEATURE [App::DocumentObjectGroup] Group008  label="Kipper"
  Group = -> [Compound002]
